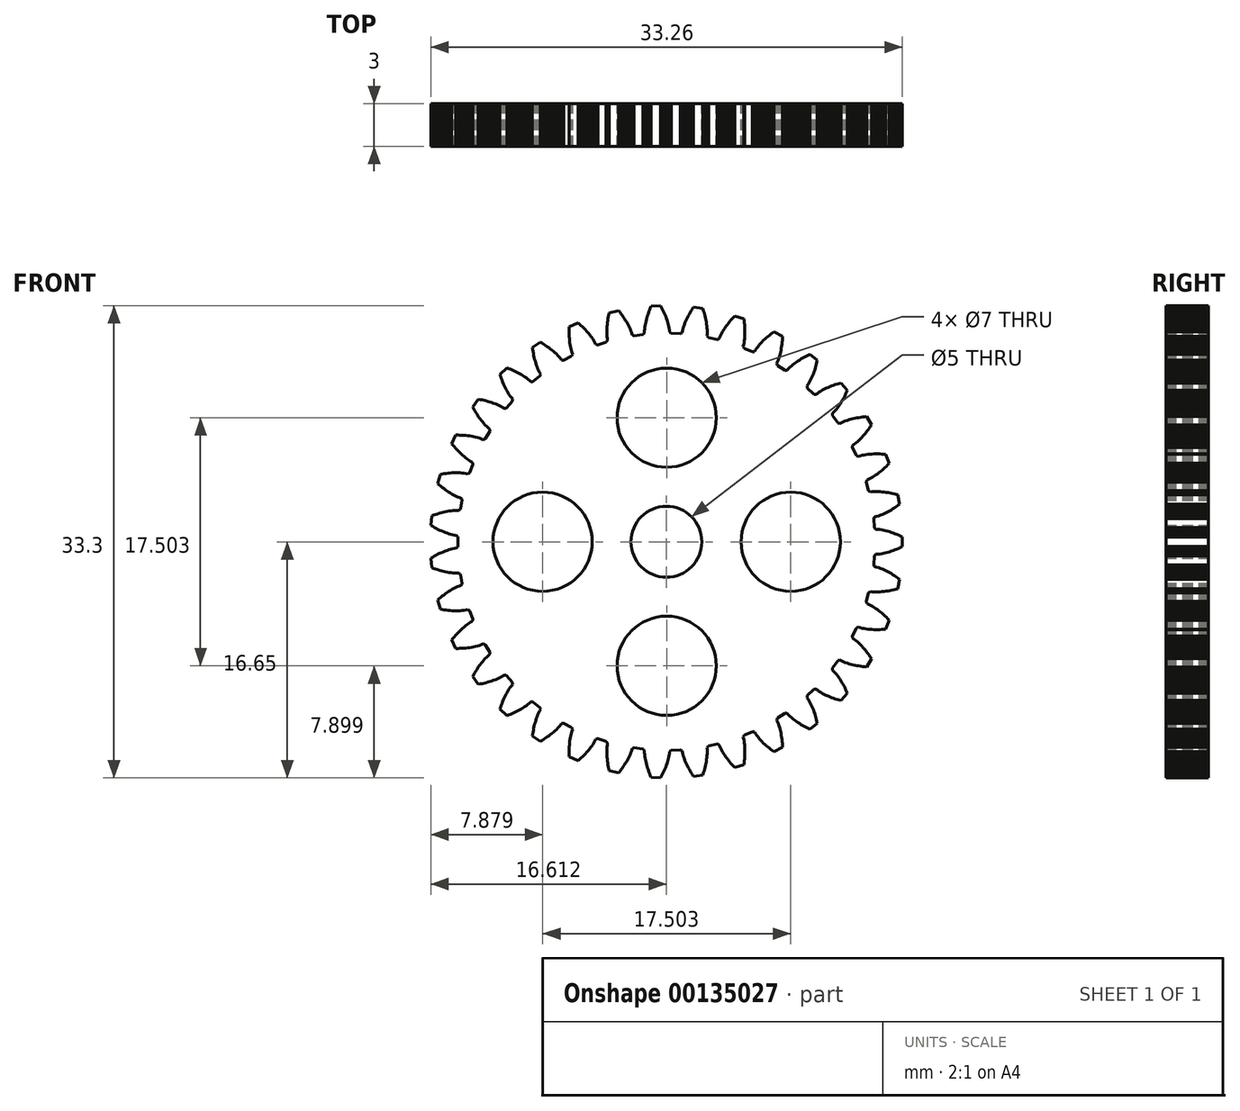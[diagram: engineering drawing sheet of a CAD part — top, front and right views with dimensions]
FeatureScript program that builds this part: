
annotation { "Feature Type Name" : "Feature", "Feature Type Description" : "" }
export const myFeature = defineFeature(function(context is Context, id is Id, definition is map)
    precondition{}
    {
        {
            var Q0;
            Q0=qCreatedBy(makeId("Front.planeOp"),FACE);
            var sketch = newSketch(context, id + "F0", { "sketchPlane" : qUnion([Q0])});
            skLineSegment(sketch, "E0", {"start": v(14.66, -1.01) * mm, "end": v(14.66, -1) * mm});
            skLineSegment(sketch, "E1", {"start": v(14.66, -1) * mm, "end": v(14.67, -0.97) * mm});
            skLineSegment(sketch, "E2", {"start": v(14.67, -0.97) * mm, "end": v(14.7, -0.95) * mm});
            skLineSegment(sketch, "E3", {"start": v(14.7, -0.95) * mm, "end": v(14.72, -0.93) * mm});
            skLineSegment(sketch, "E4", {"start": v(14.72, -0.93) * mm, "end": v(14.76, -0.88) * mm});
            skLineSegment(sketch, "E5", {"start": v(14.76, -0.88) * mm, "end": v(14.9, -0.88) * mm});
            skLineSegment(sketch, "E6", {"start": v(14.9, -0.88) * mm, "end": v(15.04, -0.86) * mm});
            skLineSegment(sketch, "E7", {"start": v(15.04, -0.86) * mm, "end": v(15.17, -0.84) * mm});
            skLineSegment(sketch, "E8", {"start": v(15.17, -0.84) * mm, "end": v(15.31, -0.81) * mm});
            skLineSegment(sketch, "E9", {"start": v(15.31, -0.81) * mm, "end": v(15.45, -0.78) * mm});
            skLineSegment(sketch, "E10", {"start": v(15.45, -0.78) * mm, "end": v(15.58, -0.75) * mm});
            skLineSegment(sketch, "E11", {"start": v(15.58, -0.75) * mm, "end": v(15.72, -0.7) * mm});
            skLineSegment(sketch, "E12", {"start": v(15.72, -0.7) * mm, "end": v(15.85, -0.66) * mm});
            skLineSegment(sketch, "E13", {"start": v(15.85, -0.66) * mm, "end": v(15.98, -0.61) * mm});
            skLineSegment(sketch, "E14", {"start": v(15.98, -0.61) * mm, "end": v(16.12, -0.56) * mm});
            skLineSegment(sketch, "E15", {"start": v(16.12, -0.56) * mm, "end": v(16.25, -0.51) * mm});
            skLineSegment(sketch, "E16", {"start": v(16.25, -0.51) * mm, "end": v(16.38, -0.46) * mm});
            skLineSegment(sketch, "E17", {"start": v(16.38, -0.46) * mm, "end": v(16.5, -0.4) * mm});
            skLineSegment(sketch, "E18", {"start": v(16.5, -0.4) * mm, "end": v(16.63, -0.34) * mm});
            skLineSegment(sketch, "E19", {"start": v(16.63, -0.34) * mm, "end": v(16.63, 0.34) * mm});
            skLineSegment(sketch, "E20", {"start": v(16.63, 0.34) * mm, "end": v(16.5, 0.4) * mm});
            skLineSegment(sketch, "E21", {"start": v(16.5, 0.4) * mm, "end": v(16.38, 0.46) * mm});
            skLineSegment(sketch, "E22", {"start": v(16.38, 0.46) * mm, "end": v(16.25, 0.51) * mm});
            skLineSegment(sketch, "E23", {"start": v(16.25, 0.51) * mm, "end": v(16.12, 0.56) * mm});
            skLineSegment(sketch, "E24", {"start": v(16.12, 0.56) * mm, "end": v(15.98, 0.61) * mm});
            skLineSegment(sketch, "E25", {"start": v(15.98, 0.61) * mm, "end": v(15.85, 0.66) * mm});
            skLineSegment(sketch, "E26", {"start": v(15.85, 0.66) * mm, "end": v(15.72, 0.7) * mm});
            skLineSegment(sketch, "E27", {"start": v(15.72, 0.7) * mm, "end": v(15.58, 0.75) * mm});
            skLineSegment(sketch, "E28", {"start": v(15.58, 0.75) * mm, "end": v(15.45, 0.78) * mm});
            skLineSegment(sketch, "E29", {"start": v(15.45, 0.78) * mm, "end": v(15.31, 0.81) * mm});
            skLineSegment(sketch, "E30", {"start": v(15.31, 0.81) * mm, "end": v(15.17, 0.84) * mm});
            skLineSegment(sketch, "E31", {"start": v(15.17, 0.84) * mm, "end": v(15.04, 0.86) * mm});
            skLineSegment(sketch, "E32", {"start": v(15.04, 0.86) * mm, "end": v(14.9, 0.88) * mm});
            skLineSegment(sketch, "E33", {"start": v(14.9, 0.88) * mm, "end": v(14.76, 0.88) * mm});
            skLineSegment(sketch, "E34", {"start": v(14.76, 0.88) * mm, "end": v(14.72, 0.93) * mm});
            skLineSegment(sketch, "E35", {"start": v(14.72, 0.93) * mm, "end": v(14.7, 0.95) * mm});
            skLineSegment(sketch, "E36", {"start": v(14.7, 0.95) * mm, "end": v(14.67, 0.97) * mm});
            skLineSegment(sketch, "E37", {"start": v(14.67, 0.97) * mm, "end": v(14.66, 1) * mm});
            skLineSegment(sketch, "E38", {"start": v(14.66, 1) * mm, "end": v(14.66, 1.01) * mm});
            skLineSegment(sketch, "E39", {"start": v(14.66, 1.01) * mm, "end": v(14.6, 1.62) * mm});
            skLineSegment(sketch, "E40", {"start": v(14.6, 1.62) * mm, "end": v(14.6, 1.65) * mm});
            skLineSegment(sketch, "E41", {"start": v(14.6, 1.65) * mm, "end": v(14.61, 1.67) * mm});
            skLineSegment(sketch, "E42", {"start": v(14.61, 1.67) * mm, "end": v(14.63, 1.7) * mm});
            skLineSegment(sketch, "E43", {"start": v(14.63, 1.7) * mm, "end": v(14.65, 1.71) * mm});
            skLineSegment(sketch, "E44", {"start": v(14.65, 1.71) * mm, "end": v(14.68, 1.77) * mm});
            skLineSegment(sketch, "E45", {"start": v(14.68, 1.77) * mm, "end": v(14.81, 1.8) * mm});
            skLineSegment(sketch, "E46", {"start": v(14.81, 1.8) * mm, "end": v(14.95, 1.84) * mm});
            skLineSegment(sketch, "E47", {"start": v(14.95, 1.84) * mm, "end": v(15.08, 1.88) * mm});
            skLineSegment(sketch, "E48", {"start": v(15.08, 1.88) * mm, "end": v(15.21, 1.94) * mm});
            skLineSegment(sketch, "E49", {"start": v(15.21, 1.94) * mm, "end": v(15.34, 2) * mm});
            skLineSegment(sketch, "E50", {"start": v(15.34, 2) * mm, "end": v(15.47, 2.05) * mm});
            skLineSegment(sketch, "E51", {"start": v(15.47, 2.05) * mm, "end": v(15.6, 2.12) * mm});
            skLineSegment(sketch, "E52", {"start": v(15.6, 2.12) * mm, "end": v(15.72, 2.18) * mm});
            skLineSegment(sketch, "E53", {"start": v(15.72, 2.18) * mm, "end": v(15.84, 2.25) * mm});
            skLineSegment(sketch, "E54", {"start": v(15.84, 2.25) * mm, "end": v(15.96, 2.33) * mm});
            skLineSegment(sketch, "E55", {"start": v(15.96, 2.33) * mm, "end": v(16.08, 2.4) * mm});
            skLineSegment(sketch, "E56", {"start": v(16.08, 2.4) * mm, "end": v(16.2, 2.48) * mm});
            skLineSegment(sketch, "E57", {"start": v(16.2, 2.48) * mm, "end": v(16.3, 2.56) * mm});
            skLineSegment(sketch, "E58", {"start": v(16.3, 2.56) * mm, "end": v(16.42, 2.64) * mm});
            skLineSegment(sketch, "E59", {"start": v(16.42, 2.64) * mm, "end": v(16.3, 3.3) * mm});
            skLineSegment(sketch, "E60", {"start": v(16.3, 3.3) * mm, "end": v(16.17, 3.34) * mm});
            skLineSegment(sketch, "E61", {"start": v(16.17, 3.34) * mm, "end": v(16.03, 3.38) * mm});
            skLineSegment(sketch, "E62", {"start": v(16.03, 3.38) * mm, "end": v(15.9, 3.4) * mm});
            skLineSegment(sketch, "E63", {"start": v(15.9, 3.4) * mm, "end": v(15.76, 3.44) * mm});
            skLineSegment(sketch, "E64", {"start": v(15.76, 3.44) * mm, "end": v(15.62, 3.46) * mm});
            skLineSegment(sketch, "E65", {"start": v(15.62, 3.46) * mm, "end": v(15.48, 3.48) * mm});
            skLineSegment(sketch, "E66", {"start": v(15.48, 3.48) * mm, "end": v(15.34, 3.5) * mm});
            skLineSegment(sketch, "E67", {"start": v(15.34, 3.5) * mm, "end": v(15.2, 3.52) * mm});
            skLineSegment(sketch, "E68", {"start": v(15.2, 3.52) * mm, "end": v(15.06, 3.53) * mm});
            skLineSegment(sketch, "E69", {"start": v(15.06, 3.53) * mm, "end": v(14.92, 3.54) * mm});
            skLineSegment(sketch, "E70", {"start": v(14.92, 3.54) * mm, "end": v(14.78, 3.54) * mm});
            skLineSegment(sketch, "E71", {"start": v(14.78, 3.54) * mm, "end": v(14.64, 3.54) * mm});
            skLineSegment(sketch, "E72", {"start": v(14.64, 3.54) * mm, "end": v(14.5, 3.53) * mm});
            skLineSegment(sketch, "E73", {"start": v(14.5, 3.53) * mm, "end": v(14.36, 3.5) * mm});
            skLineSegment(sketch, "E74", {"start": v(14.36, 3.5) * mm, "end": v(14.32, 3.55) * mm});
            skLineSegment(sketch, "E75", {"start": v(14.32, 3.55) * mm, "end": v(14.29, 3.56) * mm});
            skLineSegment(sketch, "E76", {"start": v(14.29, 3.56) * mm, "end": v(14.26, 3.58) * mm});
            skLineSegment(sketch, "E77", {"start": v(14.26, 3.58) * mm, "end": v(14.25, 3.6) * mm});
            skLineSegment(sketch, "E78", {"start": v(14.25, 3.6) * mm, "end": v(14.24, 3.62) * mm});
            skLineSegment(sketch, "E79", {"start": v(14.24, 3.62) * mm, "end": v(14.08, 4.2) * mm});
            skLineSegment(sketch, "E80", {"start": v(14.08, 4.2) * mm, "end": v(14.07, 4.23) * mm});
            skLineSegment(sketch, "E81", {"start": v(14.07, 4.23) * mm, "end": v(14.08, 4.25) * mm});
            skLineSegment(sketch, "E82", {"start": v(14.08, 4.25) * mm, "end": v(14.09, 4.28) * mm});
            skLineSegment(sketch, "E83", {"start": v(14.09, 4.28) * mm, "end": v(14.1, 4.3) * mm});
            skLineSegment(sketch, "E84", {"start": v(14.1, 4.3) * mm, "end": v(14.12, 4.36) * mm});
            skLineSegment(sketch, "E85", {"start": v(14.12, 4.36) * mm, "end": v(14.25, 4.42) * mm});
            skLineSegment(sketch, "E86", {"start": v(14.25, 4.42) * mm, "end": v(14.38, 4.48) * mm});
            skLineSegment(sketch, "E87", {"start": v(14.38, 4.48) * mm, "end": v(14.5, 4.55) * mm});
            skLineSegment(sketch, "E88", {"start": v(14.5, 4.55) * mm, "end": v(14.62, 4.62) * mm});
            skLineSegment(sketch, "E89", {"start": v(14.62, 4.62) * mm, "end": v(14.74, 4.7) * mm});
            skLineSegment(sketch, "E90", {"start": v(14.74, 4.7) * mm, "end": v(14.85, 4.78) * mm});
            skLineSegment(sketch, "E91", {"start": v(14.85, 4.78) * mm, "end": v(14.96, 4.87) * mm});
            skLineSegment(sketch, "E92", {"start": v(14.96, 4.87) * mm, "end": v(15.07, 4.96) * mm});
            skLineSegment(sketch, "E93", {"start": v(15.07, 4.96) * mm, "end": v(15.18, 5.05) * mm});
            skLineSegment(sketch, "E94", {"start": v(15.18, 5.05) * mm, "end": v(15.29, 5.14) * mm});
            skLineSegment(sketch, "E95", {"start": v(15.29, 5.14) * mm, "end": v(15.39, 5.24) * mm});
            skLineSegment(sketch, "E96", {"start": v(15.39, 5.24) * mm, "end": v(15.49, 5.33) * mm});
            skLineSegment(sketch, "E97", {"start": v(15.49, 5.33) * mm, "end": v(15.59, 5.43) * mm});
            skLineSegment(sketch, "E98", {"start": v(15.59, 5.43) * mm, "end": v(15.69, 5.53) * mm});
            skLineSegment(sketch, "E99", {"start": v(15.69, 5.53) * mm, "end": v(15.45, 6.17) * mm});
            skLineSegment(sketch, "E100", {"start": v(15.45, 6.17) * mm, "end": v(15.3, 6.18) * mm});
            skLineSegment(sketch, "E101", {"start": v(15.3, 6.18) * mm, "end": v(15.17, 6.19) * mm});
            skLineSegment(sketch, "E102", {"start": v(15.17, 6.19) * mm, "end": v(15.03, 6.2) * mm});
            skLineSegment(sketch, "E103", {"start": v(15.03, 6.2) * mm, "end": v(14.89, 6.2) * mm});
            skLineSegment(sketch, "E104", {"start": v(14.89, 6.2) * mm, "end": v(14.75, 6.2) * mm});
            skLineSegment(sketch, "E105", {"start": v(14.75, 6.2) * mm, "end": v(14.6, 6.2) * mm});
            skLineSegment(sketch, "E106", {"start": v(14.6, 6.2) * mm, "end": v(14.47, 6.2) * mm});
            skLineSegment(sketch, "E107", {"start": v(14.47, 6.2) * mm, "end": v(14.33, 6.18) * mm});
            skLineSegment(sketch, "E108", {"start": v(14.33, 6.18) * mm, "end": v(14.19, 6.17) * mm});
            skLineSegment(sketch, "E109", {"start": v(14.19, 6.17) * mm, "end": v(14.05, 6.15) * mm});
            skLineSegment(sketch, "E110", {"start": v(14.05, 6.15) * mm, "end": v(13.9, 6.13) * mm});
            skLineSegment(sketch, "E111", {"start": v(13.9, 6.13) * mm, "end": v(13.77, 6.1) * mm});
            skLineSegment(sketch, "E112", {"start": v(13.77, 6.1) * mm, "end": v(13.64, 6.06) * mm});
            skLineSegment(sketch, "E113", {"start": v(13.64, 6.06) * mm, "end": v(13.5, 6.02) * mm});
            skLineSegment(sketch, "E114", {"start": v(13.5, 6.02) * mm, "end": v(13.45, 6.05) * mm});
            skLineSegment(sketch, "E115", {"start": v(13.45, 6.05) * mm, "end": v(13.42, 6.06) * mm});
            skLineSegment(sketch, "E116", {"start": v(13.42, 6.06) * mm, "end": v(13.4, 6.07) * mm});
            skLineSegment(sketch, "E117", {"start": v(13.4, 6.07) * mm, "end": v(13.38, 6.09) * mm});
            skLineSegment(sketch, "E118", {"start": v(13.38, 6.09) * mm, "end": v(13.36, 6.1) * mm});
            skLineSegment(sketch, "E119", {"start": v(13.36, 6.1) * mm, "end": v(13.1, 6.66) * mm});
            skLineSegment(sketch, "E120", {"start": v(13.1, 6.66) * mm, "end": v(13.1, 6.68) * mm});
            skLineSegment(sketch, "E121", {"start": v(13.1, 6.68) * mm, "end": v(13.1, 6.7) * mm});
            skLineSegment(sketch, "E122", {"start": v(13.1, 6.7) * mm, "end": v(13.1, 6.73) * mm});
            skLineSegment(sketch, "E123", {"start": v(13.1, 6.73) * mm, "end": v(13.11, 6.76) * mm});
            skLineSegment(sketch, "E124", {"start": v(13.11, 6.76) * mm, "end": v(13.12, 6.82) * mm});
            skLineSegment(sketch, "E125", {"start": v(13.12, 6.82) * mm, "end": v(13.24, 6.9) * mm});
            skLineSegment(sketch, "E126", {"start": v(13.24, 6.9) * mm, "end": v(13.35, 6.98) * mm});
            skLineSegment(sketch, "E127", {"start": v(13.35, 6.98) * mm, "end": v(13.46, 7.07) * mm});
            skLineSegment(sketch, "E128", {"start": v(13.46, 7.07) * mm, "end": v(13.56, 7.16) * mm});
            skLineSegment(sketch, "E129", {"start": v(13.56, 7.16) * mm, "end": v(13.66, 7.26) * mm});
            skLineSegment(sketch, "E130", {"start": v(13.66, 7.26) * mm, "end": v(13.76, 7.36) * mm});
            skLineSegment(sketch, "E131", {"start": v(13.76, 7.36) * mm, "end": v(13.85, 7.47) * mm});
            skLineSegment(sketch, "E132", {"start": v(13.85, 7.47) * mm, "end": v(13.95, 7.57) * mm});
            skLineSegment(sketch, "E133", {"start": v(13.95, 7.57) * mm, "end": v(14.03, 7.68) * mm});
            skLineSegment(sketch, "E134", {"start": v(14.03, 7.68) * mm, "end": v(14.12, 7.8) * mm});
            skLineSegment(sketch, "E135", {"start": v(14.12, 7.8) * mm, "end": v(14.2, 7.9) * mm});
            skLineSegment(sketch, "E136", {"start": v(14.2, 7.9) * mm, "end": v(14.29, 8.02) * mm});
            skLineSegment(sketch, "E137", {"start": v(14.29, 8.02) * mm, "end": v(14.37, 8.13) * mm});
            skLineSegment(sketch, "E138", {"start": v(14.37, 8.13) * mm, "end": v(14.45, 8.25) * mm});
            skLineSegment(sketch, "E139", {"start": v(14.45, 8.25) * mm, "end": v(14.1, 8.83) * mm});
            skLineSegment(sketch, "E140", {"start": v(14.1, 8.83) * mm, "end": v(13.96, 8.82) * mm});
            skLineSegment(sketch, "E141", {"start": v(13.96, 8.82) * mm, "end": v(13.82, 8.8) * mm});
            skLineSegment(sketch, "E142", {"start": v(13.82, 8.8) * mm, "end": v(13.68, 8.78) * mm});
            skLineSegment(sketch, "E143", {"start": v(13.68, 8.78) * mm, "end": v(13.54, 8.76) * mm});
            skLineSegment(sketch, "E144", {"start": v(13.54, 8.76) * mm, "end": v(13.4, 8.74) * mm});
            skLineSegment(sketch, "E145", {"start": v(13.4, 8.74) * mm, "end": v(13.27, 8.7) * mm});
            skLineSegment(sketch, "E146", {"start": v(13.27, 8.7) * mm, "end": v(13.13, 8.68) * mm});
            skLineSegment(sketch, "E147", {"start": v(13.13, 8.68) * mm, "end": v(13, 8.64) * mm});
            skLineSegment(sketch, "E148", {"start": v(13, 8.64) * mm, "end": v(12.86, 8.6) * mm});
            skLineSegment(sketch, "E149", {"start": v(12.86, 8.6) * mm, "end": v(12.72, 8.56) * mm});
            skLineSegment(sketch, "E150", {"start": v(12.72, 8.56) * mm, "end": v(12.6, 8.52) * mm});
            skLineSegment(sketch, "E151", {"start": v(12.6, 8.52) * mm, "end": v(12.46, 8.46) * mm});
            skLineSegment(sketch, "E152", {"start": v(12.46, 8.46) * mm, "end": v(12.33, 8.4) * mm});
            skLineSegment(sketch, "E153", {"start": v(12.33, 8.4) * mm, "end": v(12.21, 8.34) * mm});
            skLineSegment(sketch, "E154", {"start": v(12.21, 8.34) * mm, "end": v(12.15, 8.36) * mm});
            skLineSegment(sketch, "E155", {"start": v(12.15, 8.36) * mm, "end": v(12.12, 8.36) * mm});
            skLineSegment(sketch, "E156", {"start": v(12.12, 8.36) * mm, "end": v(12.1, 8.37) * mm});
            skLineSegment(sketch, "E157", {"start": v(12.1, 8.37) * mm, "end": v(12.07, 8.38) * mm});
            skLineSegment(sketch, "E158", {"start": v(12.07, 8.38) * mm, "end": v(12.06, 8.4) * mm});
            skLineSegment(sketch, "E159", {"start": v(12.06, 8.4) * mm, "end": v(11.7, 8.9) * mm});
            skLineSegment(sketch, "E160", {"start": v(11.7, 8.9) * mm, "end": v(11.69, 8.91) * mm});
            skLineSegment(sketch, "E161", {"start": v(11.69, 8.91) * mm, "end": v(11.68, 8.94) * mm});
            skLineSegment(sketch, "E162", {"start": v(11.68, 8.94) * mm, "end": v(11.69, 8.96) * mm});
            skLineSegment(sketch, "E163", {"start": v(11.69, 8.96) * mm, "end": v(11.7, 9) * mm});
            skLineSegment(sketch, "E164", {"start": v(11.7, 9) * mm, "end": v(11.69, 9.05) * mm});
            skLineSegment(sketch, "E165", {"start": v(11.69, 9.05) * mm, "end": v(11.8, 9.15) * mm});
            skLineSegment(sketch, "E166", {"start": v(11.8, 9.15) * mm, "end": v(11.89, 9.25) * mm});
            skLineSegment(sketch, "E167", {"start": v(11.89, 9.25) * mm, "end": v(11.98, 9.36) * mm});
            skLineSegment(sketch, "E168", {"start": v(11.98, 9.36) * mm, "end": v(12.06, 9.47) * mm});
            skLineSegment(sketch, "E169", {"start": v(12.06, 9.47) * mm, "end": v(12.14, 9.59) * mm});
            skLineSegment(sketch, "E170", {"start": v(12.14, 9.59) * mm, "end": v(12.22, 9.7) * mm});
            skLineSegment(sketch, "E171", {"start": v(12.22, 9.7) * mm, "end": v(12.3, 9.82) * mm});
            skLineSegment(sketch, "E172", {"start": v(12.3, 9.82) * mm, "end": v(12.37, 9.94) * mm});
            skLineSegment(sketch, "E173", {"start": v(12.37, 9.94) * mm, "end": v(12.44, 10.07) * mm});
            skLineSegment(sketch, "E174", {"start": v(12.44, 10.07) * mm, "end": v(12.5, 10.2) * mm});
            skLineSegment(sketch, "E175", {"start": v(12.5, 10.2) * mm, "end": v(12.57, 10.32) * mm});
            skLineSegment(sketch, "E176", {"start": v(12.57, 10.32) * mm, "end": v(12.63, 10.44) * mm});
            skLineSegment(sketch, "E177", {"start": v(12.63, 10.44) * mm, "end": v(12.68, 10.57) * mm});
            skLineSegment(sketch, "E178", {"start": v(12.68, 10.57) * mm, "end": v(12.74, 10.7) * mm});
            skLineSegment(sketch, "E179", {"start": v(12.74, 10.7) * mm, "end": v(12.3, 11.2) * mm});
            skLineSegment(sketch, "E180", {"start": v(12.3, 11.2) * mm, "end": v(12.16, 11.17) * mm});
            skLineSegment(sketch, "E181", {"start": v(12.16, 11.17) * mm, "end": v(12.03, 11.13) * mm});
            skLineSegment(sketch, "E182", {"start": v(12.03, 11.13) * mm, "end": v(11.9, 11.09) * mm});
            skLineSegment(sketch, "E183", {"start": v(11.9, 11.09) * mm, "end": v(11.76, 11.04) * mm});
            skLineSegment(sketch, "E184", {"start": v(11.76, 11.04) * mm, "end": v(11.63, 11) * mm});
            skLineSegment(sketch, "E185", {"start": v(11.63, 11) * mm, "end": v(11.5, 10.94) * mm});
            skLineSegment(sketch, "E186", {"start": v(11.5, 10.94) * mm, "end": v(11.37, 10.89) * mm});
            skLineSegment(sketch, "E187", {"start": v(11.37, 10.89) * mm, "end": v(11.24, 10.83) * mm});
            skLineSegment(sketch, "E188", {"start": v(11.24, 10.83) * mm, "end": v(11.11, 10.77) * mm});
            skLineSegment(sketch, "E189", {"start": v(11.11, 10.77) * mm, "end": v(11, 10.7) * mm});
            skLineSegment(sketch, "E190", {"start": v(11, 10.7) * mm, "end": v(10.87, 10.63) * mm});
            skLineSegment(sketch, "E191", {"start": v(10.87, 10.63) * mm, "end": v(10.75, 10.56) * mm});
            skLineSegment(sketch, "E192", {"start": v(10.75, 10.56) * mm, "end": v(10.63, 10.48) * mm});
            skLineSegment(sketch, "E193", {"start": v(10.63, 10.48) * mm, "end": v(10.53, 10.39) * mm});
            skLineSegment(sketch, "E194", {"start": v(10.53, 10.39) * mm, "end": v(10.47, 10.4) * mm});
            skLineSegment(sketch, "E195", {"start": v(10.47, 10.4) * mm, "end": v(10.43, 10.4) * mm});
            skLineSegment(sketch, "E196", {"start": v(10.43, 10.4) * mm, "end": v(10.4, 10.4) * mm});
            skLineSegment(sketch, "E197", {"start": v(10.4, 10.4) * mm, "end": v(10.38, 10.4) * mm});
            skLineSegment(sketch, "E198", {"start": v(10.38, 10.4) * mm, "end": v(10.37, 10.42) * mm});
            skLineSegment(sketch, "E199", {"start": v(10.37, 10.42) * mm, "end": v(9.92, 10.84) * mm});
            skLineSegment(sketch, "E200", {"start": v(9.92, 10.84) * mm, "end": v(9.9, 10.86) * mm});
            skLineSegment(sketch, "E201", {"start": v(9.9, 10.86) * mm, "end": v(9.9, 10.88) * mm});
            skLineSegment(sketch, "E202", {"start": v(9.9, 10.88) * mm, "end": v(9.9, 10.9) * mm});
            skLineSegment(sketch, "E203", {"start": v(9.9, 10.9) * mm, "end": v(9.9, 10.94) * mm});
            skLineSegment(sketch, "E204", {"start": v(9.9, 10.94) * mm, "end": v(9.88, 11) * mm});
            skLineSegment(sketch, "E205", {"start": v(9.88, 11) * mm, "end": v(9.97, 11.11) * mm});
            skLineSegment(sketch, "E206", {"start": v(9.97, 11.11) * mm, "end": v(10.04, 11.23) * mm});
            skLineSegment(sketch, "E207", {"start": v(10.04, 11.23) * mm, "end": v(10.11, 11.35) * mm});
            skLineSegment(sketch, "E208", {"start": v(10.11, 11.35) * mm, "end": v(10.18, 11.48) * mm});
            skLineSegment(sketch, "E209", {"start": v(10.18, 11.48) * mm, "end": v(10.24, 11.6) * mm});
            skLineSegment(sketch, "E210", {"start": v(10.24, 11.6) * mm, "end": v(10.3, 11.73) * mm});
            skLineSegment(sketch, "E211", {"start": v(10.3, 11.73) * mm, "end": v(10.35, 11.86) * mm});
            skLineSegment(sketch, "E212", {"start": v(10.35, 11.86) * mm, "end": v(10.4, 12) * mm});
            skLineSegment(sketch, "E213", {"start": v(10.4, 12) * mm, "end": v(10.44, 12.13) * mm});
            skLineSegment(sketch, "E214", {"start": v(10.44, 12.13) * mm, "end": v(10.48, 12.26) * mm});
            skLineSegment(sketch, "E215", {"start": v(10.48, 12.26) * mm, "end": v(10.52, 12.4) * mm});
            skLineSegment(sketch, "E216", {"start": v(10.52, 12.4) * mm, "end": v(10.56, 12.53) * mm});
            skLineSegment(sketch, "E217", {"start": v(10.56, 12.53) * mm, "end": v(10.6, 12.67) * mm});
            skLineSegment(sketch, "E218", {"start": v(10.6, 12.67) * mm, "end": v(10.62, 12.8) * mm});
            skLineSegment(sketch, "E219", {"start": v(10.62, 12.8) * mm, "end": v(10.1, 13.23) * mm});
            skLineSegment(sketch, "E220", {"start": v(10.1, 13.23) * mm, "end": v(9.97, 13.16) * mm});
            skLineSegment(sketch, "E221", {"start": v(9.97, 13.16) * mm, "end": v(9.85, 13.1) * mm});
            skLineSegment(sketch, "E222", {"start": v(9.85, 13.1) * mm, "end": v(9.72, 13.03) * mm});
            skLineSegment(sketch, "E223", {"start": v(9.72, 13.03) * mm, "end": v(9.6, 12.97) * mm});
            skLineSegment(sketch, "E224", {"start": v(9.6, 12.97) * mm, "end": v(9.48, 12.9) * mm});
            skLineSegment(sketch, "E225", {"start": v(9.48, 12.9) * mm, "end": v(9.36, 12.82) * mm});
            skLineSegment(sketch, "E226", {"start": v(9.36, 12.82) * mm, "end": v(9.24, 12.74) * mm});
            skLineSegment(sketch, "E227", {"start": v(9.24, 12.74) * mm, "end": v(9.13, 12.66) * mm});
            skLineSegment(sketch, "E228", {"start": v(9.13, 12.66) * mm, "end": v(9.01, 12.58) * mm});
            skLineSegment(sketch, "E229", {"start": v(9.01, 12.58) * mm, "end": v(8.9, 12.5) * mm});
            skLineSegment(sketch, "E230", {"start": v(8.9, 12.5) * mm, "end": v(8.8, 12.4) * mm});
            skLineSegment(sketch, "E231", {"start": v(8.8, 12.4) * mm, "end": v(8.7, 12.3) * mm});
            skLineSegment(sketch, "E232", {"start": v(8.7, 12.3) * mm, "end": v(8.6, 12.2) * mm});
            skLineSegment(sketch, "E233", {"start": v(8.6, 12.2) * mm, "end": v(8.5, 12.1) * mm});
            skLineSegment(sketch, "E234", {"start": v(8.5, 12.1) * mm, "end": v(8.44, 12.1) * mm});
            skLineSegment(sketch, "E235", {"start": v(8.44, 12.1) * mm, "end": v(8.41, 12.1) * mm});
            skLineSegment(sketch, "E236", {"start": v(8.41, 12.1) * mm, "end": v(8.38, 12.1) * mm});
            skLineSegment(sketch, "E237", {"start": v(8.38, 12.1) * mm, "end": v(8.36, 12.1) * mm});
            skLineSegment(sketch, "E238", {"start": v(8.36, 12.1) * mm, "end": v(8.34, 12.1) * mm});
            skLineSegment(sketch, "E239", {"start": v(8.34, 12.1) * mm, "end": v(7.83, 12.44) * mm});
            skLineSegment(sketch, "E240", {"start": v(7.83, 12.44) * mm, "end": v(7.81, 12.46) * mm});
            skLineSegment(sketch, "E241", {"start": v(7.81, 12.46) * mm, "end": v(7.8, 12.48) * mm});
            skLineSegment(sketch, "E242", {"start": v(7.8, 12.48) * mm, "end": v(7.8, 12.5) * mm});
            skLineSegment(sketch, "E243", {"start": v(7.8, 12.5) * mm, "end": v(7.79, 12.54) * mm});
            skLineSegment(sketch, "E244", {"start": v(7.79, 12.54) * mm, "end": v(7.76, 12.6) * mm});
            skLineSegment(sketch, "E245", {"start": v(7.76, 12.6) * mm, "end": v(7.82, 12.72) * mm});
            skLineSegment(sketch, "E246", {"start": v(7.82, 12.72) * mm, "end": v(7.88, 12.85) * mm});
            skLineSegment(sketch, "E247", {"start": v(7.88, 12.85) * mm, "end": v(7.92, 12.98) * mm});
            skLineSegment(sketch, "E248", {"start": v(7.92, 12.98) * mm, "end": v(7.96, 13.11) * mm});
            skLineSegment(sketch, "E249", {"start": v(7.96, 13.11) * mm, "end": v(8, 13.25) * mm});
            skLineSegment(sketch, "E250", {"start": v(8, 13.25) * mm, "end": v(8.03, 13.39) * mm});
            skLineSegment(sketch, "E251", {"start": v(8.03, 13.39) * mm, "end": v(8.06, 13.52) * mm});
            skLineSegment(sketch, "E252", {"start": v(8.06, 13.52) * mm, "end": v(8.08, 13.66) * mm});
            skLineSegment(sketch, "E253", {"start": v(8.08, 13.66) * mm, "end": v(8.1, 13.8) * mm});
            skLineSegment(sketch, "E254", {"start": v(8.1, 13.8) * mm, "end": v(8.12, 13.94) * mm});
            skLineSegment(sketch, "E255", {"start": v(8.12, 13.94) * mm, "end": v(8.14, 14.08) * mm});
            skLineSegment(sketch, "E256", {"start": v(8.14, 14.08) * mm, "end": v(8.15, 14.22) * mm});
            skLineSegment(sketch, "E257", {"start": v(8.15, 14.22) * mm, "end": v(8.16, 14.36) * mm});
            skLineSegment(sketch, "E258", {"start": v(8.16, 14.36) * mm, "end": v(8.17, 14.5) * mm});
            skLineSegment(sketch, "E259", {"start": v(8.17, 14.5) * mm, "end": v(7.57, 14.82) * mm});
            skLineSegment(sketch, "E260", {"start": v(7.57, 14.82) * mm, "end": v(7.46, 14.74) * mm});
            skLineSegment(sketch, "E261", {"start": v(7.46, 14.74) * mm, "end": v(7.35, 14.65) * mm});
            skLineSegment(sketch, "E262", {"start": v(7.35, 14.65) * mm, "end": v(7.24, 14.56) * mm});
            skLineSegment(sketch, "E263", {"start": v(7.24, 14.56) * mm, "end": v(7.13, 14.48) * mm});
            skLineSegment(sketch, "E264", {"start": v(7.13, 14.48) * mm, "end": v(7.02, 14.38) * mm});
            skLineSegment(sketch, "E265", {"start": v(7.02, 14.38) * mm, "end": v(6.92, 14.29) * mm});
            skLineSegment(sketch, "E266", {"start": v(6.92, 14.29) * mm, "end": v(6.82, 14.2) * mm});
            skLineSegment(sketch, "E267", {"start": v(6.82, 14.2) * mm, "end": v(6.72, 14.1) * mm});
            skLineSegment(sketch, "E268", {"start": v(6.72, 14.1) * mm, "end": v(6.62, 14) * mm});
            skLineSegment(sketch, "E269", {"start": v(6.62, 14) * mm, "end": v(6.53, 13.89) * mm});
            skLineSegment(sketch, "E270", {"start": v(6.53, 13.89) * mm, "end": v(6.44, 13.78) * mm});
            skLineSegment(sketch, "E271", {"start": v(6.44, 13.78) * mm, "end": v(6.35, 13.67) * mm});
            skLineSegment(sketch, "E272", {"start": v(6.35, 13.67) * mm, "end": v(6.27, 13.55) * mm});
            skLineSegment(sketch, "E273", {"start": v(6.27, 13.55) * mm, "end": v(6.2, 13.43) * mm});
            skLineSegment(sketch, "E274", {"start": v(6.2, 13.43) * mm, "end": v(6.14, 13.42) * mm});
            skLineSegment(sketch, "E275", {"start": v(6.14, 13.42) * mm, "end": v(6.12, 13.4) * mm});
            skLineSegment(sketch, "E276", {"start": v(6.12, 13.4) * mm, "end": v(6.09, 13.4) * mm});
            skLineSegment(sketch, "E277", {"start": v(6.09, 13.4) * mm, "end": v(6.06, 13.4) * mm});
            skLineSegment(sketch, "E278", {"start": v(6.06, 13.4) * mm, "end": v(6.04, 13.4) * mm});
            skLineSegment(sketch, "E279", {"start": v(6.04, 13.4) * mm, "end": v(5.48, 13.64) * mm});
            skLineSegment(sketch, "E280", {"start": v(5.48, 13.64) * mm, "end": v(5.46, 13.65) * mm});
            skLineSegment(sketch, "E281", {"start": v(5.46, 13.65) * mm, "end": v(5.44, 13.67) * mm});
            skLineSegment(sketch, "E282", {"start": v(5.44, 13.67) * mm, "end": v(5.43, 13.7) * mm});
            skLineSegment(sketch, "E283", {"start": v(5.43, 13.7) * mm, "end": v(5.42, 13.73) * mm});
            skLineSegment(sketch, "E284", {"start": v(5.42, 13.73) * mm, "end": v(5.39, 13.78) * mm});
            skLineSegment(sketch, "E285", {"start": v(5.39, 13.78) * mm, "end": v(5.43, 13.91) * mm});
            skLineSegment(sketch, "E286", {"start": v(5.43, 13.91) * mm, "end": v(5.46, 14.05) * mm});
            skLineSegment(sketch, "E287", {"start": v(5.46, 14.05) * mm, "end": v(5.48, 14.19) * mm});
            skLineSegment(sketch, "E288", {"start": v(5.48, 14.19) * mm, "end": v(5.5, 14.33) * mm});
            skLineSegment(sketch, "E289", {"start": v(5.5, 14.33) * mm, "end": v(5.5, 14.47) * mm});
            skLineSegment(sketch, "E290", {"start": v(5.5, 14.47) * mm, "end": v(5.51, 14.6) * mm});
            skLineSegment(sketch, "E291", {"start": v(5.51, 14.6) * mm, "end": v(5.52, 14.75) * mm});
            skLineSegment(sketch, "E292", {"start": v(5.52, 14.75) * mm, "end": v(5.52, 14.89) * mm});
            skLineSegment(sketch, "E293", {"start": v(5.52, 14.89) * mm, "end": v(5.51, 15.03) * mm});
            skLineSegment(sketch, "E294", {"start": v(5.51, 15.03) * mm, "end": v(5.5, 15.17) * mm});
            skLineSegment(sketch, "E295", {"start": v(5.5, 15.17) * mm, "end": v(5.5, 15.31) * mm});
            skLineSegment(sketch, "E296", {"start": v(5.5, 15.31) * mm, "end": v(5.48, 15.45) * mm});
            skLineSegment(sketch, "E297", {"start": v(5.48, 15.45) * mm, "end": v(5.47, 15.59) * mm});
            skLineSegment(sketch, "E298", {"start": v(5.47, 15.59) * mm, "end": v(5.45, 15.73) * mm});
            skLineSegment(sketch, "E299", {"start": v(5.45, 15.73) * mm, "end": v(4.8, 15.94) * mm});
            skLineSegment(sketch, "E300", {"start": v(4.8, 15.94) * mm, "end": v(4.7, 15.84) * mm});
            skLineSegment(sketch, "E301", {"start": v(4.7, 15.84) * mm, "end": v(4.61, 15.73) * mm});
            skLineSegment(sketch, "E302", {"start": v(4.61, 15.73) * mm, "end": v(4.52, 15.63) * mm});
            skLineSegment(sketch, "E303", {"start": v(4.52, 15.63) * mm, "end": v(4.43, 15.52) * mm});
            skLineSegment(sketch, "E304", {"start": v(4.43, 15.52) * mm, "end": v(4.34, 15.4) * mm});
            skLineSegment(sketch, "E305", {"start": v(4.34, 15.4) * mm, "end": v(4.26, 15.3) * mm});
            skLineSegment(sketch, "E306", {"start": v(4.26, 15.3) * mm, "end": v(4.17, 15.19) * mm});
            skLineSegment(sketch, "E307", {"start": v(4.17, 15.19) * mm, "end": v(4.1, 15.07) * mm});
            skLineSegment(sketch, "E308", {"start": v(4.1, 15.07) * mm, "end": v(4.02, 14.95) * mm});
            skLineSegment(sketch, "E309", {"start": v(4.02, 14.95) * mm, "end": v(3.94, 14.83) * mm});
            skLineSegment(sketch, "E310", {"start": v(3.94, 14.83) * mm, "end": v(3.88, 14.7) * mm});
            skLineSegment(sketch, "E311", {"start": v(3.88, 14.7) * mm, "end": v(3.81, 14.58) * mm});
            skLineSegment(sketch, "E312", {"start": v(3.81, 14.58) * mm, "end": v(3.75, 14.46) * mm});
            skLineSegment(sketch, "E313", {"start": v(3.75, 14.46) * mm, "end": v(3.7, 14.32) * mm});
            skLineSegment(sketch, "E314", {"start": v(3.7, 14.32) * mm, "end": v(3.65, 14.3) * mm});
            skLineSegment(sketch, "E315", {"start": v(3.65, 14.3) * mm, "end": v(3.62, 14.29) * mm});
            skLineSegment(sketch, "E316", {"start": v(3.62, 14.29) * mm, "end": v(3.6, 14.27) * mm});
            skLineSegment(sketch, "E317", {"start": v(3.6, 14.27) * mm, "end": v(3.57, 14.27) * mm});
            skLineSegment(sketch, "E318", {"start": v(3.57, 14.27) * mm, "end": v(3.55, 14.27) * mm});
            skLineSegment(sketch, "E319", {"start": v(3.55, 14.27) * mm, "end": v(2.95, 14.4) * mm});
            skLineSegment(sketch, "E320", {"start": v(2.95, 14.4) * mm, "end": v(2.93, 14.41) * mm});
            skLineSegment(sketch, "E321", {"start": v(2.93, 14.41) * mm, "end": v(2.92, 14.43) * mm});
            skLineSegment(sketch, "E322", {"start": v(2.92, 14.43) * mm, "end": v(2.9, 14.45) * mm});
            skLineSegment(sketch, "E323", {"start": v(2.9, 14.45) * mm, "end": v(2.88, 14.48) * mm});
            skLineSegment(sketch, "E324", {"start": v(2.88, 14.48) * mm, "end": v(2.84, 14.52) * mm});
            skLineSegment(sketch, "E325", {"start": v(2.84, 14.52) * mm, "end": v(2.86, 14.66) * mm});
            skLineSegment(sketch, "E326", {"start": v(2.86, 14.66) * mm, "end": v(2.86, 14.8) * mm});
            skLineSegment(sketch, "E327", {"start": v(2.86, 14.8) * mm, "end": v(2.86, 14.94) * mm});
            skLineSegment(sketch, "E328", {"start": v(2.86, 14.94) * mm, "end": v(2.85, 15.08) * mm});
            skLineSegment(sketch, "E329", {"start": v(2.85, 15.08) * mm, "end": v(2.83, 15.22) * mm});
            skLineSegment(sketch, "E330", {"start": v(2.83, 15.22) * mm, "end": v(2.82, 15.36) * mm});
            skLineSegment(sketch, "E331", {"start": v(2.82, 15.36) * mm, "end": v(2.8, 15.5) * mm});
            skLineSegment(sketch, "E332", {"start": v(2.8, 15.5) * mm, "end": v(2.77, 15.64) * mm});
            skLineSegment(sketch, "E333", {"start": v(2.77, 15.64) * mm, "end": v(2.74, 15.78) * mm});
            skLineSegment(sketch, "E334", {"start": v(2.74, 15.78) * mm, "end": v(2.7, 15.91) * mm});
            skLineSegment(sketch, "E335", {"start": v(2.7, 15.91) * mm, "end": v(2.67, 16.05) * mm});
            skLineSegment(sketch, "E336", {"start": v(2.67, 16.05) * mm, "end": v(2.63, 16.18) * mm});
            skLineSegment(sketch, "E337", {"start": v(2.63, 16.18) * mm, "end": v(2.6, 16.32) * mm});
            skLineSegment(sketch, "E338", {"start": v(2.6, 16.32) * mm, "end": v(2.55, 16.45) * mm});
            skLineSegment(sketch, "E339", {"start": v(2.55, 16.45) * mm, "end": v(1.88, 16.54) * mm});
            skLineSegment(sketch, "E340", {"start": v(1.88, 16.54) * mm, "end": v(1.8, 16.43) * mm});
            skLineSegment(sketch, "E341", {"start": v(1.8, 16.43) * mm, "end": v(1.73, 16.3) * mm});
            skLineSegment(sketch, "E342", {"start": v(1.73, 16.3) * mm, "end": v(1.66, 16.19) * mm});
            skLineSegment(sketch, "E343", {"start": v(1.66, 16.19) * mm, "end": v(1.59, 16.06) * mm});
            skLineSegment(sketch, "E344", {"start": v(1.59, 16.06) * mm, "end": v(1.52, 15.94) * mm});
            skLineSegment(sketch, "E345", {"start": v(1.52, 15.94) * mm, "end": v(1.46, 15.82) * mm});
            skLineSegment(sketch, "E346", {"start": v(1.46, 15.82) * mm, "end": v(1.4, 15.69) * mm});
            skLineSegment(sketch, "E347", {"start": v(1.4, 15.69) * mm, "end": v(1.34, 15.56) * mm});
            skLineSegment(sketch, "E348", {"start": v(1.34, 15.56) * mm, "end": v(1.28, 15.43) * mm});
            skLineSegment(sketch, "E349", {"start": v(1.28, 15.43) * mm, "end": v(1.23, 15.3) * mm});
            skLineSegment(sketch, "E350", {"start": v(1.23, 15.3) * mm, "end": v(1.19, 15.17) * mm});
            skLineSegment(sketch, "E351", {"start": v(1.19, 15.17) * mm, "end": v(1.15, 15.03) * mm});
            skLineSegment(sketch, "E352", {"start": v(1.15, 15.03) * mm, "end": v(1.11, 14.9) * mm});
            skLineSegment(sketch, "E353", {"start": v(1.11, 14.9) * mm, "end": v(1.09, 14.76) * mm});
            skLineSegment(sketch, "E354", {"start": v(1.09, 14.76) * mm, "end": v(1.03, 14.73) * mm});
            skLineSegment(sketch, "E355", {"start": v(1.03, 14.73) * mm, "end": v(1.01, 14.7) * mm});
            skLineSegment(sketch, "E356", {"start": v(1.01, 14.7) * mm, "end": v(1, 14.69) * mm});
            skLineSegment(sketch, "E357", {"start": v(1, 14.69) * mm, "end": v(0.97, 14.68) * mm});
            skLineSegment(sketch, "E358", {"start": v(0.97, 14.68) * mm, "end": v(0.95, 14.68) * mm});
            skLineSegment(sketch, "E359", {"start": v(0.95, 14.68) * mm, "end": v(0.33, 14.7) * mm});
            skLineSegment(sketch, "E360", {"start": v(0.33, 14.7) * mm, "end": v(0.31, 14.7) * mm});
            skLineSegment(sketch, "E361", {"start": v(0.31, 14.7) * mm, "end": v(0.3, 14.72) * mm});
            skLineSegment(sketch, "E362", {"start": v(0.3, 14.72) * mm, "end": v(0.27, 14.74) * mm});
            skLineSegment(sketch, "E363", {"start": v(0.27, 14.74) * mm, "end": v(0.25, 14.77) * mm});
            skLineSegment(sketch, "E364", {"start": v(0.25, 14.77) * mm, "end": v(0.2, 14.8) * mm});
            skLineSegment(sketch, "E365", {"start": v(0.2, 14.8) * mm, "end": v(0.2, 14.94) * mm});
            skLineSegment(sketch, "E366", {"start": v(0.2, 14.94) * mm, "end": v(0.17, 15.08) * mm});
            skLineSegment(sketch, "E367", {"start": v(0.17, 15.08) * mm, "end": v(0.14, 15.21) * mm});
            skLineSegment(sketch, "E368", {"start": v(0.14, 15.21) * mm, "end": v(0.1, 15.35) * mm});
            skLineSegment(sketch, "E369", {"start": v(0.1, 15.35) * mm, "end": v(0.07, 15.49) * mm});
            skLineSegment(sketch, "E370", {"start": v(0.07, 15.49) * mm, "end": v(0.03, 15.62) * mm});
            skLineSegment(sketch, "E371", {"start": v(0.03, 15.62) * mm, "end": v(-0.02, 15.75) * mm});
            skLineSegment(sketch, "E372", {"start": v(-0.02, 15.75) * mm, "end": v(-0.07, 15.88) * mm});
            skLineSegment(sketch, "E373", {"start": v(-0.07, 15.88) * mm, "end": v(-0.12, 16.01) * mm});
            skLineSegment(sketch, "E374", {"start": v(-0.12, 16.01) * mm, "end": v(-0.18, 16.14) * mm});
            skLineSegment(sketch, "E375", {"start": v(-0.18, 16.14) * mm, "end": v(-0.24, 16.27) * mm});
            skLineSegment(sketch, "E376", {"start": v(-0.24, 16.27) * mm, "end": v(-0.3, 16.4) * mm});
            skLineSegment(sketch, "E377", {"start": v(-0.3, 16.4) * mm, "end": v(-0.36, 16.52) * mm});
            skLineSegment(sketch, "E378", {"start": v(-0.36, 16.52) * mm, "end": v(-0.43, 16.65) * mm});
            skLineSegment(sketch, "E379", {"start": v(-0.43, 16.65) * mm, "end": v(-1.1, 16.62) * mm});
            skLineSegment(sketch, "E380", {"start": v(-1.1, 16.62) * mm, "end": v(-1.16, 16.49) * mm});
            skLineSegment(sketch, "E381", {"start": v(-1.16, 16.49) * mm, "end": v(-1.2, 16.36) * mm});
            skLineSegment(sketch, "E382", {"start": v(-1.2, 16.36) * mm, "end": v(-1.26, 16.23) * mm});
            skLineSegment(sketch, "E383", {"start": v(-1.26, 16.23) * mm, "end": v(-1.3, 16.1) * mm});
            skLineSegment(sketch, "E384", {"start": v(-1.3, 16.1) * mm, "end": v(-1.35, 15.96) * mm});
            skLineSegment(sketch, "E385", {"start": v(-1.35, 15.96) * mm, "end": v(-1.4, 15.82) * mm});
            skLineSegment(sketch, "E386", {"start": v(-1.4, 15.82) * mm, "end": v(-1.43, 15.69) * mm});
            skLineSegment(sketch, "E387", {"start": v(-1.43, 15.69) * mm, "end": v(-1.46, 15.55) * mm});
            skLineSegment(sketch, "E388", {"start": v(-1.46, 15.55) * mm, "end": v(-1.5, 15.42) * mm});
            skLineSegment(sketch, "E389", {"start": v(-1.5, 15.42) * mm, "end": v(-1.52, 15.28) * mm});
            skLineSegment(sketch, "E390", {"start": v(-1.52, 15.28) * mm, "end": v(-1.54, 15.14) * mm});
            skLineSegment(sketch, "E391", {"start": v(-1.54, 15.14) * mm, "end": v(-1.56, 15) * mm});
            skLineSegment(sketch, "E392", {"start": v(-1.56, 15) * mm, "end": v(-1.57, 14.86) * mm});
            skLineSegment(sketch, "E393", {"start": v(-1.57, 14.86) * mm, "end": v(-1.56, 14.72) * mm});
            skLineSegment(sketch, "E394", {"start": v(-1.56, 14.72) * mm, "end": v(-1.61, 14.68) * mm});
            skLineSegment(sketch, "E395", {"start": v(-1.61, 14.68) * mm, "end": v(-1.63, 14.65) * mm});
            skLineSegment(sketch, "E396", {"start": v(-1.63, 14.65) * mm, "end": v(-1.65, 14.63) * mm});
            skLineSegment(sketch, "E397", {"start": v(-1.65, 14.63) * mm, "end": v(-1.67, 14.62) * mm});
            skLineSegment(sketch, "E398", {"start": v(-1.67, 14.62) * mm, "end": v(-1.69, 14.61) * mm});
            skLineSegment(sketch, "E399", {"start": v(-1.69, 14.61) * mm, "end": v(-2.3, 14.53) * mm});
            skLineSegment(sketch, "E400", {"start": v(-2.3, 14.53) * mm, "end": v(-2.32, 14.53) * mm});
            skLineSegment(sketch, "E401", {"start": v(-2.32, 14.53) * mm, "end": v(-2.34, 14.54) * mm});
            skLineSegment(sketch, "E402", {"start": v(-2.34, 14.54) * mm, "end": v(-2.36, 14.55) * mm});
            skLineSegment(sketch, "E403", {"start": v(-2.36, 14.55) * mm, "end": v(-2.39, 14.58) * mm});
            skLineSegment(sketch, "E404", {"start": v(-2.39, 14.58) * mm, "end": v(-2.44, 14.6) * mm});
            skLineSegment(sketch, "E405", {"start": v(-2.44, 14.6) * mm, "end": v(-2.48, 14.74) * mm});
            skLineSegment(sketch, "E406", {"start": v(-2.48, 14.74) * mm, "end": v(-2.53, 14.87) * mm});
            skLineSegment(sketch, "E407", {"start": v(-2.53, 14.87) * mm, "end": v(-2.58, 15) * mm});
            skLineSegment(sketch, "E408", {"start": v(-2.58, 15) * mm, "end": v(-2.64, 15.13) * mm});
            skLineSegment(sketch, "E409", {"start": v(-2.64, 15.13) * mm, "end": v(-2.7, 15.25) * mm});
            skLineSegment(sketch, "E410", {"start": v(-2.7, 15.25) * mm, "end": v(-2.76, 15.38) * mm});
            skLineSegment(sketch, "E411", {"start": v(-2.76, 15.38) * mm, "end": v(-2.83, 15.5) * mm});
            skLineSegment(sketch, "E412", {"start": v(-2.83, 15.5) * mm, "end": v(-2.9, 15.62) * mm});
            skLineSegment(sketch, "E413", {"start": v(-2.9, 15.62) * mm, "end": v(-2.98, 15.74) * mm});
            skLineSegment(sketch, "E414", {"start": v(-2.98, 15.74) * mm, "end": v(-3.06, 15.86) * mm});
            skLineSegment(sketch, "E415", {"start": v(-3.06, 15.86) * mm, "end": v(-3.14, 15.97) * mm});
            skLineSegment(sketch, "E416", {"start": v(-3.14, 15.97) * mm, "end": v(-3.22, 16.08) * mm});
            skLineSegment(sketch, "E417", {"start": v(-3.22, 16.08) * mm, "end": v(-3.3, 16.2) * mm});
            skLineSegment(sketch, "E418", {"start": v(-3.3, 16.2) * mm, "end": v(-3.4, 16.3) * mm});
            skLineSegment(sketch, "E419", {"start": v(-3.4, 16.3) * mm, "end": v(-4.05, 16.16) * mm});
            skLineSegment(sketch, "E420", {"start": v(-4.05, 16.16) * mm, "end": v(-4.08, 16.02) * mm});
            skLineSegment(sketch, "E421", {"start": v(-4.08, 16.02) * mm, "end": v(-4.11, 15.88) * mm});
            skLineSegment(sketch, "E422", {"start": v(-4.11, 15.88) * mm, "end": v(-4.14, 15.74) * mm});
            skLineSegment(sketch, "E423", {"start": v(-4.14, 15.74) * mm, "end": v(-4.16, 15.6) * mm});
            skLineSegment(sketch, "E424", {"start": v(-4.16, 15.6) * mm, "end": v(-4.18, 15.47) * mm});
            skLineSegment(sketch, "E425", {"start": v(-4.18, 15.47) * mm, "end": v(-4.2, 15.33) * mm});
            skLineSegment(sketch, "E426", {"start": v(-4.2, 15.33) * mm, "end": v(-4.2, 15.19) * mm});
            skLineSegment(sketch, "E427", {"start": v(-4.2, 15.19) * mm, "end": v(-4.22, 15.05) * mm});
            skLineSegment(sketch, "E428", {"start": v(-4.22, 15.05) * mm, "end": v(-4.22, 14.9) * mm});
            skLineSegment(sketch, "E429", {"start": v(-4.22, 14.9) * mm, "end": v(-4.22, 14.76) * mm});
            skLineSegment(sketch, "E430", {"start": v(-4.22, 14.76) * mm, "end": v(-4.22, 14.62) * mm});
            skLineSegment(sketch, "E431", {"start": v(-4.22, 14.62) * mm, "end": v(-4.21, 14.48) * mm});
            skLineSegment(sketch, "E432", {"start": v(-4.21, 14.48) * mm, "end": v(-4.2, 14.34) * mm});
            skLineSegment(sketch, "E433", {"start": v(-4.2, 14.34) * mm, "end": v(-4.17, 14.2) * mm});
            skLineSegment(sketch, "E434", {"start": v(-4.17, 14.2) * mm, "end": v(-4.2, 14.16) * mm});
            skLineSegment(sketch, "E435", {"start": v(-4.2, 14.16) * mm, "end": v(-4.22, 14.13) * mm});
            skLineSegment(sketch, "E436", {"start": v(-4.22, 14.13) * mm, "end": v(-4.23, 14.1) * mm});
            skLineSegment(sketch, "E437", {"start": v(-4.23, 14.1) * mm, "end": v(-4.25, 14.1) * mm});
            skLineSegment(sketch, "E438", {"start": v(-4.25, 14.1) * mm, "end": v(-4.27, 14.08) * mm});
            skLineSegment(sketch, "E439", {"start": v(-4.27, 14.08) * mm, "end": v(-4.85, 13.9) * mm});
            skLineSegment(sketch, "E440", {"start": v(-4.85, 13.9) * mm, "end": v(-4.88, 13.89) * mm});
            skLineSegment(sketch, "E441", {"start": v(-4.88, 13.89) * mm, "end": v(-4.9, 13.9) * mm});
            skLineSegment(sketch, "E442", {"start": v(-4.9, 13.9) * mm, "end": v(-4.93, 13.9) * mm});
            skLineSegment(sketch, "E443", {"start": v(-4.93, 13.9) * mm, "end": v(-4.95, 13.92) * mm});
            skLineSegment(sketch, "E444", {"start": v(-4.95, 13.92) * mm, "end": v(-5.01, 13.93) * mm});
            skLineSegment(sketch, "E445", {"start": v(-5.01, 13.93) * mm, "end": v(-5.07, 14.06) * mm});
            skLineSegment(sketch, "E446", {"start": v(-5.07, 14.06) * mm, "end": v(-5.14, 14.18) * mm});
            skLineSegment(sketch, "E447", {"start": v(-5.14, 14.18) * mm, "end": v(-5.21, 14.3) * mm});
            skLineSegment(sketch, "E448", {"start": v(-5.21, 14.3) * mm, "end": v(-5.3, 14.42) * mm});
            skLineSegment(sketch, "E449", {"start": v(-5.3, 14.42) * mm, "end": v(-5.38, 14.53) * mm});
            skLineSegment(sketch, "E450", {"start": v(-5.38, 14.53) * mm, "end": v(-5.46, 14.64) * mm});
            skLineSegment(sketch, "E451", {"start": v(-5.46, 14.64) * mm, "end": v(-5.55, 14.75) * mm});
            skLineSegment(sketch, "E452", {"start": v(-5.55, 14.75) * mm, "end": v(-5.65, 14.85) * mm});
            skLineSegment(sketch, "E453", {"start": v(-5.65, 14.85) * mm, "end": v(-5.74, 14.96) * mm});
            skLineSegment(sketch, "E454", {"start": v(-5.74, 14.96) * mm, "end": v(-5.84, 15.06) * mm});
            skLineSegment(sketch, "E455", {"start": v(-5.84, 15.06) * mm, "end": v(-5.94, 15.16) * mm});
            skLineSegment(sketch, "E456", {"start": v(-5.94, 15.16) * mm, "end": v(-6.04, 15.25) * mm});
            skLineSegment(sketch, "E457", {"start": v(-6.04, 15.25) * mm, "end": v(-6.15, 15.35) * mm});
            skLineSegment(sketch, "E458", {"start": v(-6.15, 15.35) * mm, "end": v(-6.25, 15.44) * mm});
            skLineSegment(sketch, "E459", {"start": v(-6.25, 15.44) * mm, "end": v(-6.87, 15.18) * mm});
            skLineSegment(sketch, "E460", {"start": v(-6.87, 15.18) * mm, "end": v(-6.88, 15.04) * mm});
            skLineSegment(sketch, "E461", {"start": v(-6.88, 15.04) * mm, "end": v(-6.88, 14.9) * mm});
            skLineSegment(sketch, "E462", {"start": v(-6.88, 14.9) * mm, "end": v(-6.88, 14.75) * mm});
            skLineSegment(sketch, "E463", {"start": v(-6.88, 14.75) * mm, "end": v(-6.88, 14.61) * mm});
            skLineSegment(sketch, "E464", {"start": v(-6.88, 14.61) * mm, "end": v(-6.87, 14.47) * mm});
            skLineSegment(sketch, "E465", {"start": v(-6.87, 14.47) * mm, "end": v(-6.86, 14.33) * mm});
            skLineSegment(sketch, "E466", {"start": v(-6.86, 14.33) * mm, "end": v(-6.85, 14.2) * mm});
            skLineSegment(sketch, "E467", {"start": v(-6.85, 14.2) * mm, "end": v(-6.84, 14.05) * mm});
            skLineSegment(sketch, "E468", {"start": v(-6.84, 14.05) * mm, "end": v(-6.82, 13.91) * mm});
            skLineSegment(sketch, "E469", {"start": v(-6.82, 13.91) * mm, "end": v(-6.8, 13.78) * mm});
            skLineSegment(sketch, "E470", {"start": v(-6.8, 13.78) * mm, "end": v(-6.76, 13.64) * mm});
            skLineSegment(sketch, "E471", {"start": v(-6.76, 13.64) * mm, "end": v(-6.73, 13.5) * mm});
            skLineSegment(sketch, "E472", {"start": v(-6.73, 13.5) * mm, "end": v(-6.69, 13.37) * mm});
            skLineSegment(sketch, "E473", {"start": v(-6.69, 13.37) * mm, "end": v(-6.64, 13.24) * mm});
            skLineSegment(sketch, "E474", {"start": v(-6.64, 13.24) * mm, "end": v(-6.67, 13.19) * mm});
            skLineSegment(sketch, "E475", {"start": v(-6.67, 13.19) * mm, "end": v(-6.68, 13.15) * mm});
            skLineSegment(sketch, "E476", {"start": v(-6.68, 13.15) * mm, "end": v(-6.69, 13.13) * mm});
            skLineSegment(sketch, "E477", {"start": v(-6.69, 13.13) * mm, "end": v(-6.7, 13.1) * mm});
            skLineSegment(sketch, "E478", {"start": v(-6.7, 13.1) * mm, "end": v(-6.72, 13.1) * mm});
            skLineSegment(sketch, "E479", {"start": v(-6.72, 13.1) * mm, "end": v(-7.26, 12.8) * mm});
            skLineSegment(sketch, "E480", {"start": v(-7.26, 12.8) * mm, "end": v(-7.28, 12.8) * mm});
            skLineSegment(sketch, "E481", {"start": v(-7.28, 12.8) * mm, "end": v(-7.3, 12.8) * mm});
            skLineSegment(sketch, "E482", {"start": v(-7.3, 12.8) * mm, "end": v(-7.33, 12.8) * mm});
            skLineSegment(sketch, "E483", {"start": v(-7.33, 12.8) * mm, "end": v(-7.36, 12.81) * mm});
            skLineSegment(sketch, "E484", {"start": v(-7.36, 12.81) * mm, "end": v(-7.42, 12.82) * mm});
            skLineSegment(sketch, "E485", {"start": v(-7.42, 12.82) * mm, "end": v(-7.5, 12.93) * mm});
            skLineSegment(sketch, "E486", {"start": v(-7.5, 12.93) * mm, "end": v(-7.59, 13.04) * mm});
            skLineSegment(sketch, "E487", {"start": v(-7.59, 13.04) * mm, "end": v(-7.68, 13.14) * mm});
            skLineSegment(sketch, "E488", {"start": v(-7.68, 13.14) * mm, "end": v(-7.78, 13.24) * mm});
            skLineSegment(sketch, "E489", {"start": v(-7.78, 13.24) * mm, "end": v(-7.89, 13.34) * mm});
            skLineSegment(sketch, "E490", {"start": v(-7.89, 13.34) * mm, "end": v(-8, 13.43) * mm});
            skLineSegment(sketch, "E491", {"start": v(-8, 13.43) * mm, "end": v(-8.1, 13.52) * mm});
            skLineSegment(sketch, "E492", {"start": v(-8.1, 13.52) * mm, "end": v(-8.2, 13.6) * mm});
            skLineSegment(sketch, "E493", {"start": v(-8.2, 13.6) * mm, "end": v(-8.32, 13.7) * mm});
            skLineSegment(sketch, "E494", {"start": v(-8.32, 13.7) * mm, "end": v(-8.44, 13.78) * mm});
            skLineSegment(sketch, "E495", {"start": v(-8.44, 13.78) * mm, "end": v(-8.55, 13.86) * mm});
            skLineSegment(sketch, "E496", {"start": v(-8.55, 13.86) * mm, "end": v(-8.67, 13.93) * mm});
            skLineSegment(sketch, "E497", {"start": v(-8.67, 13.93) * mm, "end": v(-8.79, 14) * mm});
            skLineSegment(sketch, "E498", {"start": v(-8.79, 14) * mm, "end": v(-8.9, 14.08) * mm});
            skLineSegment(sketch, "E499", {"start": v(-8.9, 14.08) * mm, "end": v(-9.47, 13.7) * mm});
            skLineSegment(sketch, "E500", {"start": v(-9.47, 13.7) * mm, "end": v(-9.45, 13.57) * mm});
            skLineSegment(sketch, "E501", {"start": v(-9.45, 13.57) * mm, "end": v(-9.43, 13.43) * mm});
            skLineSegment(sketch, "E502", {"start": v(-9.43, 13.43) * mm, "end": v(-9.4, 13.3) * mm});
            skLineSegment(sketch, "E503", {"start": v(-9.4, 13.3) * mm, "end": v(-9.38, 13.15) * mm});
            skLineSegment(sketch, "E504", {"start": v(-9.38, 13.15) * mm, "end": v(-9.35, 13.02) * mm});
            skLineSegment(sketch, "E505", {"start": v(-9.35, 13.02) * mm, "end": v(-9.31, 12.88) * mm});
            skLineSegment(sketch, "E506", {"start": v(-9.31, 12.88) * mm, "end": v(-9.28, 12.75) * mm});
            skLineSegment(sketch, "E507", {"start": v(-9.28, 12.75) * mm, "end": v(-9.24, 12.61) * mm});
            skLineSegment(sketch, "E508", {"start": v(-9.24, 12.61) * mm, "end": v(-9.2, 12.48) * mm});
            skLineSegment(sketch, "E509", {"start": v(-9.2, 12.48) * mm, "end": v(-9.14, 12.35) * mm});
            skLineSegment(sketch, "E510", {"start": v(-9.14, 12.35) * mm, "end": v(-9.1, 12.22) * mm});
            skLineSegment(sketch, "E511", {"start": v(-9.1, 12.22) * mm, "end": v(-9.03, 12.09) * mm});
            skLineSegment(sketch, "E512", {"start": v(-9.03, 12.09) * mm, "end": v(-8.97, 11.96) * mm});
            skLineSegment(sketch, "E513", {"start": v(-8.97, 11.96) * mm, "end": v(-8.9, 11.84) * mm});
            skLineSegment(sketch, "E514", {"start": v(-8.9, 11.84) * mm, "end": v(-8.92, 11.79) * mm});
            skLineSegment(sketch, "E515", {"start": v(-8.92, 11.79) * mm, "end": v(-8.92, 11.75) * mm});
            skLineSegment(sketch, "E516", {"start": v(-8.92, 11.75) * mm, "end": v(-8.92, 11.73) * mm});
            skLineSegment(sketch, "E517", {"start": v(-8.92, 11.73) * mm, "end": v(-8.93, 11.7) * mm});
            skLineSegment(sketch, "E518", {"start": v(-8.93, 11.7) * mm, "end": v(-8.95, 11.69) * mm});
            skLineSegment(sketch, "E519", {"start": v(-8.95, 11.69) * mm, "end": v(-9.43, 11.3) * mm});
            skLineSegment(sketch, "E520", {"start": v(-9.43, 11.3) * mm, "end": v(-9.45, 11.3) * mm});
            skLineSegment(sketch, "E521", {"start": v(-9.45, 11.3) * mm, "end": v(-9.47, 11.29) * mm});
            skLineSegment(sketch, "E522", {"start": v(-9.47, 11.29) * mm, "end": v(-9.5, 11.3) * mm});
            skLineSegment(sketch, "E523", {"start": v(-9.5, 11.3) * mm, "end": v(-9.53, 11.3) * mm});
            skLineSegment(sketch, "E524", {"start": v(-9.53, 11.3) * mm, "end": v(-9.59, 11.29) * mm});
            skLineSegment(sketch, "E525", {"start": v(-9.59, 11.29) * mm, "end": v(-9.69, 11.39) * mm});
            skLineSegment(sketch, "E526", {"start": v(-9.69, 11.39) * mm, "end": v(-9.8, 11.48) * mm});
            skLineSegment(sketch, "E527", {"start": v(-9.8, 11.48) * mm, "end": v(-9.9, 11.56) * mm});
            skLineSegment(sketch, "E528", {"start": v(-9.9, 11.56) * mm, "end": v(-10.02, 11.64) * mm});
            skLineSegment(sketch, "E529", {"start": v(-10.02, 11.64) * mm, "end": v(-10.14, 11.72) * mm});
            skLineSegment(sketch, "E530", {"start": v(-10.14, 11.72) * mm, "end": v(-10.26, 11.8) * mm});
            skLineSegment(sketch, "E531", {"start": v(-10.26, 11.8) * mm, "end": v(-10.38, 11.86) * mm});
            skLineSegment(sketch, "E532", {"start": v(-10.38, 11.86) * mm, "end": v(-10.5, 11.93) * mm});
            skLineSegment(sketch, "E533", {"start": v(-10.5, 11.93) * mm, "end": v(-10.63, 12) * mm});
            skLineSegment(sketch, "E534", {"start": v(-10.63, 12) * mm, "end": v(-10.76, 12.05) * mm});
            skLineSegment(sketch, "E535", {"start": v(-10.76, 12.05) * mm, "end": v(-10.89, 12.1) * mm});
            skLineSegment(sketch, "E536", {"start": v(-10.89, 12.1) * mm, "end": v(-11.02, 12.16) * mm});
            skLineSegment(sketch, "E537", {"start": v(-11.02, 12.16) * mm, "end": v(-11.15, 12.22) * mm});
            skLineSegment(sketch, "E538", {"start": v(-11.15, 12.22) * mm, "end": v(-11.28, 12.27) * mm});
            skLineSegment(sketch, "E539", {"start": v(-11.28, 12.27) * mm, "end": v(-11.77, 11.8) * mm});
            skLineSegment(sketch, "E540", {"start": v(-11.77, 11.8) * mm, "end": v(-11.72, 11.67) * mm});
            skLineSegment(sketch, "E541", {"start": v(-11.72, 11.67) * mm, "end": v(-11.68, 11.53) * mm});
            skLineSegment(sketch, "E542", {"start": v(-11.68, 11.53) * mm, "end": v(-11.63, 11.4) * mm});
            skLineSegment(sketch, "E543", {"start": v(-11.63, 11.4) * mm, "end": v(-11.58, 11.27) * mm});
            skLineSegment(sketch, "E544", {"start": v(-11.58, 11.27) * mm, "end": v(-11.52, 11.14) * mm});
            skLineSegment(sketch, "E545", {"start": v(-11.52, 11.14) * mm, "end": v(-11.46, 11.01) * mm});
            skLineSegment(sketch, "E546", {"start": v(-11.46, 11.01) * mm, "end": v(-11.4, 10.89) * mm});
            skLineSegment(sketch, "E547", {"start": v(-11.4, 10.89) * mm, "end": v(-11.34, 10.76) * mm});
            skLineSegment(sketch, "E548", {"start": v(-11.34, 10.76) * mm, "end": v(-11.27, 10.64) * mm});
            skLineSegment(sketch, "E549", {"start": v(-11.27, 10.64) * mm, "end": v(-11.2, 10.52) * mm});
            skLineSegment(sketch, "E550", {"start": v(-11.2, 10.52) * mm, "end": v(-11.13, 10.4) * mm});
            skLineSegment(sketch, "E551", {"start": v(-11.13, 10.4) * mm, "end": v(-11.05, 10.28) * mm});
            skLineSegment(sketch, "E552", {"start": v(-11.05, 10.28) * mm, "end": v(-10.96, 10.17) * mm});
            skLineSegment(sketch, "E553", {"start": v(-10.96, 10.17) * mm, "end": v(-10.87, 10.07) * mm});
            skLineSegment(sketch, "E554", {"start": v(-10.87, 10.07) * mm, "end": v(-10.88, 10) * mm});
            skLineSegment(sketch, "E555", {"start": v(-10.88, 10) * mm, "end": v(-10.87, 9.98) * mm});
            skLineSegment(sketch, "E556", {"start": v(-10.87, 9.98) * mm, "end": v(-10.87, 9.95) * mm});
            skLineSegment(sketch, "E557", {"start": v(-10.87, 9.95) * mm, "end": v(-10.88, 9.92) * mm});
            skLineSegment(sketch, "E558", {"start": v(-10.88, 9.92) * mm, "end": v(-10.9, 9.9) * mm});
            skLineSegment(sketch, "E559", {"start": v(-10.9, 9.9) * mm, "end": v(-11.3, 9.44) * mm});
            skLineSegment(sketch, "E560", {"start": v(-11.3, 9.44) * mm, "end": v(-11.31, 9.43) * mm});
            skLineSegment(sketch, "E561", {"start": v(-11.31, 9.43) * mm, "end": v(-11.33, 9.42) * mm});
            skLineSegment(sketch, "E562", {"start": v(-11.33, 9.42) * mm, "end": v(-11.36, 9.42) * mm});
            skLineSegment(sketch, "E563", {"start": v(-11.36, 9.42) * mm, "end": v(-11.4, 9.42) * mm});
            skLineSegment(sketch, "E564", {"start": v(-11.4, 9.42) * mm, "end": v(-11.45, 9.4) * mm});
            skLineSegment(sketch, "E565", {"start": v(-11.45, 9.4) * mm, "end": v(-11.57, 9.48) * mm});
            skLineSegment(sketch, "E566", {"start": v(-11.57, 9.48) * mm, "end": v(-11.69, 9.55) * mm});
            skLineSegment(sketch, "E567", {"start": v(-11.69, 9.55) * mm, "end": v(-11.81, 9.61) * mm});
            skLineSegment(sketch, "E568", {"start": v(-11.81, 9.61) * mm, "end": v(-11.94, 9.67) * mm});
            skLineSegment(sketch, "E569", {"start": v(-11.94, 9.67) * mm, "end": v(-12.07, 9.72) * mm});
            skLineSegment(sketch, "E570", {"start": v(-12.07, 9.72) * mm, "end": v(-12.2, 9.77) * mm});
            skLineSegment(sketch, "E571", {"start": v(-12.2, 9.77) * mm, "end": v(-12.34, 9.82) * mm});
            skLineSegment(sketch, "E572", {"start": v(-12.34, 9.82) * mm, "end": v(-12.47, 9.86) * mm});
            skLineSegment(sketch, "E573", {"start": v(-12.47, 9.86) * mm, "end": v(-12.6, 9.9) * mm});
            skLineSegment(sketch, "E574", {"start": v(-12.6, 9.9) * mm, "end": v(-12.74, 9.94) * mm});
            skLineSegment(sketch, "E575", {"start": v(-12.74, 9.94) * mm, "end": v(-12.88, 9.97) * mm});
            skLineSegment(sketch, "E576", {"start": v(-12.88, 9.97) * mm, "end": v(-13.01, 10) * mm});
            skLineSegment(sketch, "E577", {"start": v(-13.01, 10) * mm, "end": v(-13.15, 10.03) * mm});
            skLineSegment(sketch, "E578", {"start": v(-13.15, 10.03) * mm, "end": v(-13.29, 10.06) * mm});
            skLineSegment(sketch, "E579", {"start": v(-13.29, 10.06) * mm, "end": v(-13.69, 9.51) * mm});
            skLineSegment(sketch, "E580", {"start": v(-13.69, 9.51) * mm, "end": v(-13.62, 9.39) * mm});
            skLineSegment(sketch, "E581", {"start": v(-13.62, 9.39) * mm, "end": v(-13.55, 9.27) * mm});
            skLineSegment(sketch, "E582", {"start": v(-13.55, 9.27) * mm, "end": v(-13.48, 9.15) * mm});
            skLineSegment(sketch, "E583", {"start": v(-13.48, 9.15) * mm, "end": v(-13.4, 9.03) * mm});
            skLineSegment(sketch, "E584", {"start": v(-13.4, 9.03) * mm, "end": v(-13.33, 8.9) * mm});
            skLineSegment(sketch, "E585", {"start": v(-13.33, 8.9) * mm, "end": v(-13.25, 8.8) * mm});
            skLineSegment(sketch, "E586", {"start": v(-13.25, 8.8) * mm, "end": v(-13.16, 8.68) * mm});
            skLineSegment(sketch, "E587", {"start": v(-13.16, 8.68) * mm, "end": v(-13.08, 8.57) * mm});
            skLineSegment(sketch, "E588", {"start": v(-13.08, 8.57) * mm, "end": v(-13, 8.46) * mm});
            skLineSegment(sketch, "E589", {"start": v(-13, 8.46) * mm, "end": v(-12.9, 8.35) * mm});
            skLineSegment(sketch, "E590", {"start": v(-12.9, 8.35) * mm, "end": v(-12.8, 8.25) * mm});
            skLineSegment(sketch, "E591", {"start": v(-12.8, 8.25) * mm, "end": v(-12.7, 8.15) * mm});
            skLineSegment(sketch, "E592", {"start": v(-12.7, 8.15) * mm, "end": v(-12.6, 8.05) * mm});
            skLineSegment(sketch, "E593", {"start": v(-12.6, 8.05) * mm, "end": v(-12.5, 7.97) * mm});
            skLineSegment(sketch, "E594", {"start": v(-12.5, 7.97) * mm, "end": v(-12.5, 7.9) * mm});
            skLineSegment(sketch, "E595", {"start": v(-12.5, 7.9) * mm, "end": v(-12.48, 7.88) * mm});
            skLineSegment(sketch, "E596", {"start": v(-12.48, 7.88) * mm, "end": v(-12.47, 7.85) * mm});
            skLineSegment(sketch, "E597", {"start": v(-12.47, 7.85) * mm, "end": v(-12.48, 7.83) * mm});
            skLineSegment(sketch, "E598", {"start": v(-12.48, 7.83) * mm, "end": v(-12.48, 7.8) * mm});
            skLineSegment(sketch, "E599", {"start": v(-12.48, 7.8) * mm, "end": v(-12.8, 7.28) * mm});
            skLineSegment(sketch, "E600", {"start": v(-12.8, 7.28) * mm, "end": v(-12.81, 7.26) * mm});
            skLineSegment(sketch, "E601", {"start": v(-12.81, 7.26) * mm, "end": v(-12.83, 7.25) * mm});
            skLineSegment(sketch, "E602", {"start": v(-12.83, 7.25) * mm, "end": v(-12.86, 7.24) * mm});
            skLineSegment(sketch, "E603", {"start": v(-12.86, 7.24) * mm, "end": v(-12.9, 7.24) * mm});
            skLineSegment(sketch, "E604", {"start": v(-12.9, 7.24) * mm, "end": v(-12.95, 7.2) * mm});
            skLineSegment(sketch, "E605", {"start": v(-12.95, 7.2) * mm, "end": v(-13.07, 7.26) * mm});
            skLineSegment(sketch, "E606", {"start": v(-13.07, 7.26) * mm, "end": v(-13.2, 7.31) * mm});
            skLineSegment(sketch, "E607", {"start": v(-13.2, 7.31) * mm, "end": v(-13.34, 7.35) * mm});
            skLineSegment(sketch, "E608", {"start": v(-13.34, 7.35) * mm, "end": v(-13.48, 7.39) * mm});
            skLineSegment(sketch, "E609", {"start": v(-13.48, 7.39) * mm, "end": v(-13.61, 7.42) * mm});
            skLineSegment(sketch, "E610", {"start": v(-13.61, 7.42) * mm, "end": v(-13.75, 7.44) * mm});
            skLineSegment(sketch, "E611", {"start": v(-13.75, 7.44) * mm, "end": v(-13.9, 7.46) * mm});
            skLineSegment(sketch, "E612", {"start": v(-13.9, 7.46) * mm, "end": v(-14.03, 7.48) * mm});
            skLineSegment(sketch, "E613", {"start": v(-14.03, 7.48) * mm, "end": v(-14.17, 7.5) * mm});
            skLineSegment(sketch, "E614", {"start": v(-14.17, 7.5) * mm, "end": v(-14.3, 7.5) * mm});
            skLineSegment(sketch, "E615", {"start": v(-14.3, 7.5) * mm, "end": v(-14.45, 7.52) * mm});
            skLineSegment(sketch, "E616", {"start": v(-14.45, 7.52) * mm, "end": v(-14.6, 7.52) * mm});
            skLineSegment(sketch, "E617", {"start": v(-14.6, 7.52) * mm, "end": v(-14.73, 7.53) * mm});
            skLineSegment(sketch, "E618", {"start": v(-14.73, 7.53) * mm, "end": v(-14.87, 7.53) * mm});
            skLineSegment(sketch, "E619", {"start": v(-14.87, 7.53) * mm, "end": v(-15.16, 6.92) * mm});
            skLineSegment(sketch, "E620", {"start": v(-15.16, 6.92) * mm, "end": v(-15.08, 6.81) * mm});
            skLineSegment(sketch, "E621", {"start": v(-15.08, 6.81) * mm, "end": v(-14.99, 6.7) * mm});
            skLineSegment(sketch, "E622", {"start": v(-14.99, 6.7) * mm, "end": v(-14.9, 6.6) * mm});
            skLineSegment(sketch, "E623", {"start": v(-14.9, 6.6) * mm, "end": v(-14.8, 6.5) * mm});
            skLineSegment(sketch, "E624", {"start": v(-14.8, 6.5) * mm, "end": v(-14.7, 6.39) * mm});
            skLineSegment(sketch, "E625", {"start": v(-14.7, 6.39) * mm, "end": v(-14.6, 6.29) * mm});
            skLineSegment(sketch, "E626", {"start": v(-14.6, 6.29) * mm, "end": v(-14.5, 6.2) * mm});
            skLineSegment(sketch, "E627", {"start": v(-14.5, 6.2) * mm, "end": v(-14.4, 6.1) * mm});
            skLineSegment(sketch, "E628", {"start": v(-14.4, 6.1) * mm, "end": v(-14.3, 6) * mm});
            skLineSegment(sketch, "E629", {"start": v(-14.3, 6) * mm, "end": v(-14.18, 5.92) * mm});
            skLineSegment(sketch, "E630", {"start": v(-14.18, 5.92) * mm, "end": v(-14.07, 5.83) * mm});
            skLineSegment(sketch, "E631", {"start": v(-14.07, 5.83) * mm, "end": v(-13.96, 5.75) * mm});
            skLineSegment(sketch, "E632", {"start": v(-13.96, 5.75) * mm, "end": v(-13.84, 5.68) * mm});
            skLineSegment(sketch, "E633", {"start": v(-13.84, 5.68) * mm, "end": v(-13.71, 5.61) * mm});
            skLineSegment(sketch, "E634", {"start": v(-13.71, 5.61) * mm, "end": v(-13.7, 5.55) * mm});
            skLineSegment(sketch, "E635", {"start": v(-13.7, 5.55) * mm, "end": v(-13.69, 5.53) * mm});
            skLineSegment(sketch, "E636", {"start": v(-13.69, 5.53) * mm, "end": v(-13.68, 5.5) * mm});
            skLineSegment(sketch, "E637", {"start": v(-13.68, 5.5) * mm, "end": v(-13.67, 5.48) * mm});
            skLineSegment(sketch, "E638", {"start": v(-13.67, 5.48) * mm, "end": v(-13.68, 5.45) * mm});
            skLineSegment(sketch, "E639", {"start": v(-13.68, 5.45) * mm, "end": v(-13.9, 4.88) * mm});
            skLineSegment(sketch, "E640", {"start": v(-13.9, 4.88) * mm, "end": v(-13.9, 4.86) * mm});
            skLineSegment(sketch, "E641", {"start": v(-13.9, 4.86) * mm, "end": v(-13.92, 4.84) * mm});
            skLineSegment(sketch, "E642", {"start": v(-13.92, 4.84) * mm, "end": v(-13.95, 4.83) * mm});
            skLineSegment(sketch, "E643", {"start": v(-13.95, 4.83) * mm, "end": v(-13.98, 4.82) * mm});
            skLineSegment(sketch, "E644", {"start": v(-13.98, 4.82) * mm, "end": v(-14.02, 4.78) * mm});
            skLineSegment(sketch, "E645", {"start": v(-14.02, 4.78) * mm, "end": v(-14.16, 4.82) * mm});
            skLineSegment(sketch, "E646", {"start": v(-14.16, 4.82) * mm, "end": v(-14.3, 4.84) * mm});
            skLineSegment(sketch, "E647", {"start": v(-14.3, 4.84) * mm, "end": v(-14.44, 4.85) * mm});
            skLineSegment(sketch, "E648", {"start": v(-14.44, 4.85) * mm, "end": v(-14.58, 4.86) * mm});
            skLineSegment(sketch, "E649", {"start": v(-14.58, 4.86) * mm, "end": v(-14.72, 4.87) * mm});
            skLineSegment(sketch, "E650", {"start": v(-14.72, 4.87) * mm, "end": v(-14.86, 4.87) * mm});
            skLineSegment(sketch, "E651", {"start": v(-14.86, 4.87) * mm, "end": v(-15, 4.87) * mm});
            skLineSegment(sketch, "E652", {"start": v(-15, 4.87) * mm, "end": v(-15.14, 4.86) * mm});
            skLineSegment(sketch, "E653", {"start": v(-15.14, 4.86) * mm, "end": v(-15.28, 4.85) * mm});
            skLineSegment(sketch, "E654", {"start": v(-15.28, 4.85) * mm, "end": v(-15.42, 4.84) * mm});
            skLineSegment(sketch, "E655", {"start": v(-15.42, 4.84) * mm, "end": v(-15.56, 4.82) * mm});
            skLineSegment(sketch, "E656", {"start": v(-15.56, 4.82) * mm, "end": v(-15.7, 4.8) * mm});
            skLineSegment(sketch, "E657", {"start": v(-15.7, 4.8) * mm, "end": v(-15.84, 4.78) * mm});
            skLineSegment(sketch, "E658", {"start": v(-15.84, 4.78) * mm, "end": v(-15.98, 4.75) * mm});
            skLineSegment(sketch, "E659", {"start": v(-15.98, 4.75) * mm, "end": v(-16.16, 4.1) * mm});
            skLineSegment(sketch, "E660", {"start": v(-16.16, 4.1) * mm, "end": v(-16.05, 4.01) * mm});
            skLineSegment(sketch, "E661", {"start": v(-16.05, 4.01) * mm, "end": v(-15.94, 3.92) * mm});
            skLineSegment(sketch, "E662", {"start": v(-15.94, 3.92) * mm, "end": v(-15.83, 3.83) * mm});
            skLineSegment(sketch, "E663", {"start": v(-15.83, 3.83) * mm, "end": v(-15.72, 3.75) * mm});
            skLineSegment(sketch, "E664", {"start": v(-15.72, 3.75) * mm, "end": v(-15.6, 3.66) * mm});
            skLineSegment(sketch, "E665", {"start": v(-15.6, 3.66) * mm, "end": v(-15.5, 3.58) * mm});
            skLineSegment(sketch, "E666", {"start": v(-15.5, 3.58) * mm, "end": v(-15.38, 3.5) * mm});
            skLineSegment(sketch, "E667", {"start": v(-15.38, 3.5) * mm, "end": v(-15.26, 3.43) * mm});
            skLineSegment(sketch, "E668", {"start": v(-15.26, 3.43) * mm, "end": v(-15.14, 3.36) * mm});
            skLineSegment(sketch, "E669", {"start": v(-15.14, 3.36) * mm, "end": v(-15.01, 3.3) * mm});
            skLineSegment(sketch, "E670", {"start": v(-15.01, 3.3) * mm, "end": v(-14.89, 3.23) * mm});
            skLineSegment(sketch, "E671", {"start": v(-14.89, 3.23) * mm, "end": v(-14.76, 3.17) * mm});
            skLineSegment(sketch, "E672", {"start": v(-14.76, 3.17) * mm, "end": v(-14.63, 3.12) * mm});
            skLineSegment(sketch, "E673", {"start": v(-14.63, 3.12) * mm, "end": v(-14.5, 3.08) * mm});
            skLineSegment(sketch, "E674", {"start": v(-14.5, 3.08) * mm, "end": v(-14.47, 3.02) * mm});
            skLineSegment(sketch, "E675", {"start": v(-14.47, 3.02) * mm, "end": v(-14.45, 3) * mm});
            skLineSegment(sketch, "E676", {"start": v(-14.45, 3) * mm, "end": v(-14.44, 2.97) * mm});
            skLineSegment(sketch, "E677", {"start": v(-14.44, 2.97) * mm, "end": v(-14.43, 2.95) * mm});
            skLineSegment(sketch, "E678", {"start": v(-14.43, 2.95) * mm, "end": v(-14.43, 2.93) * mm});
            skLineSegment(sketch, "E679", {"start": v(-14.43, 2.93) * mm, "end": v(-14.54, 2.32) * mm});
            skLineSegment(sketch, "E680", {"start": v(-14.54, 2.32) * mm, "end": v(-14.55, 2.3) * mm});
            skLineSegment(sketch, "E681", {"start": v(-14.55, 2.3) * mm, "end": v(-14.56, 2.28) * mm});
            skLineSegment(sketch, "E682", {"start": v(-14.56, 2.28) * mm, "end": v(-14.59, 2.27) * mm});
            skLineSegment(sketch, "E683", {"start": v(-14.59, 2.27) * mm, "end": v(-14.61, 2.25) * mm});
            skLineSegment(sketch, "E684", {"start": v(-14.61, 2.25) * mm, "end": v(-14.65, 2.2) * mm});
            skLineSegment(sketch, "E685", {"start": v(-14.65, 2.2) * mm, "end": v(-14.8, 2.21) * mm});
            skLineSegment(sketch, "E686", {"start": v(-14.8, 2.21) * mm, "end": v(-14.93, 2.21) * mm});
            skLineSegment(sketch, "E687", {"start": v(-14.93, 2.21) * mm, "end": v(-15.07, 2.2) * mm});
            skLineSegment(sketch, "E688", {"start": v(-15.07, 2.2) * mm, "end": v(-15.21, 2.19) * mm});
            skLineSegment(sketch, "E689", {"start": v(-15.21, 2.19) * mm, "end": v(-15.35, 2.17) * mm});
            skLineSegment(sketch, "E690", {"start": v(-15.35, 2.17) * mm, "end": v(-15.5, 2.14) * mm});
            skLineSegment(sketch, "E691", {"start": v(-15.5, 2.14) * mm, "end": v(-15.63, 2.11) * mm});
            skLineSegment(sketch, "E692", {"start": v(-15.63, 2.11) * mm, "end": v(-15.77, 2.08) * mm});
            skLineSegment(sketch, "E693", {"start": v(-15.77, 2.08) * mm, "end": v(-15.9, 2.05) * mm});
            skLineSegment(sketch, "E694", {"start": v(-15.9, 2.05) * mm, "end": v(-16.04, 2) * mm});
            skLineSegment(sketch, "E695", {"start": v(-16.04, 2) * mm, "end": v(-16.17, 1.97) * mm});
            skLineSegment(sketch, "E696", {"start": v(-16.17, 1.97) * mm, "end": v(-16.3, 1.92) * mm});
            skLineSegment(sketch, "E697", {"start": v(-16.3, 1.92) * mm, "end": v(-16.44, 1.88) * mm});
            skLineSegment(sketch, "E698", {"start": v(-16.44, 1.88) * mm, "end": v(-16.57, 1.83) * mm});
            skLineSegment(sketch, "E699", {"start": v(-16.57, 1.83) * mm, "end": v(-16.63, 1.16) * mm});
            skLineSegment(sketch, "E700", {"start": v(-16.63, 1.16) * mm, "end": v(-16.5, 1.08) * mm});
            skLineSegment(sketch, "E701", {"start": v(-16.5, 1.08) * mm, "end": v(-16.39, 1.02) * mm});
            skLineSegment(sketch, "E702", {"start": v(-16.39, 1.02) * mm, "end": v(-16.26, 0.95) * mm});
            skLineSegment(sketch, "E703", {"start": v(-16.26, 0.95) * mm, "end": v(-16.14, 0.88) * mm});
            skLineSegment(sketch, "E704", {"start": v(-16.14, 0.88) * mm, "end": v(-16.01, 0.82) * mm});
            skLineSegment(sketch, "E705", {"start": v(-16.01, 0.82) * mm, "end": v(-15.88, 0.76) * mm});
            skLineSegment(sketch, "E706", {"start": v(-15.88, 0.76) * mm, "end": v(-15.76, 0.7) * mm});
            skLineSegment(sketch, "E707", {"start": v(-15.76, 0.7) * mm, "end": v(-15.63, 0.66) * mm});
            skLineSegment(sketch, "E708", {"start": v(-15.63, 0.66) * mm, "end": v(-15.5, 0.6) * mm});
            skLineSegment(sketch, "E709", {"start": v(-15.5, 0.6) * mm, "end": v(-15.36, 0.56) * mm});
            skLineSegment(sketch, "E710", {"start": v(-15.36, 0.56) * mm, "end": v(-15.23, 0.52) * mm});
            skLineSegment(sketch, "E711", {"start": v(-15.23, 0.52) * mm, "end": v(-15.09, 0.49) * mm});
            skLineSegment(sketch, "E712", {"start": v(-15.09, 0.49) * mm, "end": v(-14.95, 0.46) * mm});
            skLineSegment(sketch, "E713", {"start": v(-14.95, 0.46) * mm, "end": v(-14.81, 0.44) * mm});
            skLineSegment(sketch, "E714", {"start": v(-14.81, 0.44) * mm, "end": v(-14.78, 0.4) * mm});
            skLineSegment(sketch, "E715", {"start": v(-14.78, 0.4) * mm, "end": v(-14.76, 0.37) * mm});
            skLineSegment(sketch, "E716", {"start": v(-14.76, 0.37) * mm, "end": v(-14.74, 0.35) * mm});
            skLineSegment(sketch, "E717", {"start": v(-14.74, 0.35) * mm, "end": v(-14.73, 0.33) * mm});
            skLineSegment(sketch, "E718", {"start": v(-14.73, 0.33) * mm, "end": v(-14.72, 0.3) * mm});
            skLineSegment(sketch, "E719", {"start": v(-14.72, 0.3) * mm, "end": v(-14.72, -0.3) * mm});
            skLineSegment(sketch, "E720", {"start": v(-14.72, -0.3) * mm, "end": v(-14.73, -0.33) * mm});
            skLineSegment(sketch, "E721", {"start": v(-14.73, -0.33) * mm, "end": v(-14.74, -0.35) * mm});
            skLineSegment(sketch, "E722", {"start": v(-14.74, -0.35) * mm, "end": v(-14.76, -0.37) * mm});
            skLineSegment(sketch, "E723", {"start": v(-14.76, -0.37) * mm, "end": v(-14.78, -0.4) * mm});
            skLineSegment(sketch, "E724", {"start": v(-14.78, -0.4) * mm, "end": v(-14.81, -0.44) * mm});
            skLineSegment(sketch, "E725", {"start": v(-14.81, -0.44) * mm, "end": v(-14.95, -0.46) * mm});
            skLineSegment(sketch, "E726", {"start": v(-14.95, -0.46) * mm, "end": v(-15.09, -0.49) * mm});
            skLineSegment(sketch, "E727", {"start": v(-15.09, -0.49) * mm, "end": v(-15.23, -0.52) * mm});
            skLineSegment(sketch, "E728", {"start": v(-15.23, -0.52) * mm, "end": v(-15.36, -0.56) * mm});
            skLineSegment(sketch, "E729", {"start": v(-15.36, -0.56) * mm, "end": v(-15.5, -0.6) * mm});
            skLineSegment(sketch, "E730", {"start": v(-15.5, -0.6) * mm, "end": v(-15.63, -0.66) * mm});
            skLineSegment(sketch, "E731", {"start": v(-15.63, -0.66) * mm, "end": v(-15.76, -0.7) * mm});
            skLineSegment(sketch, "E732", {"start": v(-15.76, -0.7) * mm, "end": v(-15.88, -0.76) * mm});
            skLineSegment(sketch, "E733", {"start": v(-15.88, -0.76) * mm, "end": v(-16.01, -0.82) * mm});
            skLineSegment(sketch, "E734", {"start": v(-16.01, -0.82) * mm, "end": v(-16.14, -0.88) * mm});
            skLineSegment(sketch, "E735", {"start": v(-16.14, -0.88) * mm, "end": v(-16.26, -0.95) * mm});
            skLineSegment(sketch, "E736", {"start": v(-16.26, -0.95) * mm, "end": v(-16.39, -1.02) * mm});
            skLineSegment(sketch, "E737", {"start": v(-16.39, -1.02) * mm, "end": v(-16.5, -1.08) * mm});
            skLineSegment(sketch, "E738", {"start": v(-16.5, -1.08) * mm, "end": v(-16.63, -1.16) * mm});
            skLineSegment(sketch, "E739", {"start": v(-16.63, -1.16) * mm, "end": v(-16.57, -1.83) * mm});
            skLineSegment(sketch, "E740", {"start": v(-16.57, -1.83) * mm, "end": v(-16.44, -1.88) * mm});
            skLineSegment(sketch, "E741", {"start": v(-16.44, -1.88) * mm, "end": v(-16.3, -1.92) * mm});
            skLineSegment(sketch, "E742", {"start": v(-16.3, -1.92) * mm, "end": v(-16.17, -1.97) * mm});
            skLineSegment(sketch, "E743", {"start": v(-16.17, -1.97) * mm, "end": v(-16.04, -2) * mm});
            skLineSegment(sketch, "E744", {"start": v(-16.04, -2) * mm, "end": v(-15.9, -2.05) * mm});
            skLineSegment(sketch, "E745", {"start": v(-15.9, -2.05) * mm, "end": v(-15.77, -2.08) * mm});
            skLineSegment(sketch, "E746", {"start": v(-15.77, -2.08) * mm, "end": v(-15.63, -2.11) * mm});
            skLineSegment(sketch, "E747", {"start": v(-15.63, -2.11) * mm, "end": v(-15.5, -2.14) * mm});
            skLineSegment(sketch, "E748", {"start": v(-15.5, -2.14) * mm, "end": v(-15.35, -2.17) * mm});
            skLineSegment(sketch, "E749", {"start": v(-15.35, -2.17) * mm, "end": v(-15.21, -2.19) * mm});
            skLineSegment(sketch, "E750", {"start": v(-15.21, -2.19) * mm, "end": v(-15.07, -2.2) * mm});
            skLineSegment(sketch, "E751", {"start": v(-15.07, -2.2) * mm, "end": v(-14.93, -2.21) * mm});
            skLineSegment(sketch, "E752", {"start": v(-14.93, -2.21) * mm, "end": v(-14.8, -2.21) * mm});
            skLineSegment(sketch, "E753", {"start": v(-14.8, -2.21) * mm, "end": v(-14.65, -2.2) * mm});
            skLineSegment(sketch, "E754", {"start": v(-14.65, -2.2) * mm, "end": v(-14.61, -2.25) * mm});
            skLineSegment(sketch, "E755", {"start": v(-14.61, -2.25) * mm, "end": v(-14.59, -2.27) * mm});
            skLineSegment(sketch, "E756", {"start": v(-14.59, -2.27) * mm, "end": v(-14.56, -2.28) * mm});
            skLineSegment(sketch, "E757", {"start": v(-14.56, -2.28) * mm, "end": v(-14.55, -2.3) * mm});
            skLineSegment(sketch, "E758", {"start": v(-14.55, -2.3) * mm, "end": v(-14.54, -2.32) * mm});
            skLineSegment(sketch, "E759", {"start": v(-14.54, -2.32) * mm, "end": v(-14.43, -2.93) * mm});
            skLineSegment(sketch, "E760", {"start": v(-14.43, -2.93) * mm, "end": v(-14.43, -2.95) * mm});
            skLineSegment(sketch, "E761", {"start": v(-14.43, -2.95) * mm, "end": v(-14.44, -2.97) * mm});
            skLineSegment(sketch, "E762", {"start": v(-14.44, -2.97) * mm, "end": v(-14.45, -3) * mm});
            skLineSegment(sketch, "E763", {"start": v(-14.45, -3) * mm, "end": v(-14.47, -3.02) * mm});
            skLineSegment(sketch, "E764", {"start": v(-14.47, -3.02) * mm, "end": v(-14.5, -3.08) * mm});
            skLineSegment(sketch, "E765", {"start": v(-14.5, -3.08) * mm, "end": v(-14.63, -3.12) * mm});
            skLineSegment(sketch, "E766", {"start": v(-14.63, -3.12) * mm, "end": v(-14.76, -3.17) * mm});
            skLineSegment(sketch, "E767", {"start": v(-14.76, -3.17) * mm, "end": v(-14.89, -3.23) * mm});
            skLineSegment(sketch, "E768", {"start": v(-14.89, -3.23) * mm, "end": v(-15.01, -3.3) * mm});
            skLineSegment(sketch, "E769", {"start": v(-15.01, -3.3) * mm, "end": v(-15.14, -3.36) * mm});
            skLineSegment(sketch, "E770", {"start": v(-15.14, -3.36) * mm, "end": v(-15.26, -3.43) * mm});
            skLineSegment(sketch, "E771", {"start": v(-15.26, -3.43) * mm, "end": v(-15.38, -3.5) * mm});
            skLineSegment(sketch, "E772", {"start": v(-15.38, -3.5) * mm, "end": v(-15.5, -3.58) * mm});
            skLineSegment(sketch, "E773", {"start": v(-15.5, -3.58) * mm, "end": v(-15.6, -3.66) * mm});
            skLineSegment(sketch, "E774", {"start": v(-15.6, -3.66) * mm, "end": v(-15.72, -3.75) * mm});
            skLineSegment(sketch, "E775", {"start": v(-15.72, -3.75) * mm, "end": v(-15.83, -3.83) * mm});
            skLineSegment(sketch, "E776", {"start": v(-15.83, -3.83) * mm, "end": v(-15.94, -3.92) * mm});
            skLineSegment(sketch, "E777", {"start": v(-15.94, -3.92) * mm, "end": v(-16.05, -4.01) * mm});
            skLineSegment(sketch, "E778", {"start": v(-16.05, -4.01) * mm, "end": v(-16.16, -4.1) * mm});
            skLineSegment(sketch, "E779", {"start": v(-16.16, -4.1) * mm, "end": v(-15.98, -4.75) * mm});
            skLineSegment(sketch, "E780", {"start": v(-15.98, -4.75) * mm, "end": v(-15.84, -4.78) * mm});
            skLineSegment(sketch, "E781", {"start": v(-15.84, -4.78) * mm, "end": v(-15.7, -4.8) * mm});
            skLineSegment(sketch, "E782", {"start": v(-15.7, -4.8) * mm, "end": v(-15.56, -4.82) * mm});
            skLineSegment(sketch, "E783", {"start": v(-15.56, -4.82) * mm, "end": v(-15.42, -4.84) * mm});
            skLineSegment(sketch, "E784", {"start": v(-15.42, -4.84) * mm, "end": v(-15.28, -4.85) * mm});
            skLineSegment(sketch, "E785", {"start": v(-15.28, -4.85) * mm, "end": v(-15.14, -4.86) * mm});
            skLineSegment(sketch, "E786", {"start": v(-15.14, -4.86) * mm, "end": v(-15, -4.87) * mm});
            skLineSegment(sketch, "E787", {"start": v(-15, -4.87) * mm, "end": v(-14.86, -4.87) * mm});
            skLineSegment(sketch, "E788", {"start": v(-14.86, -4.87) * mm, "end": v(-14.72, -4.87) * mm});
            skLineSegment(sketch, "E789", {"start": v(-14.72, -4.87) * mm, "end": v(-14.58, -4.86) * mm});
            skLineSegment(sketch, "E790", {"start": v(-14.58, -4.86) * mm, "end": v(-14.44, -4.85) * mm});
            skLineSegment(sketch, "E791", {"start": v(-14.44, -4.85) * mm, "end": v(-14.3, -4.84) * mm});
            skLineSegment(sketch, "E792", {"start": v(-14.3, -4.84) * mm, "end": v(-14.16, -4.82) * mm});
            skLineSegment(sketch, "E793", {"start": v(-14.16, -4.82) * mm, "end": v(-14.02, -4.78) * mm});
            skLineSegment(sketch, "E794", {"start": v(-14.02, -4.78) * mm, "end": v(-13.98, -4.82) * mm});
            skLineSegment(sketch, "E795", {"start": v(-13.98, -4.82) * mm, "end": v(-13.95, -4.83) * mm});
            skLineSegment(sketch, "E796", {"start": v(-13.95, -4.83) * mm, "end": v(-13.92, -4.84) * mm});
            skLineSegment(sketch, "E797", {"start": v(-13.92, -4.84) * mm, "end": v(-13.9, -4.86) * mm});
            skLineSegment(sketch, "E798", {"start": v(-13.9, -4.86) * mm, "end": v(-13.9, -4.88) * mm});
            skLineSegment(sketch, "E799", {"start": v(-13.9, -4.88) * mm, "end": v(-13.68, -5.45) * mm});
            skLineSegment(sketch, "E800", {"start": v(-13.68, -5.45) * mm, "end": v(-13.67, -5.48) * mm});
            skLineSegment(sketch, "E801", {"start": v(-13.67, -5.48) * mm, "end": v(-13.68, -5.5) * mm});
            skLineSegment(sketch, "E802", {"start": v(-13.68, -5.5) * mm, "end": v(-13.69, -5.53) * mm});
            skLineSegment(sketch, "E803", {"start": v(-13.69, -5.53) * mm, "end": v(-13.7, -5.55) * mm});
            skLineSegment(sketch, "E804", {"start": v(-13.7, -5.55) * mm, "end": v(-13.71, -5.61) * mm});
            skLineSegment(sketch, "E805", {"start": v(-13.71, -5.61) * mm, "end": v(-13.84, -5.68) * mm});
            skLineSegment(sketch, "E806", {"start": v(-13.84, -5.68) * mm, "end": v(-13.96, -5.75) * mm});
            skLineSegment(sketch, "E807", {"start": v(-13.96, -5.75) * mm, "end": v(-14.07, -5.83) * mm});
            skLineSegment(sketch, "E808", {"start": v(-14.07, -5.83) * mm, "end": v(-14.18, -5.92) * mm});
            skLineSegment(sketch, "E809", {"start": v(-14.18, -5.92) * mm, "end": v(-14.3, -6) * mm});
            skLineSegment(sketch, "E810", {"start": v(-14.3, -6) * mm, "end": v(-14.4, -6.1) * mm});
            skLineSegment(sketch, "E811", {"start": v(-14.4, -6.1) * mm, "end": v(-14.5, -6.2) * mm});
            skLineSegment(sketch, "E812", {"start": v(-14.5, -6.2) * mm, "end": v(-14.6, -6.29) * mm});
            skLineSegment(sketch, "E813", {"start": v(-14.6, -6.29) * mm, "end": v(-14.7, -6.39) * mm});
            skLineSegment(sketch, "E814", {"start": v(-14.7, -6.39) * mm, "end": v(-14.8, -6.5) * mm});
            skLineSegment(sketch, "E815", {"start": v(-14.8, -6.5) * mm, "end": v(-14.9, -6.6) * mm});
            skLineSegment(sketch, "E816", {"start": v(-14.9, -6.6) * mm, "end": v(-14.99, -6.7) * mm});
            skLineSegment(sketch, "E817", {"start": v(-14.99, -6.7) * mm, "end": v(-15.08, -6.81) * mm});
            skLineSegment(sketch, "E818", {"start": v(-15.08, -6.81) * mm, "end": v(-15.16, -6.92) * mm});
            skLineSegment(sketch, "E819", {"start": v(-15.16, -6.92) * mm, "end": v(-14.87, -7.53) * mm});
            skLineSegment(sketch, "E820", {"start": v(-14.87, -7.53) * mm, "end": v(-14.73, -7.53) * mm});
            skLineSegment(sketch, "E821", {"start": v(-14.73, -7.53) * mm, "end": v(-14.6, -7.52) * mm});
            skLineSegment(sketch, "E822", {"start": v(-14.6, -7.52) * mm, "end": v(-14.45, -7.52) * mm});
            skLineSegment(sketch, "E823", {"start": v(-14.45, -7.52) * mm, "end": v(-14.3, -7.5) * mm});
            skLineSegment(sketch, "E824", {"start": v(-14.3, -7.5) * mm, "end": v(-14.17, -7.5) * mm});
            skLineSegment(sketch, "E825", {"start": v(-14.17, -7.5) * mm, "end": v(-14.03, -7.48) * mm});
            skLineSegment(sketch, "E826", {"start": v(-14.03, -7.48) * mm, "end": v(-13.9, -7.46) * mm});
            skLineSegment(sketch, "E827", {"start": v(-13.9, -7.46) * mm, "end": v(-13.75, -7.44) * mm});
            skLineSegment(sketch, "E828", {"start": v(-13.75, -7.44) * mm, "end": v(-13.61, -7.42) * mm});
            skLineSegment(sketch, "E829", {"start": v(-13.61, -7.42) * mm, "end": v(-13.48, -7.39) * mm});
            skLineSegment(sketch, "E830", {"start": v(-13.48, -7.39) * mm, "end": v(-13.34, -7.35) * mm});
            skLineSegment(sketch, "E831", {"start": v(-13.34, -7.35) * mm, "end": v(-13.2, -7.31) * mm});
            skLineSegment(sketch, "E832", {"start": v(-13.2, -7.31) * mm, "end": v(-13.07, -7.26) * mm});
            skLineSegment(sketch, "E833", {"start": v(-13.07, -7.26) * mm, "end": v(-12.95, -7.2) * mm});
            skLineSegment(sketch, "E834", {"start": v(-12.95, -7.2) * mm, "end": v(-12.9, -7.24) * mm});
            skLineSegment(sketch, "E835", {"start": v(-12.9, -7.24) * mm, "end": v(-12.86, -7.24) * mm});
            skLineSegment(sketch, "E836", {"start": v(-12.86, -7.24) * mm, "end": v(-12.83, -7.25) * mm});
            skLineSegment(sketch, "E837", {"start": v(-12.83, -7.25) * mm, "end": v(-12.81, -7.26) * mm});
            skLineSegment(sketch, "E838", {"start": v(-12.81, -7.26) * mm, "end": v(-12.8, -7.28) * mm});
            skLineSegment(sketch, "E839", {"start": v(-12.8, -7.28) * mm, "end": v(-12.48, -7.8) * mm});
            skLineSegment(sketch, "E840", {"start": v(-12.48, -7.8) * mm, "end": v(-12.48, -7.83) * mm});
            skLineSegment(sketch, "E841", {"start": v(-12.48, -7.83) * mm, "end": v(-12.47, -7.85) * mm});
            skLineSegment(sketch, "E842", {"start": v(-12.47, -7.85) * mm, "end": v(-12.48, -7.88) * mm});
            skLineSegment(sketch, "E843", {"start": v(-12.48, -7.88) * mm, "end": v(-12.5, -7.9) * mm});
            skLineSegment(sketch, "E844", {"start": v(-12.5, -7.9) * mm, "end": v(-12.5, -7.97) * mm});
            skLineSegment(sketch, "E845", {"start": v(-12.5, -7.97) * mm, "end": v(-12.6, -8.05) * mm});
            skLineSegment(sketch, "E846", {"start": v(-12.6, -8.05) * mm, "end": v(-12.7, -8.15) * mm});
            skLineSegment(sketch, "E847", {"start": v(-12.7, -8.15) * mm, "end": v(-12.8, -8.25) * mm});
            skLineSegment(sketch, "E848", {"start": v(-12.8, -8.25) * mm, "end": v(-12.9, -8.35) * mm});
            skLineSegment(sketch, "E849", {"start": v(-12.9, -8.35) * mm, "end": v(-13, -8.46) * mm});
            skLineSegment(sketch, "E850", {"start": v(-13, -8.46) * mm, "end": v(-13.08, -8.57) * mm});
            skLineSegment(sketch, "E851", {"start": v(-13.08, -8.57) * mm, "end": v(-13.16, -8.68) * mm});
            skLineSegment(sketch, "E852", {"start": v(-13.16, -8.68) * mm, "end": v(-13.25, -8.8) * mm});
            skLineSegment(sketch, "E853", {"start": v(-13.25, -8.8) * mm, "end": v(-13.33, -8.9) * mm});
            skLineSegment(sketch, "E854", {"start": v(-13.33, -8.9) * mm, "end": v(-13.4, -9.03) * mm});
            skLineSegment(sketch, "E855", {"start": v(-13.4, -9.03) * mm, "end": v(-13.48, -9.15) * mm});
            skLineSegment(sketch, "E856", {"start": v(-13.48, -9.15) * mm, "end": v(-13.55, -9.27) * mm});
            skLineSegment(sketch, "E857", {"start": v(-13.55, -9.27) * mm, "end": v(-13.62, -9.39) * mm});
            skLineSegment(sketch, "E858", {"start": v(-13.62, -9.39) * mm, "end": v(-13.69, -9.51) * mm});
            skLineSegment(sketch, "E859", {"start": v(-13.69, -9.51) * mm, "end": v(-13.29, -10.06) * mm});
            skLineSegment(sketch, "E860", {"start": v(-13.29, -10.06) * mm, "end": v(-13.15, -10.03) * mm});
            skLineSegment(sketch, "E861", {"start": v(-13.15, -10.03) * mm, "end": v(-13.01, -10) * mm});
            skLineSegment(sketch, "E862", {"start": v(-13.01, -10) * mm, "end": v(-12.88, -9.97) * mm});
            skLineSegment(sketch, "E863", {"start": v(-12.88, -9.97) * mm, "end": v(-12.74, -9.94) * mm});
            skLineSegment(sketch, "E864", {"start": v(-12.74, -9.94) * mm, "end": v(-12.6, -9.9) * mm});
            skLineSegment(sketch, "E865", {"start": v(-12.6, -9.9) * mm, "end": v(-12.47, -9.86) * mm});
            skLineSegment(sketch, "E866", {"start": v(-12.47, -9.86) * mm, "end": v(-12.34, -9.82) * mm});
            skLineSegment(sketch, "E867", {"start": v(-12.34, -9.82) * mm, "end": v(-12.2, -9.77) * mm});
            skLineSegment(sketch, "E868", {"start": v(-12.2, -9.77) * mm, "end": v(-12.07, -9.72) * mm});
            skLineSegment(sketch, "E869", {"start": v(-12.07, -9.72) * mm, "end": v(-11.94, -9.67) * mm});
            skLineSegment(sketch, "E870", {"start": v(-11.94, -9.67) * mm, "end": v(-11.81, -9.61) * mm});
            skLineSegment(sketch, "E871", {"start": v(-11.81, -9.61) * mm, "end": v(-11.69, -9.55) * mm});
            skLineSegment(sketch, "E872", {"start": v(-11.69, -9.55) * mm, "end": v(-11.57, -9.48) * mm});
            skLineSegment(sketch, "E873", {"start": v(-11.57, -9.48) * mm, "end": v(-11.45, -9.4) * mm});
            skLineSegment(sketch, "E874", {"start": v(-11.45, -9.4) * mm, "end": v(-11.4, -9.42) * mm});
            skLineSegment(sketch, "E875", {"start": v(-11.4, -9.42) * mm, "end": v(-11.36, -9.42) * mm});
            skLineSegment(sketch, "E876", {"start": v(-11.36, -9.42) * mm, "end": v(-11.33, -9.42) * mm});
            skLineSegment(sketch, "E877", {"start": v(-11.33, -9.42) * mm, "end": v(-11.31, -9.43) * mm});
            skLineSegment(sketch, "E878", {"start": v(-11.31, -9.43) * mm, "end": v(-11.3, -9.44) * mm});
            skLineSegment(sketch, "E879", {"start": v(-11.3, -9.44) * mm, "end": v(-10.9, -9.9) * mm});
            skLineSegment(sketch, "E880", {"start": v(-10.9, -9.9) * mm, "end": v(-10.88, -9.92) * mm});
            skLineSegment(sketch, "E881", {"start": v(-10.88, -9.92) * mm, "end": v(-10.87, -9.95) * mm});
            skLineSegment(sketch, "E882", {"start": v(-10.87, -9.95) * mm, "end": v(-10.87, -9.98) * mm});
            skLineSegment(sketch, "E883", {"start": v(-10.87, -9.98) * mm, "end": v(-10.88, -10) * mm});
            skLineSegment(sketch, "E884", {"start": v(-10.88, -10) * mm, "end": v(-10.87, -10.07) * mm});
            skLineSegment(sketch, "E885", {"start": v(-10.87, -10.07) * mm, "end": v(-10.96, -10.17) * mm});
            skLineSegment(sketch, "E886", {"start": v(-10.96, -10.17) * mm, "end": v(-11.05, -10.28) * mm});
            skLineSegment(sketch, "E887", {"start": v(-11.05, -10.28) * mm, "end": v(-11.13, -10.4) * mm});
            skLineSegment(sketch, "E888", {"start": v(-11.13, -10.4) * mm, "end": v(-11.2, -10.52) * mm});
            skLineSegment(sketch, "E889", {"start": v(-11.2, -10.52) * mm, "end": v(-11.27, -10.64) * mm});
            skLineSegment(sketch, "E890", {"start": v(-11.27, -10.64) * mm, "end": v(-11.34, -10.76) * mm});
            skLineSegment(sketch, "E891", {"start": v(-11.34, -10.76) * mm, "end": v(-11.4, -10.89) * mm});
            skLineSegment(sketch, "E892", {"start": v(-11.4, -10.89) * mm, "end": v(-11.46, -11.01) * mm});
            skLineSegment(sketch, "E893", {"start": v(-11.46, -11.01) * mm, "end": v(-11.52, -11.14) * mm});
            skLineSegment(sketch, "E894", {"start": v(-11.52, -11.14) * mm, "end": v(-11.58, -11.27) * mm});
            skLineSegment(sketch, "E895", {"start": v(-11.58, -11.27) * mm, "end": v(-11.63, -11.4) * mm});
            skLineSegment(sketch, "E896", {"start": v(-11.63, -11.4) * mm, "end": v(-11.68, -11.53) * mm});
            skLineSegment(sketch, "E897", {"start": v(-11.68, -11.53) * mm, "end": v(-11.72, -11.67) * mm});
            skLineSegment(sketch, "E898", {"start": v(-11.72, -11.67) * mm, "end": v(-11.77, -11.8) * mm});
            skLineSegment(sketch, "E899", {"start": v(-11.77, -11.8) * mm, "end": v(-11.28, -12.27) * mm});
            skLineSegment(sketch, "E900", {"start": v(-11.28, -12.27) * mm, "end": v(-11.15, -12.22) * mm});
            skLineSegment(sketch, "E901", {"start": v(-11.15, -12.22) * mm, "end": v(-11.02, -12.16) * mm});
            skLineSegment(sketch, "E902", {"start": v(-11.02, -12.16) * mm, "end": v(-10.89, -12.1) * mm});
            skLineSegment(sketch, "E903", {"start": v(-10.89, -12.1) * mm, "end": v(-10.76, -12.05) * mm});
            skLineSegment(sketch, "E904", {"start": v(-10.76, -12.05) * mm, "end": v(-10.63, -12) * mm});
            skLineSegment(sketch, "E905", {"start": v(-10.63, -12) * mm, "end": v(-10.5, -11.93) * mm});
            skLineSegment(sketch, "E906", {"start": v(-10.5, -11.93) * mm, "end": v(-10.38, -11.86) * mm});
            skLineSegment(sketch, "E907", {"start": v(-10.38, -11.86) * mm, "end": v(-10.26, -11.8) * mm});
            skLineSegment(sketch, "E908", {"start": v(-10.26, -11.8) * mm, "end": v(-10.14, -11.72) * mm});
            skLineSegment(sketch, "E909", {"start": v(-10.14, -11.72) * mm, "end": v(-10.02, -11.64) * mm});
            skLineSegment(sketch, "E910", {"start": v(-10.02, -11.64) * mm, "end": v(-9.9, -11.56) * mm});
            skLineSegment(sketch, "E911", {"start": v(-9.9, -11.56) * mm, "end": v(-9.8, -11.48) * mm});
            skLineSegment(sketch, "E912", {"start": v(-9.8, -11.48) * mm, "end": v(-9.69, -11.39) * mm});
            skLineSegment(sketch, "E913", {"start": v(-9.69, -11.39) * mm, "end": v(-9.59, -11.29) * mm});
            skLineSegment(sketch, "E914", {"start": v(-9.59, -11.29) * mm, "end": v(-9.53, -11.3) * mm});
            skLineSegment(sketch, "E915", {"start": v(-9.53, -11.3) * mm, "end": v(-9.5, -11.3) * mm});
            skLineSegment(sketch, "E916", {"start": v(-9.5, -11.3) * mm, "end": v(-9.47, -11.29) * mm});
            skLineSegment(sketch, "E917", {"start": v(-9.47, -11.29) * mm, "end": v(-9.45, -11.3) * mm});
            skLineSegment(sketch, "E918", {"start": v(-9.45, -11.3) * mm, "end": v(-9.43, -11.3) * mm});
            skLineSegment(sketch, "E919", {"start": v(-9.43, -11.3) * mm, "end": v(-8.95, -11.69) * mm});
            skLineSegment(sketch, "E920", {"start": v(-8.95, -11.69) * mm, "end": v(-8.93, -11.7) * mm});
            skLineSegment(sketch, "E921", {"start": v(-8.93, -11.7) * mm, "end": v(-8.92, -11.73) * mm});
            skLineSegment(sketch, "E922", {"start": v(-8.92, -11.73) * mm, "end": v(-8.92, -11.75) * mm});
            skLineSegment(sketch, "E923", {"start": v(-8.92, -11.75) * mm, "end": v(-8.92, -11.79) * mm});
            skLineSegment(sketch, "E924", {"start": v(-8.92, -11.79) * mm, "end": v(-8.9, -11.84) * mm});
            skLineSegment(sketch, "E925", {"start": v(-8.9, -11.84) * mm, "end": v(-8.97, -11.96) * mm});
            skLineSegment(sketch, "E926", {"start": v(-8.97, -11.96) * mm, "end": v(-9.03, -12.09) * mm});
            skLineSegment(sketch, "E927", {"start": v(-9.03, -12.09) * mm, "end": v(-9.1, -12.22) * mm});
            skLineSegment(sketch, "E928", {"start": v(-9.1, -12.22) * mm, "end": v(-9.14, -12.35) * mm});
            skLineSegment(sketch, "E929", {"start": v(-9.14, -12.35) * mm, "end": v(-9.2, -12.48) * mm});
            skLineSegment(sketch, "E930", {"start": v(-9.2, -12.48) * mm, "end": v(-9.24, -12.61) * mm});
            skLineSegment(sketch, "E931", {"start": v(-9.24, -12.61) * mm, "end": v(-9.28, -12.75) * mm});
            skLineSegment(sketch, "E932", {"start": v(-9.28, -12.75) * mm, "end": v(-9.31, -12.88) * mm});
            skLineSegment(sketch, "E933", {"start": v(-9.31, -12.88) * mm, "end": v(-9.35, -13.02) * mm});
            skLineSegment(sketch, "E934", {"start": v(-9.35, -13.02) * mm, "end": v(-9.38, -13.15) * mm});
            skLineSegment(sketch, "E935", {"start": v(-9.38, -13.15) * mm, "end": v(-9.4, -13.3) * mm});
            skLineSegment(sketch, "E936", {"start": v(-9.4, -13.3) * mm, "end": v(-9.43, -13.43) * mm});
            skLineSegment(sketch, "E937", {"start": v(-9.43, -13.43) * mm, "end": v(-9.45, -13.57) * mm});
            skLineSegment(sketch, "E938", {"start": v(-9.45, -13.57) * mm, "end": v(-9.47, -13.7) * mm});
            skLineSegment(sketch, "E939", {"start": v(-9.47, -13.7) * mm, "end": v(-8.9, -14.08) * mm});
            skLineSegment(sketch, "E940", {"start": v(-8.9, -14.08) * mm, "end": v(-8.79, -14) * mm});
            skLineSegment(sketch, "E941", {"start": v(-8.79, -14) * mm, "end": v(-8.67, -13.93) * mm});
            skLineSegment(sketch, "E942", {"start": v(-8.67, -13.93) * mm, "end": v(-8.55, -13.86) * mm});
            skLineSegment(sketch, "E943", {"start": v(-8.55, -13.86) * mm, "end": v(-8.44, -13.78) * mm});
            skLineSegment(sketch, "E944", {"start": v(-8.44, -13.78) * mm, "end": v(-8.32, -13.7) * mm});
            skLineSegment(sketch, "E945", {"start": v(-8.32, -13.7) * mm, "end": v(-8.2, -13.6) * mm});
            skLineSegment(sketch, "E946", {"start": v(-8.2, -13.6) * mm, "end": v(-8.1, -13.52) * mm});
            skLineSegment(sketch, "E947", {"start": v(-8.1, -13.52) * mm, "end": v(-8, -13.43) * mm});
            skLineSegment(sketch, "E948", {"start": v(-8, -13.43) * mm, "end": v(-7.89, -13.34) * mm});
            skLineSegment(sketch, "E949", {"start": v(-7.89, -13.34) * mm, "end": v(-7.78, -13.24) * mm});
            skLineSegment(sketch, "E950", {"start": v(-7.78, -13.24) * mm, "end": v(-7.68, -13.14) * mm});
            skLineSegment(sketch, "E951", {"start": v(-7.68, -13.14) * mm, "end": v(-7.59, -13.04) * mm});
            skLineSegment(sketch, "E952", {"start": v(-7.59, -13.04) * mm, "end": v(-7.5, -12.93) * mm});
            skLineSegment(sketch, "E953", {"start": v(-7.5, -12.93) * mm, "end": v(-7.42, -12.82) * mm});
            skLineSegment(sketch, "E954", {"start": v(-7.42, -12.82) * mm, "end": v(-7.36, -12.81) * mm});
            skLineSegment(sketch, "E955", {"start": v(-7.36, -12.81) * mm, "end": v(-7.33, -12.8) * mm});
            skLineSegment(sketch, "E956", {"start": v(-7.33, -12.8) * mm, "end": v(-7.3, -12.8) * mm});
            skLineSegment(sketch, "E957", {"start": v(-7.3, -12.8) * mm, "end": v(-7.28, -12.8) * mm});
            skLineSegment(sketch, "E958", {"start": v(-7.28, -12.8) * mm, "end": v(-7.26, -12.8) * mm});
            skLineSegment(sketch, "E959", {"start": v(-7.26, -12.8) * mm, "end": v(-6.72, -13.1) * mm});
            skLineSegment(sketch, "E960", {"start": v(-6.72, -13.1) * mm, "end": v(-6.7, -13.1) * mm});
            skLineSegment(sketch, "E961", {"start": v(-6.7, -13.1) * mm, "end": v(-6.69, -13.13) * mm});
            skLineSegment(sketch, "E962", {"start": v(-6.69, -13.13) * mm, "end": v(-6.68, -13.15) * mm});
            skLineSegment(sketch, "E963", {"start": v(-6.68, -13.15) * mm, "end": v(-6.67, -13.19) * mm});
            skLineSegment(sketch, "E964", {"start": v(-6.67, -13.19) * mm, "end": v(-6.64, -13.24) * mm});
            skLineSegment(sketch, "E965", {"start": v(-6.64, -13.24) * mm, "end": v(-6.69, -13.37) * mm});
            skLineSegment(sketch, "E966", {"start": v(-6.69, -13.37) * mm, "end": v(-6.73, -13.5) * mm});
            skLineSegment(sketch, "E967", {"start": v(-6.73, -13.5) * mm, "end": v(-6.76, -13.64) * mm});
            skLineSegment(sketch, "E968", {"start": v(-6.76, -13.64) * mm, "end": v(-6.8, -13.78) * mm});
            skLineSegment(sketch, "E969", {"start": v(-6.8, -13.78) * mm, "end": v(-6.82, -13.91) * mm});
            skLineSegment(sketch, "E970", {"start": v(-6.82, -13.91) * mm, "end": v(-6.84, -14.05) * mm});
            skLineSegment(sketch, "E971", {"start": v(-6.84, -14.05) * mm, "end": v(-6.85, -14.2) * mm});
            skLineSegment(sketch, "E972", {"start": v(-6.85, -14.2) * mm, "end": v(-6.86, -14.33) * mm});
            skLineSegment(sketch, "E973", {"start": v(-6.86, -14.33) * mm, "end": v(-6.87, -14.47) * mm});
            skLineSegment(sketch, "E974", {"start": v(-6.87, -14.47) * mm, "end": v(-6.88, -14.61) * mm});
            skLineSegment(sketch, "E975", {"start": v(-6.88, -14.61) * mm, "end": v(-6.88, -14.75) * mm});
            skLineSegment(sketch, "E976", {"start": v(-6.88, -14.75) * mm, "end": v(-6.88, -14.9) * mm});
            skLineSegment(sketch, "E977", {"start": v(-6.88, -14.9) * mm, "end": v(-6.88, -15.04) * mm});
            skLineSegment(sketch, "E978", {"start": v(-6.88, -15.04) * mm, "end": v(-6.87, -15.18) * mm});
            skLineSegment(sketch, "E979", {"start": v(-6.87, -15.18) * mm, "end": v(-6.25, -15.44) * mm});
            skLineSegment(sketch, "E980", {"start": v(-6.25, -15.44) * mm, "end": v(-6.15, -15.35) * mm});
            skLineSegment(sketch, "E981", {"start": v(-6.15, -15.35) * mm, "end": v(-6.04, -15.25) * mm});
            skLineSegment(sketch, "E982", {"start": v(-6.04, -15.25) * mm, "end": v(-5.94, -15.16) * mm});
            skLineSegment(sketch, "E983", {"start": v(-5.94, -15.16) * mm, "end": v(-5.84, -15.06) * mm});
            skLineSegment(sketch, "E984", {"start": v(-5.84, -15.06) * mm, "end": v(-5.74, -14.96) * mm});
            skLineSegment(sketch, "E985", {"start": v(-5.74, -14.96) * mm, "end": v(-5.65, -14.85) * mm});
            skLineSegment(sketch, "E986", {"start": v(-5.65, -14.85) * mm, "end": v(-5.55, -14.75) * mm});
            skLineSegment(sketch, "E987", {"start": v(-5.55, -14.75) * mm, "end": v(-5.46, -14.64) * mm});
            skLineSegment(sketch, "E988", {"start": v(-5.46, -14.64) * mm, "end": v(-5.38, -14.53) * mm});
            skLineSegment(sketch, "E989", {"start": v(-5.38, -14.53) * mm, "end": v(-5.3, -14.42) * mm});
            skLineSegment(sketch, "E990", {"start": v(-5.3, -14.42) * mm, "end": v(-5.21, -14.3) * mm});
            skLineSegment(sketch, "E991", {"start": v(-5.21, -14.3) * mm, "end": v(-5.14, -14.18) * mm});
            skLineSegment(sketch, "E992", {"start": v(-5.14, -14.18) * mm, "end": v(-5.07, -14.06) * mm});
            skLineSegment(sketch, "E993", {"start": v(-5.07, -14.06) * mm, "end": v(-5.01, -13.93) * mm});
            skLineSegment(sketch, "E994", {"start": v(-5.01, -13.93) * mm, "end": v(-4.95, -13.92) * mm});
            skLineSegment(sketch, "E995", {"start": v(-4.95, -13.92) * mm, "end": v(-4.93, -13.9) * mm});
            skLineSegment(sketch, "E996", {"start": v(-4.93, -13.9) * mm, "end": v(-4.9, -13.9) * mm});
            skLineSegment(sketch, "E997", {"start": v(-4.9, -13.9) * mm, "end": v(-4.88, -13.89) * mm});
            skLineSegment(sketch, "E998", {"start": v(-4.88, -13.89) * mm, "end": v(-4.85, -13.9) * mm});
            skLineSegment(sketch, "E999", {"start": v(-4.85, -13.9) * mm, "end": v(-4.27, -14.08) * mm});
            skLineSegment(sketch, "E1000", {"start": v(-4.27, -14.08) * mm, "end": v(-4.25, -14.1) * mm});
            skLineSegment(sketch, "E1001", {"start": v(-4.25, -14.1) * mm, "end": v(-4.23, -14.1) * mm});
            skLineSegment(sketch, "E1002", {"start": v(-4.23, -14.1) * mm, "end": v(-4.22, -14.13) * mm});
            skLineSegment(sketch, "E1003", {"start": v(-4.22, -14.13) * mm, "end": v(-4.2, -14.16) * mm});
            skLineSegment(sketch, "E1004", {"start": v(-4.2, -14.16) * mm, "end": v(-4.17, -14.2) * mm});
            skLineSegment(sketch, "E1005", {"start": v(-4.17, -14.2) * mm, "end": v(-4.2, -14.34) * mm});
            skLineSegment(sketch, "E1006", {"start": v(-4.2, -14.34) * mm, "end": v(-4.21, -14.48) * mm});
            skLineSegment(sketch, "E1007", {"start": v(-4.21, -14.48) * mm, "end": v(-4.22, -14.62) * mm});
            skLineSegment(sketch, "E1008", {"start": v(-4.22, -14.62) * mm, "end": v(-4.22, -14.76) * mm});
            skLineSegment(sketch, "E1009", {"start": v(-4.22, -14.76) * mm, "end": v(-4.22, -14.9) * mm});
            skLineSegment(sketch, "E1010", {"start": v(-4.22, -14.9) * mm, "end": v(-4.22, -15.05) * mm});
            skLineSegment(sketch, "E1011", {"start": v(-4.22, -15.05) * mm, "end": v(-4.2, -15.19) * mm});
            skLineSegment(sketch, "E1012", {"start": v(-4.2, -15.19) * mm, "end": v(-4.2, -15.33) * mm});
            skLineSegment(sketch, "E1013", {"start": v(-4.2, -15.33) * mm, "end": v(-4.18, -15.47) * mm});
            skLineSegment(sketch, "E1014", {"start": v(-4.18, -15.47) * mm, "end": v(-4.16, -15.6) * mm});
            skLineSegment(sketch, "E1015", {"start": v(-4.16, -15.6) * mm, "end": v(-4.14, -15.74) * mm});
            skLineSegment(sketch, "E1016", {"start": v(-4.14, -15.74) * mm, "end": v(-4.11, -15.88) * mm});
            skLineSegment(sketch, "E1017", {"start": v(-4.11, -15.88) * mm, "end": v(-4.08, -16.02) * mm});
            skLineSegment(sketch, "E1018", {"start": v(-4.08, -16.02) * mm, "end": v(-4.05, -16.16) * mm});
            skLineSegment(sketch, "E1019", {"start": v(-4.05, -16.16) * mm, "end": v(-3.4, -16.3) * mm});
            skLineSegment(sketch, "E1020", {"start": v(-3.4, -16.3) * mm, "end": v(-3.3, -16.2) * mm});
            skLineSegment(sketch, "E1021", {"start": v(-3.3, -16.2) * mm, "end": v(-3.22, -16.08) * mm});
            skLineSegment(sketch, "E1022", {"start": v(-3.22, -16.08) * mm, "end": v(-3.14, -15.97) * mm});
            skLineSegment(sketch, "E1023", {"start": v(-3.14, -15.97) * mm, "end": v(-3.06, -15.86) * mm});
            skLineSegment(sketch, "E1024", {"start": v(-3.06, -15.86) * mm, "end": v(-2.98, -15.74) * mm});
            skLineSegment(sketch, "E1025", {"start": v(-2.98, -15.74) * mm, "end": v(-2.9, -15.62) * mm});
            skLineSegment(sketch, "E1026", {"start": v(-2.9, -15.62) * mm, "end": v(-2.83, -15.5) * mm});
            skLineSegment(sketch, "E1027", {"start": v(-2.83, -15.5) * mm, "end": v(-2.76, -15.38) * mm});
            skLineSegment(sketch, "E1028", {"start": v(-2.76, -15.38) * mm, "end": v(-2.7, -15.25) * mm});
            skLineSegment(sketch, "E1029", {"start": v(-2.7, -15.25) * mm, "end": v(-2.64, -15.13) * mm});
            skLineSegment(sketch, "E1030", {"start": v(-2.64, -15.13) * mm, "end": v(-2.58, -15) * mm});
            skLineSegment(sketch, "E1031", {"start": v(-2.58, -15) * mm, "end": v(-2.53, -14.87) * mm});
            skLineSegment(sketch, "E1032", {"start": v(-2.53, -14.87) * mm, "end": v(-2.48, -14.74) * mm});
            skLineSegment(sketch, "E1033", {"start": v(-2.48, -14.74) * mm, "end": v(-2.44, -14.6) * mm});
            skLineSegment(sketch, "E1034", {"start": v(-2.44, -14.6) * mm, "end": v(-2.39, -14.58) * mm});
            skLineSegment(sketch, "E1035", {"start": v(-2.39, -14.58) * mm, "end": v(-2.36, -14.55) * mm});
            skLineSegment(sketch, "E1036", {"start": v(-2.36, -14.55) * mm, "end": v(-2.34, -14.54) * mm});
            skLineSegment(sketch, "E1037", {"start": v(-2.34, -14.54) * mm, "end": v(-2.32, -14.53) * mm});
            skLineSegment(sketch, "E1038", {"start": v(-2.32, -14.53) * mm, "end": v(-2.3, -14.53) * mm});
            skLineSegment(sketch, "E1039", {"start": v(-2.3, -14.53) * mm, "end": v(-1.69, -14.61) * mm});
            skLineSegment(sketch, "E1040", {"start": v(-1.69, -14.61) * mm, "end": v(-1.67, -14.62) * mm});
            skLineSegment(sketch, "E1041", {"start": v(-1.67, -14.62) * mm, "end": v(-1.65, -14.63) * mm});
            skLineSegment(sketch, "E1042", {"start": v(-1.65, -14.63) * mm, "end": v(-1.63, -14.65) * mm});
            skLineSegment(sketch, "E1043", {"start": v(-1.63, -14.65) * mm, "end": v(-1.61, -14.68) * mm});
            skLineSegment(sketch, "E1044", {"start": v(-1.61, -14.68) * mm, "end": v(-1.56, -14.72) * mm});
            skLineSegment(sketch, "E1045", {"start": v(-1.56, -14.72) * mm, "end": v(-1.57, -14.86) * mm});
            skLineSegment(sketch, "E1046", {"start": v(-1.57, -14.86) * mm, "end": v(-1.56, -15) * mm});
            skLineSegment(sketch, "E1047", {"start": v(-1.56, -15) * mm, "end": v(-1.54, -15.14) * mm});
            skLineSegment(sketch, "E1048", {"start": v(-1.54, -15.14) * mm, "end": v(-1.52, -15.28) * mm});
            skLineSegment(sketch, "E1049", {"start": v(-1.52, -15.28) * mm, "end": v(-1.5, -15.42) * mm});
            skLineSegment(sketch, "E1050", {"start": v(-1.5, -15.42) * mm, "end": v(-1.46, -15.55) * mm});
            skLineSegment(sketch, "E1051", {"start": v(-1.46, -15.55) * mm, "end": v(-1.43, -15.69) * mm});
            skLineSegment(sketch, "E1052", {"start": v(-1.43, -15.69) * mm, "end": v(-1.4, -15.82) * mm});
            skLineSegment(sketch, "E1053", {"start": v(-1.4, -15.82) * mm, "end": v(-1.35, -15.96) * mm});
            skLineSegment(sketch, "E1054", {"start": v(-1.35, -15.96) * mm, "end": v(-1.3, -16.1) * mm});
            skLineSegment(sketch, "E1055", {"start": v(-1.3, -16.1) * mm, "end": v(-1.26, -16.23) * mm});
            skLineSegment(sketch, "E1056", {"start": v(-1.26, -16.23) * mm, "end": v(-1.2, -16.36) * mm});
            skLineSegment(sketch, "E1057", {"start": v(-1.2, -16.36) * mm, "end": v(-1.16, -16.49) * mm});
            skLineSegment(sketch, "E1058", {"start": v(-1.16, -16.49) * mm, "end": v(-1.1, -16.62) * mm});
            skLineSegment(sketch, "E1059", {"start": v(-1.1, -16.62) * mm, "end": v(-0.43, -16.65) * mm});
            skLineSegment(sketch, "E1060", {"start": v(-0.43, -16.65) * mm, "end": v(-0.36, -16.52) * mm});
            skLineSegment(sketch, "E1061", {"start": v(-0.36, -16.52) * mm, "end": v(-0.3, -16.4) * mm});
            skLineSegment(sketch, "E1062", {"start": v(-0.3, -16.4) * mm, "end": v(-0.24, -16.27) * mm});
            skLineSegment(sketch, "E1063", {"start": v(-0.24, -16.27) * mm, "end": v(-0.18, -16.14) * mm});
            skLineSegment(sketch, "E1064", {"start": v(-0.18, -16.14) * mm, "end": v(-0.12, -16.01) * mm});
            skLineSegment(sketch, "E1065", {"start": v(-0.12, -16.01) * mm, "end": v(-0.07, -15.88) * mm});
            skLineSegment(sketch, "E1066", {"start": v(-0.07, -15.88) * mm, "end": v(-0.02, -15.75) * mm});
            skLineSegment(sketch, "E1067", {"start": v(-0.02, -15.75) * mm, "end": v(0.03, -15.62) * mm});
            skLineSegment(sketch, "E1068", {"start": v(0.03, -15.62) * mm, "end": v(0.07, -15.49) * mm});
            skLineSegment(sketch, "E1069", {"start": v(0.07, -15.49) * mm, "end": v(0.1, -15.35) * mm});
            skLineSegment(sketch, "E1070", {"start": v(0.1, -15.35) * mm, "end": v(0.14, -15.21) * mm});
            skLineSegment(sketch, "E1071", {"start": v(0.14, -15.21) * mm, "end": v(0.17, -15.08) * mm});
            skLineSegment(sketch, "E1072", {"start": v(0.17, -15.08) * mm, "end": v(0.2, -14.94) * mm});
            skLineSegment(sketch, "E1073", {"start": v(0.2, -14.94) * mm, "end": v(0.2, -14.8) * mm});
            skLineSegment(sketch, "E1074", {"start": v(0.2, -14.8) * mm, "end": v(0.25, -14.77) * mm});
            skLineSegment(sketch, "E1075", {"start": v(0.25, -14.77) * mm, "end": v(0.27, -14.74) * mm});
            skLineSegment(sketch, "E1076", {"start": v(0.27, -14.74) * mm, "end": v(0.3, -14.72) * mm});
            skLineSegment(sketch, "E1077", {"start": v(0.3, -14.72) * mm, "end": v(0.31, -14.7) * mm});
            skLineSegment(sketch, "E1078", {"start": v(0.31, -14.7) * mm, "end": v(0.33, -14.7) * mm});
            skLineSegment(sketch, "E1079", {"start": v(0.33, -14.7) * mm, "end": v(0.95, -14.68) * mm});
            skLineSegment(sketch, "E1080", {"start": v(0.95, -14.68) * mm, "end": v(0.97, -14.68) * mm});
            skLineSegment(sketch, "E1081", {"start": v(0.97, -14.68) * mm, "end": v(1, -14.69) * mm});
            skLineSegment(sketch, "E1082", {"start": v(1, -14.69) * mm, "end": v(1.01, -14.7) * mm});
            skLineSegment(sketch, "E1083", {"start": v(1.01, -14.7) * mm, "end": v(1.03, -14.73) * mm});
            skLineSegment(sketch, "E1084", {"start": v(1.03, -14.73) * mm, "end": v(1.09, -14.76) * mm});
            skLineSegment(sketch, "E1085", {"start": v(1.09, -14.76) * mm, "end": v(1.11, -14.9) * mm});
            skLineSegment(sketch, "E1086", {"start": v(1.11, -14.9) * mm, "end": v(1.15, -15.03) * mm});
            skLineSegment(sketch, "E1087", {"start": v(1.15, -15.03) * mm, "end": v(1.19, -15.17) * mm});
            skLineSegment(sketch, "E1088", {"start": v(1.19, -15.17) * mm, "end": v(1.23, -15.3) * mm});
            skLineSegment(sketch, "E1089", {"start": v(1.23, -15.3) * mm, "end": v(1.28, -15.43) * mm});
            skLineSegment(sketch, "E1090", {"start": v(1.28, -15.43) * mm, "end": v(1.34, -15.56) * mm});
            skLineSegment(sketch, "E1091", {"start": v(1.34, -15.56) * mm, "end": v(1.4, -15.69) * mm});
            skLineSegment(sketch, "E1092", {"start": v(1.4, -15.69) * mm, "end": v(1.46, -15.82) * mm});
            skLineSegment(sketch, "E1093", {"start": v(1.46, -15.82) * mm, "end": v(1.52, -15.94) * mm});
            skLineSegment(sketch, "E1094", {"start": v(1.52, -15.94) * mm, "end": v(1.59, -16.06) * mm});
            skLineSegment(sketch, "E1095", {"start": v(1.59, -16.06) * mm, "end": v(1.66, -16.19) * mm});
            skLineSegment(sketch, "E1096", {"start": v(1.66, -16.19) * mm, "end": v(1.73, -16.3) * mm});
            skLineSegment(sketch, "E1097", {"start": v(1.73, -16.3) * mm, "end": v(1.8, -16.43) * mm});
            skLineSegment(sketch, "E1098", {"start": v(1.8, -16.43) * mm, "end": v(1.88, -16.54) * mm});
            skLineSegment(sketch, "E1099", {"start": v(1.88, -16.54) * mm, "end": v(2.55, -16.45) * mm});
            skLineSegment(sketch, "E1100", {"start": v(2.55, -16.45) * mm, "end": v(2.6, -16.32) * mm});
            skLineSegment(sketch, "E1101", {"start": v(2.6, -16.32) * mm, "end": v(2.63, -16.18) * mm});
            skLineSegment(sketch, "E1102", {"start": v(2.63, -16.18) * mm, "end": v(2.67, -16.05) * mm});
            skLineSegment(sketch, "E1103", {"start": v(2.67, -16.05) * mm, "end": v(2.7, -15.91) * mm});
            skLineSegment(sketch, "E1104", {"start": v(2.7, -15.91) * mm, "end": v(2.74, -15.78) * mm});
            skLineSegment(sketch, "E1105", {"start": v(2.74, -15.78) * mm, "end": v(2.77, -15.64) * mm});
            skLineSegment(sketch, "E1106", {"start": v(2.77, -15.64) * mm, "end": v(2.8, -15.5) * mm});
            skLineSegment(sketch, "E1107", {"start": v(2.8, -15.5) * mm, "end": v(2.82, -15.36) * mm});
            skLineSegment(sketch, "E1108", {"start": v(2.82, -15.36) * mm, "end": v(2.83, -15.22) * mm});
            skLineSegment(sketch, "E1109", {"start": v(2.83, -15.22) * mm, "end": v(2.85, -15.08) * mm});
            skLineSegment(sketch, "E1110", {"start": v(2.85, -15.08) * mm, "end": v(2.86, -14.94) * mm});
            skLineSegment(sketch, "E1111", {"start": v(2.86, -14.94) * mm, "end": v(2.86, -14.8) * mm});
            skLineSegment(sketch, "E1112", {"start": v(2.86, -14.8) * mm, "end": v(2.86, -14.66) * mm});
            skLineSegment(sketch, "E1113", {"start": v(2.86, -14.66) * mm, "end": v(2.84, -14.52) * mm});
            skLineSegment(sketch, "E1114", {"start": v(2.84, -14.52) * mm, "end": v(2.88, -14.48) * mm});
            skLineSegment(sketch, "E1115", {"start": v(2.88, -14.48) * mm, "end": v(2.9, -14.45) * mm});
            skLineSegment(sketch, "E1116", {"start": v(2.9, -14.45) * mm, "end": v(2.92, -14.43) * mm});
            skLineSegment(sketch, "E1117", {"start": v(2.92, -14.43) * mm, "end": v(2.93, -14.41) * mm});
            skLineSegment(sketch, "E1118", {"start": v(2.93, -14.41) * mm, "end": v(2.95, -14.4) * mm});
            skLineSegment(sketch, "E1119", {"start": v(2.95, -14.4) * mm, "end": v(3.55, -14.27) * mm});
            skLineSegment(sketch, "E1120", {"start": v(3.55, -14.27) * mm, "end": v(3.57, -14.27) * mm});
            skLineSegment(sketch, "E1121", {"start": v(3.57, -14.27) * mm, "end": v(3.6, -14.27) * mm});
            skLineSegment(sketch, "E1122", {"start": v(3.6, -14.27) * mm, "end": v(3.62, -14.29) * mm});
            skLineSegment(sketch, "E1123", {"start": v(3.62, -14.29) * mm, "end": v(3.65, -14.3) * mm});
            skLineSegment(sketch, "E1124", {"start": v(3.65, -14.3) * mm, "end": v(3.7, -14.32) * mm});
            skLineSegment(sketch, "E1125", {"start": v(3.7, -14.32) * mm, "end": v(3.75, -14.46) * mm});
            skLineSegment(sketch, "E1126", {"start": v(3.75, -14.46) * mm, "end": v(3.81, -14.58) * mm});
            skLineSegment(sketch, "E1127", {"start": v(3.81, -14.58) * mm, "end": v(3.88, -14.7) * mm});
            skLineSegment(sketch, "E1128", {"start": v(3.88, -14.7) * mm, "end": v(3.94, -14.83) * mm});
            skLineSegment(sketch, "E1129", {"start": v(3.94, -14.83) * mm, "end": v(4.02, -14.95) * mm});
            skLineSegment(sketch, "E1130", {"start": v(4.02, -14.95) * mm, "end": v(4.1, -15.07) * mm});
            skLineSegment(sketch, "E1131", {"start": v(4.1, -15.07) * mm, "end": v(4.17, -15.19) * mm});
            skLineSegment(sketch, "E1132", {"start": v(4.17, -15.19) * mm, "end": v(4.26, -15.3) * mm});
            skLineSegment(sketch, "E1133", {"start": v(4.26, -15.3) * mm, "end": v(4.34, -15.4) * mm});
            skLineSegment(sketch, "E1134", {"start": v(4.34, -15.4) * mm, "end": v(4.43, -15.52) * mm});
            skLineSegment(sketch, "E1135", {"start": v(4.43, -15.52) * mm, "end": v(4.52, -15.63) * mm});
            skLineSegment(sketch, "E1136", {"start": v(4.52, -15.63) * mm, "end": v(4.61, -15.73) * mm});
            skLineSegment(sketch, "E1137", {"start": v(4.61, -15.73) * mm, "end": v(4.7, -15.84) * mm});
            skLineSegment(sketch, "E1138", {"start": v(4.7, -15.84) * mm, "end": v(4.8, -15.94) * mm});
            skLineSegment(sketch, "E1139", {"start": v(4.8, -15.94) * mm, "end": v(5.45, -15.73) * mm});
            skLineSegment(sketch, "E1140", {"start": v(5.45, -15.73) * mm, "end": v(5.47, -15.59) * mm});
            skLineSegment(sketch, "E1141", {"start": v(5.47, -15.59) * mm, "end": v(5.48, -15.45) * mm});
            skLineSegment(sketch, "E1142", {"start": v(5.48, -15.45) * mm, "end": v(5.5, -15.31) * mm});
            skLineSegment(sketch, "E1143", {"start": v(5.5, -15.31) * mm, "end": v(5.5, -15.17) * mm});
            skLineSegment(sketch, "E1144", {"start": v(5.5, -15.17) * mm, "end": v(5.51, -15.03) * mm});
            skLineSegment(sketch, "E1145", {"start": v(5.51, -15.03) * mm, "end": v(5.52, -14.89) * mm});
            skLineSegment(sketch, "E1146", {"start": v(5.52, -14.89) * mm, "end": v(5.52, -14.75) * mm});
            skLineSegment(sketch, "E1147", {"start": v(5.52, -14.75) * mm, "end": v(5.51, -14.6) * mm});
            skLineSegment(sketch, "E1148", {"start": v(5.51, -14.6) * mm, "end": v(5.5, -14.47) * mm});
            skLineSegment(sketch, "E1149", {"start": v(5.5, -14.47) * mm, "end": v(5.5, -14.33) * mm});
            skLineSegment(sketch, "E1150", {"start": v(5.5, -14.33) * mm, "end": v(5.48, -14.19) * mm});
            skLineSegment(sketch, "E1151", {"start": v(5.48, -14.19) * mm, "end": v(5.46, -14.05) * mm});
            skLineSegment(sketch, "E1152", {"start": v(5.46, -14.05) * mm, "end": v(5.43, -13.91) * mm});
            skLineSegment(sketch, "E1153", {"start": v(5.43, -13.91) * mm, "end": v(5.39, -13.78) * mm});
            skLineSegment(sketch, "E1154", {"start": v(5.39, -13.78) * mm, "end": v(5.42, -13.73) * mm});
            skLineSegment(sketch, "E1155", {"start": v(5.42, -13.73) * mm, "end": v(5.43, -13.7) * mm});
            skLineSegment(sketch, "E1156", {"start": v(5.43, -13.7) * mm, "end": v(5.44, -13.67) * mm});
            skLineSegment(sketch, "E1157", {"start": v(5.44, -13.67) * mm, "end": v(5.46, -13.65) * mm});
            skLineSegment(sketch, "E1158", {"start": v(5.46, -13.65) * mm, "end": v(5.48, -13.64) * mm});
            skLineSegment(sketch, "E1159", {"start": v(5.48, -13.64) * mm, "end": v(6.04, -13.4) * mm});
            skLineSegment(sketch, "E1160", {"start": v(6.04, -13.4) * mm, "end": v(6.06, -13.4) * mm});
            skLineSegment(sketch, "E1161", {"start": v(6.06, -13.4) * mm, "end": v(6.09, -13.4) * mm});
            skLineSegment(sketch, "E1162", {"start": v(6.09, -13.4) * mm, "end": v(6.12, -13.4) * mm});
            skLineSegment(sketch, "E1163", {"start": v(6.12, -13.4) * mm, "end": v(6.14, -13.42) * mm});
            skLineSegment(sketch, "E1164", {"start": v(6.14, -13.42) * mm, "end": v(6.2, -13.43) * mm});
            skLineSegment(sketch, "E1165", {"start": v(6.2, -13.43) * mm, "end": v(6.27, -13.55) * mm});
            skLineSegment(sketch, "E1166", {"start": v(6.27, -13.55) * mm, "end": v(6.35, -13.67) * mm});
            skLineSegment(sketch, "E1167", {"start": v(6.35, -13.67) * mm, "end": v(6.44, -13.78) * mm});
            skLineSegment(sketch, "E1168", {"start": v(6.44, -13.78) * mm, "end": v(6.53, -13.89) * mm});
            skLineSegment(sketch, "E1169", {"start": v(6.53, -13.89) * mm, "end": v(6.62, -14) * mm});
            skLineSegment(sketch, "E1170", {"start": v(6.62, -14) * mm, "end": v(6.72, -14.1) * mm});
            skLineSegment(sketch, "E1171", {"start": v(6.72, -14.1) * mm, "end": v(6.82, -14.2) * mm});
            skLineSegment(sketch, "E1172", {"start": v(6.82, -14.2) * mm, "end": v(6.92, -14.29) * mm});
            skLineSegment(sketch, "E1173", {"start": v(6.92, -14.29) * mm, "end": v(7.02, -14.38) * mm});
            skLineSegment(sketch, "E1174", {"start": v(7.02, -14.38) * mm, "end": v(7.13, -14.48) * mm});
            skLineSegment(sketch, "E1175", {"start": v(7.13, -14.48) * mm, "end": v(7.24, -14.56) * mm});
            skLineSegment(sketch, "E1176", {"start": v(7.24, -14.56) * mm, "end": v(7.35, -14.65) * mm});
            skLineSegment(sketch, "E1177", {"start": v(7.35, -14.65) * mm, "end": v(7.46, -14.74) * mm});
            skLineSegment(sketch, "E1178", {"start": v(7.46, -14.74) * mm, "end": v(7.57, -14.82) * mm});
            skLineSegment(sketch, "E1179", {"start": v(7.57, -14.82) * mm, "end": v(8.17, -14.5) * mm});
            skLineSegment(sketch, "E1180", {"start": v(8.17, -14.5) * mm, "end": v(8.16, -14.36) * mm});
            skLineSegment(sketch, "E1181", {"start": v(8.16, -14.36) * mm, "end": v(8.15, -14.22) * mm});
            skLineSegment(sketch, "E1182", {"start": v(8.15, -14.22) * mm, "end": v(8.14, -14.08) * mm});
            skLineSegment(sketch, "E1183", {"start": v(8.14, -14.08) * mm, "end": v(8.12, -13.94) * mm});
            skLineSegment(sketch, "E1184", {"start": v(8.12, -13.94) * mm, "end": v(8.1, -13.8) * mm});
            skLineSegment(sketch, "E1185", {"start": v(8.1, -13.8) * mm, "end": v(8.08, -13.66) * mm});
            skLineSegment(sketch, "E1186", {"start": v(8.08, -13.66) * mm, "end": v(8.06, -13.52) * mm});
            skLineSegment(sketch, "E1187", {"start": v(8.06, -13.52) * mm, "end": v(8.03, -13.39) * mm});
            skLineSegment(sketch, "E1188", {"start": v(8.03, -13.39) * mm, "end": v(8, -13.25) * mm});
            skLineSegment(sketch, "E1189", {"start": v(8, -13.25) * mm, "end": v(7.96, -13.11) * mm});
            skLineSegment(sketch, "E1190", {"start": v(7.96, -13.11) * mm, "end": v(7.92, -12.98) * mm});
            skLineSegment(sketch, "E1191", {"start": v(7.92, -12.98) * mm, "end": v(7.88, -12.85) * mm});
            skLineSegment(sketch, "E1192", {"start": v(7.88, -12.85) * mm, "end": v(7.82, -12.72) * mm});
            skLineSegment(sketch, "E1193", {"start": v(7.82, -12.72) * mm, "end": v(7.76, -12.6) * mm});
            skLineSegment(sketch, "E1194", {"start": v(7.76, -12.6) * mm, "end": v(7.79, -12.54) * mm});
            skLineSegment(sketch, "E1195", {"start": v(7.79, -12.54) * mm, "end": v(7.8, -12.5) * mm});
            skLineSegment(sketch, "E1196", {"start": v(7.8, -12.5) * mm, "end": v(7.8, -12.48) * mm});
            skLineSegment(sketch, "E1197", {"start": v(7.8, -12.48) * mm, "end": v(7.81, -12.46) * mm});
            skLineSegment(sketch, "E1198", {"start": v(7.81, -12.46) * mm, "end": v(7.83, -12.44) * mm});
            skLineSegment(sketch, "E1199", {"start": v(7.83, -12.44) * mm, "end": v(8.34, -12.1) * mm});
            skLineSegment(sketch, "E1200", {"start": v(8.34, -12.1) * mm, "end": v(8.36, -12.1) * mm});
            skLineSegment(sketch, "E1201", {"start": v(8.36, -12.1) * mm, "end": v(8.38, -12.1) * mm});
            skLineSegment(sketch, "E1202", {"start": v(8.38, -12.1) * mm, "end": v(8.41, -12.1) * mm});
            skLineSegment(sketch, "E1203", {"start": v(8.41, -12.1) * mm, "end": v(8.44, -12.1) * mm});
            skLineSegment(sketch, "E1204", {"start": v(8.44, -12.1) * mm, "end": v(8.5, -12.1) * mm});
            skLineSegment(sketch, "E1205", {"start": v(8.5, -12.1) * mm, "end": v(8.6, -12.2) * mm});
            skLineSegment(sketch, "E1206", {"start": v(8.6, -12.2) * mm, "end": v(8.7, -12.3) * mm});
            skLineSegment(sketch, "E1207", {"start": v(8.7, -12.3) * mm, "end": v(8.8, -12.4) * mm});
            skLineSegment(sketch, "E1208", {"start": v(8.8, -12.4) * mm, "end": v(8.9, -12.5) * mm});
            skLineSegment(sketch, "E1209", {"start": v(8.9, -12.5) * mm, "end": v(9.01, -12.58) * mm});
            skLineSegment(sketch, "E1210", {"start": v(9.01, -12.58) * mm, "end": v(9.13, -12.66) * mm});
            skLineSegment(sketch, "E1211", {"start": v(9.13, -12.66) * mm, "end": v(9.24, -12.74) * mm});
            skLineSegment(sketch, "E1212", {"start": v(9.24, -12.74) * mm, "end": v(9.36, -12.82) * mm});
            skLineSegment(sketch, "E1213", {"start": v(9.36, -12.82) * mm, "end": v(9.48, -12.9) * mm});
            skLineSegment(sketch, "E1214", {"start": v(9.48, -12.9) * mm, "end": v(9.6, -12.97) * mm});
            skLineSegment(sketch, "E1215", {"start": v(9.6, -12.97) * mm, "end": v(9.72, -13.03) * mm});
            skLineSegment(sketch, "E1216", {"start": v(9.72, -13.03) * mm, "end": v(9.85, -13.1) * mm});
            skLineSegment(sketch, "E1217", {"start": v(9.85, -13.1) * mm, "end": v(9.97, -13.16) * mm});
            skLineSegment(sketch, "E1218", {"start": v(9.97, -13.16) * mm, "end": v(10.1, -13.23) * mm});
            skLineSegment(sketch, "E1219", {"start": v(10.1, -13.23) * mm, "end": v(10.62, -12.8) * mm});
            skLineSegment(sketch, "E1220", {"start": v(10.62, -12.8) * mm, "end": v(10.6, -12.67) * mm});
            skLineSegment(sketch, "E1221", {"start": v(10.6, -12.67) * mm, "end": v(10.56, -12.53) * mm});
            skLineSegment(sketch, "E1222", {"start": v(10.56, -12.53) * mm, "end": v(10.52, -12.4) * mm});
            skLineSegment(sketch, "E1223", {"start": v(10.52, -12.4) * mm, "end": v(10.48, -12.26) * mm});
            skLineSegment(sketch, "E1224", {"start": v(10.48, -12.26) * mm, "end": v(10.44, -12.13) * mm});
            skLineSegment(sketch, "E1225", {"start": v(10.44, -12.13) * mm, "end": v(10.4, -12) * mm});
            skLineSegment(sketch, "E1226", {"start": v(10.4, -12) * mm, "end": v(10.35, -11.86) * mm});
            skLineSegment(sketch, "E1227", {"start": v(10.35, -11.86) * mm, "end": v(10.3, -11.73) * mm});
            skLineSegment(sketch, "E1228", {"start": v(10.3, -11.73) * mm, "end": v(10.24, -11.6) * mm});
            skLineSegment(sketch, "E1229", {"start": v(10.24, -11.6) * mm, "end": v(10.18, -11.48) * mm});
            skLineSegment(sketch, "E1230", {"start": v(10.18, -11.48) * mm, "end": v(10.11, -11.35) * mm});
            skLineSegment(sketch, "E1231", {"start": v(10.11, -11.35) * mm, "end": v(10.04, -11.23) * mm});
            skLineSegment(sketch, "E1232", {"start": v(10.04, -11.23) * mm, "end": v(9.97, -11.11) * mm});
            skLineSegment(sketch, "E1233", {"start": v(9.97, -11.11) * mm, "end": v(9.88, -11) * mm});
            skLineSegment(sketch, "E1234", {"start": v(9.88, -11) * mm, "end": v(9.9, -10.94) * mm});
            skLineSegment(sketch, "E1235", {"start": v(9.9, -10.94) * mm, "end": v(9.9, -10.9) * mm});
            skLineSegment(sketch, "E1236", {"start": v(9.9, -10.9) * mm, "end": v(9.9, -10.88) * mm});
            skLineSegment(sketch, "E1237", {"start": v(9.9, -10.88) * mm, "end": v(9.9, -10.86) * mm});
            skLineSegment(sketch, "E1238", {"start": v(9.9, -10.86) * mm, "end": v(9.92, -10.84) * mm});
            skLineSegment(sketch, "E1239", {"start": v(9.92, -10.84) * mm, "end": v(10.37, -10.42) * mm});
            skLineSegment(sketch, "E1240", {"start": v(10.37, -10.42) * mm, "end": v(10.38, -10.4) * mm});
            skLineSegment(sketch, "E1241", {"start": v(10.38, -10.4) * mm, "end": v(10.4, -10.4) * mm});
            skLineSegment(sketch, "E1242", {"start": v(10.4, -10.4) * mm, "end": v(10.43, -10.4) * mm});
            skLineSegment(sketch, "E1243", {"start": v(10.43, -10.4) * mm, "end": v(10.47, -10.4) * mm});
            skLineSegment(sketch, "E1244", {"start": v(10.47, -10.4) * mm, "end": v(10.53, -10.39) * mm});
            skLineSegment(sketch, "E1245", {"start": v(10.53, -10.39) * mm, "end": v(10.63, -10.48) * mm});
            skLineSegment(sketch, "E1246", {"start": v(10.63, -10.48) * mm, "end": v(10.75, -10.56) * mm});
            skLineSegment(sketch, "E1247", {"start": v(10.75, -10.56) * mm, "end": v(10.87, -10.63) * mm});
            skLineSegment(sketch, "E1248", {"start": v(10.87, -10.63) * mm, "end": v(11, -10.7) * mm});
            skLineSegment(sketch, "E1249", {"start": v(11, -10.7) * mm, "end": v(11.11, -10.77) * mm});
            skLineSegment(sketch, "E1250", {"start": v(11.11, -10.77) * mm, "end": v(11.24, -10.83) * mm});
            skLineSegment(sketch, "E1251", {"start": v(11.24, -10.83) * mm, "end": v(11.37, -10.89) * mm});
            skLineSegment(sketch, "E1252", {"start": v(11.37, -10.89) * mm, "end": v(11.5, -10.94) * mm});
            skLineSegment(sketch, "E1253", {"start": v(11.5, -10.94) * mm, "end": v(11.63, -11) * mm});
            skLineSegment(sketch, "E1254", {"start": v(11.63, -11) * mm, "end": v(11.76, -11.04) * mm});
            skLineSegment(sketch, "E1255", {"start": v(11.76, -11.04) * mm, "end": v(11.9, -11.09) * mm});
            skLineSegment(sketch, "E1256", {"start": v(11.9, -11.09) * mm, "end": v(12.03, -11.13) * mm});
            skLineSegment(sketch, "E1257", {"start": v(12.03, -11.13) * mm, "end": v(12.16, -11.17) * mm});
            skLineSegment(sketch, "E1258", {"start": v(12.16, -11.17) * mm, "end": v(12.3, -11.2) * mm});
            skLineSegment(sketch, "E1259", {"start": v(12.3, -11.2) * mm, "end": v(12.74, -10.7) * mm});
            skLineSegment(sketch, "E1260", {"start": v(12.74, -10.7) * mm, "end": v(12.68, -10.57) * mm});
            skLineSegment(sketch, "E1261", {"start": v(12.68, -10.57) * mm, "end": v(12.63, -10.44) * mm});
            skLineSegment(sketch, "E1262", {"start": v(12.63, -10.44) * mm, "end": v(12.57, -10.32) * mm});
            skLineSegment(sketch, "E1263", {"start": v(12.57, -10.32) * mm, "end": v(12.5, -10.2) * mm});
            skLineSegment(sketch, "E1264", {"start": v(12.5, -10.2) * mm, "end": v(12.44, -10.07) * mm});
            skLineSegment(sketch, "E1265", {"start": v(12.44, -10.07) * mm, "end": v(12.37, -9.94) * mm});
            skLineSegment(sketch, "E1266", {"start": v(12.37, -9.94) * mm, "end": v(12.3, -9.82) * mm});
            skLineSegment(sketch, "E1267", {"start": v(12.3, -9.82) * mm, "end": v(12.22, -9.7) * mm});
            skLineSegment(sketch, "E1268", {"start": v(12.22, -9.7) * mm, "end": v(12.14, -9.59) * mm});
            skLineSegment(sketch, "E1269", {"start": v(12.14, -9.59) * mm, "end": v(12.06, -9.47) * mm});
            skLineSegment(sketch, "E1270", {"start": v(12.06, -9.47) * mm, "end": v(11.98, -9.36) * mm});
            skLineSegment(sketch, "E1271", {"start": v(11.98, -9.36) * mm, "end": v(11.89, -9.25) * mm});
            skLineSegment(sketch, "E1272", {"start": v(11.89, -9.25) * mm, "end": v(11.8, -9.15) * mm});
            skLineSegment(sketch, "E1273", {"start": v(11.8, -9.15) * mm, "end": v(11.69, -9.05) * mm});
            skLineSegment(sketch, "E1274", {"start": v(11.69, -9.05) * mm, "end": v(11.7, -9) * mm});
            skLineSegment(sketch, "E1275", {"start": v(11.7, -9) * mm, "end": v(11.69, -8.96) * mm});
            skLineSegment(sketch, "E1276", {"start": v(11.69, -8.96) * mm, "end": v(11.68, -8.94) * mm});
            skLineSegment(sketch, "E1277", {"start": v(11.68, -8.94) * mm, "end": v(11.69, -8.91) * mm});
            skLineSegment(sketch, "E1278", {"start": v(11.69, -8.91) * mm, "end": v(11.7, -8.9) * mm});
            skLineSegment(sketch, "E1279", {"start": v(11.7, -8.9) * mm, "end": v(12.06, -8.4) * mm});
            skLineSegment(sketch, "E1280", {"start": v(12.06, -8.4) * mm, "end": v(12.07, -8.38) * mm});
            skLineSegment(sketch, "E1281", {"start": v(12.07, -8.38) * mm, "end": v(12.1, -8.37) * mm});
            skLineSegment(sketch, "E1282", {"start": v(12.1, -8.37) * mm, "end": v(12.12, -8.36) * mm});
            skLineSegment(sketch, "E1283", {"start": v(12.12, -8.36) * mm, "end": v(12.15, -8.36) * mm});
            skLineSegment(sketch, "E1284", {"start": v(12.15, -8.36) * mm, "end": v(12.21, -8.34) * mm});
            skLineSegment(sketch, "E1285", {"start": v(12.21, -8.34) * mm, "end": v(12.33, -8.4) * mm});
            skLineSegment(sketch, "E1286", {"start": v(12.33, -8.4) * mm, "end": v(12.46, -8.46) * mm});
            skLineSegment(sketch, "E1287", {"start": v(12.46, -8.46) * mm, "end": v(12.6, -8.52) * mm});
            skLineSegment(sketch, "E1288", {"start": v(12.6, -8.52) * mm, "end": v(12.72, -8.56) * mm});
            skLineSegment(sketch, "E1289", {"start": v(12.72, -8.56) * mm, "end": v(12.86, -8.6) * mm});
            skLineSegment(sketch, "E1290", {"start": v(12.86, -8.6) * mm, "end": v(13, -8.64) * mm});
            skLineSegment(sketch, "E1291", {"start": v(13, -8.64) * mm, "end": v(13.13, -8.68) * mm});
            skLineSegment(sketch, "E1292", {"start": v(13.13, -8.68) * mm, "end": v(13.27, -8.7) * mm});
            skLineSegment(sketch, "E1293", {"start": v(13.27, -8.7) * mm, "end": v(13.4, -8.74) * mm});
            skLineSegment(sketch, "E1294", {"start": v(13.4, -8.74) * mm, "end": v(13.54, -8.76) * mm});
            skLineSegment(sketch, "E1295", {"start": v(13.54, -8.76) * mm, "end": v(13.68, -8.78) * mm});
            skLineSegment(sketch, "E1296", {"start": v(13.68, -8.78) * mm, "end": v(13.82, -8.8) * mm});
            skLineSegment(sketch, "E1297", {"start": v(13.82, -8.8) * mm, "end": v(13.96, -8.82) * mm});
            skLineSegment(sketch, "E1298", {"start": v(13.96, -8.82) * mm, "end": v(14.1, -8.83) * mm});
            skLineSegment(sketch, "E1299", {"start": v(14.1, -8.83) * mm, "end": v(14.45, -8.25) * mm});
            skLineSegment(sketch, "E1300", {"start": v(14.45, -8.25) * mm, "end": v(14.37, -8.13) * mm});
            skLineSegment(sketch, "E1301", {"start": v(14.37, -8.13) * mm, "end": v(14.29, -8.02) * mm});
            skLineSegment(sketch, "E1302", {"start": v(14.29, -8.02) * mm, "end": v(14.2, -7.9) * mm});
            skLineSegment(sketch, "E1303", {"start": v(14.2, -7.9) * mm, "end": v(14.12, -7.8) * mm});
            skLineSegment(sketch, "E1304", {"start": v(14.12, -7.8) * mm, "end": v(14.03, -7.68) * mm});
            skLineSegment(sketch, "E1305", {"start": v(14.03, -7.68) * mm, "end": v(13.95, -7.57) * mm});
            skLineSegment(sketch, "E1306", {"start": v(13.95, -7.57) * mm, "end": v(13.85, -7.47) * mm});
            skLineSegment(sketch, "E1307", {"start": v(13.85, -7.47) * mm, "end": v(13.76, -7.36) * mm});
            skLineSegment(sketch, "E1308", {"start": v(13.76, -7.36) * mm, "end": v(13.66, -7.26) * mm});
            skLineSegment(sketch, "E1309", {"start": v(13.66, -7.26) * mm, "end": v(13.56, -7.16) * mm});
            skLineSegment(sketch, "E1310", {"start": v(13.56, -7.16) * mm, "end": v(13.46, -7.07) * mm});
            skLineSegment(sketch, "E1311", {"start": v(13.46, -7.07) * mm, "end": v(13.35, -6.98) * mm});
            skLineSegment(sketch, "E1312", {"start": v(13.35, -6.98) * mm, "end": v(13.24, -6.9) * mm});
            skLineSegment(sketch, "E1313", {"start": v(13.24, -6.9) * mm, "end": v(13.12, -6.82) * mm});
            skLineSegment(sketch, "E1314", {"start": v(13.12, -6.82) * mm, "end": v(13.11, -6.76) * mm});
            skLineSegment(sketch, "E1315", {"start": v(13.11, -6.76) * mm, "end": v(13.1, -6.73) * mm});
            skLineSegment(sketch, "E1316", {"start": v(13.1, -6.73) * mm, "end": v(13.1, -6.7) * mm});
            skLineSegment(sketch, "E1317", {"start": v(13.1, -6.7) * mm, "end": v(13.1, -6.68) * mm});
            skLineSegment(sketch, "E1318", {"start": v(13.1, -6.68) * mm, "end": v(13.1, -6.66) * mm});
            skLineSegment(sketch, "E1319", {"start": v(13.1, -6.66) * mm, "end": v(13.36, -6.1) * mm});
            skLineSegment(sketch, "E1320", {"start": v(13.36, -6.1) * mm, "end": v(13.38, -6.09) * mm});
            skLineSegment(sketch, "E1321", {"start": v(13.38, -6.09) * mm, "end": v(13.4, -6.07) * mm});
            skLineSegment(sketch, "E1322", {"start": v(13.4, -6.07) * mm, "end": v(13.42, -6.06) * mm});
            skLineSegment(sketch, "E1323", {"start": v(13.42, -6.06) * mm, "end": v(13.45, -6.05) * mm});
            skLineSegment(sketch, "E1324", {"start": v(13.45, -6.05) * mm, "end": v(13.5, -6.02) * mm});
            skLineSegment(sketch, "E1325", {"start": v(13.5, -6.02) * mm, "end": v(13.64, -6.06) * mm});
            skLineSegment(sketch, "E1326", {"start": v(13.64, -6.06) * mm, "end": v(13.77, -6.1) * mm});
            skLineSegment(sketch, "E1327", {"start": v(13.77, -6.1) * mm, "end": v(13.9, -6.13) * mm});
            skLineSegment(sketch, "E1328", {"start": v(13.9, -6.13) * mm, "end": v(14.05, -6.15) * mm});
            skLineSegment(sketch, "E1329", {"start": v(14.05, -6.15) * mm, "end": v(14.19, -6.17) * mm});
            skLineSegment(sketch, "E1330", {"start": v(14.19, -6.17) * mm, "end": v(14.33, -6.18) * mm});
            skLineSegment(sketch, "E1331", {"start": v(14.33, -6.18) * mm, "end": v(14.47, -6.2) * mm});
            skLineSegment(sketch, "E1332", {"start": v(14.47, -6.2) * mm, "end": v(14.6, -6.2) * mm});
            skLineSegment(sketch, "E1333", {"start": v(14.6, -6.2) * mm, "end": v(14.75, -6.2) * mm});
            skLineSegment(sketch, "E1334", {"start": v(14.75, -6.2) * mm, "end": v(14.89, -6.2) * mm});
            skLineSegment(sketch, "E1335", {"start": v(14.89, -6.2) * mm, "end": v(15.03, -6.2) * mm});
            skLineSegment(sketch, "E1336", {"start": v(15.03, -6.2) * mm, "end": v(15.17, -6.19) * mm});
            skLineSegment(sketch, "E1337", {"start": v(15.17, -6.19) * mm, "end": v(15.3, -6.18) * mm});
            skLineSegment(sketch, "E1338", {"start": v(15.3, -6.18) * mm, "end": v(15.45, -6.17) * mm});
            skLineSegment(sketch, "E1339", {"start": v(15.45, -6.17) * mm, "end": v(15.69, -5.53) * mm});
            skLineSegment(sketch, "E1340", {"start": v(15.69, -5.53) * mm, "end": v(15.59, -5.43) * mm});
            skLineSegment(sketch, "E1341", {"start": v(15.59, -5.43) * mm, "end": v(15.49, -5.33) * mm});
            skLineSegment(sketch, "E1342", {"start": v(15.49, -5.33) * mm, "end": v(15.39, -5.24) * mm});
            skLineSegment(sketch, "E1343", {"start": v(15.39, -5.24) * mm, "end": v(15.29, -5.14) * mm});
            skLineSegment(sketch, "E1344", {"start": v(15.29, -5.14) * mm, "end": v(15.18, -5.05) * mm});
            skLineSegment(sketch, "E1345", {"start": v(15.18, -5.05) * mm, "end": v(15.07, -4.96) * mm});
            skLineSegment(sketch, "E1346", {"start": v(15.07, -4.96) * mm, "end": v(14.96, -4.87) * mm});
            skLineSegment(sketch, "E1347", {"start": v(14.96, -4.87) * mm, "end": v(14.85, -4.78) * mm});
            skLineSegment(sketch, "E1348", {"start": v(14.85, -4.78) * mm, "end": v(14.74, -4.7) * mm});
            skLineSegment(sketch, "E1349", {"start": v(14.74, -4.7) * mm, "end": v(14.62, -4.62) * mm});
            skLineSegment(sketch, "E1350", {"start": v(14.62, -4.62) * mm, "end": v(14.5, -4.55) * mm});
            skLineSegment(sketch, "E1351", {"start": v(14.5, -4.55) * mm, "end": v(14.38, -4.48) * mm});
            skLineSegment(sketch, "E1352", {"start": v(14.38, -4.48) * mm, "end": v(14.25, -4.42) * mm});
            skLineSegment(sketch, "E1353", {"start": v(14.25, -4.42) * mm, "end": v(14.12, -4.36) * mm});
            skLineSegment(sketch, "E1354", {"start": v(14.12, -4.36) * mm, "end": v(14.1, -4.3) * mm});
            skLineSegment(sketch, "E1355", {"start": v(14.1, -4.3) * mm, "end": v(14.09, -4.28) * mm});
            skLineSegment(sketch, "E1356", {"start": v(14.09, -4.28) * mm, "end": v(14.08, -4.25) * mm});
            skLineSegment(sketch, "E1357", {"start": v(14.08, -4.25) * mm, "end": v(14.07, -4.23) * mm});
            skLineSegment(sketch, "E1358", {"start": v(14.07, -4.23) * mm, "end": v(14.08, -4.2) * mm});
            skLineSegment(sketch, "E1359", {"start": v(14.08, -4.2) * mm, "end": v(14.24, -3.62) * mm});
            skLineSegment(sketch, "E1360", {"start": v(14.24, -3.62) * mm, "end": v(14.25, -3.6) * mm});
            skLineSegment(sketch, "E1361", {"start": v(14.25, -3.6) * mm, "end": v(14.26, -3.58) * mm});
            skLineSegment(sketch, "E1362", {"start": v(14.26, -3.58) * mm, "end": v(14.29, -3.56) * mm});
            skLineSegment(sketch, "E1363", {"start": v(14.29, -3.56) * mm, "end": v(14.32, -3.55) * mm});
            skLineSegment(sketch, "E1364", {"start": v(14.32, -3.55) * mm, "end": v(14.36, -3.5) * mm});
            skLineSegment(sketch, "E1365", {"start": v(14.36, -3.5) * mm, "end": v(14.5, -3.53) * mm});
            skLineSegment(sketch, "E1366", {"start": v(14.5, -3.53) * mm, "end": v(14.64, -3.54) * mm});
            skLineSegment(sketch, "E1367", {"start": v(14.64, -3.54) * mm, "end": v(14.78, -3.54) * mm});
            skLineSegment(sketch, "E1368", {"start": v(14.78, -3.54) * mm, "end": v(14.92, -3.54) * mm});
            skLineSegment(sketch, "E1369", {"start": v(14.92, -3.54) * mm, "end": v(15.06, -3.53) * mm});
            skLineSegment(sketch, "E1370", {"start": v(15.06, -3.53) * mm, "end": v(15.2, -3.52) * mm});
            skLineSegment(sketch, "E1371", {"start": v(15.2, -3.52) * mm, "end": v(15.34, -3.5) * mm});
            skLineSegment(sketch, "E1372", {"start": v(15.34, -3.5) * mm, "end": v(15.48, -3.48) * mm});
            skLineSegment(sketch, "E1373", {"start": v(15.48, -3.48) * mm, "end": v(15.62, -3.46) * mm});
            skLineSegment(sketch, "E1374", {"start": v(15.62, -3.46) * mm, "end": v(15.76, -3.44) * mm});
            skLineSegment(sketch, "E1375", {"start": v(15.76, -3.44) * mm, "end": v(15.9, -3.4) * mm});
            skLineSegment(sketch, "E1376", {"start": v(15.9, -3.4) * mm, "end": v(16.03, -3.38) * mm});
            skLineSegment(sketch, "E1377", {"start": v(16.03, -3.38) * mm, "end": v(16.17, -3.34) * mm});
            skLineSegment(sketch, "E1378", {"start": v(16.17, -3.34) * mm, "end": v(16.3, -3.3) * mm});
            skLineSegment(sketch, "E1379", {"start": v(16.3, -3.3) * mm, "end": v(16.42, -2.64) * mm});
            skLineSegment(sketch, "E1380", {"start": v(16.42, -2.64) * mm, "end": v(16.3, -2.56) * mm});
            skLineSegment(sketch, "E1381", {"start": v(16.3, -2.56) * mm, "end": v(16.2, -2.48) * mm});
            skLineSegment(sketch, "E1382", {"start": v(16.2, -2.48) * mm, "end": v(16.08, -2.4) * mm});
            skLineSegment(sketch, "E1383", {"start": v(16.08, -2.4) * mm, "end": v(15.96, -2.33) * mm});
            skLineSegment(sketch, "E1384", {"start": v(15.96, -2.33) * mm, "end": v(15.84, -2.25) * mm});
            skLineSegment(sketch, "E1385", {"start": v(15.84, -2.25) * mm, "end": v(15.72, -2.18) * mm});
            skLineSegment(sketch, "E1386", {"start": v(15.72, -2.18) * mm, "end": v(15.6, -2.12) * mm});
            skLineSegment(sketch, "E1387", {"start": v(15.6, -2.12) * mm, "end": v(15.47, -2.05) * mm});
            skLineSegment(sketch, "E1388", {"start": v(15.47, -2.05) * mm, "end": v(15.34, -2) * mm});
            skLineSegment(sketch, "E1389", {"start": v(15.34, -2) * mm, "end": v(15.21, -1.94) * mm});
            skLineSegment(sketch, "E1390", {"start": v(15.21, -1.94) * mm, "end": v(15.08, -1.88) * mm});
            skLineSegment(sketch, "E1391", {"start": v(15.08, -1.88) * mm, "end": v(14.95, -1.84) * mm});
            skLineSegment(sketch, "E1392", {"start": v(14.95, -1.84) * mm, "end": v(14.81, -1.8) * mm});
            skLineSegment(sketch, "E1393", {"start": v(14.81, -1.8) * mm, "end": v(14.68, -1.77) * mm});
            skLineSegment(sketch, "E1394", {"start": v(14.68, -1.77) * mm, "end": v(14.65, -1.71) * mm});
            skLineSegment(sketch, "E1395", {"start": v(14.65, -1.71) * mm, "end": v(14.63, -1.7) * mm});
            skLineSegment(sketch, "E1396", {"start": v(14.63, -1.7) * mm, "end": v(14.61, -1.67) * mm});
            skLineSegment(sketch, "E1397", {"start": v(14.61, -1.67) * mm, "end": v(14.6, -1.65) * mm});
            skLineSegment(sketch, "E1398", {"start": v(14.6, -1.65) * mm, "end": v(14.6, -1.62) * mm});
            skLineSegment(sketch, "E1399", {"start": v(14.6, -1.62) * mm, "end": v(14.66, -1.01) * mm});
            skArc(sketch, "E1400", {"start": v(2.48, 0) * mm, "mid": v(-0.02, 2.5) * mm, "end": v(-2.52, 0) * mm});
            skArc(sketch, "E1401", {"start": v(-2.52, 0) * mm, "mid": v(-0.02, -2.5) * mm, "end": v(2.48, 0) * mm});
            skSolve(sketch);
        }
        {
            var Q0;
            Q0=makeQuery(id+"F0.imprint","IMPRINT",FACE,{"disambiguationData":[TD([[makeQuery(id+"F0.imprint","IMPRINT",EDGE,{"derivedFrom":sQuery(id+"F0.wireOp",EDGE,"E0")}),1.0]])]});
            var Q1;
            Q1=sQuery(id+"F0.wireOp",EDGE,"7309f3f8-ef88-46e9-8fb4-8255285162c7");
            var Q2;
            Q2=sQuery(id+"F0.wireOp",EDGE,"b2a63112-4bf1-41c3-b461-56f98d5fa946");
            var Q3;
            Q3=sQuery(id+"F0.wireOp",EDGE,"be3bdae5-7221-43e0-9c34-a2ee1238bb43");
            var Q4;
            Q4=sQuery(id+"F0.wireOp",EDGE,"ec9eebeb-1b99-46b7-b2f4-5d2084d343b1");
            var Q5;
            Q5=sQuery(id+"F0.wireOp",EDGE,"35b14249-e9a0-47c8-aca2-4ab9fe527380");
            var Q6;
            Q6=sQuery(id+"F0.wireOp",EDGE,"c3351f80-c2ff-4df1-bd8f-ec6a557da3f3");
            var Q7;
            Q7=sQuery(id+"F0.wireOp",EDGE,"46acb43d-d820-40f7-9638-2ccedc33000a");
            var Q8;
            Q8=sQuery(id+"F0.wireOp",EDGE,"29ea69ef-cd05-4e00-a0a6-9cc8001efeb1");
            var Q9;
            Q9=sQuery(id+"F0.wireOp",EDGE,"7ab8850d-2ea3-45dd-a1c8-00848d1db5b8");
            var Q10;
            Q10=sQuery(id+"F0.wireOp",EDGE,"623bd98d-c0dc-479d-a8a5-890fe37865cb");
            var Q11;
            Q11=sQuery(id+"F0.wireOp",EDGE,"1efc9fc0-7036-4e0d-9986-c9b1302a552e");
            var Q12;
            Q12=sQuery(id+"F0.wireOp",EDGE,"7662399b-19ac-4a72-a0ac-402ceeb9b6a6");
            var Q13;
            Q13=sQuery(id+"F0.wireOp",EDGE,"c4cbaa82-8d02-46a8-b059-21a10c35e4ce");
            var Q14;
            Q14=sQuery(id+"F0.wireOp",EDGE,"472b75b9-c591-4bb4-a231-992f9da12eed");
            var Q15;
            Q15=sQuery(id+"F0.wireOp",EDGE,"68f39e92-25ab-443d-8542-4550f2e761c6");
            var Q16;
            Q16=sQuery(id+"F0.wireOp",EDGE,"70addfda-b363-4c8d-8f28-65f55d6bf3f9");
            var Q17;
            Q17=sQuery(id+"F0.wireOp",EDGE,"a4603310-b405-43ed-bc6b-6584038cd5b5");
            var Q18;
            Q18=sQuery(id+"F0.wireOp",EDGE,"b4a0b278-f3b5-4f1c-8bbb-7459f56fdb34");
            var Q19;
            Q19=sQuery(id+"F0.wireOp",EDGE,"9fa16e21-8a48-424b-b30d-da61aeee6c9d");
            var Q20;
            Q20=sQuery(id+"F0.wireOp",EDGE,"584f3759-045f-43ac-9341-90ba05595e02");
            var Q21;
            Q21=sQuery(id+"F0.wireOp",EDGE,"f7aa21af-c542-484b-a152-bd626eb03955");
            var Q22;
            Q22=sQuery(id+"F0.wireOp",EDGE,"b9bdda09-afda-4f35-a687-465d606eb36e");
            var Q23;
            Q23=sQuery(id+"F0.wireOp",EDGE,"70f01949-47ce-4438-9cf4-a8b3ca3bf5ae");
            var Q24;
            Q24=sQuery(id+"F0.wireOp",EDGE,"5f222920-fe5b-46d2-a61c-a114375e88aa");
            var Q25;
            Q25=sQuery(id+"F0.wireOp",EDGE,"2dcfc702-2bb2-4b9c-8461-9676e20c291e");
            var Q26;
            Q26=sQuery(id+"F0.wireOp",EDGE,"dca9aac0-f9d2-4242-9c32-5ff30d33bf8e");
            var Q27;
            Q27=sQuery(id+"F0.wireOp",EDGE,"63e166f6-15d9-451e-a3b9-4110036b3ae1");
            var Q28;
            Q28=sQuery(id+"F0.wireOp",EDGE,"5f72f41a-55b7-4b46-9740-f25719e33462");
            var Q29;
            Q29=sQuery(id+"F0.wireOp",EDGE,"b5905b0b-7c74-4187-93f6-fc8d35eca649");
            var Q30;
            Q30=sQuery(id+"F0.wireOp",EDGE,"b83b1cda-3bfb-4581-a92d-e4b788d51102");
            var Q31;
            Q31=sQuery(id+"F0.wireOp",EDGE,"94ee5c99-f184-4824-8962-8d9f357783cc");
            var Q32;
            Q32=sQuery(id+"F0.wireOp",EDGE,"7583a498-f963-428a-bc34-090ce8c12176");
            var Q33;
            Q33=sQuery(id+"F0.wireOp",EDGE,"884c4fd3-9bf9-48ba-b8a0-4d00b815c230");
            var Q34;
            Q34=sQuery(id+"F0.wireOp",EDGE,"3cd332c9-439f-41f9-91b2-bc31bcbfee76");
            var Q35;
            Q35=sQuery(id+"F0.wireOp",EDGE,"75fa14c4-213c-4a00-81b2-006ac13c50d2");
            var Q36;
            Q36=sQuery(id+"F0.wireOp",EDGE,"e1ffbcfd-7490-495b-972d-e4921fb3579a");
            var Q37;
            Q37=sQuery(id+"F0.wireOp",EDGE,"d97ffa5b-f102-4bbe-8476-3722f31591da");
            var Q38;
            Q38=sQuery(id+"F0.wireOp",EDGE,"89154713-6e23-46b1-9483-7df1bc6b3ac0");
            var Q39;
            Q39=sQuery(id+"F0.wireOp",EDGE,"272f92f5-2497-4508-9ecb-38b1b7578350");
            var Q40;
            Q40=sQuery(id+"F0.wireOp",EDGE,"2982ca84-2c20-4561-9a20-d30b503f607c");
            var Q41;
            Q41=sQuery(id+"F0.wireOp",EDGE,"90fdf26b-707c-4b41-b30c-847906291f5d");
            var Q42;
            Q42=sQuery(id+"F0.wireOp",EDGE,"5d666d61-8589-4f1a-9bde-30663510b4b0");
            var Q43;
            Q43=sQuery(id+"F0.wireOp",EDGE,"1e68ec19-922b-4806-a83d-953545ad0019");
            var Q44;
            Q44=sQuery(id+"F0.wireOp",EDGE,"94ec0cc2-5c05-4931-813a-f418e61d2aaf");
            var Q45;
            Q45=sQuery(id+"F0.wireOp",EDGE,"75de6577-5c6c-4f7f-a147-082f3f837f3c");
            var Q46;
            Q46=sQuery(id+"F0.wireOp",EDGE,"df9d9f96-f722-4f4b-875a-86c96eb74f8f");
            var Q47;
            Q47=sQuery(id+"F0.wireOp",EDGE,"2e4af2a4-728c-4945-977a-6554cb0fff51");
            var Q48;
            Q48=sQuery(id+"F0.wireOp",EDGE,"377f6529-6584-43c6-bdc2-9ba0d4e11724");
            var Q49;
            Q49=sQuery(id+"F0.wireOp",EDGE,"10cbb697-5226-4b2c-b5cc-e81d69268c96");
            var Q50;
            Q50=sQuery(id+"F0.wireOp",EDGE,"3ece06c8-c336-4122-8b35-987510dac89b");
            var Q51;
            Q51=sQuery(id+"F0.wireOp",EDGE,"c8d66315-8cdc-41fe-937c-2e1a63ec9f10");
            var Q52;
            Q52=sQuery(id+"F0.wireOp",EDGE,"6e86d26c-efab-47bd-8872-f2e23db73f00");
            var Q53;
            Q53=sQuery(id+"F0.wireOp",EDGE,"d7949ea1-ab0b-4d88-86b4-6daa9cd0f181");
            var Q54;
            Q54=sQuery(id+"F0.wireOp",EDGE,"297bec19-d9ae-4386-bfe1-c0c7466fd250");
            var Q55;
            Q55=sQuery(id+"F0.wireOp",EDGE,"a32aa804-80e1-4a05-9618-4dac30ced6c3");
            var Q56;
            Q56=sQuery(id+"F0.wireOp",EDGE,"aa6f45c6-7afb-4d27-86fd-c1ebd8e2f7e7");
            var Q57;
            Q57=sQuery(id+"F0.wireOp",EDGE,"11d1b8f2-847e-4bb8-81cc-d043421a6ae8");
            var Q58;
            Q58=sQuery(id+"F0.wireOp",EDGE,"1beb1f84-8ce1-4d84-b8f6-0d24b79d50e5");
            var Q59;
            Q59=sQuery(id+"F0.wireOp",EDGE,"8c902ec3-e1fd-4ca9-8dca-893e540a809d");
            var Q60;
            Q60=sQuery(id+"F0.wireOp",EDGE,"179cdf32-9807-46cd-92c2-30124c439a6c");
            var Q61;
            Q61=sQuery(id+"F0.wireOp",EDGE,"45d6227b-93d9-4a31-b933-e4694813863e");
            var Q62;
            Q62=sQuery(id+"F0.wireOp",EDGE,"543a261d-eb1f-445e-b2b0-01ffdb662b0b");
            var Q63;
            Q63=sQuery(id+"F0.wireOp",EDGE,"d33cb51b-e03d-41f1-9ccf-90c5b7f3cd52");
            var Q64;
            Q64=sQuery(id+"F0.wireOp",EDGE,"f227d708-1f6a-4b32-b816-381fda1d1450");
            var Q65;
            Q65=sQuery(id+"F0.wireOp",EDGE,"1f5e820d-3c99-42dd-b4a6-99b199b266df");
            var Q66;
            Q66=sQuery(id+"F0.wireOp",EDGE,"41422e6e-5894-4db3-8e77-810edf1b7272");
            var Q67;
            Q67=sQuery(id+"F0.wireOp",EDGE,"4f1a2a27-c633-4465-bfdb-88c6b73c62c4");
            var Q68;
            Q68=sQuery(id+"F0.wireOp",EDGE,"a57f4070-c4f1-4e95-a628-a9a6a349497a");
            var Q69;
            Q69=sQuery(id+"F0.wireOp",EDGE,"4a1a83b5-9a06-41ae-98a3-3a04336b08ad");
            var Q70;
            Q70=sQuery(id+"F0.wireOp",EDGE,"4c693bb5-86f2-4158-aa6a-af2805e25b9a");
            var Q71;
            Q71=sQuery(id+"F0.wireOp",EDGE,"1bc0a22e-0169-4fb9-bda7-0924990e0b3e");
            var Q72;
            Q72=sQuery(id+"F0.wireOp",EDGE,"ce196c30-22b6-4dc5-92ee-945213ffb0d8");
            var Q73;
            Q73=sQuery(id+"F0.wireOp",EDGE,"24870c9e-006d-4ee9-ba51-613bbbbc10c5");
            var Q74;
            Q74=sQuery(id+"F0.wireOp",EDGE,"ffa842f2-254b-4916-be1a-a88e763aafd7");
            var Q75;
            Q75=sQuery(id+"F0.wireOp",EDGE,"f3189daf-d85d-4ec7-8f8e-e40009f41664");
            var Q76;
            Q76=sQuery(id+"F0.wireOp",EDGE,"473cd8b3-bedd-430f-9a11-c85ad8cb5a5b");
            var Q77;
            Q77=sQuery(id+"F0.wireOp",EDGE,"d8e6115d-03ee-46f3-9b21-48b840269ebd");
            var Q78;
            Q78=sQuery(id+"F0.wireOp",EDGE,"83b13cdd-6dd5-45c4-a538-1c0e935c1ff3");
            var Q79;
            Q79=sQuery(id+"F0.wireOp",EDGE,"bf3fc835-79b4-4e35-997e-51877b2170ec");
            var Q80;
            Q80=sQuery(id+"F0.wireOp",EDGE,"63c5684c-b12f-40c4-ab44-e39470141120");
            var Q81;
            Q81=sQuery(id+"F0.wireOp",EDGE,"e62aeb14-e6b0-4c36-957b-3fd3b729a46b");
            var Q82;
            Q82=sQuery(id+"F0.wireOp",EDGE,"d69a79c5-910d-44d1-9ccf-ca80c0d4f05b");
            var Q83;
            Q83=sQuery(id+"F0.wireOp",EDGE,"7060d10d-b95f-4674-9f7b-125dd6c6a589");
            var Q84;
            Q84=sQuery(id+"F0.wireOp",EDGE,"caf1fbc0-cc95-47c7-8f56-e6e81de24bc1");
            var Q85;
            Q85=sQuery(id+"F0.wireOp",EDGE,"ee6d87e2-fe0a-4d93-9b03-6aa2e71190e2");
            var Q86;
            Q86=sQuery(id+"F0.wireOp",EDGE,"a40b6dff-ca63-4f98-a8e5-30971598be1d");
            var Q87;
            Q87=sQuery(id+"F0.wireOp",EDGE,"0aa880ba-8163-48e3-9076-0f427dd79036");
            var Q88;
            Q88=sQuery(id+"F0.wireOp",EDGE,"6d229088-adae-4870-bc57-6753069c361f");
            var Q89;
            Q89=sQuery(id+"F0.wireOp",EDGE,"2d5dced9-c715-465e-b06d-5545aa175d12");
            var Q90;
            Q90=sQuery(id+"F0.wireOp",EDGE,"982fef42-0279-4e8a-9ded-45d6a86b66ef");
            var Q91;
            Q91=sQuery(id+"F0.wireOp",EDGE,"12e6ae0f-94f9-4d72-9700-96a8fb56f190");
            var Q92;
            Q92=sQuery(id+"F0.wireOp",EDGE,"e90157f7-3c56-4887-a605-af283ad49b8c");
            var Q93;
            Q93=sQuery(id+"F0.wireOp",EDGE,"6a08b5a6-83a3-4bd7-868d-afd1c004ff4a");
            var Q94;
            Q94=sQuery(id+"F0.wireOp",EDGE,"d1dd882c-9276-455e-b7be-540880040f96");
            var Q95;
            Q95=sQuery(id+"F0.wireOp",EDGE,"3c61c565-db3a-4148-80e8-2aa197252efa");
            var Q96;
            Q96=sQuery(id+"F0.wireOp",EDGE,"c8a1e2b0-c85e-4794-b773-fe6a1eb9bc29");
            var Q97;
            Q97=sQuery(id+"F0.wireOp",EDGE,"16cf732e-9e83-4722-b09a-37f381a24923");
            var Q98;
            Q98=sQuery(id+"F0.wireOp",EDGE,"2d3ca5d5-cb33-4073-b288-f4ffb2e724f4");
            var Q99;
            Q99=sQuery(id+"F0.wireOp",EDGE,"e1b9e37d-5601-4aba-a24e-ffc9865441a0");
            var Q100;
            Q100=sQuery(id+"F0.wireOp",EDGE,"a2e1f6b5-1609-487f-9fc8-309514535e02");
            var Q101;
            Q101=sQuery(id+"F0.wireOp",EDGE,"a246b688-e5c0-4195-95f9-01e393df7fc7");
            var Q102;
            Q102=sQuery(id+"F0.wireOp",EDGE,"2a09587e-3111-4844-a2a4-914ddc9de77b");
            var Q103;
            Q103=sQuery(id+"F0.wireOp",EDGE,"a83dcc95-8ddd-4b3b-b502-9717e4ad198d");
            var Q104;
            Q104=sQuery(id+"F0.wireOp",EDGE,"451ce23c-99c0-495c-8995-c9efb44d27b2");
            var Q105;
            Q105=sQuery(id+"F0.wireOp",EDGE,"ac203fcb-dea0-4f3c-b5df-89be0ae61488");
            var Q106;
            Q106=sQuery(id+"F0.wireOp",EDGE,"94cbe807-6985-427d-8940-1e3995c33bfa");
            var Q107;
            Q107=sQuery(id+"F0.wireOp",EDGE,"5b9d69c3-3463-4541-89b0-b52d6965ceff");
            var Q108;
            Q108=sQuery(id+"F0.wireOp",EDGE,"dabac9ec-1792-4a30-b093-80af6aa0bccf");
            var Q109;
            Q109=sQuery(id+"F0.wireOp",EDGE,"15142d5c-1134-49b7-986d-5e2227ba75ff");
            var Q110;
            Q110=sQuery(id+"F0.wireOp",EDGE,"fb1468d6-59de-4c38-ab33-eec1b36e0082");
            var Q111;
            Q111=sQuery(id+"F0.wireOp",EDGE,"19518190-0445-4dd2-ae83-2969e903840d");
            var Q112;
            Q112=sQuery(id+"F0.wireOp",EDGE,"080e2fe6-8b7a-4a04-a2b4-c3eb09c71583");
            var Q113;
            Q113=sQuery(id+"F0.wireOp",EDGE,"3140dba7-ed21-4f8b-80cd-ba3ad2efd9d8");
            var Q114;
            Q114=sQuery(id+"F0.wireOp",EDGE,"936f2a14-84fb-48ce-a5ca-7d99b52b8b4e");
            var Q115;
            Q115=sQuery(id+"F0.wireOp",EDGE,"8829ee09-6a9c-4b36-8b0a-4123fef7bddf");
            var Q116;
            Q116=sQuery(id+"F0.wireOp",EDGE,"e85b8b67-7d90-4a3b-b9f4-d78ab6c2e61b");
            var Q117;
            Q117=sQuery(id+"F0.wireOp",EDGE,"721b4826-6925-4f18-a067-c63206d4ffef");
            var Q118;
            Q118=sQuery(id+"F0.wireOp",EDGE,"e9fcef97-ffad-48c3-9ca7-9243d7d3905c");
            var Q119;
            Q119=sQuery(id+"F0.wireOp",EDGE,"04c4160b-9d8a-4f5b-969d-151e94076818");
            var Q120;
            Q120=sQuery(id+"F0.wireOp",EDGE,"e259befe-e3de-4130-8e60-1ef21500c7dc");
            var Q121;
            Q121=sQuery(id+"F0.wireOp",EDGE,"cbe1f823-a23d-4649-b334-8a83b90e0afb");
            var Q122;
            Q122=sQuery(id+"F0.wireOp",EDGE,"e755d527-187a-4fb2-a514-6f331dcb4af2");
            var Q123;
            Q123=sQuery(id+"F0.wireOp",EDGE,"dd40b44f-920d-4825-9930-24d3af47eb61");
            var Q124;
            Q124=sQuery(id+"F0.wireOp",EDGE,"b71a7093-5359-458b-9a43-08d928570128");
            var Q125;
            Q125=sQuery(id+"F0.wireOp",EDGE,"a9c834f3-c3d3-4e0f-be17-42c47d945f13");
            var Q126;
            Q126=sQuery(id+"F0.wireOp",EDGE,"626141c7-5b74-4f9e-a389-ea8407d48580");
            var Q127;
            Q127=sQuery(id+"F0.wireOp",EDGE,"3b04b0c8-5fa6-49c2-beab-d217cb9a7bc7");
            var Q128;
            Q128=sQuery(id+"F0.wireOp",EDGE,"31f2ed08-c90a-440f-9717-b7a33d14793d");
            var Q129;
            Q129=sQuery(id+"F0.wireOp",EDGE,"3219733c-0ee5-4d1c-8a07-5d837d99ed80");
            var Q130;
            Q130=sQuery(id+"F0.wireOp",EDGE,"713d4b77-bc17-4308-9478-5f305760a654");
            var Q131;
            Q131=sQuery(id+"F0.wireOp",EDGE,"958e88b5-6cd3-434a-97f8-1f951c34d63c");
            var Q132;
            Q132=sQuery(id+"F0.wireOp",EDGE,"db81bf98-7869-4716-81aa-c17cbc16732b");
            var Q133;
            Q133=sQuery(id+"F0.wireOp",EDGE,"142d55f4-5e14-427c-b54c-505b3e9850d0");
            var Q134;
            Q134=sQuery(id+"F0.wireOp",EDGE,"c8029bf8-70bf-42df-978d-c493726b82b1");
            var Q135;
            Q135=sQuery(id+"F0.wireOp",EDGE,"6d8d724f-a34f-4100-a088-6555e23b4351");
            var Q136;
            Q136=sQuery(id+"F0.wireOp",EDGE,"6b707735-0332-41d8-bd5b-af7eca52f773");
            var Q137;
            Q137=sQuery(id+"F0.wireOp",EDGE,"222ef1bd-0af5-4e6c-8c40-45813659ed35");
            var Q138;
            Q138=sQuery(id+"F0.wireOp",EDGE,"86cbfd17-bda3-4848-8ff1-39776571088a");
            var Q139;
            Q139=sQuery(id+"F0.wireOp",EDGE,"ae4a1f36-c1fd-4a5c-977d-8b5948d07b7c");
            var Q140;
            Q140=sQuery(id+"F0.wireOp",EDGE,"81187b77-b5e9-42a9-9da8-f71af45faaab");
            var Q141;
            Q141=sQuery(id+"F0.wireOp",EDGE,"81705a66-663c-4763-9e46-e90485d2d841");
            var Q142;
            Q142=sQuery(id+"F0.wireOp",EDGE,"13d4ba02-48ba-4fe0-87a3-201b4659e093");
            var Q143;
            Q143=sQuery(id+"F0.wireOp",EDGE,"2dcac969-a105-4f2a-84dd-37f60b0af43f");
            var Q144;
            Q144=sQuery(id+"F0.wireOp",EDGE,"e127b53b-c21f-4421-ba8b-edafc972fcc5");
            var Q145;
            Q145=sQuery(id+"F0.wireOp",EDGE,"564ed9b6-8979-4104-933a-879b9b5fea65");
            var Q146;
            Q146=sQuery(id+"F0.wireOp",EDGE,"b7f965e3-c419-4939-8ba7-a599f938fd7c");
            var Q147;
            Q147=sQuery(id+"F0.wireOp",EDGE,"3941c595-af71-4494-b1a2-f7365ae4605c");
            var Q148;
            Q148=sQuery(id+"F0.wireOp",EDGE,"e018ae15-d7c6-4ac6-981a-ca11a95724f3");
            var Q149;
            Q149=sQuery(id+"F0.wireOp",EDGE,"241bee0d-6fba-4687-97c8-aa09339cce1c");
            var Q150;
            Q150=sQuery(id+"F0.wireOp",EDGE,"c15aa438-26a4-4c6c-9de6-bc099cd37cc8");
            var Q151;
            Q151=sQuery(id+"F0.wireOp",EDGE,"ae38a82f-dbfa-43eb-b3ea-1d789d9b38d3");
            var Q152;
            Q152=sQuery(id+"F0.wireOp",EDGE,"7e36df09-c549-4606-9aa8-faadb265c30d");
            var Q153;
            Q153=sQuery(id+"F0.wireOp",EDGE,"aec71f34-a5c3-40de-b49f-1658ae85eb65");
            var Q154;
            Q154=sQuery(id+"F0.wireOp",EDGE,"7c34add8-7a8a-46da-8bd0-fe90622e2fec");
            var Q155;
            Q155=sQuery(id+"F0.wireOp",EDGE,"1d0651bc-b14e-4d84-a0c9-eed0cc06cc2b");
            var Q156;
            Q156=sQuery(id+"F0.wireOp",EDGE,"1b21b260-6793-412d-ac7e-231a665e2f67");
            var Q157;
            Q157=sQuery(id+"F0.wireOp",EDGE,"f9132a57-b075-4694-aa8f-0b4a2c4c75f2");
            var Q158;
            Q158=sQuery(id+"F0.wireOp",EDGE,"fdd3a3c4-54f0-4cb7-bac3-53dec90283bb");
            var Q159;
            Q159=sQuery(id+"F0.wireOp",EDGE,"822784f9-6941-42e1-9ee6-3f4a40940b2d");
            var Q160;
            Q160=sQuery(id+"F0.wireOp",EDGE,"1f087669-54f8-4c8d-ba14-7e05eb3e8409");
            var Q161;
            Q161=sQuery(id+"F0.wireOp",EDGE,"9d7e5707-cdfa-4dc8-8492-a19cc241628f");
            var Q162;
            Q162=sQuery(id+"F0.wireOp",EDGE,"bcb3dfad-fb4a-4411-91e6-c9b5cda8fd14");
            var Q163;
            Q163=sQuery(id+"F0.wireOp",EDGE,"95962ee9-9084-43ab-b1e4-76a9ee61eb30");
            var Q164;
            Q164=sQuery(id+"F0.wireOp",EDGE,"200a7033-b7af-4dda-b57b-5a45707219a9");
            var Q165;
            Q165=sQuery(id+"F0.wireOp",EDGE,"eadf095e-bc43-46e3-af85-0683d06a32ed");
            var Q166;
            Q166=sQuery(id+"F0.wireOp",EDGE,"208db721-fa1d-4159-abfe-ce43f533a226");
            var Q167;
            Q167=sQuery(id+"F0.wireOp",EDGE,"708b5412-edc0-474e-b74f-b2f5291f1d6f");
            var Q168;
            Q168=sQuery(id+"F0.wireOp",EDGE,"ba50007b-7739-47eb-8a5d-eea6c23cae1a");
            var Q169;
            Q169=sQuery(id+"F0.wireOp",EDGE,"7c4f7003-3786-44e3-89d3-9cdcb530bd96");
            var Q170;
            Q170=sQuery(id+"F0.wireOp",EDGE,"42377a32-1649-41bf-ad98-0860f8939325");
            var Q171;
            Q171=sQuery(id+"F0.wireOp",EDGE,"023966f7-04b6-486f-9307-04207d55d774");
            var Q172;
            Q172=sQuery(id+"F0.wireOp",EDGE,"ae52cdd3-6b80-45fe-8671-c5fc49032b15");
            var Q173;
            Q173=sQuery(id+"F0.wireOp",EDGE,"670054d2-47ad-4900-9e36-eaadf7dea361");
            var Q174;
            Q174=sQuery(id+"F0.wireOp",EDGE,"dea378e4-c466-4f25-9545-ab8e48fafcb7");
            var Q175;
            Q175=sQuery(id+"F0.wireOp",EDGE,"52713da7-b4e2-4871-8ba9-29c5d4c8c32a");
            var Q176;
            Q176=sQuery(id+"F0.wireOp",EDGE,"bf6f0fb8-0b10-4d7c-8c5c-aa39c35ed806");
            var Q177;
            Q177=sQuery(id+"F0.wireOp",EDGE,"1df2c45d-eda5-4bad-887c-eb3fb30eeb61");
            var Q178;
            Q178=sQuery(id+"F0.wireOp",EDGE,"4005f240-1be1-4c36-88ff-ff847a5577da");
            var Q179;
            Q179=sQuery(id+"F0.wireOp",EDGE,"18ba767c-ae24-4547-957b-bf58be90d5d6");
            var Q180;
            Q180=sQuery(id+"F0.wireOp",EDGE,"b033678a-8024-4a22-b997-12e0b82a0a8d");
            var Q181;
            Q181=sQuery(id+"F0.wireOp",EDGE,"54b98135-d1f7-4d00-a813-44ba808d54f4");
            var Q182;
            Q182=sQuery(id+"F0.wireOp",EDGE,"a4c9d2cb-2fb7-41b1-ab09-1aaa2a95a4b7");
            var Q183;
            Q183=sQuery(id+"F0.wireOp",EDGE,"ad9d789c-c57e-4533-97e0-66265e645b33");
            var Q184;
            Q184=sQuery(id+"F0.wireOp",EDGE,"4e1e4b9c-98ad-420f-9e13-52cfad6aa471");
            var Q185;
            Q185=sQuery(id+"F0.wireOp",EDGE,"59011ceb-ceb6-4741-b705-4558e9035875");
            var Q186;
            Q186=sQuery(id+"F0.wireOp",EDGE,"a8783edb-7103-4604-84aa-ae5f50ce6f35");
            var Q187;
            Q187=sQuery(id+"F0.wireOp",EDGE,"e974b45b-1f0d-4675-b4a6-1dd9354d2159");
            var Q188;
            Q188=sQuery(id+"F0.wireOp",EDGE,"85e41199-6c72-49e9-8ffe-c5e1a65a4ed2");
            var Q189;
            Q189=sQuery(id+"F0.wireOp",EDGE,"3b3d6dbe-d43f-432b-919e-87e1f59aee55");
            var Q190;
            Q190=sQuery(id+"F0.wireOp",EDGE,"943e2d72-a598-468b-934a-2d8cbad0fe81");
            var Q191;
            Q191=sQuery(id+"F0.wireOp",EDGE,"5c5a8aa5-77c8-49b3-beb8-c44a8f908f93");
            var Q192;
            Q192=sQuery(id+"F0.wireOp",EDGE,"97bb7080-2790-4ec3-8e60-17cb88b3837b");
            var Q193;
            Q193=sQuery(id+"F0.wireOp",EDGE,"d783070b-3db1-4405-be62-31af5ee851bc");
            var Q194;
            Q194=sQuery(id+"F0.wireOp",EDGE,"a87ee406-1397-4a46-9f4f-c9ee503f5c00");
            var Q195;
            Q195=sQuery(id+"F0.wireOp",EDGE,"9adb11b5-17e4-4570-bbe1-ead1ae22a224");
            var Q196;
            Q196=sQuery(id+"F0.wireOp",EDGE,"e6914099-8d46-40bc-a70e-07f640dd2b5c");
            var Q197;
            Q197=sQuery(id+"F0.wireOp",EDGE,"182f6ebc-877d-49de-b1d2-a744eea1bb5a");
            var Q198;
            Q198=sQuery(id+"F0.wireOp",EDGE,"f2ffceea-56d6-429a-a395-f6fdaeb9c5b9");
            var Q199;
            Q199=sQuery(id+"F0.wireOp",EDGE,"fed4ff70-ab02-4cfd-84cf-1f5617b51fd1");
            var Q200;
            Q200=sQuery(id+"F0.wireOp",EDGE,"01e2eafe-d6b7-446a-80c0-45b023e238b8");
            var Q201;
            Q201=sQuery(id+"F0.wireOp",EDGE,"092b59f1-313f-4d4b-b3ba-6b46ae178804");
            var Q202;
            Q202=sQuery(id+"F0.wireOp",EDGE,"fc68b6b9-3937-4a61-874b-320c0e13cc4f");
            var Q203;
            Q203=sQuery(id+"F0.wireOp",EDGE,"80decb2d-1536-4a18-b939-e4ec6bbea812");
            var Q204;
            Q204=sQuery(id+"F0.wireOp",EDGE,"c6f9345b-86db-43a4-b515-eb158d5ef369");
            var Q205;
            Q205=sQuery(id+"F0.wireOp",EDGE,"cc889fad-9551-4a9e-8107-c060dd4a1ee0");
            var Q206;
            Q206=sQuery(id+"F0.wireOp",EDGE,"02dc6fdb-d17f-425c-a813-7633b344225f");
            var Q207;
            Q207=sQuery(id+"F0.wireOp",EDGE,"19d41cb9-7b14-4336-bd7f-c4ae697d61ed");
            var Q208;
            Q208=sQuery(id+"F0.wireOp",EDGE,"fabc90ab-b7f0-4706-a816-833440d7a082");
            var Q209;
            Q209=sQuery(id+"F0.wireOp",EDGE,"7e78b61c-5fa9-42bd-b385-4a6641259dec");
            var Q210;
            Q210=sQuery(id+"F0.wireOp",EDGE,"43a79a8b-2c50-4f9a-938f-a57d68172c91");
            var Q211;
            Q211=sQuery(id+"F0.wireOp",EDGE,"55a49ccb-3225-413b-8d60-325cd313969d");
            var Q212;
            Q212=sQuery(id+"F0.wireOp",EDGE,"4f20ef62-eb61-4e80-b320-a570306b013a");
            var Q213;
            Q213=sQuery(id+"F0.wireOp",EDGE,"e6f5a2ea-c659-47ba-9fdd-0e1490e48047");
            var Q214;
            Q214=sQuery(id+"F0.wireOp",EDGE,"6ef797e6-6fca-4c67-b96a-fc605fc0a61f");
            var Q215;
            Q215=sQuery(id+"F0.wireOp",EDGE,"59a3c244-7eeb-456e-9f29-d2dac5ea8019");
            var Q216;
            Q216=sQuery(id+"F0.wireOp",EDGE,"a53c1f67-00b4-4250-ab22-6aca685f083e");
            var Q217;
            Q217=sQuery(id+"F0.wireOp",EDGE,"752dab1e-6506-4335-bfaa-9acdd9f376d5");
            var Q218;
            Q218=sQuery(id+"F0.wireOp",EDGE,"281fa2eb-c7e4-4a90-92ea-9394f7d4b19b");
            var Q219;
            Q219=sQuery(id+"F0.wireOp",EDGE,"8471d841-cf85-4302-b5e1-b49ac7d04758");
            var Q220;
            Q220=sQuery(id+"F0.wireOp",EDGE,"9e33050f-6ade-4444-9139-12cbbadb0058");
            var Q221;
            Q221=sQuery(id+"F0.wireOp",EDGE,"c7b8b96a-5954-49e2-8192-05ff292aaa25");
            var Q222;
            Q222=sQuery(id+"F0.wireOp",EDGE,"61ff8242-49d8-41b6-a586-2637f50f01de");
            var Q223;
            Q223=sQuery(id+"F0.wireOp",EDGE,"f7442712-9243-4227-b455-863977752177");
            var Q224;
            Q224=sQuery(id+"F0.wireOp",EDGE,"170d62ae-a9ef-4a8d-8a53-f45e045b5146");
            var Q225;
            Q225=sQuery(id+"F0.wireOp",EDGE,"e970df4d-c520-4d14-ad11-dcbceccf15fe");
            var Q226;
            Q226=sQuery(id+"F0.wireOp",EDGE,"abf4d311-9ccd-4e27-a19c-5a20a183c842");
            var Q227;
            Q227=sQuery(id+"F0.wireOp",EDGE,"a254cd3b-21af-4385-bf3b-a1575fe07dd9");
            var Q228;
            Q228=sQuery(id+"F0.wireOp",EDGE,"594ff17d-4ee6-4973-916a-d543e49c5ec3");
            var Q229;
            Q229=sQuery(id+"F0.wireOp",EDGE,"e86682ef-b041-4e95-be7b-285cd4d4df88");
            var Q230;
            Q230=sQuery(id+"F0.wireOp",EDGE,"94ef4e09-fbda-4fd5-be9a-c66b7cae82e1");
            var Q231;
            Q231=sQuery(id+"F0.wireOp",EDGE,"15a11fe2-bed9-4f20-925a-9bed442a08f0");
            var Q232;
            Q232=sQuery(id+"F0.wireOp",EDGE,"6a624c9f-ced0-4431-8a1b-88256ff62a77");
            var Q233;
            Q233=sQuery(id+"F0.wireOp",EDGE,"d940df8c-b160-4e01-bc03-0c05d840abf5");
            var Q234;
            Q234=sQuery(id+"F0.wireOp",EDGE,"f422e6ee-78a3-4f44-909d-3801a1389615");
            var Q235;
            Q235=sQuery(id+"F0.wireOp",EDGE,"06022005-639e-4dfe-8703-a0e07118bd50");
            var Q236;
            Q236=sQuery(id+"F0.wireOp",EDGE,"147bd0ea-68a1-41b9-bce9-6ea09494e95c");
            var Q237;
            Q237=sQuery(id+"F0.wireOp",EDGE,"dde150f4-1b7e-4070-85c5-2365280059ba");
            var Q238;
            Q238=sQuery(id+"F0.wireOp",EDGE,"09214e61-70c1-439f-aba1-d64ae4936d6d");
            var Q239;
            Q239=sQuery(id+"F0.wireOp",EDGE,"6b62aad5-6267-4a3a-b143-9c0585b6040f");
            var Q240;
            Q240=sQuery(id+"F0.wireOp",EDGE,"ab5c2a37-a635-476b-a7b1-996719423ef7");
            var Q241;
            Q241=sQuery(id+"F0.wireOp",EDGE,"c773e41e-f025-4dea-8424-73d06e777144");
            var Q242;
            Q242=sQuery(id+"F0.wireOp",EDGE,"43c604ef-1fe6-4677-9a51-841cea193f8d");
            var Q243;
            Q243=sQuery(id+"F0.wireOp",EDGE,"4079cc02-c2ab-48f1-96ad-5e445c7c5daa");
            var Q244;
            Q244=sQuery(id+"F0.wireOp",EDGE,"bca58e95-6a4f-49be-87d3-423e0dfd1e13");
            var Q245;
            Q245=sQuery(id+"F0.wireOp",EDGE,"6f00a1f0-c17a-4e2b-a4dd-3b0ecfeefd3f");
            var Q246;
            Q246=sQuery(id+"F0.wireOp",EDGE,"93af3d28-65ea-42bd-9944-4a01794fa17f");
            var Q247;
            Q247=sQuery(id+"F0.wireOp",EDGE,"8ae477cd-fba8-4ed4-94a7-acbff7aa2caf");
            var Q248;
            Q248=sQuery(id+"F0.wireOp",EDGE,"92b1ff2e-21b9-4bb5-96dc-db7ffe1b1239");
            var Q249;
            Q249=sQuery(id+"F0.wireOp",EDGE,"8eb805be-5375-40c9-ae28-df5c0b9e8e28");
            var Q250;
            Q250=sQuery(id+"F0.wireOp",EDGE,"2bda0f72-8f58-4999-b8dd-a2727c5fdb4b");
            var Q251;
            Q251=sQuery(id+"F0.wireOp",EDGE,"1f0bb823-3707-49dc-b33d-4b8095ea962f");
            var Q252;
            Q252=sQuery(id+"F0.wireOp",EDGE,"436738d1-ee62-4cee-b007-bd71c44ca3ee");
            var Q253;
            Q253=sQuery(id+"F0.wireOp",EDGE,"6871e66e-f4f4-4649-8570-dbceaf7154b2");
            var Q254;
            Q254=sQuery(id+"F0.wireOp",EDGE,"9fadec71-6945-4a52-a4c9-66d324f01180");
            var Q255;
            Q255=sQuery(id+"F0.wireOp",EDGE,"f7e041bd-23ad-4145-8b58-2206bcc89525");
            var Q256;
            Q256=sQuery(id+"F0.wireOp",EDGE,"d1b3a265-2744-436a-a39d-1eaafc116a85");
            var Q257;
            Q257=sQuery(id+"F0.wireOp",EDGE,"7a28e73a-4d55-4a16-8a35-57849b49e6cf");
            var Q258;
            Q258=sQuery(id+"F0.wireOp",EDGE,"6a40ec59-6cc4-48c2-baf1-4f2f2aade053");
            var Q259;
            Q259=sQuery(id+"F0.wireOp",EDGE,"b908e2bf-91f5-4c64-8960-beae9ae2a4d6");
            var Q260;
            Q260=sQuery(id+"F0.wireOp",EDGE,"570633e6-7517-49a3-bff5-82ab9de813d6");
            var Q261;
            Q261=sQuery(id+"F0.wireOp",EDGE,"0945c1b5-d4f9-47c5-b57b-e332ddd4e855");
            var Q262;
            Q262=sQuery(id+"F0.wireOp",EDGE,"fe48725f-090e-4992-abe2-aa71fe558e4d");
            var Q263;
            Q263=sQuery(id+"F0.wireOp",EDGE,"4b5a159b-e256-4dd7-9c17-f72d86f10fcf");
            var Q264;
            Q264=sQuery(id+"F0.wireOp",EDGE,"3c705657-ebd5-4a2e-ba43-6bdac0ab4b9e");
            var Q265;
            Q265=sQuery(id+"F0.wireOp",EDGE,"712e4b28-ff2c-40e8-ba32-9f0605835486");
            var Q266;
            Q266=sQuery(id+"F0.wireOp",EDGE,"24fa234a-2b35-466f-a3cd-e4be737aed86");
            var Q267;
            Q267=sQuery(id+"F0.wireOp",EDGE,"9bad5c4b-02fc-44ea-aa41-48f12b23e18b");
            var Q268;
            Q268=sQuery(id+"F0.wireOp",EDGE,"bc6a7240-a078-410c-acf2-d54f8b2a807b");
            var Q269;
            Q269=sQuery(id+"F0.wireOp",EDGE,"6dd0d1b0-6502-48c5-83cd-8955309dc104");
            var Q270;
            Q270=sQuery(id+"F0.wireOp",EDGE,"32268b4e-ad34-43ab-9daa-f2fcc4560a6d");
            var Q271;
            Q271=sQuery(id+"F0.wireOp",EDGE,"9847225f-f29a-4fec-ab8a-6664b9ebae80");
            var Q272;
            Q272=sQuery(id+"F0.wireOp",EDGE,"f76aca36-b9f6-4e91-a925-d249fead31a3");
            var Q273;
            Q273=sQuery(id+"F0.wireOp",EDGE,"3661c53d-308a-4556-a41e-3306c72a4d35");
            var Q274;
            Q274=sQuery(id+"F0.wireOp",EDGE,"9894e9d3-2c4f-4f0a-b5ea-31c54520a84a");
            var Q275;
            Q275=sQuery(id+"F0.wireOp",EDGE,"2b5b1eb8-1455-416a-8faa-2760d59dd5ea");
            var Q276;
            Q276=sQuery(id+"F0.wireOp",EDGE,"a216fc57-d47b-455a-917e-bdcfa69b1c1a");
            var Q277;
            Q277=sQuery(id+"F0.wireOp",EDGE,"a6661684-0a55-47be-a2fe-69eda20bf1b1");
            var Q278;
            Q278=sQuery(id+"F0.wireOp",EDGE,"24051782-1490-45f2-823c-226c75081577");
            var Q279;
            Q279=sQuery(id+"F0.wireOp",EDGE,"b756afba-3e58-446e-87b1-46c49cb034f2");
            var Q280;
            Q280=sQuery(id+"F0.wireOp",EDGE,"4dce0a22-4cfc-4c9c-890f-304bb43b0c1e");
            var Q281;
            Q281=sQuery(id+"F0.wireOp",EDGE,"15e630bf-ac27-40d4-af00-d534fbea9def");
            var Q282;
            Q282=sQuery(id+"F0.wireOp",EDGE,"ae1db1c7-7ead-4213-8aac-417530f5d9f6");
            var Q283;
            Q283=sQuery(id+"F0.wireOp",EDGE,"e3e8741b-b50c-4bd5-a322-09d9c1e72bdf");
            var Q284;
            Q284=sQuery(id+"F0.wireOp",EDGE,"63ad6c29-aed3-48f2-859c-b3306693e82f");
            var Q285;
            Q285=sQuery(id+"F0.wireOp",EDGE,"718e3965-66f3-4ef3-b966-255703aba622");
            var Q286;
            Q286=sQuery(id+"F0.wireOp",EDGE,"158921ad-1888-4e3c-86d5-c4fb477243ec");
            var Q287;
            Q287=sQuery(id+"F0.wireOp",EDGE,"5c78efcd-c602-4dba-8da5-86049ce937a7");
            var Q288;
            Q288=sQuery(id+"F0.wireOp",EDGE,"30347bf8-ae05-430f-86bc-c305ba899688");
            var Q289;
            Q289=sQuery(id+"F0.wireOp",EDGE,"b231a039-7285-4fb4-ab8a-67ed776e6413");
            var Q290;
            Q290=sQuery(id+"F0.wireOp",EDGE,"dcdc839c-c5f8-4ca7-9aa4-8e69b3a2aa64");
            var Q291;
            Q291=sQuery(id+"F0.wireOp",EDGE,"5f33efc1-c690-47fb-bb11-fc5faa1838b0");
            var Q292;
            Q292=sQuery(id+"F0.wireOp",EDGE,"89cf8f2d-7ce4-4ee7-9fbf-0a5f152fb2c4");
            var Q293;
            Q293=sQuery(id+"F0.wireOp",EDGE,"b1cd398c-b9b1-4cb5-9352-8ca609c9acb4");
            var Q294;
            Q294=sQuery(id+"F0.wireOp",EDGE,"9f1a7cae-6987-429c-a2f6-dcd8041146ed");
            var Q295;
            Q295=sQuery(id+"F0.wireOp",EDGE,"b653d48f-6c5b-402d-aa65-1c5abe97d5c9");
            var Q296;
            Q296=sQuery(id+"F0.wireOp",EDGE,"a163c911-ff0f-4431-9af2-fc6f56f3d0dc");
            var Q297;
            Q297=sQuery(id+"F0.wireOp",EDGE,"e06f4376-9365-41b8-a401-cc906146f956");
            var Q298;
            Q298=sQuery(id+"F0.wireOp",EDGE,"9a7b0da6-876a-49f1-9cb2-73f81be332ee");
            var Q299;
            Q299=sQuery(id+"F0.wireOp",EDGE,"7edf417f-18d5-4661-83cb-a760c2b0dca4");
            var Q300;
            Q300=sQuery(id+"F0.wireOp",EDGE,"5f316655-5179-4d32-a9e7-c273bf19bb4e");
            var Q301;
            Q301=sQuery(id+"F0.wireOp",EDGE,"cba3f01e-f043-4097-a14d-a99c3b3aae8a");
            var Q302;
            Q302=sQuery(id+"F0.wireOp",EDGE,"61b2ee59-7706-448c-a32c-54a21cbc5363");
            var Q303;
            Q303=sQuery(id+"F0.wireOp",EDGE,"e3d86722-bb18-4c24-9244-e51d365b08cf");
            var Q304;
            Q304=sQuery(id+"F0.wireOp",EDGE,"c9cc44c4-6bf0-4fc4-ae87-0e0ed4605d10");
            var Q305;
            Q305=sQuery(id+"F0.wireOp",EDGE,"6dce4068-cadd-49d6-b465-361764826a9d");
            var Q306;
            Q306=sQuery(id+"F0.wireOp",EDGE,"710e49e5-a932-4e02-8173-a4077f0c4e7c");
            var Q307;
            Q307=sQuery(id+"F0.wireOp",EDGE,"2515c18a-6b91-43e9-84db-b8fe3071d6e9");
            var Q308;
            Q308=sQuery(id+"F0.wireOp",EDGE,"33261848-5bcf-4520-ac7e-eabeaf1f0f2b");
            var Q309;
            Q309=sQuery(id+"F0.wireOp",EDGE,"fc8f182c-f0e5-45a0-baa0-0dd0e6b989ff");
            var Q310;
            Q310=sQuery(id+"F0.wireOp",EDGE,"4466e7be-3994-43b8-85b2-0444a8f8d1dd");
            var Q311;
            Q311=sQuery(id+"F0.wireOp",EDGE,"ed43152d-2de0-461a-8572-3cf223b4821f");
            var Q312;
            Q312=sQuery(id+"F0.wireOp",EDGE,"95dfa57d-a339-48d0-a5b1-c31657420968");
            var Q313;
            Q313=sQuery(id+"F0.wireOp",EDGE,"14d6ec74-049e-4f47-bec1-5514d1929b08");
            var Q314;
            Q314=sQuery(id+"F0.wireOp",EDGE,"b6adeab5-bfd9-4105-a79c-e5d7a65deb4e");
            var Q315;
            Q315=sQuery(id+"F0.wireOp",EDGE,"f1fcc84b-c5f8-405b-a788-91acd4fe5d6f");
            var Q316;
            Q316=sQuery(id+"F0.wireOp",EDGE,"204a93df-3e8b-48a8-b4a6-3b1f7df701de");
            var Q317;
            Q317=sQuery(id+"F0.wireOp",EDGE,"68c010cf-21da-4a99-a306-f48544d44a24");
            var Q318;
            Q318=sQuery(id+"F0.wireOp",EDGE,"7d58a832-b1c8-4c1d-b19e-77332a7e850e");
            var Q319;
            Q319=sQuery(id+"F0.wireOp",EDGE,"3ab9c832-2f3e-48ac-b5fe-1d85a0d27515");
            var Q320;
            Q320=sQuery(id+"F0.wireOp",EDGE,"7f598219-c50b-466c-9963-7aa06059f3c3");
            var Q321;
            Q321=sQuery(id+"F0.wireOp",EDGE,"78957a42-6091-469b-8187-228bdeaae0dd");
            var Q322;
            Q322=sQuery(id+"F0.wireOp",EDGE,"3e4c8541-5611-4ef6-bfc6-c9658453a165");
            var Q323;
            Q323=sQuery(id+"F0.wireOp",EDGE,"0309f8bf-6441-49fe-a3e8-633837b1e06e");
            var Q324;
            Q324=sQuery(id+"F0.wireOp",EDGE,"3b007f29-a46e-44af-887e-5e05572845be");
            var Q325;
            Q325=sQuery(id+"F0.wireOp",EDGE,"874044c1-1454-4e66-8967-ed63f41701dd");
            var Q326;
            Q326=sQuery(id+"F0.wireOp",EDGE,"aeade805-d481-4216-bf99-5a48db9cf426");
            var Q327;
            Q327=sQuery(id+"F0.wireOp",EDGE,"00e86a39-94b3-4023-a53f-b4aa44a775ec");
            var Q328;
            Q328=sQuery(id+"F0.wireOp",EDGE,"8c73edf1-6ac8-44ac-b93d-44f0affe2040");
            var Q329;
            Q329=sQuery(id+"F0.wireOp",EDGE,"84fc82e1-304f-471d-92c1-044a46d2f091");
            var Q330;
            Q330=sQuery(id+"F0.wireOp",EDGE,"028781c7-9bd6-4d23-bd54-411b028262f7");
            var Q331;
            Q331=sQuery(id+"F0.wireOp",EDGE,"8932bf57-ea72-4dae-9dd1-05ff1af233dd");
            var Q332;
            Q332=sQuery(id+"F0.wireOp",EDGE,"126f7224-531d-4f22-86f2-2a96b7705991");
            var Q333;
            Q333=sQuery(id+"F0.wireOp",EDGE,"7f7ab259-b4e4-47be-804d-ea5579f4b57c");
            var Q334;
            Q334=sQuery(id+"F0.wireOp",EDGE,"2c314007-30a4-4fe1-a3af-32cab76b0449");
            var Q335;
            Q335=sQuery(id+"F0.wireOp",EDGE,"ca62d923-0b38-4bbd-b99c-2ec846512bf9");
            var Q336;
            Q336=sQuery(id+"F0.wireOp",EDGE,"f6e73acd-588f-42ab-b10e-40382b729b80");
            var Q337;
            Q337=sQuery(id+"F0.wireOp",EDGE,"12e105e2-e15f-4bd6-bff1-c7870034a4d2");
            var Q338;
            Q338=sQuery(id+"F0.wireOp",EDGE,"b31b1fb0-4294-49a1-b997-0bda446484da");
            var Q339;
            Q339=sQuery(id+"F0.wireOp",EDGE,"1dbfca44-5845-4966-bb70-8b692067a66c");
            var Q340;
            Q340=sQuery(id+"F0.wireOp",EDGE,"a0eba54a-3365-4b96-8c49-ce29b1587b5a");
            var Q341;
            Q341=sQuery(id+"F0.wireOp",EDGE,"ed432ea7-389f-475c-bbe5-4f4fec1bebad");
            var Q342;
            Q342=sQuery(id+"F0.wireOp",EDGE,"5ce8c59f-7dfb-414a-a6e0-4ff488a28fb2");
            var Q343;
            Q343=sQuery(id+"F0.wireOp",EDGE,"4f9e31a4-b999-4bc7-95b2-4f159697828c");
            var Q344;
            Q344=sQuery(id+"F0.wireOp",EDGE,"a08e625b-a8c1-4735-a52b-b38f04e63ae5");
            var Q345;
            Q345=sQuery(id+"F0.wireOp",EDGE,"30b75b4c-8e51-4562-910d-645cf956ca61");
            var Q346;
            Q346=sQuery(id+"F0.wireOp",EDGE,"3f55a9e4-e58d-470e-aae4-e4322d856376");
            var Q347;
            Q347=sQuery(id+"F0.wireOp",EDGE,"58556f95-a468-44b5-84d1-0270322461c3");
            var Q348;
            Q348=sQuery(id+"F0.wireOp",EDGE,"84669540-2781-4340-8707-565b3c4a4420");
            var Q349;
            Q349=sQuery(id+"F0.wireOp",EDGE,"e5d889a3-2e26-4ec3-bb59-9820bdcc1709");
            var Q350;
            Q350=sQuery(id+"F0.wireOp",EDGE,"61b373e4-8d44-44e1-8fac-2cf8fd06ca1a");
            var Q351;
            Q351=sQuery(id+"F0.wireOp",EDGE,"486cbbcf-239a-4153-a642-1b963908063b");
            var Q352;
            Q352=sQuery(id+"F0.wireOp",EDGE,"7e7f1c9d-90b9-450c-b268-ec1d7233d4af");
            var Q353;
            Q353=sQuery(id+"F0.wireOp",EDGE,"2008e0ba-7109-4a40-818e-c6843e5ca367");
            var Q354;
            Q354=sQuery(id+"F0.wireOp",EDGE,"f9f3e073-a369-4469-84ee-548d29d14263");
            var Q355;
            Q355=sQuery(id+"F0.wireOp",EDGE,"1666dc2f-26e5-4a43-b4ed-0523ac478243");
            var Q356;
            Q356=sQuery(id+"F0.wireOp",EDGE,"b6161f04-496f-4b7d-8689-fbafaa3d2ab2");
            var Q357;
            Q357=sQuery(id+"F0.wireOp",EDGE,"6097b697-fa79-40b2-89d8-30548b2fe342");
            var Q358;
            Q358=sQuery(id+"F0.wireOp",EDGE,"71a6252e-44d2-4488-a0b3-68043f90e243");
            var Q359;
            Q359=sQuery(id+"F0.wireOp",EDGE,"16519efe-fa94-4315-b088-329e2beecb7e");
            var Q360;
            Q360=sQuery(id+"F0.wireOp",EDGE,"e0bae670-4179-4a6f-b4ed-d68ac16fd916");
            var Q361;
            Q361=sQuery(id+"F0.wireOp",EDGE,"2ceac2f5-cf09-4104-893f-586b7758b944");
            var Q362;
            Q362=sQuery(id+"F0.wireOp",EDGE,"b6577b79-44b1-41c8-8aa2-ad92633e5bf7");
            var Q363;
            Q363=sQuery(id+"F0.wireOp",EDGE,"e6207f82-95ad-43e8-a44c-29849019fe82");
            var Q364;
            Q364=sQuery(id+"F0.wireOp",EDGE,"fe21c3b0-8545-4827-94e6-f4d4723f8b9c");
            var Q365;
            Q365=sQuery(id+"F0.wireOp",EDGE,"acd5adb5-cc08-4699-bc29-15ed15393373");
            var Q366;
            Q366=sQuery(id+"F0.wireOp",EDGE,"4d3f9095-d82f-4b71-84a6-b11eb229af17");
            var Q367;
            Q367=sQuery(id+"F0.wireOp",EDGE,"1972ee2f-3439-49cc-b51c-4b5e933f349d");
            var Q368;
            Q368=sQuery(id+"F0.wireOp",EDGE,"bf17d7c0-23f0-4eeb-a4ec-84e067684ff1");
            var Q369;
            Q369=sQuery(id+"F0.wireOp",EDGE,"2a13326e-54df-4fac-8248-a44836dfc266");
            var Q370;
            Q370=sQuery(id+"F0.wireOp",EDGE,"accbb5f2-97bb-451e-a978-c27f09aaae09");
            var Q371;
            Q371=sQuery(id+"F0.wireOp",EDGE,"aae82bf7-3277-48e7-94ae-f7d85818d0e2");
            var Q372;
            Q372=sQuery(id+"F0.wireOp",EDGE,"12a956a1-5e84-4a9d-8c79-3d2b94aaba04");
            var Q373;
            Q373=sQuery(id+"F0.wireOp",EDGE,"95f9f989-237c-46a1-9153-d42f698fdf2a");
            var Q374;
            Q374=sQuery(id+"F0.wireOp",EDGE,"1c9b03f7-0e23-4665-8c6a-032aca37a267");
            var Q375;
            Q375=sQuery(id+"F0.wireOp",EDGE,"abc2e760-6330-4f7a-bede-db7f0641340b");
            var Q376;
            Q376=sQuery(id+"F0.wireOp",EDGE,"1cf2b08a-386c-4cf3-b4d9-abdf79250f19");
            var Q377;
            Q377=sQuery(id+"F0.wireOp",EDGE,"9e8f7868-09eb-424c-aa2d-208e1253c597");
            var Q378;
            Q378=sQuery(id+"F0.wireOp",EDGE,"1018596e-5666-486b-8f55-d02f80e1e46c");
            var Q379;
            Q379=sQuery(id+"F0.wireOp",EDGE,"62565ba4-7b55-4c83-b18e-ef0d66ed250d");
            var Q380;
            Q380=sQuery(id+"F0.wireOp",EDGE,"a7e0e514-cc88-488c-b14a-00e50b20241a");
            var Q381;
            Q381=sQuery(id+"F0.wireOp",EDGE,"baa9fcec-114a-489a-82e9-f76e113aa5f2");
            var Q382;
            Q382=sQuery(id+"F0.wireOp",EDGE,"a929d149-ba50-4562-b0ef-b6911a79f464");
            var Q383;
            Q383=sQuery(id+"F0.wireOp",EDGE,"8aa420fb-4b32-4e2c-b58d-10d903bb11e4");
            var Q384;
            Q384=sQuery(id+"F0.wireOp",EDGE,"74b43074-f05a-4bc0-acbb-eb525222dad0");
            var Q385;
            Q385=sQuery(id+"F0.wireOp",EDGE,"04be3a19-02d0-47d0-b6bd-d415b195b495");
            var Q386;
            Q386=sQuery(id+"F0.wireOp",EDGE,"3ae136b8-2aae-476a-ad48-e5afa5c5f200");
            var Q387;
            Q387=sQuery(id+"F0.wireOp",EDGE,"818f9023-beba-47a1-9734-fb5f77750908");
            var Q388;
            Q388=sQuery(id+"F0.wireOp",EDGE,"9e5ee8aa-84b6-479b-b720-dbc823c9c2cb");
            var Q389;
            Q389=sQuery(id+"F0.wireOp",EDGE,"61030a76-3b4f-4e34-8c8b-f7bd082feaea");
            var Q390;
            Q390=sQuery(id+"F0.wireOp",EDGE,"852a069f-acdd-4d55-aaa5-9c34f418adec");
            var Q391;
            Q391=sQuery(id+"F0.wireOp",EDGE,"d1679a48-5781-49d6-a762-1f57a16e231c");
            var Q392;
            Q392=sQuery(id+"F0.wireOp",EDGE,"e2f5ea15-fb45-4fc7-8ee5-0d4284da82dd");
            var Q393;
            Q393=sQuery(id+"F0.wireOp",EDGE,"81a5d950-5bc6-491e-b953-c2e267885748");
            var Q394;
            Q394=sQuery(id+"F0.wireOp",EDGE,"408287aa-aef2-4bfa-b4c5-b859ffcee08f");
            var Q395;
            Q395=sQuery(id+"F0.wireOp",EDGE,"1521a068-ac87-4687-8ede-4291755ae4a3");
            var Q396;
            Q396=sQuery(id+"F0.wireOp",EDGE,"1ea76fe4-f069-4d4f-8b46-6f8bb3f885f9");
            var Q397;
            Q397=sQuery(id+"F0.wireOp",EDGE,"9f2170eb-64e5-4ee3-b0cf-414594a6a298");
            var Q398;
            Q398=sQuery(id+"F0.wireOp",EDGE,"f01332b9-ab39-465c-beb6-8984c2184f39");
            var Q399;
            Q399=sQuery(id+"F0.wireOp",EDGE,"b081edc4-6d4d-4b62-9029-b534f9249413");
            var Q400;
            Q400=sQuery(id+"F0.wireOp",EDGE,"4df64e8d-aef7-4c8b-bde6-19b901d8831d");
            var Q401;
            Q401=sQuery(id+"F0.wireOp",EDGE,"4d52244b-6e15-4f8a-b321-d6f5fb858f8a");
            var Q402;
            Q402=sQuery(id+"F0.wireOp",EDGE,"062ede01-6ca6-4aa1-8e3f-5ac7e1b67dcc");
            var Q403;
            Q403=sQuery(id+"F0.wireOp",EDGE,"cee0d511-8e9a-48ae-8dfb-9c4f7ec137aa");
            var Q404;
            Q404=sQuery(id+"F0.wireOp",EDGE,"5913414d-3f83-4224-a811-9e9a5f31ba27");
            var Q405;
            Q405=sQuery(id+"F0.wireOp",EDGE,"a287ea01-349a-4ce3-8832-7d30eb52a30f");
            var Q406;
            Q406=sQuery(id+"F0.wireOp",EDGE,"23476558-9d87-437c-8afa-28353b48b8f6");
            var Q407;
            Q407=sQuery(id+"F0.wireOp",EDGE,"9af30d04-f352-4f79-bdea-c6fd37cae325");
            var Q408;
            Q408=sQuery(id+"F0.wireOp",EDGE,"4044b538-b1f4-4cca-ae7c-bdd926e353ac");
            var Q409;
            Q409=sQuery(id+"F0.wireOp",EDGE,"1d74f1c9-2727-44b3-a0dc-bc47d79da832");
            var Q410;
            Q410=sQuery(id+"F0.wireOp",EDGE,"ec8cd1df-7649-4fb1-8402-4e48e1375cbd");
            var Q411;
            Q411=sQuery(id+"F0.wireOp",EDGE,"4c027a63-fc91-4c6d-9b49-0cc7ded3b89a");
            var Q412;
            Q412=sQuery(id+"F0.wireOp",EDGE,"d8fbec70-6f02-4622-94d1-5e3c853f8e18");
            var Q413;
            Q413=sQuery(id+"F0.wireOp",EDGE,"5e1b5da2-95c4-4f3f-a161-6bc589a541d9");
            var Q414;
            Q414=sQuery(id+"F0.wireOp",EDGE,"beb08d6c-fe16-48a7-b09f-963761e0119b");
            var Q415;
            Q415=sQuery(id+"F0.wireOp",EDGE,"0053698b-7f0f-441e-ac2d-3afd16a290b8");
            var Q416;
            Q416=sQuery(id+"F0.wireOp",EDGE,"e3b8132d-c381-49d8-b3fc-c95c308392c9");
            var Q417;
            Q417=sQuery(id+"F0.wireOp",EDGE,"3f96cf5d-c423-4839-acd3-571db6f1c4a4");
            var Q418;
            Q418=sQuery(id+"F0.wireOp",EDGE,"459af069-a669-41a0-abbb-127ae50cb09f");
            var Q419;
            Q419=sQuery(id+"F0.wireOp",EDGE,"746e4252-9699-4a68-a801-b91c1123648a");
            var Q420;
            Q420=sQuery(id+"F0.wireOp",EDGE,"fe50feef-dcf1-4a6b-8c35-9320cb5e4cbe");
            var Q421;
            Q421=sQuery(id+"F0.wireOp",EDGE,"03c148b0-f31c-49b1-b988-bcbea5c027bd");
            var Q422;
            Q422=sQuery(id+"F0.wireOp",EDGE,"61c519ee-dcf0-4992-82d3-75fec948e721");
            var Q423;
            Q423=sQuery(id+"F0.wireOp",EDGE,"8b661c0d-055b-43d6-b076-b460f0201bf4");
            var Q424;
            Q424=sQuery(id+"F0.wireOp",EDGE,"86b7d3ae-2512-4204-81d7-55256437d0ea");
            var Q425;
            Q425=sQuery(id+"F0.wireOp",EDGE,"6b403c07-df29-4907-900e-dc9875300bd1");
            var Q426;
            Q426=sQuery(id+"F0.wireOp",EDGE,"db41e016-4d70-4cfa-8285-2ca86cf24b85");
            var Q427;
            Q427=sQuery(id+"F0.wireOp",EDGE,"e7d0385e-b609-426d-9841-6c2ff86bdeb3");
            var Q428;
            Q428=sQuery(id+"F0.wireOp",EDGE,"1d7cf3b9-ce58-4f5e-b7e9-dd43746a9bd5");
            var Q429;
            Q429=sQuery(id+"F0.wireOp",EDGE,"74717471-de17-4922-90e5-2b3a44363210");
            var Q430;
            Q430=sQuery(id+"F0.wireOp",EDGE,"20a14537-9657-4727-8691-3caaf883bfd2");
            var Q431;
            Q431=sQuery(id+"F0.wireOp",EDGE,"856912ba-9ee0-4017-bd98-9aa288beb6ab");
            var Q432;
            Q432=sQuery(id+"F0.wireOp",EDGE,"eb656ce3-473f-4dd7-a18d-591eca08611e");
            var Q433;
            Q433=sQuery(id+"F0.wireOp",EDGE,"37818a3f-6017-4e4f-94e6-b467d3b7c78a");
            var Q434;
            Q434=sQuery(id+"F0.wireOp",EDGE,"1c855a8b-861d-49b3-a26b-1d8de9eede60");
            var Q435;
            Q435=sQuery(id+"F0.wireOp",EDGE,"ad004b65-5a30-411a-8582-2a43038239b1");
            var Q436;
            Q436=sQuery(id+"F0.wireOp",EDGE,"fead4a3f-fffd-4bac-a116-a2bed4ae2169");
            var Q437;
            Q437=sQuery(id+"F0.wireOp",EDGE,"50de83bb-6e24-4fae-9847-076ee6852f0a");
            var Q438;
            Q438=sQuery(id+"F0.wireOp",EDGE,"d09f2845-53bc-48ac-af47-265ab2f3e3e4");
            var Q439;
            Q439=sQuery(id+"F0.wireOp",EDGE,"bca4a6a0-f7b9-4618-aa7d-5371c57d0069");
            var Q440;
            Q440=sQuery(id+"F0.wireOp",EDGE,"ad4288c3-60d3-4e8a-85c4-79febd1164e9");
            var Q441;
            Q441=sQuery(id+"F0.wireOp",EDGE,"04bd206b-1085-4bce-9c2a-501427a26078");
            var Q442;
            Q442=sQuery(id+"F0.wireOp",EDGE,"94efd2e8-0d98-4ded-b020-3afcd68a3189");
            var Q443;
            Q443=sQuery(id+"F0.wireOp",EDGE,"94e78dc4-5c38-466c-8268-dc58d093b5e9");
            var Q444;
            Q444=sQuery(id+"F0.wireOp",EDGE,"2b8c4a85-bdba-4d41-9cf2-5207d5fd6afb");
            var Q445;
            Q445=sQuery(id+"F0.wireOp",EDGE,"ad31e87b-84e1-4a4f-8fc6-74022bd5d25d");
            var Q446;
            Q446=sQuery(id+"F0.wireOp",EDGE,"0a351fb9-3afd-42db-9c8d-c5b8ad01d728");
            var Q447;
            Q447=sQuery(id+"F0.wireOp",EDGE,"14f5f2c0-b85c-4341-b750-154b67dc4070");
            var Q448;
            Q448=sQuery(id+"F0.wireOp",EDGE,"63f59df1-76b3-4343-966d-a60838649a05");
            var Q449;
            Q449=sQuery(id+"F0.wireOp",EDGE,"25189332-8524-44fe-a2fc-aac3fa488e39");
            var Q450;
            Q450=sQuery(id+"F0.wireOp",EDGE,"f874bbcb-a2bc-46bd-b6d7-44ba1279ee91");
            var Q451;
            Q451=sQuery(id+"F0.wireOp",EDGE,"d0a7814a-1222-4f8c-8e7a-80471a822548");
            var Q452;
            Q452=sQuery(id+"F0.wireOp",EDGE,"122a558a-46c0-43a0-b15c-9dfba89fbb0f");
            var Q453;
            Q453=sQuery(id+"F0.wireOp",EDGE,"a7cd5c29-5fd4-400a-9add-82191ceda874");
            var Q454;
            Q454=sQuery(id+"F0.wireOp",EDGE,"61fe6b3d-6e93-497c-8f0d-b6404c1d344b");
            var Q455;
            Q455=sQuery(id+"F0.wireOp",EDGE,"5bd33001-578a-4f51-a1e8-2a873ceb4bee");
            var Q456;
            Q456=sQuery(id+"F0.wireOp",EDGE,"8fa2012b-84e6-4fbf-af20-03d72d2b540c");
            var Q457;
            Q457=sQuery(id+"F0.wireOp",EDGE,"7c340835-bed0-4727-9ef2-b1d094dccd83");
            var Q458;
            Q458=sQuery(id+"F0.wireOp",EDGE,"047ad523-9107-4e7c-be35-fc26db93e666");
            var Q459;
            Q459=sQuery(id+"F0.wireOp",EDGE,"3b7d9e52-e2fd-4dde-a7ae-a3087f1199db");
            var Q460;
            Q460=sQuery(id+"F0.wireOp",EDGE,"d47b0123-c20f-40ee-8a46-1addfb46e102");
            var Q461;
            Q461=sQuery(id+"F0.wireOp",EDGE,"985666c0-7fd1-4443-affd-4eb1e8e5d53d");
            var Q462;
            Q462=sQuery(id+"F0.wireOp",EDGE,"90582e85-4e1a-441e-a53f-043b378d98f3");
            var Q463;
            Q463=sQuery(id+"F0.wireOp",EDGE,"aa626575-5564-470a-84cd-c627e7de4aed");
            var Q464;
            Q464=sQuery(id+"F0.wireOp",EDGE,"a3b6b441-427d-440b-8c2c-80785c929e40");
            var Q465;
            Q465=sQuery(id+"F0.wireOp",EDGE,"e57f89cf-6cb2-42af-9578-f0ef4107fd33");
            var Q466;
            Q466=sQuery(id+"F0.wireOp",EDGE,"5a2435ae-17a7-4fbb-ba20-4a0f65af2d1d");
            var Q467;
            Q467=sQuery(id+"F0.wireOp",EDGE,"138eb31f-5006-46d0-8ca8-2c67495791fd");
            var Q468;
            Q468=sQuery(id+"F0.wireOp",EDGE,"6579bb54-9fdc-4110-88a4-7906c3ef3556");
            var Q469;
            Q469=sQuery(id+"F0.wireOp",EDGE,"0cf7208c-1a71-47df-97c8-53c6d421c9fb");
            var Q470;
            Q470=sQuery(id+"F0.wireOp",EDGE,"60fff4b6-1947-4d59-b7c1-1105943900dd");
            var Q471;
            Q471=sQuery(id+"F0.wireOp",EDGE,"fcb45c1f-8973-439f-8532-e83cd1331289");
            var Q472;
            Q472=sQuery(id+"F0.wireOp",EDGE,"78226ede-3183-4892-a582-1516693a27e7");
            var Q473;
            Q473=sQuery(id+"F0.wireOp",EDGE,"e9164195-c5de-4080-8e3c-23046a038e85");
            var Q474;
            Q474=sQuery(id+"F0.wireOp",EDGE,"363e33d5-ca43-466f-b69f-5dc54007e29f");
            var Q475;
            Q475=sQuery(id+"F0.wireOp",EDGE,"8814b402-bf88-4c52-954c-bdbb337b8d1a");
            var Q476;
            Q476=sQuery(id+"F0.wireOp",EDGE,"103e89e5-d0ac-4b7d-bfa2-d84d0dff8951");
            var Q477;
            Q477=sQuery(id+"F0.wireOp",EDGE,"0b43ab89-c2a8-4938-9f7a-d08a511a6cbd");
            var Q478;
            Q478=sQuery(id+"F0.wireOp",EDGE,"5d77cda3-eaab-46da-83d2-ffa8dcd8220a");
            var Q479;
            Q479=sQuery(id+"F0.wireOp",EDGE,"66983001-3dcd-4b9e-9670-77a27fbc2c54");
            var Q480;
            Q480=sQuery(id+"F0.wireOp",EDGE,"bd8d5075-2a82-4e18-83e0-74c8aefd0e32");
            var Q481;
            Q481=sQuery(id+"F0.wireOp",EDGE,"a89e7e69-11db-41a8-8a74-ba4250ee6a85");
            var Q482;
            Q482=sQuery(id+"F0.wireOp",EDGE,"1c7fb0ba-077d-483b-ae1c-1dde5a594371");
            var Q483;
            Q483=sQuery(id+"F0.wireOp",EDGE,"855afb09-258e-4880-b1a1-0f2b59b4fe2f");
            var Q484;
            Q484=sQuery(id+"F0.wireOp",EDGE,"b259bfec-d253-4a2c-a24f-7d8631b7afd7");
            var Q485;
            Q485=sQuery(id+"F0.wireOp",EDGE,"84603e5c-3b30-417f-a56a-e882bd6a0b5d");
            var Q486;
            Q486=sQuery(id+"F0.wireOp",EDGE,"1521c41d-b5c9-45ff-9edc-56230a2ed4a4");
            var Q487;
            Q487=sQuery(id+"F0.wireOp",EDGE,"dcaeb994-f153-4958-87bc-431588b68df6");
            var Q488;
            Q488=sQuery(id+"F0.wireOp",EDGE,"52bfafaf-e2e3-4d72-9107-243d2d8a8012");
            var Q489;
            Q489=sQuery(id+"F0.wireOp",EDGE,"9a957709-b59b-49a7-8d84-3ec4f9c2ec1c");
            var Q490;
            Q490=sQuery(id+"F0.wireOp",EDGE,"1d7add12-6228-4d84-adc0-d71fdaa25509");
            var Q491;
            Q491=sQuery(id+"F0.wireOp",EDGE,"767627d2-8812-495f-a08f-95b5ddd45e37");
            var Q492;
            Q492=sQuery(id+"F0.wireOp",EDGE,"2e620b6b-c55f-47db-a814-7f7551ff26b4");
            var Q493;
            Q493=sQuery(id+"F0.wireOp",EDGE,"6ec58471-5e6a-44d2-9282-e2fa170a3529");
            var Q494;
            Q494=sQuery(id+"F0.wireOp",EDGE,"f2db79c3-2ec8-4911-b557-ad6997a9c13a");
            var Q495;
            Q495=sQuery(id+"F0.wireOp",EDGE,"f909c35a-6754-47e2-9080-053ec47216d0");
            var Q496;
            Q496=sQuery(id+"F0.wireOp",EDGE,"2ffa262c-3d37-44a7-b3ec-6c19a3cba8fb");
            var Q497;
            Q497=sQuery(id+"F0.wireOp",EDGE,"f294d6b1-f3cc-4531-a978-8ce670211157");
            var Q498;
            Q498=sQuery(id+"F0.wireOp",EDGE,"cd4d4eb2-46ab-4ec9-853f-bd4721f7408c");
            var Q499;
            Q499=sQuery(id+"F0.wireOp",EDGE,"f322850d-93d2-4033-a75d-11cdfe81a91c");
            var Q500;
            Q500=sQuery(id+"F0.wireOp",EDGE,"95bcaee2-c604-4096-9b52-2f57d6947b0d");
            var Q501;
            Q501=sQuery(id+"F0.wireOp",EDGE,"e25eeb5b-34e6-4129-a03c-dcfd41d91f73");
            var Q502;
            Q502=sQuery(id+"F0.wireOp",EDGE,"629f2785-6231-4ca9-b1ae-5ccadb133575");
            var Q503;
            Q503=sQuery(id+"F0.wireOp",EDGE,"73bea145-0604-4790-bd75-3ad1a1fd2b06");
            var Q504;
            Q504=sQuery(id+"F0.wireOp",EDGE,"6d864eac-8b9e-4b4e-b713-f6acc84c62a5");
            var Q505;
            Q505=sQuery(id+"F0.wireOp",EDGE,"ddd51366-a982-45c5-ace5-e961c7d109e9");
            var Q506;
            Q506=sQuery(id+"F0.wireOp",EDGE,"4d4cfdc5-eb0c-424f-82f5-38dc03d1feb1");
            var Q507;
            Q507=sQuery(id+"F0.wireOp",EDGE,"20cf5957-0f8b-48ea-a3bf-d9edb72e515b");
            var Q508;
            Q508=sQuery(id+"F0.wireOp",EDGE,"ce6b0072-47a3-426d-b32f-67d89b43b61f");
            var Q509;
            Q509=sQuery(id+"F0.wireOp",EDGE,"d268efd0-19cb-44ab-a888-f4f92552d823");
            var Q510;
            Q510=sQuery(id+"F0.wireOp",EDGE,"bc6ca0f5-1c83-4e7c-ab08-0d68b6054148");
            var Q511;
            Q511=sQuery(id+"F0.wireOp",EDGE,"f9f941f6-80c6-4b83-95b8-22a7d0e9cafc");
            var Q512;
            Q512=sQuery(id+"F0.wireOp",EDGE,"c8ee8d35-d1ad-4dd7-bd1e-fd29dfbc38be");
            var Q513;
            Q513=sQuery(id+"F0.wireOp",EDGE,"ebe46ed6-a27a-4f61-8de2-f27ac0004ce6");
            var Q514;
            Q514=sQuery(id+"F0.wireOp",EDGE,"4f7adc8d-dbf4-4aff-82d3-fae2ad54f90e");
            var Q515;
            Q515=sQuery(id+"F0.wireOp",EDGE,"b892e461-1800-4299-a272-a8766a2c0126");
            var Q516;
            Q516=sQuery(id+"F0.wireOp",EDGE,"d4718cb8-9a10-49d8-9282-53fb380303af");
            var Q517;
            Q517=sQuery(id+"F0.wireOp",EDGE,"3059d69b-787c-487b-8717-4fae857d1f42");
            var Q518;
            Q518=sQuery(id+"F0.wireOp",EDGE,"a3b952db-0257-40e8-ae82-e3719db8004d");
            var Q519;
            Q519=sQuery(id+"F0.wireOp",EDGE,"2ae867bc-aa63-4b58-ae0f-ce66b7cd19fb");
            var Q520;
            Q520=sQuery(id+"F0.wireOp",EDGE,"3534428a-10a2-4703-8563-a62eec53282b");
            var Q521;
            Q521=sQuery(id+"F0.wireOp",EDGE,"c6fa1ef4-1829-44e2-ba8c-4f02416815c2");
            var Q522;
            Q522=sQuery(id+"F0.wireOp",EDGE,"678b29cd-7408-411b-b8d6-83b0cb157339");
            var Q523;
            Q523=sQuery(id+"F0.wireOp",EDGE,"b4290da5-aa83-4878-b36c-5c5d78594994");
            var Q524;
            Q524=sQuery(id+"F0.wireOp",EDGE,"7fd1c1f9-1e59-476b-bc0f-8a9a7843098e");
            var Q525;
            Q525=sQuery(id+"F0.wireOp",EDGE,"181fb608-04f6-4f8d-acc7-bbf37972e770");
            var Q526;
            Q526=sQuery(id+"F0.wireOp",EDGE,"3236ed16-407d-4a48-a6ec-0911b0473962");
            var Q527;
            Q527=sQuery(id+"F0.wireOp",EDGE,"efc84da6-379c-46fe-949c-e08be640cc81");
            var Q528;
            Q528=sQuery(id+"F0.wireOp",EDGE,"b547bb45-8b37-4fea-b03f-8b909485fec0");
            var Q529;
            Q529=sQuery(id+"F0.wireOp",EDGE,"6141d76a-66b2-4cfa-8000-5c3b377c6a02");
            var Q530;
            Q530=sQuery(id+"F0.wireOp",EDGE,"71c3bac6-e149-4125-bbc5-d9cc39433aa6");
            var Q531;
            Q531=sQuery(id+"F0.wireOp",EDGE,"68f54daa-9af1-4f3c-ba8d-6079211c1d63");
            var Q532;
            Q532=sQuery(id+"F0.wireOp",EDGE,"f3010785-e4a9-4ec1-93bf-d890c295b738");
            var Q533;
            Q533=sQuery(id+"F0.wireOp",EDGE,"126d7365-51e2-426c-8cb6-536c46931f65");
            var Q534;
            Q534=sQuery(id+"F0.wireOp",EDGE,"334171b9-4515-4770-aa89-8a8e3261534c");
            var Q535;
            Q535=sQuery(id+"F0.wireOp",EDGE,"2250db4e-00d1-4e57-9ab2-bd91be94555a");
            var Q536;
            Q536=sQuery(id+"F0.wireOp",EDGE,"545b69c8-dc73-497a-a742-3a0c497953a6");
            var Q537;
            Q537=sQuery(id+"F0.wireOp",EDGE,"b33c4c3b-a7a0-43cc-9078-d9c7c5fd1229");
            var Q538;
            Q538=sQuery(id+"F0.wireOp",EDGE,"80d477bc-515c-4f64-b593-cfb2aa7a9c4f");
            var Q539;
            Q539=sQuery(id+"F0.wireOp",EDGE,"876ef25c-f7ce-4574-aee9-d59c1eef4dcb");
            var Q540;
            Q540=sQuery(id+"F0.wireOp",EDGE,"2f0a1aab-41c3-472d-ace1-a9096a0dafa2");
            var Q541;
            Q541=sQuery(id+"F0.wireOp",EDGE,"1d22b484-5126-495f-aee6-751e27c0418c");
            var Q542;
            Q542=sQuery(id+"F0.wireOp",EDGE,"7af0be32-e452-42b8-86a6-29ad33cbadd3");
            var Q543;
            Q543=sQuery(id+"F0.wireOp",EDGE,"4c129c47-0274-40e5-98b1-a33b40a2b2fc");
            var Q544;
            Q544=sQuery(id+"F0.wireOp",EDGE,"2435d7a4-2d50-46ef-baa9-c1734e7df4fe");
            var Q545;
            Q545=sQuery(id+"F0.wireOp",EDGE,"15886489-f7c5-4ab4-9d1b-a21e5d648e21");
            var Q546;
            Q546=sQuery(id+"F0.wireOp",EDGE,"e48f69d3-f6f8-4ae4-aa1d-f9d0081d6522");
            var Q547;
            Q547=sQuery(id+"F0.wireOp",EDGE,"65b74898-40b1-44fa-8f85-aeca3648dd59");
            var Q548;
            Q548=sQuery(id+"F0.wireOp",EDGE,"4859540f-82e8-4cb2-bb7c-dfc8782d8730");
            var Q549;
            Q549=sQuery(id+"F0.wireOp",EDGE,"f534458d-67de-405e-b991-805b723b8329");
            var Q550;
            Q550=sQuery(id+"F0.wireOp",EDGE,"a40f3c3d-bb30-436c-9dec-d2ab363f0958");
            var Q551;
            Q551=sQuery(id+"F0.wireOp",EDGE,"53351925-de40-4414-89a6-2044e8fd5543");
            var Q552;
            Q552=sQuery(id+"F0.wireOp",EDGE,"d76a8e36-dc11-4a94-b226-187974253dc5");
            var Q553;
            Q553=sQuery(id+"F0.wireOp",EDGE,"39f3253a-00e6-44e3-bec9-cd7d99c9d8f4");
            var Q554;
            Q554=sQuery(id+"F0.wireOp",EDGE,"304c153c-0716-49de-bf70-49e62218028a");
            var Q555;
            Q555=sQuery(id+"F0.wireOp",EDGE,"b3420633-8995-4156-9ac5-687f4ffe3503");
            var Q556;
            Q556=sQuery(id+"F0.wireOp",EDGE,"b8fbef81-bc51-4624-ad45-7c49b05c5eb9");
            var Q557;
            Q557=sQuery(id+"F0.wireOp",EDGE,"a406faed-58cd-488f-8b9f-885bab66d5ac");
            var Q558;
            Q558=sQuery(id+"F0.wireOp",EDGE,"3640537b-b84e-4b88-8daa-1380de25c44a");
            var Q559;
            Q559=sQuery(id+"F0.wireOp",EDGE,"42e48f3b-33a9-4518-904e-2412c949bbdb");
            var Q560;
            Q560=sQuery(id+"F0.wireOp",EDGE,"0335961c-c5e0-47e5-81b6-1a9b5a213c74");
            var Q561;
            Q561=sQuery(id+"F0.wireOp",EDGE,"662e1da9-27fa-4af8-8210-4b79d9af7e42");
            var Q562;
            Q562=sQuery(id+"F0.wireOp",EDGE,"6dc66cb9-4606-4c16-b73f-9c32e0d650f2");
            var Q563;
            Q563=sQuery(id+"F0.wireOp",EDGE,"8c7b1507-d709-4f38-a0db-4572cdcd4fb5");
            var Q564;
            Q564=sQuery(id+"F0.wireOp",EDGE,"1d598116-0a88-46cf-9af7-efce2bf9acaf");
            var Q565;
            Q565=sQuery(id+"F0.wireOp",EDGE,"eb35c1ed-7a78-4a26-93f9-9f972ea6e778");
            var Q566;
            Q566=sQuery(id+"F0.wireOp",EDGE,"991f671b-3fc3-4cf1-977e-17d6a43d86e3");
            var Q567;
            Q567=sQuery(id+"F0.wireOp",EDGE,"8113fb5b-df3c-48b9-a42a-0252b4344fd1");
            var Q568;
            Q568=sQuery(id+"F0.wireOp",EDGE,"00c08814-0dae-4830-b04e-e777c80183d1");
            var Q569;
            Q569=sQuery(id+"F0.wireOp",EDGE,"a83ebc36-fa0f-4deb-ac05-1dcbd97d0ebc");
            var Q570;
            Q570=sQuery(id+"F0.wireOp",EDGE,"0f9137b7-eb45-420e-b4fe-33be502bb732");
            var Q571;
            Q571=sQuery(id+"F0.wireOp",EDGE,"c5eeed70-3087-4086-8b51-9a2197a59f51");
            var Q572;
            Q572=sQuery(id+"F0.wireOp",EDGE,"5c179d0c-7561-4c51-98e1-cdacce0068da");
            var Q573;
            Q573=sQuery(id+"F0.wireOp",EDGE,"270b7cf6-df7e-4ad7-846b-66cf83c905c5");
            var Q574;
            Q574=sQuery(id+"F0.wireOp",EDGE,"9a0ad8ed-b740-422e-a79d-8846f2c223b1");
            var Q575;
            Q575=sQuery(id+"F0.wireOp",EDGE,"7fc0f6ad-9c5e-42ce-a64d-e90a39e26311");
            var Q576;
            Q576=sQuery(id+"F0.wireOp",EDGE,"94aaf6db-da50-4de8-aff1-3cd9b643884a");
            var Q577;
            Q577=sQuery(id+"F0.wireOp",EDGE,"ac737ff0-e154-4660-8b70-dee6eeafc03c");
            var Q578;
            Q578=sQuery(id+"F0.wireOp",EDGE,"d38faf90-d12e-4353-93af-609026f644d9");
            var Q579;
            Q579=sQuery(id+"F0.wireOp",EDGE,"33fd6c38-110c-40f3-8bdd-ebd8e5271663");
            var Q580;
            Q580=sQuery(id+"F0.wireOp",EDGE,"e9183c95-dab9-4603-b802-1c0d8e577071");
            var Q581;
            Q581=sQuery(id+"F0.wireOp",EDGE,"e2a7d1cc-622f-4fef-8903-18175652cb58");
            var Q582;
            Q582=sQuery(id+"F0.wireOp",EDGE,"b301fa47-36ff-41bb-b319-0c76f3083598");
            var Q583;
            Q583=sQuery(id+"F0.wireOp",EDGE,"45303744-8f52-411d-ac07-4fc6d226e0ae");
            var Q584;
            Q584=sQuery(id+"F0.wireOp",EDGE,"b43fcb64-529b-49a0-9773-2f20c657565c");
            var Q585;
            Q585=sQuery(id+"F0.wireOp",EDGE,"2e18731b-3c5a-4707-a521-355c8674fe0e");
            var Q586;
            Q586=sQuery(id+"F0.wireOp",EDGE,"6cab2b07-7205-43b9-8677-4e380babddfa");
            var Q587;
            Q587=sQuery(id+"F0.wireOp",EDGE,"6457d740-0cfb-4044-900d-e9596b45bfd0");
            var Q588;
            Q588=sQuery(id+"F0.wireOp",EDGE,"4e459bb9-8ef5-444f-b456-edb38bfbeabf");
            var Q589;
            Q589=sQuery(id+"F0.wireOp",EDGE,"19701cad-3e9d-428e-8ec7-2a4abf53ce56");
            var Q590;
            Q590=sQuery(id+"F0.wireOp",EDGE,"a242cedd-8ce7-46c7-ae1a-0be622896d55");
            var Q591;
            Q591=sQuery(id+"F0.wireOp",EDGE,"7efe9093-d4bd-423a-a445-f889e4992ef7");
            var Q592;
            Q592=sQuery(id+"F0.wireOp",EDGE,"7991c37b-6eb9-4ae1-a9c3-eff94d62ca07");
            var Q593;
            Q593=sQuery(id+"F0.wireOp",EDGE,"c0d66a6c-0395-40b6-bf6d-4c6a18810018");
            var Q594;
            Q594=sQuery(id+"F0.wireOp",EDGE,"6f9969c4-def1-49c8-aa67-97094f565530");
            var Q595;
            Q595=sQuery(id+"F0.wireOp",EDGE,"8cff4383-1351-42ae-aad1-24c93fd16937");
            var Q596;
            Q596=sQuery(id+"F0.wireOp",EDGE,"b2538979-2fb2-4adb-9d3d-97deef6632db");
            var Q597;
            Q597=sQuery(id+"F0.wireOp",EDGE,"948aea44-44d9-46fb-8056-d7e348bdcf2b");
            var Q598;
            Q598=sQuery(id+"F0.wireOp",EDGE,"099d4304-3dc5-4396-a74d-00eca0c31b43");
            var Q599;
            Q599=sQuery(id+"F0.wireOp",EDGE,"aecd66bf-2c05-468a-b9de-942bc829af6f");
            var Q600;
            Q600=sQuery(id+"F0.wireOp",EDGE,"987c5c36-b9b9-41f9-9459-8b387259daf4");
            var Q601;
            Q601=sQuery(id+"F0.wireOp",EDGE,"a8880e3a-2da7-42e0-aa09-8fc4072df998");
            var Q602;
            Q602=sQuery(id+"F0.wireOp",EDGE,"69075c17-7add-4dc3-90b8-8420b4227d44");
            var Q603;
            Q603=sQuery(id+"F0.wireOp",EDGE,"a20a391b-d6b4-480c-8e4c-ea38b6fb079c");
            var Q604;
            Q604=sQuery(id+"F0.wireOp",EDGE,"c447e8ad-e551-43e8-a884-fb509faff453");
            var Q605;
            Q605=sQuery(id+"F0.wireOp",EDGE,"56eface6-be90-4fbe-9e41-77e5f2525ff9");
            var Q606;
            Q606=sQuery(id+"F0.wireOp",EDGE,"953304b0-fea2-4dcc-b61e-3adaf178347f");
            var Q607;
            Q607=sQuery(id+"F0.wireOp",EDGE,"02ab138e-a8e5-4097-929b-9b4e8bfc950e");
            var Q608;
            Q608=sQuery(id+"F0.wireOp",EDGE,"1ccc4ecd-4d2f-46fa-843b-94b6a04a40e8");
            var Q609;
            Q609=sQuery(id+"F0.wireOp",EDGE,"55ca0f4a-92f6-4912-963c-41051052d43d");
            var Q610;
            Q610=sQuery(id+"F0.wireOp",EDGE,"3089c7ce-1d6d-41ab-b5b5-c02007b3f125");
            var Q611;
            Q611=sQuery(id+"F0.wireOp",EDGE,"22e27a29-c939-4432-ae82-c66144d3f8a8");
            var Q612;
            Q612=sQuery(id+"F0.wireOp",EDGE,"ebce9ea1-7e3b-435b-940c-9bdb7ebe10d3");
            var Q613;
            Q613=sQuery(id+"F0.wireOp",EDGE,"9368a4a1-f6ca-4676-b286-f0b772f65f9a");
            var Q614;
            Q614=sQuery(id+"F0.wireOp",EDGE,"5b753b46-ac8d-4a28-b5e6-ac26fa3aba35");
            var Q615;
            Q615=sQuery(id+"F0.wireOp",EDGE,"46b7b235-c6d7-4a5e-83b4-7382c38b1a18");
            var Q616;
            Q616=sQuery(id+"F0.wireOp",EDGE,"d5195f34-a264-4dc9-aafc-7404a82c1feb");
            var Q617;
            Q617=sQuery(id+"F0.wireOp",EDGE,"c04d38db-e472-4780-b497-96328ae812d2");
            var Q618;
            Q618=sQuery(id+"F0.wireOp",EDGE,"7f870fd5-554b-4571-bd31-e5869345d474");
            var Q619;
            Q619=sQuery(id+"F0.wireOp",EDGE,"b671f6f3-9a51-46a8-aaaa-25116b8914c8");
            var Q620;
            Q620=sQuery(id+"F0.wireOp",EDGE,"4fd65f93-ba25-46b8-9e08-2a940c798a7b");
            var Q621;
            Q621=sQuery(id+"F0.wireOp",EDGE,"a65fadf5-8a31-4e71-9bf1-9adca0af22ea");
            var Q622;
            Q622=sQuery(id+"F0.wireOp",EDGE,"a18aa294-8ccb-46b8-8135-a6581ec408d9");
            var Q623;
            Q623=sQuery(id+"F0.wireOp",EDGE,"b92d5a49-a1f8-4d22-aea0-572ef872cd39");
            var Q624;
            Q624=sQuery(id+"F0.wireOp",EDGE,"d610c442-713c-4641-9add-4836c36d2f9f");
            var Q625;
            Q625=sQuery(id+"F0.wireOp",EDGE,"8a1bc0ea-885b-4b11-ba9e-97b58299f71a");
            var Q626;
            Q626=sQuery(id+"F0.wireOp",EDGE,"4a6db11d-b61b-4708-a483-3eb312625c01");
            var Q627;
            Q627=sQuery(id+"F0.wireOp",EDGE,"70f66ffb-2d23-429a-8063-bf022e6057d7");
            var Q628;
            Q628=sQuery(id+"F0.wireOp",EDGE,"743380f7-2b8d-41ec-9f85-d48e925f2bd1");
            var Q629;
            Q629=sQuery(id+"F0.wireOp",EDGE,"d87e8a83-96c2-4b1e-8cb5-b707d2837be9");
            var Q630;
            Q630=sQuery(id+"F0.wireOp",EDGE,"e5d3cdfa-3711-47e8-bf9f-094b4e82d1ff");
            var Q631;
            Q631=sQuery(id+"F0.wireOp",EDGE,"ad9ce5de-9991-47ae-85a1-6dcfda4b9fc4");
            var Q632;
            Q632=sQuery(id+"F0.wireOp",EDGE,"abe799c4-63ec-4827-a1b8-e1bb9576732a");
            var Q633;
            Q633=sQuery(id+"F0.wireOp",EDGE,"54e15c2e-8928-4066-9047-b1e4b816bc72");
            var Q634;
            Q634=sQuery(id+"F0.wireOp",EDGE,"020fd7f6-e0a4-4712-85a6-0d94a65bc6d7");
            var Q635;
            Q635=sQuery(id+"F0.wireOp",EDGE,"76ed57cb-2b10-4bb2-8cec-b3f523b176d2");
            var Q636;
            Q636=sQuery(id+"F0.wireOp",EDGE,"dc0ed29d-52bd-464f-8991-b9bc578032a4");
            var Q637;
            Q637=sQuery(id+"F0.wireOp",EDGE,"9e2b3d73-4488-4a3b-9733-8ecd06b07509");
            var Q638;
            Q638=sQuery(id+"F0.wireOp",EDGE,"a29dc876-9db7-4a89-a450-7af35f3cb388");
            var Q639;
            Q639=sQuery(id+"F0.wireOp",EDGE,"4364685c-3655-49fd-800c-490fc8903b5b");
            var Q640;
            Q640=sQuery(id+"F0.wireOp",EDGE,"018c0786-f949-4b1c-abf8-d1667153acaf");
            var Q641;
            Q641=sQuery(id+"F0.wireOp",EDGE,"6d4cbf3b-d2bf-4092-b6fd-58351ac4f9bd");
            var Q642;
            Q642=sQuery(id+"F0.wireOp",EDGE,"061016bb-9cf1-4489-afa5-f1603262daca");
            var Q643;
            Q643=sQuery(id+"F0.wireOp",EDGE,"83e09370-cfd8-4c83-a232-c6fda9a2d27e");
            var Q644;
            Q644=sQuery(id+"F0.wireOp",EDGE,"fa4b581a-ed49-42b6-93a1-7cfb0767069c");
            var Q645;
            Q645=sQuery(id+"F0.wireOp",EDGE,"b92a198d-c671-4bd5-b6b3-bef59f8d9a6d");
            var Q646;
            Q646=sQuery(id+"F0.wireOp",EDGE,"bf8243a6-dccb-46d1-98c1-534a4fe33bcb");
            var Q647;
            Q647=sQuery(id+"F0.wireOp",EDGE,"c044a52e-9505-406e-b41a-7be4f5355ce6");
            var Q648;
            Q648=sQuery(id+"F0.wireOp",EDGE,"6fac1e2b-f734-4df1-b866-19195771f8a1");
            var Q649;
            Q649=sQuery(id+"F0.wireOp",EDGE,"b20ce43b-34bf-4841-a319-3e148cdc7794");
            var Q650;
            Q650=sQuery(id+"F0.wireOp",EDGE,"02ce821f-2bb9-4bfe-b08c-b08bea45f7bd");
            var Q651;
            Q651=sQuery(id+"F0.wireOp",EDGE,"1ef8e333-4829-4ddf-970f-f7e3895e13a7");
            var Q652;
            Q652=sQuery(id+"F0.wireOp",EDGE,"ab700dc7-1bc6-4c5d-a51c-849c878ad7cb");
            var Q653;
            Q653=sQuery(id+"F0.wireOp",EDGE,"d4280c2b-752b-489d-bebd-418eb61c9082");
            var Q654;
            Q654=sQuery(id+"F0.wireOp",EDGE,"df424ed9-d181-495f-a0c5-fb957548713b");
            var Q655;
            Q655=sQuery(id+"F0.wireOp",EDGE,"9e68c307-734d-4a2b-a868-2336a36cb550");
            var Q656;
            Q656=sQuery(id+"F0.wireOp",EDGE,"549f8dbe-e9b3-42c2-960e-1c57ae7ea28f");
            var Q657;
            Q657=sQuery(id+"F0.wireOp",EDGE,"b07ebf06-a3d7-4b9c-9f7b-4e265d567a61");
            var Q658;
            Q658=sQuery(id+"F0.wireOp",EDGE,"06857f45-8830-4d91-b144-bc580efe798d");
            var Q659;
            Q659=sQuery(id+"F0.wireOp",EDGE,"ea567a39-acc3-49b9-85aa-239862508a53");
            var Q660;
            Q660=sQuery(id+"F0.wireOp",EDGE,"995e7647-eab6-4a35-8b1e-6fde6900bb77");
            var Q661;
            Q661=sQuery(id+"F0.wireOp",EDGE,"9ab9f135-e806-45ae-b913-60e4fb588830");
            var Q662;
            Q662=sQuery(id+"F0.wireOp",EDGE,"5d78e72e-dda5-449d-b283-c41b32ca25cd");
            var Q663;
            Q663=sQuery(id+"F0.wireOp",EDGE,"318dbd9d-6c31-49d0-943e-419c939a4628");
            var Q664;
            Q664=sQuery(id+"F0.wireOp",EDGE,"1b0f0d51-5396-4324-9b6d-0ea6724a4315");
            var Q665;
            Q665=sQuery(id+"F0.wireOp",EDGE,"b8199065-0982-4be0-9a66-622dd85793d0");
            var Q666;
            Q666=sQuery(id+"F0.wireOp",EDGE,"5c529e34-28a0-4e24-bf9e-03afb7a7ec65");
            var Q667;
            Q667=sQuery(id+"F0.wireOp",EDGE,"0ba5c6f0-e917-44ab-bd94-5e583370fa58");
            var Q668;
            Q668=sQuery(id+"F0.wireOp",EDGE,"efa148f8-8aca-42a6-8d3d-da637cc82507");
            var Q669;
            Q669=sQuery(id+"F0.wireOp",EDGE,"f7238a60-9bde-49b1-ade9-4180079dd791");
            var Q670;
            Q670=sQuery(id+"F0.wireOp",EDGE,"311e5408-cea7-4fca-a049-98008501fad2");
            var Q671;
            Q671=sQuery(id+"F0.wireOp",EDGE,"c1b13eca-332d-416b-be97-51aeb1a362e7");
            var Q672;
            Q672=sQuery(id+"F0.wireOp",EDGE,"e8d8463e-5f04-4ca8-8d4c-c159ca3f31a6");
            var Q673;
            Q673=sQuery(id+"F0.wireOp",EDGE,"5292e5b5-bb77-4913-a41d-ea10ee014a1b");
            var Q674;
            Q674=sQuery(id+"F0.wireOp",EDGE,"0bb4ca49-d77f-44b6-9c36-6f47d451a1be");
            var Q675;
            Q675=sQuery(id+"F0.wireOp",EDGE,"06d8f846-92dd-4563-96d6-7eafd8a5937c");
            var Q676;
            Q676=sQuery(id+"F0.wireOp",EDGE,"cd0f66f0-4e41-4b21-966b-f565684014fa");
            var Q677;
            Q677=sQuery(id+"F0.wireOp",EDGE,"1b611731-55dd-4043-ad9d-452ab17e9a20");
            var Q678;
            Q678=sQuery(id+"F0.wireOp",EDGE,"57c24580-c717-4581-acb2-30b4585170ab");
            var Q679;
            Q679=sQuery(id+"F0.wireOp",EDGE,"9bf0b0a8-5262-4bbf-b80b-50c4ca2ea9f0");
            var Q680;
            Q680=sQuery(id+"F0.wireOp",EDGE,"226cf30a-d0a4-4ec3-8636-f6162329ddcd");
            var Q681;
            Q681=sQuery(id+"F0.wireOp",EDGE,"b85b1105-5acd-4632-895f-2712e3fb322e");
            var Q682;
            Q682=sQuery(id+"F0.wireOp",EDGE,"fc0db943-9038-40d9-89f2-1afcfac8191e");
            var Q683;
            Q683=sQuery(id+"F0.wireOp",EDGE,"9b373def-923f-4348-85cc-fb43396c4524");
            var Q684;
            Q684=sQuery(id+"F0.wireOp",EDGE,"9ee26cc4-fe8e-4f4e-8cf7-0e79c606c3a5");
            var Q685;
            Q685=sQuery(id+"F0.wireOp",EDGE,"df624a78-3d71-4c81-a83b-da52893e6b0d");
            var Q686;
            Q686=sQuery(id+"F0.wireOp",EDGE,"b8bd13b7-d83e-475a-9ff7-bba6e4acbb8f");
            var Q687;
            Q687=sQuery(id+"F0.wireOp",EDGE,"b89d7bb5-f3cb-4933-8963-d5e8f3aa5431");
            var Q688;
            Q688=sQuery(id+"F0.wireOp",EDGE,"e06c8f76-5625-4037-95cc-8e0e65b340a1");
            var Q689;
            Q689=sQuery(id+"F0.wireOp",EDGE,"cd3095be-be4c-46c0-a84a-79adabe1d73f");
            var Q690;
            Q690=sQuery(id+"F0.wireOp",EDGE,"2ca78408-307a-4863-84bc-f9818ede4e70");
            var Q691;
            Q691=sQuery(id+"F0.wireOp",EDGE,"5567731b-642d-42ef-a54e-4861b8a4a20d");
            var Q692;
            Q692=sQuery(id+"F0.wireOp",EDGE,"729c0272-55ac-422c-929b-7b3af7abc181");
            var Q693;
            Q693=sQuery(id+"F0.wireOp",EDGE,"e2463ec5-fa7c-4206-a09e-7a3936556a3a");
            var Q694;
            Q694=sQuery(id+"F0.wireOp",EDGE,"e14994cb-e903-4d3b-b954-48760b318a61");
            var Q695;
            Q695=sQuery(id+"F0.wireOp",EDGE,"e4ce63aa-ac44-4f16-abac-07405d582644");
            var Q696;
            Q696=sQuery(id+"F0.wireOp",EDGE,"aae2f22f-a07b-4ea0-99fd-679a5c293e7a");
            var Q697;
            Q697=sQuery(id+"F0.wireOp",EDGE,"f4c61589-1cb5-4436-aa51-28191e1ffffa");
            var Q698;
            Q698=sQuery(id+"F0.wireOp",EDGE,"a0eb9cf2-1607-44af-87a7-f27bf55caf81");
            var Q699;
            Q699=sQuery(id+"F0.wireOp",EDGE,"e4c2bfc7-b407-45df-abba-b9e042676afa");
            var Q700;
            Q700=sQuery(id+"F0.wireOp",EDGE,"bbe158af-7f57-4207-9782-d01310131e80");
            var Q701;
            Q701=sQuery(id+"F0.wireOp",EDGE,"340c1193-b1c2-48c4-865b-fc9d4b76d97f");
            var Q702;
            Q702=sQuery(id+"F0.wireOp",EDGE,"abd8d8d2-8b21-4b26-b005-21dc4b81d400");
            var Q703;
            Q703=sQuery(id+"F0.wireOp",EDGE,"35129d01-d080-4bf4-b886-85a2631e98de");
            var Q704;
            Q704=sQuery(id+"F0.wireOp",EDGE,"42febb35-8373-42ca-bc17-7c85a0564869");
            var Q705;
            Q705=sQuery(id+"F0.wireOp",EDGE,"e08b37a7-31fd-4895-9d8c-2ce173918687");
            var Q706;
            Q706=sQuery(id+"F0.wireOp",EDGE,"aeda04ce-0bdd-4c4c-92f0-9acc6ccff554");
            var Q707;
            Q707=sQuery(id+"F0.wireOp",EDGE,"d6638ce8-91d2-46bd-9fc3-9dcf9c837180");
            var Q708;
            Q708=sQuery(id+"F0.wireOp",EDGE,"251d6a62-db51-4eee-8992-fa460e00b8a3");
            var Q709;
            Q709=sQuery(id+"F0.wireOp",EDGE,"222550cb-db48-41a6-b466-c9af710a6f54");
            var Q710;
            Q710=sQuery(id+"F0.wireOp",EDGE,"735fce0c-e352-430b-8758-3db0c075c388");
            var Q711;
            Q711=sQuery(id+"F0.wireOp",EDGE,"99234a4f-b74b-460f-bd5c-0514b8367f6f");
            var Q712;
            Q712=sQuery(id+"F0.wireOp",EDGE,"5a44ae7a-0084-4e65-bff7-b1215f231a92");
            var Q713;
            Q713=sQuery(id+"F0.wireOp",EDGE,"8759d1c1-9ac5-4211-a62f-1db118e82b32");
            var Q714;
            Q714=sQuery(id+"F0.wireOp",EDGE,"02a916d0-98d8-4b0a-8be8-4a67c01843ae");
            var Q715;
            Q715=sQuery(id+"F0.wireOp",EDGE,"e9edff3e-9b80-45ea-8aaf-1a4a32fe47b6");
            var Q716;
            Q716=sQuery(id+"F0.wireOp",EDGE,"50322658-9eeb-4056-982e-394fb90bf338");
            var Q717;
            Q717=sQuery(id+"F0.wireOp",EDGE,"34aa46f2-652d-4168-80c6-0e9b2dfb3b22");
            var Q718;
            Q718=sQuery(id+"F0.wireOp",EDGE,"a5d728eb-a79d-44d9-9ac9-4ccf26485cf8");
            var Q719;
            Q719=sQuery(id+"F0.wireOp",EDGE,"9ddbccd6-80d5-4876-a3c0-dbff6beb1f53");
            var Q720;
            Q720=sQuery(id+"F0.wireOp",EDGE,"0eb5ab9f-1cf2-4dfc-97d4-fc72e92d64a3");
            var Q721;
            Q721=sQuery(id+"F0.wireOp",EDGE,"debe28b8-ca08-48cd-9b4a-3cfc9c97b736");
            var Q722;
            Q722=sQuery(id+"F0.wireOp",EDGE,"d267cb5e-d153-4ffc-9058-7eecde02ccb8");
            var Q723;
            Q723=sQuery(id+"F0.wireOp",EDGE,"96d27abd-8152-4345-8229-2c7a6eaff5af");
            var Q724;
            Q724=sQuery(id+"F0.wireOp",EDGE,"67a6a5a0-26ba-440e-a442-c24cfcc8722f");
            var Q725;
            Q725=sQuery(id+"F0.wireOp",EDGE,"897c5cca-b143-4e84-9cd2-e5dcc48e48b5");
            var Q726;
            Q726=sQuery(id+"F0.wireOp",EDGE,"b8bf9860-d705-460e-92f0-94c86af85ba8");
            var Q727;
            Q727=sQuery(id+"F0.wireOp",EDGE,"a69441dc-1f05-4068-bee5-564ce2922a6d");
            var Q728;
            Q728=sQuery(id+"F0.wireOp",EDGE,"5b99408f-31a4-4173-8585-3a513215cec4");
            var Q729;
            Q729=sQuery(id+"F0.wireOp",EDGE,"69da18e0-97b6-490b-a1a1-77733fd36deb");
            var Q730;
            Q730=sQuery(id+"F0.wireOp",EDGE,"e8d526e7-d7c3-4f10-8312-83fb277069bc");
            var Q731;
            Q731=sQuery(id+"F0.wireOp",EDGE,"3b53011b-3b67-43c3-970f-a2fb59fb3ca5");
            var Q732;
            Q732=sQuery(id+"F0.wireOp",EDGE,"e21fd06e-f471-4738-a0c6-865f961e2279");
            var Q733;
            Q733=sQuery(id+"F0.wireOp",EDGE,"880b4647-3b07-4951-9f75-78c131395aad");
            var Q734;
            Q734=sQuery(id+"F0.wireOp",EDGE,"41b0f430-635b-4569-84e7-47ec56fff732");
            var Q735;
            Q735=sQuery(id+"F0.wireOp",EDGE,"74f253cc-d814-4dd1-88ea-f652fa7e791f");
            var Q736;
            Q736=sQuery(id+"F0.wireOp",EDGE,"2b9f1373-ab85-467a-b472-878114948614");
            var Q737;
            Q737=sQuery(id+"F0.wireOp",EDGE,"7436747e-654c-4e90-83bd-b577ded190b0");
            var Q738;
            Q738=sQuery(id+"F0.wireOp",EDGE,"baa580ad-85ef-4920-9f18-924d39b909cc");
            var Q739;
            Q739=sQuery(id+"F0.wireOp",EDGE,"ce3a7348-776f-430f-b8f4-779d794a24ab");
            var Q740;
            Q740=sQuery(id+"F0.wireOp",EDGE,"06811bbc-6825-4580-8389-b50546dc544a");
            var Q741;
            Q741=sQuery(id+"F0.wireOp",EDGE,"90ee5fc9-1e35-4faa-afec-ff267c70eb66");
            var Q742;
            Q742=sQuery(id+"F0.wireOp",EDGE,"02d1a0cd-6c60-482f-8f17-5dd19e3e96a3");
            var Q743;
            Q743=sQuery(id+"F0.wireOp",EDGE,"5747ed7d-5786-4e18-ae47-b194d449f038");
            var Q744;
            Q744=sQuery(id+"F0.wireOp",EDGE,"c4801ceb-49a4-421c-9437-dfebd272cfa7");
            var Q745;
            Q745=sQuery(id+"F0.wireOp",EDGE,"7348a5be-0336-4eea-bc10-347736d79777");
            var Q746;
            Q746=sQuery(id+"F0.wireOp",EDGE,"d658e318-1e85-4595-b481-46d43ca667ec");
            var Q747;
            Q747=sQuery(id+"F0.wireOp",EDGE,"a7e62d7b-5aec-4093-9c3b-d031f728ac86");
            var Q748;
            Q748=sQuery(id+"F0.wireOp",EDGE,"b4b13375-3f8d-47b6-83fc-1c0937fdb1d4");
            var Q749;
            Q749=sQuery(id+"F0.wireOp",EDGE,"202c07ad-b2e6-44b8-bddb-6ea2652ce024");
            var Q750;
            Q750=sQuery(id+"F0.wireOp",EDGE,"53855dd5-440c-471c-9344-0973f3dc2bb3");
            var Q751;
            Q751=sQuery(id+"F0.wireOp",EDGE,"257ab787-cddb-4bcf-a75b-043875771d41");
            var Q752;
            Q752=sQuery(id+"F0.wireOp",EDGE,"d8d1f9b7-e7ad-4a7f-8bc1-7e334b32de9c");
            var Q753;
            Q753=sQuery(id+"F0.wireOp",EDGE,"21e7995e-3f52-4b82-93c9-e17c0f4c5fdc");
            var Q754;
            Q754=sQuery(id+"F0.wireOp",EDGE,"bff4f46c-3409-4f01-848b-024baf62d644");
            var Q755;
            Q755=sQuery(id+"F0.wireOp",EDGE,"2952bb6b-bfd4-453b-bbb3-c7203a38b1d7");
            var Q756;
            Q756=sQuery(id+"F0.wireOp",EDGE,"634a8e3e-ab4b-4ea1-bb9e-67166c89d6f9");
            var Q757;
            Q757=sQuery(id+"F0.wireOp",EDGE,"9d672fb0-5c25-4942-9c3f-16023faf327e");
            var Q758;
            Q758=sQuery(id+"F0.wireOp",EDGE,"7d17ef5f-c962-43ed-a0ba-dfb16b3c8dd4");
            var Q759;
            Q759=sQuery(id+"F0.wireOp",EDGE,"b24c74f7-8d65-4f66-bb17-dd68f6322bc2");
            var Q760;
            Q760=sQuery(id+"F0.wireOp",EDGE,"8ce39a8e-5b7b-46fc-b332-44d3ea07d37c");
            var Q761;
            Q761=sQuery(id+"F0.wireOp",EDGE,"d565f671-80ff-4b39-bf5b-72ab2749ae4d");
            var Q762;
            Q762=sQuery(id+"F0.wireOp",EDGE,"d805ff01-bbd8-42d7-b613-f9d7df3e8b85");
            var Q763;
            Q763=sQuery(id+"F0.wireOp",EDGE,"e75a1734-f028-4b34-9f56-fb74f97d7ab2");
            var Q764;
            Q764=sQuery(id+"F0.wireOp",EDGE,"3476e810-4ac1-4af2-9f57-002eaeea9d06");
            var Q765;
            Q765=sQuery(id+"F0.wireOp",EDGE,"ad49505c-9e3a-4a1f-a342-68fff1199af9");
            var Q766;
            Q766=sQuery(id+"F0.wireOp",EDGE,"e080b694-193a-470b-b925-42e13d719b36");
            var Q767;
            Q767=sQuery(id+"F0.wireOp",EDGE,"d89b075e-9e9d-4556-9c37-28c9466dbd76");
            var Q768;
            Q768=sQuery(id+"F0.wireOp",EDGE,"e1a3e1f9-1928-4f4b-9536-204b1bd74e0a");
            var Q769;
            Q769=sQuery(id+"F0.wireOp",EDGE,"cd24a8db-39fa-4839-bf11-ccff41dc2465");
            var Q770;
            Q770=sQuery(id+"F0.wireOp",EDGE,"772a54c5-8d7d-45ba-b680-42332558546f");
            var Q771;
            Q771=sQuery(id+"F0.wireOp",EDGE,"4c82d0d3-d915-4ac8-a273-9e3578faac7c");
            var Q772;
            Q772=sQuery(id+"F0.wireOp",EDGE,"9142770e-0295-4ed7-94a0-ac8b076bd50c");
            var Q773;
            Q773=sQuery(id+"F0.wireOp",EDGE,"8f3f7d3e-235f-4c9e-aa88-1f4628c58b1e");
            var Q774;
            Q774=sQuery(id+"F0.wireOp",EDGE,"3da8a89b-ec1f-4762-9ea0-a2d1640b6e92");
            var Q775;
            Q775=sQuery(id+"F0.wireOp",EDGE,"1e451767-9be8-4678-8ed7-d32693b0bdde");
            var Q776;
            Q776=sQuery(id+"F0.wireOp",EDGE,"6b3e79aa-1946-4b4c-aa5f-24c94313cb37");
            var Q777;
            Q777=sQuery(id+"F0.wireOp",EDGE,"9dd96c5e-2ef4-44f0-a52e-8b0be1f35b6a");
            var Q778;
            Q778=sQuery(id+"F0.wireOp",EDGE,"2f3aaa11-2c6d-4c46-aae2-ffa2eafbc8c1");
            var Q779;
            Q779=sQuery(id+"F0.wireOp",EDGE,"49ea14ce-09e5-4c5d-99b9-31a918571c5e");
            var Q780;
            Q780=sQuery(id+"F0.wireOp",EDGE,"61d0c1f4-0913-4959-82a2-654e3dff0660");
            var Q781;
            Q781=sQuery(id+"F0.wireOp",EDGE,"057c3b44-407f-403f-a825-a579b6651f36");
            var Q782;
            Q782=sQuery(id+"F0.wireOp",EDGE,"9534ffc5-e28c-4467-8a69-6a67467a701b");
            var Q783;
            Q783=sQuery(id+"F0.wireOp",EDGE,"93ae1f92-21f2-4cf5-abcf-5db9da00690d");
            var Q784;
            Q784=sQuery(id+"F0.wireOp",EDGE,"417154ca-3473-44b2-a0e4-7ec8a0ac1bf4");
            var Q785;
            Q785=sQuery(id+"F0.wireOp",EDGE,"9fdcd7ee-9d91-4a37-92e6-69cec5b8d672");
            var Q786;
            Q786=sQuery(id+"F0.wireOp",EDGE,"aa6c851d-948c-4890-9a14-6390a23b98d2");
            var Q787;
            Q787=sQuery(id+"F0.wireOp",EDGE,"4786a75a-282b-46a9-bea1-a7ef4d6e0756");
            var Q788;
            Q788=sQuery(id+"F0.wireOp",EDGE,"eb1264ef-7877-4e85-b601-97ff90499d1f");
            var Q789;
            Q789=sQuery(id+"F0.wireOp",EDGE,"6822c7b1-5af5-46c6-a6c5-06955a0357c3");
            var Q790;
            Q790=sQuery(id+"F0.wireOp",EDGE,"3a1fd319-b879-4662-9d37-db8915be39cb");
            var Q791;
            Q791=sQuery(id+"F0.wireOp",EDGE,"c03e5701-030c-475d-88bf-5ead03cc0fa1");
            var Q792;
            Q792=sQuery(id+"F0.wireOp",EDGE,"c70e4dab-423d-4330-b75a-4a766c04f351");
            var Q793;
            Q793=sQuery(id+"F0.wireOp",EDGE,"f4a7e75a-cc89-4bc0-8328-b2c46d1ff2da");
            var Q794;
            Q794=sQuery(id+"F0.wireOp",EDGE,"2f77f550-79e5-4f26-87fb-62d1b65a8e48");
            var Q795;
            Q795=sQuery(id+"F0.wireOp",EDGE,"437087ae-fb99-4fb3-aef7-8eaaf5367870");
            var Q796;
            Q796=sQuery(id+"F0.wireOp",EDGE,"193564c7-9e5a-41ca-b7d7-bf653a617aa3");
            var Q797;
            Q797=sQuery(id+"F0.wireOp",EDGE,"91ed608d-ec40-45a4-908b-0f1183838e25");
            var Q798;
            Q798=sQuery(id+"F0.wireOp",EDGE,"7da0fa1c-8432-4272-9ebe-5d6aa7ec74e0");
            var Q799;
            Q799=sQuery(id+"F0.wireOp",EDGE,"07d8525b-7626-4dbe-b82b-321c1944b6ac");
            var Q800;
            Q800=sQuery(id+"F0.wireOp",EDGE,"c2122313-4500-44fd-8279-5494d393b25e");
            var Q801;
            Q801=sQuery(id+"F0.wireOp",EDGE,"4f358088-c30e-44a0-b999-82cf4317c004");
            var Q802;
            Q802=sQuery(id+"F0.wireOp",EDGE,"13670792-c99b-4a03-9481-5fcd7dc7d4fc");
            var Q803;
            Q803=sQuery(id+"F0.wireOp",EDGE,"7406ddc7-9e25-42c4-a74a-d1166690fd50");
            var Q804;
            Q804=sQuery(id+"F0.wireOp",EDGE,"cb4211a0-f684-4573-b8a4-35ecf09375f8");
            var Q805;
            Q805=sQuery(id+"F0.wireOp",EDGE,"77174881-e2e4-4bef-aa9d-2b9dcfa8b299");
            var Q806;
            Q806=sQuery(id+"F0.wireOp",EDGE,"a0e3bd67-c979-481b-bcfd-08f6c13fcb7c");
            var Q807;
            Q807=sQuery(id+"F0.wireOp",EDGE,"b0c4f9bb-386a-488a-b771-fbe7527e506e");
            var Q808;
            Q808=sQuery(id+"F0.wireOp",EDGE,"df14c01c-2968-4a4a-ac2a-0a508eb7327c");
            var Q809;
            Q809=sQuery(id+"F0.wireOp",EDGE,"8102b00d-96b4-4ff0-a262-3b35a71b73a7");
            var Q810;
            Q810=sQuery(id+"F0.wireOp",EDGE,"14e8810b-2680-44d6-9de5-40ba95295c95");
            var Q811;
            Q811=sQuery(id+"F0.wireOp",EDGE,"4c22e5a8-95f4-44dc-b3e8-ba4919168179");
            var Q812;
            Q812=sQuery(id+"F0.wireOp",EDGE,"086f73a6-401f-46f1-8d39-a1fed06c1433");
            var Q813;
            Q813=sQuery(id+"F0.wireOp",EDGE,"eb62652e-8a61-4aeb-b817-81e56e48e244");
            var Q814;
            Q814=sQuery(id+"F0.wireOp",EDGE,"05282f7e-daf2-403b-a30e-dbe0cbb22f51");
            var Q815;
            Q815=sQuery(id+"F0.wireOp",EDGE,"d635ea92-4c76-4a8e-b72a-8a1c7608a63a");
            var Q816;
            Q816=sQuery(id+"F0.wireOp",EDGE,"c0d9b3bb-eb6f-4b00-9346-f2e181403b94");
            var Q817;
            Q817=sQuery(id+"F0.wireOp",EDGE,"3061c564-c0e3-4ce3-acae-5d47ba0cdf73");
            var Q818;
            Q818=sQuery(id+"F0.wireOp",EDGE,"b87304c6-d165-41e3-9f88-c8a25900eac9");
            var Q819;
            Q819=sQuery(id+"F0.wireOp",EDGE,"f56e819d-0814-42fa-954b-c6bd523b28e1");
            var Q820;
            Q820=sQuery(id+"F0.wireOp",EDGE,"fd8779c1-49fc-498d-a816-382fd1b28c5a");
            var Q821;
            Q821=sQuery(id+"F0.wireOp",EDGE,"6e124a58-80b7-4ed3-8f30-eadf2c8dff87");
            var Q822;
            Q822=sQuery(id+"F0.wireOp",EDGE,"369e6bfc-8ecb-45e5-8b06-137c3c1a0c7f");
            var Q823;
            Q823=sQuery(id+"F0.wireOp",EDGE,"2dcda2a0-6263-401b-bbca-813dd3399492");
            var Q824;
            Q824=sQuery(id+"F0.wireOp",EDGE,"0183eb4c-f5b2-44e5-8e0d-18ebc51096dc");
            var Q825;
            Q825=sQuery(id+"F0.wireOp",EDGE,"e992fa22-950c-430e-ba71-5dcfa8f7b3b0");
            var Q826;
            Q826=sQuery(id+"F0.wireOp",EDGE,"fa4c3aca-4691-42e6-8572-12edd329cedd");
            var Q827;
            Q827=sQuery(id+"F0.wireOp",EDGE,"0fdf2d11-86fa-49b8-b206-466234cd4c35");
            var Q828;
            Q828=sQuery(id+"F0.wireOp",EDGE,"802ab94d-8bcc-4a0e-a5bc-ec864cb48968");
            var Q829;
            Q829=sQuery(id+"F0.wireOp",EDGE,"3e360326-ef52-4997-bfde-309fb277042d");
            var Q830;
            Q830=sQuery(id+"F0.wireOp",EDGE,"eadcaa6b-de26-4625-b697-b36df8bd00ea");
            var Q831;
            Q831=sQuery(id+"F0.wireOp",EDGE,"c4a22567-dace-4290-a05b-6ac26ac5b565");
            var Q832;
            Q832=sQuery(id+"F0.wireOp",EDGE,"09c71ff1-5739-41f6-b56d-8427e50dd049");
            var Q833;
            Q833=sQuery(id+"F0.wireOp",EDGE,"07db4bd0-faaa-488b-8ac0-87e10012eb18");
            var Q834;
            Q834=sQuery(id+"F0.wireOp",EDGE,"11c8cb92-442d-4312-a44d-2929e2528cbc");
            var Q835;
            Q835=sQuery(id+"F0.wireOp",EDGE,"7c6ea435-cdc7-410d-bcd3-342a445d8b51");
            var Q836;
            Q836=sQuery(id+"F0.wireOp",EDGE,"76bcbc71-20f2-4ba1-b04a-0ad05bc70df2");
            var Q837;
            Q837=sQuery(id+"F0.wireOp",EDGE,"6d918b5c-f8b3-49c7-b019-1643fb23b1ec");
            var Q838;
            Q838=sQuery(id+"F0.wireOp",EDGE,"d7190486-2c6f-4968-a495-584e16aa84cd");
            var Q839;
            Q839=sQuery(id+"F0.wireOp",EDGE,"b222357e-4283-4408-b75d-9cf7ed0ce8b4");
            var Q840;
            Q840=sQuery(id+"F0.wireOp",EDGE,"3fc31a60-5e89-4bc2-85ce-8eeb57782117");
            var Q841;
            Q841=sQuery(id+"F0.wireOp",EDGE,"cdac3c3f-b36c-4aa0-9199-89ba1f75d2c4");
            var Q842;
            Q842=sQuery(id+"F0.wireOp",EDGE,"d778532b-bbda-4fcc-a3fd-0c4ef590cf41");
            var Q843;
            Q843=sQuery(id+"F0.wireOp",EDGE,"9f1d1a60-85e0-4438-82f9-5a0d614e20d6");
            var Q844;
            Q844=sQuery(id+"F0.wireOp",EDGE,"d3c200a1-4914-40bd-a2a8-71f4f7771fd6");
            var Q845;
            Q845=sQuery(id+"F0.wireOp",EDGE,"bd776398-6bac-42fe-97a2-fb56642ce401");
            var Q846;
            Q846=sQuery(id+"F0.wireOp",EDGE,"fde6ecc8-2b25-43b4-bdf1-66342b015add");
            var Q847;
            Q847=sQuery(id+"F0.wireOp",EDGE,"08008c52-8f49-4895-a748-1d60fc9a25c0");
            var Q848;
            Q848=sQuery(id+"F0.wireOp",EDGE,"ea5b050c-cf05-461b-baa5-9117121ac44a");
            var Q849;
            Q849=sQuery(id+"F0.wireOp",EDGE,"938acc73-85a4-493b-beca-8bb3598a83f3");
            var Q850;
            Q850=sQuery(id+"F0.wireOp",EDGE,"9d52bf1e-d39f-4ac9-8f87-507c219bcf6a");
            var Q851;
            Q851=sQuery(id+"F0.wireOp",EDGE,"bdc0a33a-30ea-465c-8579-f6d1ec919950");
            var Q852;
            Q852=sQuery(id+"F0.wireOp",EDGE,"4ce52613-d7d0-4439-9e0e-eb236dbcc1aa");
            var Q853;
            Q853=sQuery(id+"F0.wireOp",EDGE,"e853f3d7-acd3-4dc3-b0aa-565a380bc805");
            var Q854;
            Q854=sQuery(id+"F0.wireOp",EDGE,"1ae42f27-525a-4e3a-9f3d-ae80482e26ab");
            var Q855;
            Q855=sQuery(id+"F0.wireOp",EDGE,"12c2bfe5-bb8a-430d-a615-62faa06a54ec");
            var Q856;
            Q856=sQuery(id+"F0.wireOp",EDGE,"9596e904-190e-44bb-b799-c993962e8d7e");
            var Q857;
            Q857=sQuery(id+"F0.wireOp",EDGE,"4a0e91df-b252-4c07-903c-c52701e54093");
            var Q858;
            Q858=sQuery(id+"F0.wireOp",EDGE,"a08ac752-1d9e-4f53-8ec7-3a4fee179455");
            var Q859;
            Q859=sQuery(id+"F0.wireOp",EDGE,"dd1a0723-989b-477c-9a02-c6a6404ce35b");
            var Q860;
            Q860=sQuery(id+"F0.wireOp",EDGE,"b77f4a8c-486e-4d72-9358-c7d6692adeb8");
            var Q861;
            Q861=sQuery(id+"F0.wireOp",EDGE,"27d0cbcf-c1e9-4f43-806b-68d39af2e1d5");
            var Q862;
            Q862=sQuery(id+"F0.wireOp",EDGE,"e27bac2c-f9f8-4732-a6e9-2147836dbdb7");
            var Q863;
            Q863=sQuery(id+"F0.wireOp",EDGE,"6aec3e99-1649-4000-9545-56e3970c028e");
            var Q864;
            Q864=sQuery(id+"F0.wireOp",EDGE,"55841520-56ab-44b5-a7b0-ae9c956d045a");
            var Q865;
            Q865=sQuery(id+"F0.wireOp",EDGE,"ddad436e-151d-48b2-9e02-8b69542f3084");
            var Q866;
            Q866=sQuery(id+"F0.wireOp",EDGE,"835f678f-aaea-4de8-846e-5673aea9ca8a");
            var Q867;
            Q867=sQuery(id+"F0.wireOp",EDGE,"a1d5522d-3733-471d-b068-7d4640761422");
            var Q868;
            Q868=sQuery(id+"F0.wireOp",EDGE,"3518fec4-f91d-4d28-92e9-66d1d8fc8c7f");
            var Q869;
            Q869=sQuery(id+"F0.wireOp",EDGE,"83d55ed8-964f-4c39-9ab9-25b0882568bc");
            var Q870;
            Q870=sQuery(id+"F0.wireOp",EDGE,"dc295c26-abfc-4930-986b-3bb05b63116f");
            var Q871;
            Q871=sQuery(id+"F0.wireOp",EDGE,"504bb1a5-ffea-4b46-8aa9-84ffabdf99ab");
            var Q872;
            Q872=sQuery(id+"F0.wireOp",EDGE,"14e8ccef-120e-4c10-934f-59e7b587bb35");
            var Q873;
            Q873=sQuery(id+"F0.wireOp",EDGE,"172775e6-6dd0-4e2c-a9c9-b7bf6390f6e4");
            var Q874;
            Q874=sQuery(id+"F0.wireOp",EDGE,"5d6552a4-a05e-4225-ad6b-dbb830685223");
            var Q875;
            Q875=sQuery(id+"F0.wireOp",EDGE,"1b9ae826-8f00-43d0-8d00-3182dbdb73a9");
            var Q876;
            Q876=sQuery(id+"F0.wireOp",EDGE,"ae4dc029-a93f-4c97-af0a-ccc95eb2dec8");
            var Q877;
            Q877=sQuery(id+"F0.wireOp",EDGE,"b9e0b52d-9e66-4f14-88c5-97e8f8a3f4c8");
            var Q878;
            Q878=sQuery(id+"F0.wireOp",EDGE,"b202c065-313f-438e-b9e5-6bd277acd6b2");
            var Q879;
            Q879=sQuery(id+"F0.wireOp",EDGE,"579cac38-ff4c-4ce8-ad14-41e4584b0c9f");
            var Q880;
            Q880=sQuery(id+"F0.wireOp",EDGE,"abfda4fc-d824-4d2d-8302-1ae38c937602");
            var Q881;
            Q881=sQuery(id+"F0.wireOp",EDGE,"68065df1-955c-4718-95e0-59614744a418");
            var Q882;
            Q882=sQuery(id+"F0.wireOp",EDGE,"7dab18d7-b52e-4072-bfc8-b6f215b17854");
            var Q883;
            Q883=sQuery(id+"F0.wireOp",EDGE,"1b99136e-5706-4396-8129-8e3faff911b6");
            var Q884;
            Q884=sQuery(id+"F0.wireOp",EDGE,"29af4db1-b64d-4847-9138-bc22175c349a");
            var Q885;
            Q885=sQuery(id+"F0.wireOp",EDGE,"5256ffee-bd82-4079-8bb6-d65009bc4236");
            var Q886;
            Q886=sQuery(id+"F0.wireOp",EDGE,"6ea7307d-edf7-420b-aca9-daf7cbab6c11");
            var Q887;
            Q887=sQuery(id+"F0.wireOp",EDGE,"f2fd89f4-f287-42b3-a7b0-ccb50b1178ae");
            var Q888;
            Q888=sQuery(id+"F0.wireOp",EDGE,"e3e27e84-e3fd-4247-b5b7-139f65a22036");
            var Q889;
            Q889=sQuery(id+"F0.wireOp",EDGE,"5097a2a0-34b8-498a-8871-6a7a9d6864c8");
            var Q890;
            Q890=sQuery(id+"F0.wireOp",EDGE,"1b5e061a-3331-4f93-a0da-47ed43d95ed0");
            var Q891;
            Q891=sQuery(id+"F0.wireOp",EDGE,"303e3c5a-a1b0-439b-a3a3-eb7fb9554a0e");
            var Q892;
            Q892=sQuery(id+"F0.wireOp",EDGE,"47dcfebf-5477-4dee-90a7-8ec24fc8fff1");
            var Q893;
            Q893=sQuery(id+"F0.wireOp",EDGE,"4b85f008-2a48-4e63-8c6d-36b3fe535191");
            var Q894;
            Q894=sQuery(id+"F0.wireOp",EDGE,"347afbe2-90a7-4b34-940f-bd1796b66b20");
            var Q895;
            Q895=sQuery(id+"F0.wireOp",EDGE,"eb70c946-9169-4a46-be62-2c6fa3ab6746");
            var Q896;
            Q896=sQuery(id+"F0.wireOp",EDGE,"223dfe85-ff61-4188-a2a4-00d81af6ef96");
            var Q897;
            Q897=sQuery(id+"F0.wireOp",EDGE,"a0d78c51-e080-4515-b9c5-c0b8f8517473");
            var Q898;
            Q898=sQuery(id+"F0.wireOp",EDGE,"b88b04b7-ca21-484f-a6e0-0006e1694c0c");
            var Q899;
            Q899=sQuery(id+"F0.wireOp",EDGE,"05dd9717-47c4-4280-8fed-50df043da697");
            var Q900;
            Q900=sQuery(id+"F0.wireOp",EDGE,"e5e46133-e9e2-4bf6-b89f-c307485c0fbc");
            var Q901;
            Q901=sQuery(id+"F0.wireOp",EDGE,"72d99d60-8d1a-465e-8f83-d400b46145c8");
            var Q902;
            Q902=sQuery(id+"F0.wireOp",EDGE,"b99243ad-eeb6-4975-8856-d586be2478c9");
            var Q903;
            Q903=sQuery(id+"F0.wireOp",EDGE,"9a4c2b49-cb2e-4891-9b3c-910ca107801b");
            var Q904;
            Q904=sQuery(id+"F0.wireOp",EDGE,"155e0260-1c4a-43b8-a4eb-306a9388df5c");
            var Q905;
            Q905=sQuery(id+"F0.wireOp",EDGE,"fd3dd7d6-6ad2-407a-a534-2127aff8d0f0");
            var Q906;
            Q906=sQuery(id+"F0.wireOp",EDGE,"f773f20a-2cac-4881-9a57-7e844c61e1e7");
            var Q907;
            Q907=sQuery(id+"F0.wireOp",EDGE,"48085bd0-833c-4cd7-874c-0338d8ec1657");
            var Q908;
            Q908=sQuery(id+"F0.wireOp",EDGE,"ffbede93-6f27-46d5-b76a-6918362fe5de");
            var Q909;
            Q909=sQuery(id+"F0.wireOp",EDGE,"75ef836c-45b9-4bdf-9362-8caf57bf3941");
            var Q910;
            Q910=sQuery(id+"F0.wireOp",EDGE,"11a2147f-4518-4252-925d-1740d862310d");
            var Q911;
            Q911=sQuery(id+"F0.wireOp",EDGE,"0ee9287c-cc14-4f3d-818b-42b7d5891d6b");
            var Q912;
            Q912=sQuery(id+"F0.wireOp",EDGE,"1bdb204c-100b-425f-9d58-1eff77a8c6d1");
            var Q913;
            Q913=sQuery(id+"F0.wireOp",EDGE,"54524200-bfe5-4cd3-94d2-cafcf8a15520");
            var Q914;
            Q914=sQuery(id+"F0.wireOp",EDGE,"89aa5ab1-b1c6-4154-a436-024078b014a5");
            var Q915;
            Q915=sQuery(id+"F0.wireOp",EDGE,"0ec86a60-4de7-478d-a0bb-b49855dee2e7");
            var Q916;
            Q916=sQuery(id+"F0.wireOp",EDGE,"44939771-1070-449b-9dab-063e74d481f1");
            var Q917;
            Q917=sQuery(id+"F0.wireOp",EDGE,"2bb32760-ef58-4530-be9e-c3ae3d8a2fb9");
            var Q918;
            Q918=sQuery(id+"F0.wireOp",EDGE,"daf5fd84-6378-4e78-a2a2-f4362cd766dc");
            var Q919;
            Q919=sQuery(id+"F0.wireOp",EDGE,"c3ecf6ef-51bf-4c79-b8c4-ff262e87b32c");
            var Q920;
            Q920=sQuery(id+"F0.wireOp",EDGE,"cbe18273-18b0-4a79-8c99-5c7d5c73ccd8");
            var Q921;
            Q921=sQuery(id+"F0.wireOp",EDGE,"132cb862-44b1-446d-8680-7d16ebf8d7be");
            var Q922;
            Q922=sQuery(id+"F0.wireOp",EDGE,"bc848eaa-3d20-4262-897f-a71abad378a7");
            var Q923;
            Q923=sQuery(id+"F0.wireOp",EDGE,"32acb3cf-ccb3-4008-b717-ffec0110e0b8");
            var Q924;
            Q924=sQuery(id+"F0.wireOp",EDGE,"6382525b-575e-4fce-a91d-b540763ded2b");
            var Q925;
            Q925=sQuery(id+"F0.wireOp",EDGE,"55e1cdc3-9d57-4e15-81f2-209cfcdeb2e7");
            var Q926;
            Q926=sQuery(id+"F0.wireOp",EDGE,"d0e8349a-bbe5-499e-bc9b-c1d7a5095728");
            var Q927;
            Q927=sQuery(id+"F0.wireOp",EDGE,"4df841a7-209e-4541-b097-e63c69f4f8ae");
            var Q928;
            Q928=sQuery(id+"F0.wireOp",EDGE,"84bc36b7-4234-4b52-ad52-5b46dfe7480c");
            var Q929;
            Q929=sQuery(id+"F0.wireOp",EDGE,"254d3c67-b4b1-42d9-9f4c-d365681c48c9");
            var Q930;
            Q930=sQuery(id+"F0.wireOp",EDGE,"274c5837-cb55-436d-b293-0bc8b2dabc67");
            var Q931;
            Q931=sQuery(id+"F0.wireOp",EDGE,"f80492ee-7263-43c3-ab9d-23ad5e5f0f31");
            var Q932;
            Q932=sQuery(id+"F0.wireOp",EDGE,"4085d993-f764-493d-9004-16d4de42415f");
            var Q933;
            Q933=sQuery(id+"F0.wireOp",EDGE,"5b5b6edb-1660-4d85-9e11-7394a8ad59ea");
            var Q934;
            Q934=sQuery(id+"F0.wireOp",EDGE,"b17d52bc-23fc-46d6-99e8-b0d60bc78212");
            var Q935;
            Q935=sQuery(id+"F0.wireOp",EDGE,"e66eb439-1120-4629-925f-7ac69db9e14d");
            var Q936;
            Q936=sQuery(id+"F0.wireOp",EDGE,"46fdd694-4c29-4264-a4ad-758b9768018e");
            var Q937;
            Q937=sQuery(id+"F0.wireOp",EDGE,"b47e7e93-160e-494c-9461-b882b5cb33a9");
            var Q938;
            Q938=sQuery(id+"F0.wireOp",EDGE,"1b6de5aa-39d1-4ded-a32a-fcfc6b2b900e");
            var Q939;
            Q939=sQuery(id+"F0.wireOp",EDGE,"e1dcebcb-6d96-48dd-8248-ea35ff958dff");
            var Q940;
            Q940=sQuery(id+"F0.wireOp",EDGE,"4920fe1d-a769-4a8e-a5ac-b75e77f3c4c6");
            var Q941;
            Q941=sQuery(id+"F0.wireOp",EDGE,"ac5c368e-ef49-4f73-b85b-9961d64d7cfe");
            var Q942;
            Q942=sQuery(id+"F0.wireOp",EDGE,"d30e69f4-0b12-4051-803e-aa9f4b125edb");
            var Q943;
            Q943=sQuery(id+"F0.wireOp",EDGE,"7716e2b7-5fd3-4875-9fb4-f02cb2762d3b");
            var Q944;
            Q944=sQuery(id+"F0.wireOp",EDGE,"6af57263-c4df-4bbf-8c67-e6765b095f38");
            var Q945;
            Q945=sQuery(id+"F0.wireOp",EDGE,"028fe349-cd13-459d-97bc-fe93001e460b");
            var Q946;
            Q946=sQuery(id+"F0.wireOp",EDGE,"ba8e49b5-234d-49f5-be7a-992c7fc4fc70");
            var Q947;
            Q947=sQuery(id+"F0.wireOp",EDGE,"2e844f66-ae3a-4530-8ceb-d691ab71dcbc");
            var Q948;
            Q948=sQuery(id+"F0.wireOp",EDGE,"b7b3c0ef-db75-4626-bdee-adbace52fdc0");
            var Q949;
            Q949=sQuery(id+"F0.wireOp",EDGE,"80f4750b-e128-4ac0-ad55-fa18cfcf0dae");
            var Q950;
            Q950=sQuery(id+"F0.wireOp",EDGE,"f1a0291a-b86a-4eae-b7bb-fbff17953a05");
            var Q951;
            Q951=sQuery(id+"F0.wireOp",EDGE,"afa3a927-6f42-4ac4-89f0-fc3d992f5c5e");
            var Q952;
            Q952=sQuery(id+"F0.wireOp",EDGE,"f4d75038-8674-41b3-a694-2560ce1b7b48");
            var Q953;
            Q953=sQuery(id+"F0.wireOp",EDGE,"76edd7aa-6c18-4232-9e21-e7d6e81b0bfd");
            var Q954;
            Q954=sQuery(id+"F0.wireOp",EDGE,"adf5897c-79a2-439e-be62-7361ffd1ec27");
            var Q955;
            Q955=sQuery(id+"F0.wireOp",EDGE,"6d808328-304d-4c4c-b21b-ce7bc57c713b");
            var Q956;
            Q956=sQuery(id+"F0.wireOp",EDGE,"6ab22c0c-482e-4e57-8435-ed1518e28ebf");
            var Q957;
            Q957=sQuery(id+"F0.wireOp",EDGE,"a59571a7-10ce-4f4f-8e2c-4e642970bec4");
            var Q958;
            Q958=sQuery(id+"F0.wireOp",EDGE,"3f33138d-926a-429f-8364-5b8737a1c165");
            var Q959;
            Q959=sQuery(id+"F0.wireOp",EDGE,"d0303319-ce9e-4283-933b-29030d9ba786");
            var Q960;
            Q960=sQuery(id+"F0.wireOp",EDGE,"d340115b-a70b-4063-9c02-e13206ebfae1");
            var Q961;
            Q961=sQuery(id+"F0.wireOp",EDGE,"71954e83-c50d-4f6b-b37d-789bfde0302b");
            var Q962;
            Q962=sQuery(id+"F0.wireOp",EDGE,"79244ad0-a9b8-4f82-aa8e-0a7800e8b5f6");
            var Q963;
            Q963=sQuery(id+"F0.wireOp",EDGE,"35513647-324b-4014-aa36-0b0603c4ac8b");
            var Q964;
            Q964=sQuery(id+"F0.wireOp",EDGE,"e1098d45-774e-44d8-8062-ebcbcf7f9512");
            var Q965;
            Q965=sQuery(id+"F0.wireOp",EDGE,"45be2a86-2ff0-4dac-b364-088f9bd616cb");
            var Q966;
            Q966=sQuery(id+"F0.wireOp",EDGE,"227cd2f9-7dfc-456b-8ac8-6ef0634f8f4a");
            var Q967;
            Q967=sQuery(id+"F0.wireOp",EDGE,"49a2b9a6-c327-4d9e-89ff-06334b33798a");
            var Q968;
            Q968=sQuery(id+"F0.wireOp",EDGE,"5c710c44-cad3-4f03-9227-c88fa3ee5111");
            var Q969;
            Q969=sQuery(id+"F0.wireOp",EDGE,"448a14d3-e18a-413f-8067-619737524f08");
            var Q970;
            Q970=sQuery(id+"F0.wireOp",EDGE,"3a85c37f-dc73-4e98-ad0c-c4e702d21e68");
            var Q971;
            Q971=sQuery(id+"F0.wireOp",EDGE,"2a1178ed-a608-44a8-9d3a-9dd4dde51da0");
            var Q972;
            Q972=sQuery(id+"F0.wireOp",EDGE,"f8d92773-1719-4cd7-a76b-6bf78601dbe5");
            var Q973;
            Q973=sQuery(id+"F0.wireOp",EDGE,"05c21447-3cd3-40af-83f0-5ce70e1185af");
            var Q974;
            Q974=sQuery(id+"F0.wireOp",EDGE,"b293e453-6d17-458f-a4e4-eacb2344a12e");
            var Q975;
            Q975=sQuery(id+"F0.wireOp",EDGE,"548a7f22-1de7-4ad7-95b9-9deb8c58a9ba");
            var Q976;
            Q976=sQuery(id+"F0.wireOp",EDGE,"57e4db6c-e036-4237-8a0b-e94a7544a9ba");
            var Q977;
            Q977=sQuery(id+"F0.wireOp",EDGE,"4c32724e-ff46-4208-b7b6-4d899307a6b6");
            var Q978;
            Q978=sQuery(id+"F0.wireOp",EDGE,"6649ad3c-5b20-4b54-bc9b-68c57c5d46f8");
            var Q979;
            Q979=sQuery(id+"F0.wireOp",EDGE,"c93f9a03-21eb-4e7b-bd13-4a8f5becfa56");
            var Q980;
            Q980=sQuery(id+"F0.wireOp",EDGE,"a9ec1c8f-78c5-40dd-ab1f-38b50984e3ff");
            var Q981;
            Q981=sQuery(id+"F0.wireOp",EDGE,"52b4b6a9-c0cd-42db-8ceb-64e9ea81fdc5");
            var Q982;
            Q982=sQuery(id+"F0.wireOp",EDGE,"5c1ee56c-785a-4bba-bddc-1e1a1a46a3d0");
            var Q983;
            Q983=sQuery(id+"F0.wireOp",EDGE,"243c777d-fad2-4fac-818d-ac560b5e444b");
            var Q984;
            Q984=sQuery(id+"F0.wireOp",EDGE,"74aff87b-4b94-4a75-b9cb-296353e3b94d");
            var Q985;
            Q985=sQuery(id+"F0.wireOp",EDGE,"d7c78873-2920-4892-939b-b99bd05b1374");
            var Q986;
            Q986=sQuery(id+"F0.wireOp",EDGE,"52673f27-dab4-414d-b60d-80e16cb947f4");
            var Q987;
            Q987=sQuery(id+"F0.wireOp",EDGE,"08652a25-580d-4673-9c96-66886550c4dd");
            var Q988;
            Q988=sQuery(id+"F0.wireOp",EDGE,"bd6668c7-6f85-474f-9496-3069bddceb6b");
            var Q989;
            Q989=sQuery(id+"F0.wireOp",EDGE,"6604d794-65d5-4c92-9beb-47e47b74adff");
            var Q990;
            Q990=sQuery(id+"F0.wireOp",EDGE,"ba0aa0ba-33ec-42d0-bd89-3c3e7a0db8ad");
            var Q991;
            Q991=sQuery(id+"F0.wireOp",EDGE,"a7b00356-adfd-48db-b358-2dc4db0ecbd1");
            var Q992;
            Q992=sQuery(id+"F0.wireOp",EDGE,"f9801f88-d7a3-4af3-95a6-24e11f376b93");
            var Q993;
            Q993=sQuery(id+"F0.wireOp",EDGE,"c9d7d1bf-3973-4b92-8076-4859449ee50d");
            var Q994;
            Q994=sQuery(id+"F0.wireOp",EDGE,"99ca1474-f2ed-4bec-9c9c-28ca5d079f96");
            var Q995;
            Q995=sQuery(id+"F0.wireOp",EDGE,"00da09ba-f72d-401e-bfef-7986a569acc8");
            var Q996;
            Q996=sQuery(id+"F0.wireOp",EDGE,"f1bab132-564f-4ad5-a0e8-1573b301a3ea");
            var Q997;
            Q997=sQuery(id+"F0.wireOp",EDGE,"8b22d92d-6395-49c5-b7f2-4e1963e62ef4");
            var Q998;
            Q998=sQuery(id+"F0.wireOp",EDGE,"ec9708bc-bfe3-489a-a2b8-eb4a69003021");
            var Q999;
            Q999=sQuery(id+"F0.wireOp",EDGE,"f4f6d3ec-48f4-4c7c-bfec-d66f2d79dc58");
            var Q1000;
            Q1000=sQuery(id+"F0.wireOp",EDGE,"ebc650b6-b261-43d7-9d0b-6ed3e4edc1a9");
            var Q1001;
            Q1001=sQuery(id+"F0.wireOp",EDGE,"a0c68073-7f39-45a7-b1cd-fc767d138604");
            var Q1002;
            Q1002=sQuery(id+"F0.wireOp",EDGE,"c8d940f1-cecc-45a0-aab4-e3d446f4c080");
            var Q1003;
            Q1003=sQuery(id+"F0.wireOp",EDGE,"0ee0fc05-e63f-45d5-8199-7f095926834f");
            var Q1004;
            Q1004=sQuery(id+"F0.wireOp",EDGE,"bca0b6e2-a9ea-4f6b-a8f6-5d336c7066f8");
            var Q1005;
            Q1005=sQuery(id+"F0.wireOp",EDGE,"009b3d2e-0471-42dd-9808-63f94bebc91f");
            var Q1006;
            Q1006=sQuery(id+"F0.wireOp",EDGE,"59abc83d-9e5f-4c82-b12c-064548dfeb76");
            var Q1007;
            Q1007=sQuery(id+"F0.wireOp",EDGE,"97c59922-9a04-42c0-bfce-5f8a37922ea1");
            var Q1008;
            Q1008=sQuery(id+"F0.wireOp",EDGE,"eff2f1af-df55-4069-96a2-0838fa162f26");
            var Q1009;
            Q1009=sQuery(id+"F0.wireOp",EDGE,"7b7f4c2e-908a-4680-a725-2c74147db3e8");
            var Q1010;
            Q1010=sQuery(id+"F0.wireOp",EDGE,"2f09803a-30ca-4d95-baed-535513cab2e1");
            var Q1011;
            Q1011=sQuery(id+"F0.wireOp",EDGE,"0e05cebd-572c-403f-8d48-e33d7245ecba");
            var Q1012;
            Q1012=sQuery(id+"F0.wireOp",EDGE,"5b3c3f88-b4ff-4f67-9a3e-d46dc4d6417d");
            var Q1013;
            Q1013=sQuery(id+"F0.wireOp",EDGE,"ef5fa1e6-1399-44ec-a936-86ade499e569");
            var Q1014;
            Q1014=sQuery(id+"F0.wireOp",EDGE,"2e29ab11-1d47-442a-9836-5a94e6d2b5e6");
            var Q1015;
            Q1015=sQuery(id+"F0.wireOp",EDGE,"e5fc8c69-0976-4999-9a00-67aebd010f6f");
            var Q1016;
            Q1016=sQuery(id+"F0.wireOp",EDGE,"050b2e82-91c9-47bf-b69a-837559905caa");
            var Q1017;
            Q1017=sQuery(id+"F0.wireOp",EDGE,"49e713a1-553a-4a5d-9ae7-bf33dc9ef8a6");
            var Q1018;
            Q1018=sQuery(id+"F0.wireOp",EDGE,"5e10302b-92a7-48e2-a978-f194f98b059d");
            var Q1019;
            Q1019=sQuery(id+"F0.wireOp",EDGE,"0d07fed5-9492-4eb5-87cc-afc4eaad4458");
            var Q1020;
            Q1020=sQuery(id+"F0.wireOp",EDGE,"e1692512-e64c-4704-827c-ef1aa13bba88");
            var Q1021;
            Q1021=sQuery(id+"F0.wireOp",EDGE,"ba93674f-e329-4712-9e33-68c9c4061ae4");
            var Q1022;
            Q1022=sQuery(id+"F0.wireOp",EDGE,"90eccd4e-0912-4681-9688-6ca44d1a1362");
            var Q1023;
            Q1023=sQuery(id+"F0.wireOp",EDGE,"65153d47-49b7-4cfb-b702-884575c2ef42");
            var Q1024;
            Q1024=sQuery(id+"F0.wireOp",EDGE,"e4f1ca4c-0cdc-43a3-8cae-bf91a390e4f4");
            var Q1025;
            Q1025=sQuery(id+"F0.wireOp",EDGE,"6bd71193-905e-46e6-8e85-a69f6d86f87d");
            var Q1026;
            Q1026=sQuery(id+"F0.wireOp",EDGE,"b9f74751-025f-4bf9-a5de-244f10448bf5");
            var Q1027;
            Q1027=sQuery(id+"F0.wireOp",EDGE,"34735a1b-d042-4be2-9ff9-a70ebb01d15e");
            var Q1028;
            Q1028=sQuery(id+"F0.wireOp",EDGE,"e0da971d-f223-491f-a18f-62cac78e5bbe");
            var Q1029;
            Q1029=sQuery(id+"F0.wireOp",EDGE,"ce46460d-5ef9-4216-8ed3-89b077274dcf");
            var Q1030;
            Q1030=sQuery(id+"F0.wireOp",EDGE,"e51011ac-a1af-4908-913c-a434551e6df3");
            var Q1031;
            Q1031=sQuery(id+"F0.wireOp",EDGE,"197abebf-3209-4599-919b-83a94cba4d3c");
            var Q1032;
            Q1032=sQuery(id+"F0.wireOp",EDGE,"3a122dd1-a515-4518-bccd-2d26f16dffef");
            var Q1033;
            Q1033=sQuery(id+"F0.wireOp",EDGE,"1b2e2ac6-f96f-42da-b875-2047f025e1b3");
            var Q1034;
            Q1034=sQuery(id+"F0.wireOp",EDGE,"38041900-2bd0-4c4b-92f3-146272199bbc");
            var Q1035;
            Q1035=sQuery(id+"F0.wireOp",EDGE,"08448a2f-6322-4266-ab05-10170deb88ff");
            var Q1036;
            Q1036=sQuery(id+"F0.wireOp",EDGE,"74eaab4b-7320-4d53-b183-0a45fbe34574");
            var Q1037;
            Q1037=sQuery(id+"F0.wireOp",EDGE,"219928f5-11a7-4bc7-968f-c78462b39764");
            var Q1038;
            Q1038=sQuery(id+"F0.wireOp",EDGE,"c3a493b8-ee77-4bb8-8edd-f7eea29801a4");
            var Q1039;
            Q1039=sQuery(id+"F0.wireOp",EDGE,"0ab337a5-9061-4566-9876-c73a8bc182d8");
            var Q1040;
            Q1040=sQuery(id+"F0.wireOp",EDGE,"415b98f3-b90b-4989-a49f-ecfb1e72843c");
            var Q1041;
            Q1041=sQuery(id+"F0.wireOp",EDGE,"54a3efee-35fe-4e18-a080-b3f3ec06979e");
            var Q1042;
            Q1042=sQuery(id+"F0.wireOp",EDGE,"694043fa-8aec-4014-a630-4c0441cf2c33");
            var Q1043;
            Q1043=sQuery(id+"F0.wireOp",EDGE,"25026b13-0f55-4bd0-b2b4-7e6d1dcea344");
            var Q1044;
            Q1044=sQuery(id+"F0.wireOp",EDGE,"0bfff023-6aa0-4df6-92ac-ff0a0637417b");
            var Q1045;
            Q1045=sQuery(id+"F0.wireOp",EDGE,"e710705c-52d9-4dcb-9c33-60915f28ec50");
            var Q1046;
            Q1046=sQuery(id+"F0.wireOp",EDGE,"05e86e09-c2e1-48be-a598-95b619a896c8");
            var Q1047;
            Q1047=sQuery(id+"F0.wireOp",EDGE,"d358e790-3062-45e4-894b-c806146fb7eb");
            var Q1048;
            Q1048=sQuery(id+"F0.wireOp",EDGE,"e855f203-9a9c-4f0d-b11b-1b02ad42f581");
            var Q1049;
            Q1049=sQuery(id+"F0.wireOp",EDGE,"d3bc881e-6fa5-4945-8e02-4ac7323c33a9");
            var Q1050;
            Q1050=sQuery(id+"F0.wireOp",EDGE,"bd1d07e4-f2c3-4257-b98a-1fe8c25ce89f");
            var Q1051;
            Q1051=sQuery(id+"F0.wireOp",EDGE,"196ed618-9c79-4127-9b4e-ce37c76f9b5d");
            var Q1052;
            Q1052=sQuery(id+"F0.wireOp",EDGE,"b9b91509-06f2-48c8-a7ed-8e7730225518");
            var Q1053;
            Q1053=sQuery(id+"F0.wireOp",EDGE,"08d34819-d6f5-4f96-aae6-1edd98793c84");
            var Q1054;
            Q1054=sQuery(id+"F0.wireOp",EDGE,"6ab55b0f-9c9a-42c2-a48b-50e1d3fda6f5");
            var Q1055;
            Q1055=sQuery(id+"F0.wireOp",EDGE,"4356c989-a37b-4ffb-9974-797a3a9cb262");
            var Q1056;
            Q1056=sQuery(id+"F0.wireOp",EDGE,"c1bbd3a0-1654-42fb-9faa-4e5eeb844bc6");
            var Q1057;
            Q1057=sQuery(id+"F0.wireOp",EDGE,"259d7614-0b8e-4dca-9ba4-9120f21d6022");
            var Q1058;
            Q1058=sQuery(id+"F0.wireOp",EDGE,"1141a8bf-5516-41a4-bc45-0f2496349041");
            var Q1059;
            Q1059=sQuery(id+"F0.wireOp",EDGE,"04a98c4f-76c0-427d-a665-ef5e75d28741");
            var Q1060;
            Q1060=sQuery(id+"F0.wireOp",EDGE,"682134fd-ac45-434b-93cc-1387d21aaae3");
            var Q1061;
            Q1061=sQuery(id+"F0.wireOp",EDGE,"2fde874d-65d4-4ae6-830e-f4572e7c2c97");
            var Q1062;
            Q1062=sQuery(id+"F0.wireOp",EDGE,"838e71f1-9c44-47e3-899c-2e5daf42cfca");
            var Q1063;
            Q1063=sQuery(id+"F0.wireOp",EDGE,"97056cec-9a6d-4ef4-aeb5-4474882ec37b");
            var Q1064;
            Q1064=sQuery(id+"F0.wireOp",EDGE,"6716076c-a46e-4f66-93b9-242b397b653d");
            var Q1065;
            Q1065=sQuery(id+"F0.wireOp",EDGE,"47609eb1-9b68-429c-b1ea-aab52ab99386");
            var Q1066;
            Q1066=sQuery(id+"F0.wireOp",EDGE,"5fd9940d-378c-4614-aaf8-b874fd7523ec");
            var Q1067;
            Q1067=sQuery(id+"F0.wireOp",EDGE,"bf292283-a1a9-4c80-b517-58602dafaa0f");
            var Q1068;
            Q1068=sQuery(id+"F0.wireOp",EDGE,"5c0b6e27-b23d-414a-865b-733c382fc8e2");
            var Q1069;
            Q1069=sQuery(id+"F0.wireOp",EDGE,"ec6d2cb2-e622-4412-a8cd-638989f1a37c");
            var Q1070;
            Q1070=sQuery(id+"F0.wireOp",EDGE,"35041fea-2462-4ced-beed-129a7502680f");
            var Q1071;
            Q1071=sQuery(id+"F0.wireOp",EDGE,"4e0cc6c1-5ebf-404a-8b60-a9f63f576265");
            var Q1072;
            Q1072=sQuery(id+"F0.wireOp",EDGE,"eadaf89f-5809-4921-9a62-cd5170ea4661");
            var Q1073;
            Q1073=sQuery(id+"F0.wireOp",EDGE,"5698ace3-9b74-4a9a-99cf-65beadf3a12d");
            var Q1074;
            Q1074=sQuery(id+"F0.wireOp",EDGE,"7a4aa2fb-a354-45f4-ae7a-9342f2eceaf7");
            var Q1075;
            Q1075=sQuery(id+"F0.wireOp",EDGE,"e20107cd-498c-403e-a726-bb047d4024d2");
            var Q1076;
            Q1076=sQuery(id+"F0.wireOp",EDGE,"ec4c1733-cbf9-4933-a14d-e8e0d494f3a1");
            var Q1077;
            Q1077=sQuery(id+"F0.wireOp",EDGE,"316ec333-7f05-4d00-a94d-7f25aa60e01a");
            var Q1078;
            Q1078=sQuery(id+"F0.wireOp",EDGE,"1fb4af65-8427-4ac8-a434-d22fce34d010");
            var Q1079;
            Q1079=sQuery(id+"F0.wireOp",EDGE,"f8244a1e-efac-48b0-8088-d6e075f21fdf");
            var Q1080;
            Q1080=sQuery(id+"F0.wireOp",EDGE,"9e2269d3-3da7-415b-9376-2c930d6c0179");
            var Q1081;
            Q1081=sQuery(id+"F0.wireOp",EDGE,"c3981f9e-c2ce-4d7e-ba95-00c60b4c1820");
            var Q1082;
            Q1082=sQuery(id+"F0.wireOp",EDGE,"b8545496-95ca-4d26-b128-c52f5355a3e5");
            var Q1083;
            Q1083=sQuery(id+"F0.wireOp",EDGE,"ad834bc8-ae2b-4a3b-bad0-5f34cf7ff902");
            var Q1084;
            Q1084=sQuery(id+"F0.wireOp",EDGE,"8619d683-48b6-432e-808c-9f69c727dc0f");
            var Q1085;
            Q1085=sQuery(id+"F0.wireOp",EDGE,"ccaa1d33-8eb0-4865-b1d5-b558e4c797b3");
            var Q1086;
            Q1086=sQuery(id+"F0.wireOp",EDGE,"3a05ea55-020e-4ddc-8b57-7ba9f4b38ccb");
            var Q1087;
            Q1087=sQuery(id+"F0.wireOp",EDGE,"8257f5a9-9aa4-42b8-8929-649cc9a6ff8d");
            var Q1088;
            Q1088=sQuery(id+"F0.wireOp",EDGE,"3e865b14-151e-4a54-a6fc-d913306efa25");
            var Q1089;
            Q1089=sQuery(id+"F0.wireOp",EDGE,"598d4b19-9d39-4bd5-a7a3-31b17455c69a");
            var Q1090;
            Q1090=sQuery(id+"F0.wireOp",EDGE,"8621c715-7127-4389-bf10-2227c32cd141");
            var Q1091;
            Q1091=sQuery(id+"F0.wireOp",EDGE,"c6eafcc6-6cbb-4fee-93c2-8bda7b47dca8");
            var Q1092;
            Q1092=sQuery(id+"F0.wireOp",EDGE,"dbffe688-6e2a-46fe-bac6-a82682de5bd4");
            var Q1093;
            Q1093=sQuery(id+"F0.wireOp",EDGE,"411c7282-ca2b-45fb-8c5b-ec3e75a44d57");
            var Q1094;
            Q1094=sQuery(id+"F0.wireOp",EDGE,"b1238417-c4a4-4235-aa77-f5cd219e3a7e");
            var Q1095;
            Q1095=sQuery(id+"F0.wireOp",EDGE,"1e60d794-21c3-40fe-b469-3c0f7658a7a0");
            var Q1096;
            Q1096=sQuery(id+"F0.wireOp",EDGE,"f1faccf2-1f23-49de-bb3e-6d9edb14d30d");
            var Q1097;
            Q1097=sQuery(id+"F0.wireOp",EDGE,"3121b46a-bc88-42a2-8ff9-92256f883f90");
            var Q1098;
            Q1098=sQuery(id+"F0.wireOp",EDGE,"d2b8b635-0829-4918-8dba-be84af4f0740");
            var Q1099;
            Q1099=sQuery(id+"F0.wireOp",EDGE,"2cbb68b1-a72d-4013-a73d-bce717a11d65");
            var Q1100;
            Q1100=sQuery(id+"F0.wireOp",EDGE,"0c484faf-4c65-4e0c-b996-4b34c81f5aae");
            var Q1101;
            Q1101=sQuery(id+"F0.wireOp",EDGE,"52f71b51-46a3-40ce-97c4-cff48ae2d395");
            var Q1102;
            Q1102=sQuery(id+"F0.wireOp",EDGE,"cffac8b0-f98c-4fd0-a6f8-67c6da0e99e7");
            var Q1103;
            Q1103=sQuery(id+"F0.wireOp",EDGE,"9cf4823f-af2d-442d-9603-2b31587c7a17");
            var Q1104;
            Q1104=sQuery(id+"F0.wireOp",EDGE,"716310cb-d7db-4843-aab6-433ebd4d88d6");
            var Q1105;
            Q1105=sQuery(id+"F0.wireOp",EDGE,"05810521-6a2a-4c44-b3bf-e87f2c540d8e");
            var Q1106;
            Q1106=sQuery(id+"F0.wireOp",EDGE,"e3fdf5ed-aaf0-4132-9160-284538a4149e");
            var Q1107;
            Q1107=sQuery(id+"F0.wireOp",EDGE,"92b7194f-b02d-4088-a83f-b98b00611b9e");
            var Q1108;
            Q1108=sQuery(id+"F0.wireOp",EDGE,"c7b4910d-6fb2-47c9-b3a0-96931070c927");
            var Q1109;
            Q1109=sQuery(id+"F0.wireOp",EDGE,"78e2e2dd-2871-44bd-9b89-27f7934f62eb");
            var Q1110;
            Q1110=sQuery(id+"F0.wireOp",EDGE,"2d3c3943-68f8-43aa-8e15-92af06e68089");
            var Q1111;
            Q1111=sQuery(id+"F0.wireOp",EDGE,"b2f7bb5b-8241-4106-b0f9-8053877428fd");
            var Q1112;
            Q1112=sQuery(id+"F0.wireOp",EDGE,"556b535e-ec3f-4e8c-8343-073b022fccd7");
            var Q1113;
            Q1113=sQuery(id+"F0.wireOp",EDGE,"5fe82fa1-175b-45c7-a429-ba98aca0f213");
            var Q1114;
            Q1114=sQuery(id+"F0.wireOp",EDGE,"a20dffe9-d5fd-468f-867b-6c2e894a8005");
            var Q1115;
            Q1115=sQuery(id+"F0.wireOp",EDGE,"d7d8adaa-a443-48ca-87b3-c79a268dd1f7");
            var Q1116;
            Q1116=sQuery(id+"F0.wireOp",EDGE,"23b5e249-ade0-4a62-a164-a366d180aa07");
            var Q1117;
            Q1117=sQuery(id+"F0.wireOp",EDGE,"b94d84d4-53a0-4e0e-9b1b-48c49bdfb704");
            var Q1118;
            Q1118=sQuery(id+"F0.wireOp",EDGE,"99eee4d2-dc67-4f77-9b09-f31150043b33");
            var Q1119;
            Q1119=sQuery(id+"F0.wireOp",EDGE,"7732e2d9-82f3-4394-9b65-b6fe6dc41935");
            var Q1120;
            Q1120=sQuery(id+"F0.wireOp",EDGE,"bb38c429-b087-4c97-9ce1-303c9dead0ba");
            var Q1121;
            Q1121=sQuery(id+"F0.wireOp",EDGE,"928131e9-6543-4add-9e10-23f6291758fe");
            var Q1122;
            Q1122=sQuery(id+"F0.wireOp",EDGE,"765f92d4-b780-4f32-a354-d3bb424c0477");
            var Q1123;
            Q1123=sQuery(id+"F0.wireOp",EDGE,"1c057560-05a0-4357-b9e3-23f323163e9e");
            var Q1124;
            Q1124=sQuery(id+"F0.wireOp",EDGE,"2be8615a-4a15-41cf-90e3-ce0568c77f5b");
            var Q1125;
            Q1125=sQuery(id+"F0.wireOp",EDGE,"a0227d0b-c769-4151-9eb1-6b5cc9e249e7");
            var Q1126;
            Q1126=sQuery(id+"F0.wireOp",EDGE,"51c3883c-3bbd-48f8-a2a8-4bc57761c999");
            var Q1127;
            Q1127=sQuery(id+"F0.wireOp",EDGE,"a59dacfd-fec4-46ed-8bd1-3e963ca4ecf6");
            var Q1128;
            Q1128=sQuery(id+"F0.wireOp",EDGE,"b5d1d2a0-bb75-4340-86d6-208a173fdcde");
            var Q1129;
            Q1129=sQuery(id+"F0.wireOp",EDGE,"124f2ced-dffd-458e-a397-5de7d8b814e6");
            var Q1130;
            Q1130=sQuery(id+"F0.wireOp",EDGE,"c517001c-0b46-4842-8ae1-d6a75cb9d4ea");
            var Q1131;
            Q1131=sQuery(id+"F0.wireOp",EDGE,"9ebe3044-1506-4b3d-be53-d8e519f2658a");
            var Q1132;
            Q1132=sQuery(id+"F0.wireOp",EDGE,"59280f95-60c5-407c-8289-ee9d89d31d6b");
            var Q1133;
            Q1133=sQuery(id+"F0.wireOp",EDGE,"1f12b4d4-c348-445b-8ec9-6f91645136ee");
            var Q1134;
            Q1134=sQuery(id+"F0.wireOp",EDGE,"0c846d6c-08a2-4cc1-aec5-88922fd04a6d");
            var Q1135;
            Q1135=sQuery(id+"F0.wireOp",EDGE,"521974a5-4b1c-47bc-88ac-79b6cf2170db");
            var Q1136;
            Q1136=sQuery(id+"F0.wireOp",EDGE,"0ff16c05-556d-44e1-b880-e459ecfa33eb");
            var Q1137;
            Q1137=sQuery(id+"F0.wireOp",EDGE,"f108ec60-4968-4ad8-8dd3-c2f74511c436");
            var Q1138;
            Q1138=sQuery(id+"F0.wireOp",EDGE,"3774c062-6ca1-4e31-8149-0491274a3a3a");
            var Q1139;
            Q1139=sQuery(id+"F0.wireOp",EDGE,"daac10a3-1925-4f5c-9ac3-5c22cba202c4");
            var Q1140;
            Q1140=sQuery(id+"F0.wireOp",EDGE,"1c98b973-96f5-435f-9491-3192cbf812e4");
            var Q1141;
            Q1141=sQuery(id+"F0.wireOp",EDGE,"d00928be-9b64-481c-a9ee-c68cc400c14e");
            var Q1142;
            Q1142=sQuery(id+"F0.wireOp",EDGE,"feb61220-abdf-4f2e-bd8e-db18306a37ec");
            var Q1143;
            Q1143=sQuery(id+"F0.wireOp",EDGE,"339ba7e6-8849-42e2-a17b-9b37d86c2b32");
            var Q1144;
            Q1144=sQuery(id+"F0.wireOp",EDGE,"afc3be7a-4ee5-457a-a661-d0221db813f6");
            var Q1145;
            Q1145=sQuery(id+"F0.wireOp",EDGE,"9ddf1a81-6e61-493a-8445-79d0dc6dca13");
            var Q1146;
            Q1146=sQuery(id+"F0.wireOp",EDGE,"d752ff8d-b094-486e-a2e1-d0d04a3d4876");
            var Q1147;
            Q1147=sQuery(id+"F0.wireOp",EDGE,"a3ceb55c-4e1d-488d-9717-48e51c048e69");
            var Q1148;
            Q1148=sQuery(id+"F0.wireOp",EDGE,"54fda5f6-063d-4d5e-a28e-cf30f9ac58ee");
            var Q1149;
            Q1149=sQuery(id+"F0.wireOp",EDGE,"10b96512-c83f-44a8-a50d-c67087735c9f");
            var Q1150;
            Q1150=sQuery(id+"F0.wireOp",EDGE,"3549a4c3-8021-4f50-8738-d219cf749902");
            var Q1151;
            Q1151=sQuery(id+"F0.wireOp",EDGE,"59c3d715-60c8-4cb2-af7b-61a9c35e8008");
            var Q1152;
            Q1152=sQuery(id+"F0.wireOp",EDGE,"420d0191-77a8-4846-9af9-eb021fa71ca4");
            var Q1153;
            Q1153=sQuery(id+"F0.wireOp",EDGE,"6c165f4a-eb83-4218-8914-1df302add670");
            var Q1154;
            Q1154=sQuery(id+"F0.wireOp",EDGE,"8c716db9-7f3e-423e-ae7b-79d4767e3e33");
            var Q1155;
            Q1155=sQuery(id+"F0.wireOp",EDGE,"ba537bbd-cad0-436a-acde-6e5695919d87");
            var Q1156;
            Q1156=sQuery(id+"F0.wireOp",EDGE,"cbf23b25-c019-4064-8b08-bfdf0eb0275d");
            var Q1157;
            Q1157=sQuery(id+"F0.wireOp",EDGE,"9f095853-ba20-496e-9656-e23bb46455d7");
            var Q1158;
            Q1158=sQuery(id+"F0.wireOp",EDGE,"ac94fba3-6f13-46b4-8b20-448b8e3462e4");
            var Q1159;
            Q1159=sQuery(id+"F0.wireOp",EDGE,"22ebe7c7-d00c-4df7-b190-db963c23ff84");
            var Q1160;
            Q1160=sQuery(id+"F0.wireOp",EDGE,"3464e4f2-4473-42ea-8d26-2a1bf9ad807b");
            var Q1161;
            Q1161=sQuery(id+"F0.wireOp",EDGE,"453bb8c8-a69c-452c-a5b9-85da4cf1f2fe");
            var Q1162;
            Q1162=sQuery(id+"F0.wireOp",EDGE,"42503707-efc1-4e02-8622-82b466a1a901");
            var Q1163;
            Q1163=sQuery(id+"F0.wireOp",EDGE,"aca3446c-a48b-4ddb-8dcf-45a52939f1aa");
            var Q1164;
            Q1164=sQuery(id+"F0.wireOp",EDGE,"029d299b-73cc-4adb-a7dd-5bf0c18a2f6c");
            var Q1165;
            Q1165=sQuery(id+"F0.wireOp",EDGE,"6f626b80-384b-4cad-9ad6-4c4cb7d07ba2");
            var Q1166;
            Q1166=sQuery(id+"F0.wireOp",EDGE,"0dacc8fe-805a-4985-93cf-803568b133de");
            var Q1167;
            Q1167=sQuery(id+"F0.wireOp",EDGE,"855c098b-118b-4984-9e49-d5c3fc386f93");
            var Q1168;
            Q1168=sQuery(id+"F0.wireOp",EDGE,"9d60d45e-6633-4910-85a8-db10a1abeb68");
            var Q1169;
            Q1169=sQuery(id+"F0.wireOp",EDGE,"a7c134ee-4a82-462c-a689-c30b7cdf3e1c");
            var Q1170;
            Q1170=sQuery(id+"F0.wireOp",EDGE,"f6012f0b-f4fb-4aa6-b9b4-fecfc985ef13");
            var Q1171;
            Q1171=sQuery(id+"F0.wireOp",EDGE,"813674e6-56c6-46bf-ae50-dd63680584e1");
            var Q1172;
            Q1172=sQuery(id+"F0.wireOp",EDGE,"50867e27-907d-46e7-8546-6a4d7aa0ae12");
            var Q1173;
            Q1173=sQuery(id+"F0.wireOp",EDGE,"eb7409a2-58b9-4c6f-858a-ebdd850b69ad");
            var Q1174;
            Q1174=sQuery(id+"F0.wireOp",EDGE,"7ba83392-6b43-42b0-9933-c0ea43256bc3");
            var Q1175;
            Q1175=sQuery(id+"F0.wireOp",EDGE,"86fe4673-5df0-4528-bfaf-30ab9b27e3dd");
            var Q1176;
            Q1176=sQuery(id+"F0.wireOp",EDGE,"8905340d-0776-4caa-9614-3537411ab9cb");
            var Q1177;
            Q1177=sQuery(id+"F0.wireOp",EDGE,"c5ab3c2d-98cd-4cc3-bad3-c80719569fb6");
            var Q1178;
            Q1178=sQuery(id+"F0.wireOp",EDGE,"183c10a1-dc52-46fe-a08d-f45da244174f");
            var Q1179;
            Q1179=sQuery(id+"F0.wireOp",EDGE,"a6c4d6a9-f75f-4806-b924-b25a2732f452");
            var Q1180;
            Q1180=sQuery(id+"F0.wireOp",EDGE,"bff12c84-66ef-4464-b009-736423601901");
            var Q1181;
            Q1181=sQuery(id+"F0.wireOp",EDGE,"f0c3a8d5-f9e6-43db-9993-0f6e2c9ffd25");
            var Q1182;
            Q1182=sQuery(id+"F0.wireOp",EDGE,"c99aa66b-4fe4-4867-883c-e0784af1c06b");
            var Q1183;
            Q1183=sQuery(id+"F0.wireOp",EDGE,"e0bd63f2-9536-4cbb-b6b2-60a9cdce07f1");
            var Q1184;
            Q1184=sQuery(id+"F0.wireOp",EDGE,"7aac01ac-17ef-4f32-af6c-fe2bdad7c437");
            var Q1185;
            Q1185=sQuery(id+"F0.wireOp",EDGE,"0723cd5a-f3a3-406a-b60b-c7d4967394de");
            var Q1186;
            Q1186=sQuery(id+"F0.wireOp",EDGE,"c483ac35-84d3-477d-8f56-a7910402b0fd");
            var Q1187;
            Q1187=sQuery(id+"F0.wireOp",EDGE,"d0cb79d0-2394-4603-8277-b6c36fa26326");
            var Q1188;
            Q1188=sQuery(id+"F0.wireOp",EDGE,"b989aaf2-eff6-46d9-b21d-28e0907ad955");
            var Q1189;
            Q1189=sQuery(id+"F0.wireOp",EDGE,"a79b8e80-5190-4256-8898-0d9b048e6753");
            var Q1190;
            Q1190=sQuery(id+"F0.wireOp",EDGE,"a304bd21-1189-44d1-8f4d-cf30d1f9471e");
            var Q1191;
            Q1191=sQuery(id+"F0.wireOp",EDGE,"110a906b-d9ea-4a08-ac26-33c9e90be99d");
            var Q1192;
            Q1192=sQuery(id+"F0.wireOp",EDGE,"59f20474-fe49-4fc0-95ac-b9a995ebcedf");
            var Q1193;
            Q1193=sQuery(id+"F0.wireOp",EDGE,"e12d07f2-a715-4cce-af43-5ff195a6269f");
            var Q1194;
            Q1194=sQuery(id+"F0.wireOp",EDGE,"3062f8f0-ee88-41c3-b981-ed40f110201a");
            var Q1195;
            Q1195=sQuery(id+"F0.wireOp",EDGE,"84222380-e343-43de-a108-fe13ee216be8");
            var Q1196;
            Q1196=sQuery(id+"F0.wireOp",EDGE,"b8fcadef-81e6-4e31-ac2e-28a0d0e7fc57");
            var Q1197;
            Q1197=sQuery(id+"F0.wireOp",EDGE,"f450fc37-f8f7-4977-9612-3999fd11fa71");
            var Q1198;
            Q1198=sQuery(id+"F0.wireOp",EDGE,"fe363ccb-df82-42a1-bf00-0c4affdece13");
            var Q1199;
            Q1199=sQuery(id+"F0.wireOp",EDGE,"c00ba6ea-c756-468d-be20-9a93ab22eaa3");
            var Q1200;
            Q1200=sQuery(id+"F0.wireOp",EDGE,"8bf7801b-2ef5-47e1-ae34-9830fbe0365b");
            var Q1201;
            Q1201=sQuery(id+"F0.wireOp",EDGE,"3e0faae7-ec92-47c9-9d1e-58831d09b792");
            var Q1202;
            Q1202=sQuery(id+"F0.wireOp",EDGE,"4da6abbe-b8d9-4234-914d-6e448c828b43");
            var Q1203;
            Q1203=sQuery(id+"F0.wireOp",EDGE,"80e74ff1-31d1-4cc5-a67f-249ff43730b9");
            var Q1204;
            Q1204=sQuery(id+"F0.wireOp",EDGE,"5129978e-4d20-4604-acbb-048fe09a930a");
            var Q1205;
            Q1205=sQuery(id+"F0.wireOp",EDGE,"04533f69-956e-4e27-a64a-80f1e2388ea4");
            var Q1206;
            Q1206=sQuery(id+"F0.wireOp",EDGE,"9550e761-4b9e-429c-8274-0d70b3f1497f");
            var Q1207;
            Q1207=sQuery(id+"F0.wireOp",EDGE,"6f84b576-5615-4a44-b602-5b8e12687ab3");
            var Q1208;
            Q1208=sQuery(id+"F0.wireOp",EDGE,"332622cb-7abd-45b5-b02a-597f550706b8");
            var Q1209;
            Q1209=sQuery(id+"F0.wireOp",EDGE,"f77b10ed-182b-485a-9e9c-5799affe1b06");
            var Q1210;
            Q1210=sQuery(id+"F0.wireOp",EDGE,"901e203a-806f-4bab-8007-a4ee834618f9");
            var Q1211;
            Q1211=sQuery(id+"F0.wireOp",EDGE,"9b5f8699-dffb-42f1-956f-457443ac8447");
            var Q1212;
            Q1212=sQuery(id+"F0.wireOp",EDGE,"1f5b3fe8-7c49-40d4-b238-eee804fa50a0");
            var Q1213;
            Q1213=sQuery(id+"F0.wireOp",EDGE,"544a5d24-07d5-4979-811e-279a38922163");
            var Q1214;
            Q1214=sQuery(id+"F0.wireOp",EDGE,"fa063179-f4a6-41a8-959d-d10776167cd3");
            var Q1215;
            Q1215=sQuery(id+"F0.wireOp",EDGE,"06093d75-c62d-4be2-bdb0-3eb055a42e9e");
            var Q1216;
            Q1216=sQuery(id+"F0.wireOp",EDGE,"09458073-2847-4c8f-9e2e-16e823abce5c");
            var Q1217;
            Q1217=sQuery(id+"F0.wireOp",EDGE,"5a75ba8c-6856-42eb-8e03-0ed2454a3e06");
            var Q1218;
            Q1218=sQuery(id+"F0.wireOp",EDGE,"c5f0bf22-2b30-4936-8d0a-bd02d4f08a34");
            var Q1219;
            Q1219=sQuery(id+"F0.wireOp",EDGE,"66dc0efa-3188-4f11-a594-6d325820c26a");
            var Q1220;
            Q1220=sQuery(id+"F0.wireOp",EDGE,"026b4146-ae12-4ec7-bf31-9e4ad6db63f8");
            var Q1221;
            Q1221=sQuery(id+"F0.wireOp",EDGE,"aaa52ea7-56bb-40bb-8052-8ba1d8f1c6e5");
            var Q1222;
            Q1222=sQuery(id+"F0.wireOp",EDGE,"674862a6-29c6-457c-b112-30507f3068c5");
            var Q1223;
            Q1223=sQuery(id+"F0.wireOp",EDGE,"a5c56dd5-6f53-4ee9-9186-cb3a9f345b48");
            var Q1224;
            Q1224=sQuery(id+"F0.wireOp",EDGE,"f8592ba4-85d4-4850-845c-9a19aeeb0234");
            var Q1225;
            Q1225=sQuery(id+"F0.wireOp",EDGE,"fb78cb5d-f617-4463-8ed5-a3e277cf5a1c");
            var Q1226;
            Q1226=sQuery(id+"F0.wireOp",EDGE,"1a20fe12-028e-46e0-bc6d-a1016bbe1a4c");
            var Q1227;
            Q1227=sQuery(id+"F0.wireOp",EDGE,"0d2db3b9-1923-4126-a740-cfea0fea323f");
            var Q1228;
            Q1228=sQuery(id+"F0.wireOp",EDGE,"84456dbb-2811-4a9f-973e-45687f243be5");
            var Q1229;
            Q1229=sQuery(id+"F0.wireOp",EDGE,"55d8a74b-752f-4eb8-a1cc-10eaa5b86778");
            var Q1230;
            Q1230=sQuery(id+"F0.wireOp",EDGE,"797e07f5-6add-4878-91fc-b0fc11005d4f");
            var Q1231;
            Q1231=sQuery(id+"F0.wireOp",EDGE,"2f207ef1-5015-4c0d-b6fe-3b4d000237a4");
            var Q1232;
            Q1232=sQuery(id+"F0.wireOp",EDGE,"08bcbe72-0fe1-405a-9186-7b43a5e18a60");
            var Q1233;
            Q1233=sQuery(id+"F0.wireOp",EDGE,"a91757ab-d63e-41a3-9bd9-9885c4628b95");
            var Q1234;
            Q1234=sQuery(id+"F0.wireOp",EDGE,"a5a23823-105a-41e3-aa97-1ca4cc060672");
            var Q1235;
            Q1235=sQuery(id+"F0.wireOp",EDGE,"5721acc9-99da-4318-85f8-4e8f5e0c5604");
            var Q1236;
            Q1236=sQuery(id+"F0.wireOp",EDGE,"d6b59c8b-c5fb-48f4-80b2-7b7d7c20438d");
            var Q1237;
            Q1237=sQuery(id+"F0.wireOp",EDGE,"17947b76-4190-4341-80b3-32d2f10a46c4");
            var Q1238;
            Q1238=sQuery(id+"F0.wireOp",EDGE,"9ebb6ecf-ace5-4b95-8859-54939e59b9c7");
            var Q1239;
            Q1239=sQuery(id+"F0.wireOp",EDGE,"2759b357-f2be-4634-a86b-7ed53e40126e");
            var Q1240;
            Q1240=sQuery(id+"F0.wireOp",EDGE,"13dec205-eec6-4966-8e37-434043e3bea0");
            var Q1241;
            Q1241=sQuery(id+"F0.wireOp",EDGE,"e1cb6edd-1e6c-48fe-9f27-685bfee70766");
            var Q1242;
            Q1242=sQuery(id+"F0.wireOp",EDGE,"68ff189d-8713-44cc-aa48-ac10bc2864ce");
            var Q1243;
            Q1243=sQuery(id+"F0.wireOp",EDGE,"3a55800d-ffa7-44ea-a043-20e9bdc63de0");
            var Q1244;
            Q1244=sQuery(id+"F0.wireOp",EDGE,"4120baf8-9c83-4847-a2cc-686d46969543");
            var Q1245;
            Q1245=sQuery(id+"F0.wireOp",EDGE,"b380af11-1568-4abd-ae5a-e949bf253836");
            var Q1246;
            Q1246=sQuery(id+"F0.wireOp",EDGE,"c4a63bca-4435-40e7-9dcd-1cd6f53e40e6");
            var Q1247;
            Q1247=sQuery(id+"F0.wireOp",EDGE,"912fed72-529d-496f-ba2f-a8bcd8bf44b5");
            var Q1248;
            Q1248=sQuery(id+"F0.wireOp",EDGE,"b09e278c-f74a-495e-938a-991315706600");
            var Q1249;
            Q1249=sQuery(id+"F0.wireOp",EDGE,"e4251ab2-f1bc-4776-abc5-927bc557a9cf");
            var Q1250;
            Q1250=sQuery(id+"F0.wireOp",EDGE,"6fcecd97-1fad-473a-b538-d2a6704c7040");
            var Q1251;
            Q1251=sQuery(id+"F0.wireOp",EDGE,"ac4b77a3-e393-431d-aae8-1f36693e2015");
            var Q1252;
            Q1252=sQuery(id+"F0.wireOp",EDGE,"584a590f-5cde-4fe0-b9c6-175efc542bb5");
            var Q1253;
            Q1253=sQuery(id+"F0.wireOp",EDGE,"766cbe31-ddab-4eb2-af92-7ebf7f3dfb21");
            var Q1254;
            Q1254=sQuery(id+"F0.wireOp",EDGE,"989bb8ee-e4d0-445e-a88e-9f13e35ae565");
            var Q1255;
            Q1255=sQuery(id+"F0.wireOp",EDGE,"e4fc5e84-4dab-4238-a00e-0b00c12c4121");
            var Q1256;
            Q1256=sQuery(id+"F0.wireOp",EDGE,"d99a3605-28de-4e4a-87c4-f06fe82392bf");
            var Q1257;
            Q1257=sQuery(id+"F0.wireOp",EDGE,"ddd6b76d-75c0-43b8-b257-a7836384e8f0");
            var Q1258;
            Q1258=sQuery(id+"F0.wireOp",EDGE,"060787f0-3f96-4936-8377-06fd555f1251");
            var Q1259;
            Q1259=sQuery(id+"F0.wireOp",EDGE,"9d8af8d7-fc00-4d23-b5c9-7a988ed1700d");
            var Q1260;
            Q1260=sQuery(id+"F0.wireOp",EDGE,"b38656d1-e5b2-46f9-8c99-f5db946fd1fc");
            var Q1261;
            Q1261=sQuery(id+"F0.wireOp",EDGE,"df7374f4-3a7b-4e61-b9a8-90ce8479e9a9");
            var Q1262;
            Q1262=sQuery(id+"F0.wireOp",EDGE,"d774d1e8-8574-4238-8712-36b57315eb95");
            var Q1263;
            Q1263=sQuery(id+"F0.wireOp",EDGE,"ce102e7b-c5b9-4e14-bd26-87ce252c2c16");
            var Q1264;
            Q1264=sQuery(id+"F0.wireOp",EDGE,"03c34f11-ff58-47b2-9d75-c95b9921160f");
            var Q1265;
            Q1265=sQuery(id+"F0.wireOp",EDGE,"dbdeab54-c1bb-4b0c-b69a-e24488286cc9");
            var Q1266;
            Q1266=sQuery(id+"F0.wireOp",EDGE,"e85faae0-1bc9-4c3d-aa13-a96ca68db88b");
            var Q1267;
            Q1267=sQuery(id+"F0.wireOp",EDGE,"f3dc09fe-c92c-42f5-a9f0-b0b2ba60642e");
            var Q1268;
            Q1268=sQuery(id+"F0.wireOp",EDGE,"37948316-fee6-41b5-9c99-7dc231680be6");
            var Q1269;
            Q1269=sQuery(id+"F0.wireOp",EDGE,"4cbac865-8357-4161-ab1e-e64656bbd480");
            var Q1270;
            Q1270=sQuery(id+"F0.wireOp",EDGE,"94dbc04d-2746-47f2-a83c-519bc6f19bb0");
            var Q1271;
            Q1271=sQuery(id+"F0.wireOp",EDGE,"da1fcad3-d07e-4e06-8cff-0fdea0f2da13");
            var Q1272;
            Q1272=sQuery(id+"F0.wireOp",EDGE,"b4380aec-f505-46cd-bb80-910d50d1d195");
            var Q1273;
            Q1273=sQuery(id+"F0.wireOp",EDGE,"454c6f0b-20b5-4a5a-8908-f05304971670");
            var Q1274;
            Q1274=sQuery(id+"F0.wireOp",EDGE,"7eede332-902a-4a38-8ce4-986d70ebe53e");
            var Q1275;
            Q1275=sQuery(id+"F0.wireOp",EDGE,"6923784c-e516-4855-a849-26f9d444fd83");
            var Q1276;
            Q1276=sQuery(id+"F0.wireOp",EDGE,"72eace47-c5db-4d62-b06b-f2ba38ffda4a");
            var Q1277;
            Q1277=sQuery(id+"F0.wireOp",EDGE,"f5cf9b92-93cb-43ae-a0b5-7dd2787fece0");
            var Q1278;
            Q1278=sQuery(id+"F0.wireOp",EDGE,"161773b3-dc72-4ea4-8d7d-2587d17abbc5");
            var Q1279;
            Q1279=sQuery(id+"F0.wireOp",EDGE,"12283117-805b-4687-ad5e-df7a964cbc31");
            var Q1280;
            Q1280=sQuery(id+"F0.wireOp",EDGE,"9d3c9c74-5962-49b5-8442-8b7d2a51da23");
            var Q1281;
            Q1281=sQuery(id+"F0.wireOp",EDGE,"8282cdbf-e702-412e-859d-3aa442c56a14");
            var Q1282;
            Q1282=sQuery(id+"F0.wireOp",EDGE,"4d372f5c-47aa-458e-bdd5-2ba020e6ac50");
            var Q1283;
            Q1283=sQuery(id+"F0.wireOp",EDGE,"29d1f7fd-3452-461b-98e7-9ed9f4e6febf");
            var Q1284;
            Q1284=sQuery(id+"F0.wireOp",EDGE,"732ea894-6130-40fa-9b68-3e64df07e1ee");
            var Q1285;
            Q1285=sQuery(id+"F0.wireOp",EDGE,"f5d522d1-0dd0-4a90-ba6f-0c2fed08fe0e");
            var Q1286;
            Q1286=sQuery(id+"F0.wireOp",EDGE,"4cd86e53-7046-447b-85fb-6f8859658234");
            var Q1287;
            Q1287=sQuery(id+"F0.wireOp",EDGE,"f6c412b2-cfb6-4a2e-972a-44fdd27c8a07");
            var Q1288;
            Q1288=sQuery(id+"F0.wireOp",EDGE,"66ff0429-de3e-470e-b0ae-79ca92020de8");
            var Q1289;
            Q1289=sQuery(id+"F0.wireOp",EDGE,"3e94e381-b3b6-4228-9425-76e8788fded8");
            var Q1290;
            Q1290=sQuery(id+"F0.wireOp",EDGE,"d77e91d3-d1c2-4537-a73f-6770c961cbd6");
            var Q1291;
            Q1291=sQuery(id+"F0.wireOp",EDGE,"15475fac-b36b-4b4c-b371-ba62c9f21c0f");
            var Q1292;
            Q1292=sQuery(id+"F0.wireOp",EDGE,"11f760f5-05a2-43a2-92e2-8b976bb3a84d");
            var Q1293;
            Q1293=sQuery(id+"F0.wireOp",EDGE,"a3ae4e58-d090-4ecb-971f-de5c9b29571c");
            var Q1294;
            Q1294=sQuery(id+"F0.wireOp",EDGE,"e3f88e8a-0c44-45e8-a3fe-fdefa7446ef1");
            var Q1295;
            Q1295=sQuery(id+"F0.wireOp",EDGE,"346c22ec-2347-410f-80a7-9d088e1ccb27");
            var Q1296;
            Q1296=sQuery(id+"F0.wireOp",EDGE,"02034604-fa94-4537-9cec-6484da4c032f");
            var Q1297;
            Q1297=sQuery(id+"F0.wireOp",EDGE,"cb80fc93-00cc-4510-81c2-f5df0545b084");
            var Q1298;
            Q1298=sQuery(id+"F0.wireOp",EDGE,"0b84124e-1017-43cd-b0d4-25f2b32a36fc");
            var Q1299;
            Q1299=sQuery(id+"F0.wireOp",EDGE,"15cc7feb-c360-4e4f-b640-3587d6237279");
            var Q1300;
            Q1300=sQuery(id+"F0.wireOp",EDGE,"d395e5d7-472c-4e8e-95e6-47e2308dd665");
            var Q1301;
            Q1301=sQuery(id+"F0.wireOp",EDGE,"00a2640e-80fc-42a2-912c-ed8295bac3c7");
            var Q1302;
            Q1302=sQuery(id+"F0.wireOp",EDGE,"70fbf84f-63a9-466f-a818-0c481639541a");
            var Q1303;
            Q1303=sQuery(id+"F0.wireOp",EDGE,"e15e0665-1250-4393-88bd-1cc2e2ea0951");
            var Q1304;
            Q1304=sQuery(id+"F0.wireOp",EDGE,"f7bd280b-bf76-4460-b648-f0eb1ad2c04f");
            var Q1305;
            Q1305=sQuery(id+"F0.wireOp",EDGE,"23166e9d-46af-4d06-bc2d-80f726f1de0d");
            var Q1306;
            Q1306=sQuery(id+"F0.wireOp",EDGE,"c49b4d26-e721-4ffe-902b-6150a3769056");
            var Q1307;
            Q1307=sQuery(id+"F0.wireOp",EDGE,"f872ca04-b118-4773-a286-768e202f795c");
            var Q1308;
            Q1308=sQuery(id+"F0.wireOp",EDGE,"bf8ce8aa-6671-425e-ad24-948657b04ed9");
            var Q1309;
            Q1309=sQuery(id+"F0.wireOp",EDGE,"8c85a848-d737-4563-ae34-d9f68e6dcee5");
            var Q1310;
            Q1310=sQuery(id+"F0.wireOp",EDGE,"53ee6f40-50f4-4738-815f-e78ce2163c40");
            var Q1311;
            Q1311=sQuery(id+"F0.wireOp",EDGE,"63156f2e-2b3f-46bc-b489-749998d68bc3");
            var Q1312;
            Q1312=sQuery(id+"F0.wireOp",EDGE,"c362d669-0421-4a7c-ab3e-e5d00c0b357e");
            var Q1313;
            Q1313=sQuery(id+"F0.wireOp",EDGE,"13aeb47e-039f-44e9-8fe4-bf0e472cb30f");
            var Q1314;
            Q1314=sQuery(id+"F0.wireOp",EDGE,"dbf00fb9-39c5-41f6-90ad-af58c9ffcd50");
            var Q1315;
            Q1315=sQuery(id+"F0.wireOp",EDGE,"f185b365-910a-49cc-a448-3018d712aaba");
            var Q1316;
            Q1316=sQuery(id+"F0.wireOp",EDGE,"a2775f3c-7f1c-4b20-b701-265dd603bb61");
            var Q1317;
            Q1317=sQuery(id+"F0.wireOp",EDGE,"17b69779-362a-4932-97a8-5cfe6e3621c9");
            var Q1318;
            Q1318=sQuery(id+"F0.wireOp",EDGE,"48f7ca06-3e2b-4d08-a762-897818f24976");
            var Q1319;
            Q1319=sQuery(id+"F0.wireOp",EDGE,"c07d7a5d-2010-4841-b116-21003ddc74f8");
            var Q1320;
            Q1320=sQuery(id+"F0.wireOp",EDGE,"99193f23-3ab7-4baa-b17a-3aa4eb08a4da");
            var Q1321;
            Q1321=sQuery(id+"F0.wireOp",EDGE,"559ac3c6-4e71-4f80-bf05-6297c280b27f");
            var Q1322;
            Q1322=sQuery(id+"F0.wireOp",EDGE,"881a4252-2395-4de0-8e50-ba53c30422bc");
            var Q1323;
            Q1323=sQuery(id+"F0.wireOp",EDGE,"7d6392d2-93d9-407f-9a97-df338bd3a349");
            var Q1324;
            Q1324=sQuery(id+"F0.wireOp",EDGE,"8eb605dd-ee7e-414f-a32c-e64946fcedac");
            var Q1325;
            Q1325=sQuery(id+"F0.wireOp",EDGE,"ee634cd5-6846-4a33-bb11-acbcd4b6396e");
            var Q1326;
            Q1326=sQuery(id+"F0.wireOp",EDGE,"ce1b7dbb-860a-4f07-96f7-ee2d091e431b");
            var Q1327;
            Q1327=sQuery(id+"F0.wireOp",EDGE,"590e682f-b1bd-411c-9468-0a40e6445a32");
            var Q1328;
            Q1328=sQuery(id+"F0.wireOp",EDGE,"529066f9-1c69-43c4-956f-5c6a6dc09ace");
            var Q1329;
            Q1329=sQuery(id+"F0.wireOp",EDGE,"6eb5396a-19fa-4a36-8998-b97c80b49874");
            var Q1330;
            Q1330=sQuery(id+"F0.wireOp",EDGE,"72557010-a505-44f5-9187-14afc889c239");
            var Q1331;
            Q1331=sQuery(id+"F0.wireOp",EDGE,"e4fd3d82-1791-4f27-9ee8-f0c105daba96");
            var Q1332;
            Q1332=sQuery(id+"F0.wireOp",EDGE,"e7ab4f75-f83d-4b87-8240-23b6dc068c0d");
            var Q1333;
            Q1333=sQuery(id+"F0.wireOp",EDGE,"59d31a56-ec56-4444-92ad-6d81096a2d14");
            var Q1334;
            Q1334=sQuery(id+"F0.wireOp",EDGE,"359d014b-26e0-4bb1-8828-cf3c8d4f07b5");
            var Q1335;
            Q1335=sQuery(id+"F0.wireOp",EDGE,"49ec5d8c-4806-42c6-b705-d1d292f0e686");
            var Q1336;
            Q1336=sQuery(id+"F0.wireOp",EDGE,"fbd8eddb-634f-45df-9bd2-c3ef2ee84175");
            var Q1337;
            Q1337=sQuery(id+"F0.wireOp",EDGE,"c5177b1d-b45c-4a14-ac18-42fb7abada1e");
            var Q1338;
            Q1338=sQuery(id+"F0.wireOp",EDGE,"fbf4bcb2-fa5c-402b-bca1-3efd9bf47a81");
            var Q1339;
            Q1339=sQuery(id+"F0.wireOp",EDGE,"4247ff09-fe42-443e-b2a4-8716e7d6096a");
            var Q1340;
            Q1340=sQuery(id+"F0.wireOp",EDGE,"1f2513cd-2a5b-4487-9272-388755447c48");
            var Q1341;
            Q1341=sQuery(id+"F0.wireOp",EDGE,"49d2674f-ee30-49b1-8c54-8161d1e04aee");
            var Q1342;
            Q1342=sQuery(id+"F0.wireOp",EDGE,"b174c259-ec2e-4bcc-91bd-089f04a7bcd5");
            var Q1343;
            Q1343=sQuery(id+"F0.wireOp",EDGE,"52ffd256-440c-429d-9056-b09b2f04fd33");
            var Q1344;
            Q1344=sQuery(id+"F0.wireOp",EDGE,"54d4c234-23c1-4c51-bce9-7f9743e33a8d");
            var Q1345;
            Q1345=sQuery(id+"F0.wireOp",EDGE,"9dee383b-f1fa-4598-8df1-68879adfd127");
            var Q1346;
            Q1346=sQuery(id+"F0.wireOp",EDGE,"11000d6e-11c2-4405-8a0c-b0fdc02bf230");
            var Q1347;
            Q1347=sQuery(id+"F0.wireOp",EDGE,"640ce6a5-27df-4cc2-82c1-3895135d33db");
            var Q1348;
            Q1348=sQuery(id+"F0.wireOp",EDGE,"f9719c61-1e59-412b-ac3e-fd38e13567e6");
            var Q1349;
            Q1349=sQuery(id+"F0.wireOp",EDGE,"571807ff-65af-487d-af0f-0ab77cd19bb5");
            var Q1350;
            Q1350=sQuery(id+"F0.wireOp",EDGE,"faa62f8e-18c9-473a-8deb-ee40cc44c566");
            var Q1351;
            Q1351=sQuery(id+"F0.wireOp",EDGE,"5b7028ed-1ce1-46bc-926f-e5e2fb5a7630");
            var Q1352;
            Q1352=sQuery(id+"F0.wireOp",EDGE,"eba75926-2dfe-47b2-a172-6cf9ca8fc07d");
            var Q1353;
            Q1353=sQuery(id+"F0.wireOp",EDGE,"ae380623-ecd7-4712-9342-07ab9c93e1c8");
            var Q1354;
            Q1354=sQuery(id+"F0.wireOp",EDGE,"fa208c36-a280-469d-ab5a-5a2d62d456d4");
            var Q1355;
            Q1355=sQuery(id+"F0.wireOp",EDGE,"bd44625d-0dc7-422f-a4f4-726080b88030");
            var Q1356;
            Q1356=sQuery(id+"F0.wireOp",EDGE,"d3a2a52e-44a4-4a86-99ef-13d7f1bbf405");
            var Q1357;
            Q1357=sQuery(id+"F0.wireOp",EDGE,"0d039bc9-8127-42fb-810f-2e4b396d5ef9");
            var Q1358;
            Q1358=sQuery(id+"F0.wireOp",EDGE,"696578c1-0c8c-42e3-b4dd-b07d2fd675da");
            var Q1359;
            Q1359=sQuery(id+"F0.wireOp",EDGE,"a1089da2-28b0-4783-9a28-291cc434f31e");
            var Q1360;
            Q1360=sQuery(id+"F0.wireOp",EDGE,"e56c3784-59dd-41f3-a108-5a2fb828fcd9");
            var Q1361;
            Q1361=sQuery(id+"F0.wireOp",EDGE,"a5b7fbfa-35d4-46e9-80b8-e5ed622bea96");
            var Q1362;
            Q1362=sQuery(id+"F0.wireOp",EDGE,"37e30be5-a4f2-4fdd-a2e5-d734590d65d1");
            var Q1363;
            Q1363=sQuery(id+"F0.wireOp",EDGE,"c5543c86-97ec-429b-86f3-65cd64452b08");
            var Q1364;
            Q1364=sQuery(id+"F0.wireOp",EDGE,"f215a814-bcd0-49c0-9f1e-9bb66a6226e8");
            var Q1365;
            Q1365=sQuery(id+"F0.wireOp",EDGE,"32ba71c9-9490-496d-913d-68b1383bb7ed");
            var Q1366;
            Q1366=sQuery(id+"F0.wireOp",EDGE,"c2b0287d-56ba-42e7-a1f2-0e6de6af062b");
            var Q1367;
            Q1367=sQuery(id+"F0.wireOp",EDGE,"834f25ca-cdd7-43dc-b609-bc32ff1f469e");
            var Q1368;
            Q1368=sQuery(id+"F0.wireOp",EDGE,"312563ce-f695-46ac-bc21-64384a65863d");
            var Q1369;
            Q1369=sQuery(id+"F0.wireOp",EDGE,"3267d0bb-1432-4e9a-bc73-11469d8375d2");
            var Q1370;
            Q1370=sQuery(id+"F0.wireOp",EDGE,"75961fea-2c38-4ea4-bd3c-f87dd9f3092c");
            var Q1371;
            Q1371=sQuery(id+"F0.wireOp",EDGE,"05a7049a-f5b5-47ee-883a-9108e9cdb64c");
            var Q1372;
            Q1372=sQuery(id+"F0.wireOp",EDGE,"13bd3d35-b5d6-4273-bf40-56a0117b2b4b");
            var Q1373;
            Q1373=sQuery(id+"F0.wireOp",EDGE,"1406826a-057a-42cd-beca-a29def5dc4d4");
            var Q1374;
            Q1374=sQuery(id+"F0.wireOp",EDGE,"26dbfe3f-ae89-4ac8-98af-949b286d1ad9");
            var Q1375;
            Q1375=sQuery(id+"F0.wireOp",EDGE,"17721804-51c0-44f5-b324-c037e925600d");
            var Q1376;
            Q1376=sQuery(id+"F0.wireOp",EDGE,"3e2aa420-7b40-4adf-8a27-5fcc1d3ce966");
            var Q1377;
            Q1377=sQuery(id+"F0.wireOp",EDGE,"1486499e-cbb5-47a0-a88d-70d6b3a528ce");
            var Q1378;
            Q1378=sQuery(id+"F0.wireOp",EDGE,"eb327f9f-c993-45fc-ad77-f7179a553bda");
            var Q1379;
            Q1379=sQuery(id+"F0.wireOp",EDGE,"c1cc47a9-5b97-4cbb-bf9a-995889f1cada");
            var Q1380;
            Q1380=sQuery(id+"F0.wireOp",EDGE,"864e614b-3ad8-4650-9229-1a20c3611ab8");
            var Q1381;
            Q1381=sQuery(id+"F0.wireOp",EDGE,"9d2d9ff6-200c-4ff0-a039-3a82e9d78d8c");
            var Q1382;
            Q1382=sQuery(id+"F0.wireOp",EDGE,"2cabda5f-b57c-4f3b-97d5-7ed6f15cf629");
            var Q1383;
            Q1383=sQuery(id+"F0.wireOp",EDGE,"ccde0fb7-6b46-442e-ad72-263d78a239e4");
            var Q1384;
            Q1384=sQuery(id+"F0.wireOp",EDGE,"bd828c82-aac5-4da9-91f8-a36feac8695b");
            var Q1385;
            Q1385=sQuery(id+"F0.wireOp",EDGE,"3d93bdcd-5e6d-4342-ad34-b9d44d5aa404");
            var Q1386;
            Q1386=sQuery(id+"F0.wireOp",EDGE,"3b2d3f53-59e2-4468-a894-b060aeea083f");
            var Q1387;
            Q1387=sQuery(id+"F0.wireOp",EDGE,"a664053d-bfeb-419d-8b75-4bac2216b06f");
            var Q1388;
            Q1388=sQuery(id+"F0.wireOp",EDGE,"db416ea9-f508-47cc-811d-0afecb716931");
            var Q1389;
            Q1389=sQuery(id+"F0.wireOp",EDGE,"c3b289da-63b1-464d-9574-5457f3ea9871");
            var Q1390;
            Q1390=sQuery(id+"F0.wireOp",EDGE,"33fbe0ee-05f0-4682-be39-cb04b87b9ac7");
            var Q1391;
            Q1391=sQuery(id+"F0.wireOp",EDGE,"dbb6d9e4-5da1-4622-ae7d-8c21c045b3e3");
            var Q1392;
            Q1392=sQuery(id+"F0.wireOp",EDGE,"e16bb249-f1db-4a55-9058-b682ca490d22");
            var Q1393;
            Q1393=sQuery(id+"F0.wireOp",EDGE,"9fb3bedd-9338-411f-966a-6a0a9b5fccb0");
            var Q1394;
            Q1394=sQuery(id+"F0.wireOp",EDGE,"e90ca38f-8dab-4b8d-a0c2-d79bcb81ddd9");
            var Q1395;
            Q1395=sQuery(id+"F0.wireOp",EDGE,"8ec7a96a-6984-4633-b93f-17bf555cce94");
            var Q1396;
            Q1396=sQuery(id+"F0.wireOp",EDGE,"5a26aa9e-449f-476e-bc64-d372c8154948");
            var Q1397;
            Q1397=sQuery(id+"F0.wireOp",EDGE,"f0df8461-4c38-4a66-9377-2ffbfb91d054");
            var Q1398;
            Q1398=sQuery(id+"F0.wireOp",EDGE,"b7aa6c94-a8c6-4d33-b23c-789710eaa304");
            var Q1399;
            Q1399=sQuery(id+"F0.wireOp",EDGE,"97ce4053-e7e7-4319-83fa-8006ab3e7f19");
            var Q1400;
            Q1400=sQuery(id+"F0.wireOp",EDGE,"24ea41b5-14ef-4a86-9cf6-8b47cbc0f522");
            var Q1401;
            Q1401=sQuery(id+"F0.wireOp",EDGE,"2dbfffdd-ece1-4271-bd24-afe459a690d0");
            extrude(context, id + "F1", {"entities" : qUnion([Q0]), "surfaceEntities" : qUnion([Q1, Q2, Q3, Q4, Q5, Q6, Q7, Q8, Q9, Q10, Q11, Q12, Q13, Q14, Q15, Q16, Q17, Q18, Q19, Q20, Q21, Q22, Q23, Q24, Q25, Q26, Q27, Q28, Q29, Q30, Q31, Q32, Q33, Q34, Q35, Q36, Q37, Q38, Q39, Q40, Q41, Q42, Q43, Q44, Q45, Q46, Q47, Q48, Q49, Q50, Q51, Q52, Q53, Q54, Q55, Q56, Q57, Q58, Q59, Q60, Q61, Q62, Q63, Q64, Q65, Q66, Q67, Q68, Q69, Q70, Q71, Q72, Q73, Q74, Q75, Q76, Q77, Q78, Q79, Q80, Q81, Q82, Q83, Q84, Q85, Q86, Q87, Q88, Q89, Q90, Q91, Q92, Q93, Q94, Q95, Q96, Q97, Q98, Q99, Q100, Q101, Q102, Q103, Q104, Q105, Q106, Q107, Q108, Q109, Q110, Q111, Q112, Q113, Q114, Q115, Q116, Q117, Q118, Q119, Q120, Q121, Q122, Q123, Q124, Q125, Q126, Q127, Q128, Q129, Q130, Q131, Q132, Q133, Q134, Q135, Q136, Q137, Q138, Q139, Q140, Q141, Q142, Q143, Q144, Q145, Q146, Q147, Q148, Q149, Q150, Q151, Q152, Q153, Q154, Q155, Q156, Q157, Q158, Q159, Q160, Q161, Q162, Q163, Q164, Q165, Q166, Q167, Q168, Q169, Q170, Q171, Q172, Q173, Q174, Q175, Q176, Q177, Q178, Q179, Q180, Q181, Q182, Q183, Q184, Q185, Q186, Q187, Q188, Q189, Q190, Q191, Q192, Q193, Q194, Q195, Q196, Q197, Q198, Q199, Q200, Q201, Q202, Q203, Q204, Q205, Q206, Q207, Q208, Q209, Q210, Q211, Q212, Q213, Q214, Q215, Q216, Q217, Q218, Q219, Q220, Q221, Q222, Q223, Q224, Q225, Q226, Q227, Q228, Q229, Q230, Q231, Q232, Q233, Q234, Q235, Q236, Q237, Q238, Q239, Q240, Q241, Q242, Q243, Q244, Q245, Q246, Q247, Q248, Q249, Q250, Q251, Q252, Q253, Q254, Q255, Q256, Q257, Q258, Q259, Q260, Q261, Q262, Q263, Q264, Q265, Q266, Q267, Q268, Q269, Q270, Q271, Q272, Q273, Q274, Q275, Q276, Q277, Q278, Q279, Q280, Q281, Q282, Q283, Q284, Q285, Q286, Q287, Q288, Q289, Q290, Q291, Q292, Q293, Q294, Q295, Q296, Q297, Q298, Q299, Q300, Q301, Q302, Q303, Q304, Q305, Q306, Q307, Q308, Q309, Q310, Q311, Q312, Q313, Q314, Q315, Q316, Q317, Q318, Q319, Q320, Q321, Q322, Q323, Q324, Q325, Q326, Q327, Q328, Q329, Q330, Q331, Q332, Q333, Q334, Q335, Q336, Q337, Q338, Q339, Q340, Q341, Q342, Q343, Q344, Q345, Q346, Q347, Q348, Q349, Q350, Q351, Q352, Q353, Q354, Q355, Q356, Q357, Q358, Q359, Q360, Q361, Q362, Q363, Q364, Q365, Q366, Q367, Q368, Q369, Q370, Q371, Q372, Q373, Q374, Q375, Q376, Q377, Q378, Q379, Q380, Q381, Q382, Q383, Q384, Q385, Q386, Q387, Q388, Q389, Q390, Q391, Q392, Q393, Q394, Q395, Q396, Q397, Q398, Q399, Q400, Q401, Q402, Q403, Q404, Q405, Q406, Q407, Q408, Q409, Q410, Q411, Q412, Q413, Q414, Q415, Q416, Q417, Q418, Q419, Q420, Q421, Q422, Q423, Q424, Q425, Q426, Q427, Q428, Q429, Q430, Q431, Q432, Q433, Q434, Q435, Q436, Q437, Q438, Q439, Q440, Q441, Q442, Q443, Q444, Q445, Q446, Q447, Q448, Q449, Q450, Q451, Q452, Q453, Q454, Q455, Q456, Q457, Q458, Q459, Q460, Q461, Q462, Q463, Q464, Q465, Q466, Q467, Q468, Q469, Q470, Q471, Q472, Q473, Q474, Q475, Q476, Q477, Q478, Q479, Q480, Q481, Q482, Q483, Q484, Q485, Q486, Q487, Q488, Q489, Q490, Q491, Q492, Q493, Q494, Q495, Q496, Q497, Q498, Q499, Q500, Q501, Q502, Q503, Q504, Q505, Q506, Q507, Q508, Q509, Q510, Q511, Q512, Q513, Q514, Q515, Q516, Q517, Q518, Q519, Q520, Q521, Q522, Q523, Q524, Q525, Q526, Q527, Q528, Q529, Q530, Q531, Q532, Q533, Q534, Q535, Q536, Q537, Q538, Q539, Q540, Q541, Q542, Q543, Q544, Q545, Q546, Q547, Q548, Q549, Q550, Q551, Q552, Q553, Q554, Q555, Q556, Q557, Q558, Q559, Q560, Q561, Q562, Q563, Q564, Q565, Q566, Q567, Q568, Q569, Q570, Q571, Q572, Q573, Q574, Q575, Q576, Q577, Q578, Q579, Q580, Q581, Q582, Q583, Q584, Q585, Q586, Q587, Q588, Q589, Q590, Q591, Q592, Q593, Q594, Q595, Q596, Q597, Q598, Q599, Q600, Q601, Q602, Q603, Q604, Q605, Q606, Q607, Q608, Q609, Q610, Q611, Q612, Q613, Q614, Q615, Q616, Q617, Q618, Q619, Q620, Q621, Q622, Q623, Q624, Q625, Q626, Q627, Q628, Q629, Q630, Q631, Q632, Q633, Q634, Q635, Q636, Q637, Q638, Q639, Q640, Q641, Q642, Q643, Q644, Q645, Q646, Q647, Q648, Q649, Q650, Q651, Q652, Q653, Q654, Q655, Q656, Q657, Q658, Q659, Q660, Q661, Q662, Q663, Q664, Q665, Q666, Q667, Q668, Q669, Q670, Q671, Q672, Q673, Q674, Q675, Q676, Q677, Q678, Q679, Q680, Q681, Q682, Q683, Q684, Q685, Q686, Q687, Q688, Q689, Q690, Q691, Q692, Q693, Q694, Q695, Q696, Q697, Q698, Q699, Q700, Q701, Q702, Q703, Q704, Q705, Q706, Q707, Q708, Q709, Q710, Q711, Q712, Q713, Q714, Q715, Q716, Q717, Q718, Q719, Q720, Q721, Q722, Q723, Q724, Q725, Q726, Q727, Q728, Q729, Q730, Q731, Q732, Q733, Q734, Q735, Q736, Q737, Q738, Q739, Q740, Q741, Q742, Q743, Q744, Q745, Q746, Q747, Q748, Q749, Q750, Q751, Q752, Q753, Q754, Q755, Q756, Q757, Q758, Q759, Q760, Q761, Q762, Q763, Q764, Q765, Q766, Q767, Q768, Q769, Q770, Q771, Q772, Q773, Q774, Q775, Q776, Q777, Q778, Q779, Q780, Q781, Q782, Q783, Q784, Q785, Q786, Q787, Q788, Q789, Q790, Q791, Q792, Q793, Q794, Q795, Q796, Q797, Q798, Q799, Q800, Q801, Q802, Q803, Q804, Q805, Q806, Q807, Q808, Q809, Q810, Q811, Q812, Q813, Q814, Q815, Q816, Q817, Q818, Q819, Q820, Q821, Q822, Q823, Q824, Q825, Q826, Q827, Q828, Q829, Q830, Q831, Q832, Q833, Q834, Q835, Q836, Q837, Q838, Q839, Q840, Q841, Q842, Q843, Q844, Q845, Q846, Q847, Q848, Q849, Q850, Q851, Q852, Q853, Q854, Q855, Q856, Q857, Q858, Q859, Q860, Q861, Q862, Q863, Q864, Q865, Q866, Q867, Q868, Q869, Q870, Q871, Q872, Q873, Q874, Q875, Q876, Q877, Q878, Q879, Q880, Q881, Q882, Q883, Q884, Q885, Q886, Q887, Q888, Q889, Q890, Q891, Q892, Q893, Q894, Q895, Q896, Q897, Q898, Q899, Q900, Q901, Q902, Q903, Q904, Q905, Q906, Q907, Q908, Q909, Q910, Q911, Q912, Q913, Q914, Q915, Q916, Q917, Q918, Q919, Q920, Q921, Q922, Q923, Q924, Q925, Q926, Q927, Q928, Q929, Q930, Q931, Q932, Q933, Q934, Q935, Q936, Q937, Q938, Q939, Q940, Q941, Q942, Q943, Q944, Q945, Q946, Q947, Q948, Q949, Q950, Q951, Q952, Q953, Q954, Q955, Q956, Q957, Q958, Q959, Q960, Q961, Q962, Q963, Q964, Q965, Q966, Q967, Q968, Q969, Q970, Q971, Q972, Q973, Q974, Q975, Q976, Q977, Q978, Q979, Q980, Q981, Q982, Q983, Q984, Q985, Q986, Q987, Q988, Q989, Q990, Q991, Q992, Q993, Q994, Q995, Q996, Q997, Q998, Q999, Q1000, Q1001, Q1002, Q1003, Q1004, Q1005, Q1006, Q1007, Q1008, Q1009, Q1010, Q1011, Q1012, Q1013, Q1014, Q1015, Q1016, Q1017, Q1018, Q1019, Q1020, Q1021, Q1022, Q1023, Q1024, Q1025, Q1026, Q1027, Q1028, Q1029, Q1030, Q1031, Q1032, Q1033, Q1034, Q1035, Q1036, Q1037, Q1038, Q1039, Q1040, Q1041, Q1042, Q1043, Q1044, Q1045, Q1046, Q1047, Q1048, Q1049, Q1050, Q1051, Q1052, Q1053, Q1054, Q1055, Q1056, Q1057, Q1058, Q1059, Q1060, Q1061, Q1062, Q1063, Q1064, Q1065, Q1066, Q1067, Q1068, Q1069, Q1070, Q1071, Q1072, Q1073, Q1074, Q1075, Q1076, Q1077, Q1078, Q1079, Q1080, Q1081, Q1082, Q1083, Q1084, Q1085, Q1086, Q1087, Q1088, Q1089, Q1090, Q1091, Q1092, Q1093, Q1094, Q1095, Q1096, Q1097, Q1098, Q1099, Q1100, Q1101, Q1102, Q1103, Q1104, Q1105, Q1106, Q1107, Q1108, Q1109, Q1110, Q1111, Q1112, Q1113, Q1114, Q1115, Q1116, Q1117, Q1118, Q1119, Q1120, Q1121, Q1122, Q1123, Q1124, Q1125, Q1126, Q1127, Q1128, Q1129, Q1130, Q1131, Q1132, Q1133, Q1134, Q1135, Q1136, Q1137, Q1138, Q1139, Q1140, Q1141, Q1142, Q1143, Q1144, Q1145, Q1146, Q1147, Q1148, Q1149, Q1150, Q1151, Q1152, Q1153, Q1154, Q1155, Q1156, Q1157, Q1158, Q1159, Q1160, Q1161, Q1162, Q1163, Q1164, Q1165, Q1166, Q1167, Q1168, Q1169, Q1170, Q1171, Q1172, Q1173, Q1174, Q1175, Q1176, Q1177, Q1178, Q1179, Q1180, Q1181, Q1182, Q1183, Q1184, Q1185, Q1186, Q1187, Q1188, Q1189, Q1190, Q1191, Q1192, Q1193, Q1194, Q1195, Q1196, Q1197, Q1198, Q1199, Q1200, Q1201, Q1202, Q1203, Q1204, Q1205, Q1206, Q1207, Q1208, Q1209, Q1210, Q1211, Q1212, Q1213, Q1214, Q1215, Q1216, Q1217, Q1218, Q1219, Q1220, Q1221, Q1222, Q1223, Q1224, Q1225, Q1226, Q1227, Q1228, Q1229, Q1230, Q1231, Q1232, Q1233, Q1234, Q1235, Q1236, Q1237, Q1238, Q1239, Q1240, Q1241, Q1242, Q1243, Q1244, Q1245, Q1246, Q1247, Q1248, Q1249, Q1250, Q1251, Q1252, Q1253, Q1254, Q1255, Q1256, Q1257, Q1258, Q1259, Q1260, Q1261, Q1262, Q1263, Q1264, Q1265, Q1266, Q1267, Q1268, Q1269, Q1270, Q1271, Q1272, Q1273, Q1274, Q1275, Q1276, Q1277, Q1278, Q1279, Q1280, Q1281, Q1282, Q1283, Q1284, Q1285, Q1286, Q1287, Q1288, Q1289, Q1290, Q1291, Q1292, Q1293, Q1294, Q1295, Q1296, Q1297, Q1298, Q1299, Q1300, Q1301, Q1302, Q1303, Q1304, Q1305, Q1306, Q1307, Q1308, Q1309, Q1310, Q1311, Q1312, Q1313, Q1314, Q1315, Q1316, Q1317, Q1318, Q1319, Q1320, Q1321, Q1322, Q1323, Q1324, Q1325, Q1326, Q1327, Q1328, Q1329, Q1330, Q1331, Q1332, Q1333, Q1334, Q1335, Q1336, Q1337, Q1338, Q1339, Q1340, Q1341, Q1342, Q1343, Q1344, Q1345, Q1346, Q1347, Q1348, Q1349, Q1350, Q1351, Q1352, Q1353, Q1354, Q1355, Q1356, Q1357, Q1358, Q1359, Q1360, Q1361, Q1362, Q1363, Q1364, Q1365, Q1366, Q1367, Q1368, Q1369, Q1370, Q1371, Q1372, Q1373, Q1374, Q1375, Q1376, Q1377, Q1378, Q1379, Q1380, Q1381, Q1382, Q1383, Q1384, Q1385, Q1386, Q1387, Q1388, Q1389, Q1390, Q1391, Q1392, Q1393, Q1394, Q1395, Q1396, Q1397, Q1398, Q1399, Q1400, Q1401]), "depth" : 3 * mm});
        }
        {
            var Q0;
            Q0=qCreatedBy(makeId("Front.planeOp"),FACE);
            var sketch = newSketch(context, id + "F2", { "sketchPlane" : qUnion([Q0])});
            skCircle(sketch, "E1402", {"center": v(0, 8.75) * mm, "radius": 3.5 * mm});
            skCircle(sketch, "E1403", {"center": v(-8.75, 0) * mm, "radius": 3.5 * mm});
            skCircle(sketch, "E1404", {"center": v(0, -8.75) * mm, "radius": 3.5 * mm});
            skCircle(sketch, "E1405", {"center": v(8.75, 0) * mm, "radius": 3.5 * mm});
            skSolve(sketch);
        }
        {
            var Q0;
            Q0=makeQuery(id+"F2.imprint","IMPRINT",FACE,{"disambiguationData":[TD([[makeQuery(id+"F2.imprint","IMPRINT",EDGE,{"derivedFrom":sQuery(id+"F2.wireOp",EDGE,"E1405")}),1.0]])]});
            var Q1;
            Q1=makeQuery(id+"F2.imprint","IMPRINT",FACE,{"disambiguationData":[TD([[makeQuery(id+"F2.imprint","IMPRINT",EDGE,{"derivedFrom":sQuery(id+"F2.wireOp",EDGE,"E1402")}),1.0]])]});
            var Q2;
            Q2=makeQuery(id+"F2.imprint","IMPRINT",FACE,{"disambiguationData":[TD([[makeQuery(id+"F2.imprint","IMPRINT",EDGE,{"derivedFrom":sQuery(id+"F2.wireOp",EDGE,"E1403")}),1.0]])]});
            var Q3;
            Q3=makeQuery(id+"F2.imprint","IMPRINT",FACE,{"disambiguationData":[TD([[makeQuery(id+"F2.imprint","IMPRINT",EDGE,{"derivedFrom":sQuery(id+"F2.wireOp",EDGE,"E1404")}),1.0]])]});
            extrude(context, id + "F3", {"entities" : qUnion([Q0, Q1, Q2, Q3]), "endBound" : BoundingType.SYMMETRIC, "depth" : 25 * mm});
        }
        {
            var Q0;
            Q0=makeQuery(id+"F3.opExtrude","SWEPT_BODY",BODY,{"disambiguationData":[OSD([sQuery(id+"F2.wireOp",EDGE,"E1405")])]});
            var Q1;
            Q1=makeQuery(id+"F3.opExtrude","SWEPT_BODY",BODY,{"disambiguationData":[OSD([sQuery(id+"F2.wireOp",EDGE,"E1402")])]});
            var Q2;
            Q2=makeQuery(id+"F3.opExtrude","SWEPT_BODY",BODY,{"disambiguationData":[OSD([sQuery(id+"F2.wireOp",EDGE,"E1403")])]});
            var Q3;
            Q3=makeQuery(id+"F3.opExtrude","SWEPT_BODY",BODY,{"disambiguationData":[OSD([sQuery(id+"F2.wireOp",EDGE,"E1404")])]});
            var Q4;
            Q4=makeQuery(id+"F1.opExtrude","SWEPT_BODY",BODY,{"disambiguationData":[OSD([sQuery(id+"F0.wireOp",EDGE,"E0"),sQuery(id+"F0.wireOp",EDGE,"E1"),sQuery(id+"F0.wireOp",EDGE,"E2"),sQuery(id+"F0.wireOp",EDGE,"E3"),sQuery(id+"F0.wireOp",EDGE,"E4"),sQuery(id+"F0.wireOp",EDGE,"E5"),sQuery(id+"F0.wireOp",EDGE,"E6"),sQuery(id+"F0.wireOp",EDGE,"E7"),sQuery(id+"F0.wireOp",EDGE,"E8"),sQuery(id+"F0.wireOp",EDGE,"E9"),sQuery(id+"F0.wireOp",EDGE,"E10"),sQuery(id+"F0.wireOp",EDGE,"E11"),sQuery(id+"F0.wireOp",EDGE,"E12"),sQuery(id+"F0.wireOp",EDGE,"E13"),sQuery(id+"F0.wireOp",EDGE,"E14"),sQuery(id+"F0.wireOp",EDGE,"E15"),sQuery(id+"F0.wireOp",EDGE,"E16"),sQuery(id+"F0.wireOp",EDGE,"E17"),sQuery(id+"F0.wireOp",EDGE,"E18"),sQuery(id+"F0.wireOp",EDGE,"E19"),sQuery(id+"F0.wireOp",EDGE,"E20"),sQuery(id+"F0.wireOp",EDGE,"E21"),sQuery(id+"F0.wireOp",EDGE,"E22"),sQuery(id+"F0.wireOp",EDGE,"E23"),sQuery(id+"F0.wireOp",EDGE,"E24"),sQuery(id+"F0.wireOp",EDGE,"E25"),sQuery(id+"F0.wireOp",EDGE,"E26"),sQuery(id+"F0.wireOp",EDGE,"E27"),sQuery(id+"F0.wireOp",EDGE,"E28"),sQuery(id+"F0.wireOp",EDGE,"E29"),sQuery(id+"F0.wireOp",EDGE,"E30"),sQuery(id+"F0.wireOp",EDGE,"E31"),sQuery(id+"F0.wireOp",EDGE,"E32"),sQuery(id+"F0.wireOp",EDGE,"E33"),sQuery(id+"F0.wireOp",EDGE,"E34"),sQuery(id+"F0.wireOp",EDGE,"E35"),sQuery(id+"F0.wireOp",EDGE,"E36"),sQuery(id+"F0.wireOp",EDGE,"E37"),sQuery(id+"F0.wireOp",EDGE,"E38"),sQuery(id+"F0.wireOp",EDGE,"E39"),sQuery(id+"F0.wireOp",EDGE,"E40"),sQuery(id+"F0.wireOp",EDGE,"E41"),sQuery(id+"F0.wireOp",EDGE,"E42"),sQuery(id+"F0.wireOp",EDGE,"E43"),sQuery(id+"F0.wireOp",EDGE,"E44"),sQuery(id+"F0.wireOp",EDGE,"E45"),sQuery(id+"F0.wireOp",EDGE,"E46"),sQuery(id+"F0.wireOp",EDGE,"E47"),sQuery(id+"F0.wireOp",EDGE,"E48"),sQuery(id+"F0.wireOp",EDGE,"E49"),sQuery(id+"F0.wireOp",EDGE,"E50"),sQuery(id+"F0.wireOp",EDGE,"E51"),sQuery(id+"F0.wireOp",EDGE,"E52"),sQuery(id+"F0.wireOp",EDGE,"E53"),sQuery(id+"F0.wireOp",EDGE,"E54"),sQuery(id+"F0.wireOp",EDGE,"E55"),sQuery(id+"F0.wireOp",EDGE,"E56"),sQuery(id+"F0.wireOp",EDGE,"E57"),sQuery(id+"F0.wireOp",EDGE,"E58"),sQuery(id+"F0.wireOp",EDGE,"E59"),sQuery(id+"F0.wireOp",EDGE,"E60"),sQuery(id+"F0.wireOp",EDGE,"E61"),sQuery(id+"F0.wireOp",EDGE,"E62"),sQuery(id+"F0.wireOp",EDGE,"E63"),sQuery(id+"F0.wireOp",EDGE,"E64"),sQuery(id+"F0.wireOp",EDGE,"E65"),sQuery(id+"F0.wireOp",EDGE,"E66"),sQuery(id+"F0.wireOp",EDGE,"E67"),sQuery(id+"F0.wireOp",EDGE,"E68"),sQuery(id+"F0.wireOp",EDGE,"E69"),sQuery(id+"F0.wireOp",EDGE,"E70"),sQuery(id+"F0.wireOp",EDGE,"E71"),sQuery(id+"F0.wireOp",EDGE,"E72"),sQuery(id+"F0.wireOp",EDGE,"E73"),sQuery(id+"F0.wireOp",EDGE,"E74"),sQuery(id+"F0.wireOp",EDGE,"E75"),sQuery(id+"F0.wireOp",EDGE,"E76"),sQuery(id+"F0.wireOp",EDGE,"E77"),sQuery(id+"F0.wireOp",EDGE,"E78"),sQuery(id+"F0.wireOp",EDGE,"E79"),sQuery(id+"F0.wireOp",EDGE,"E80"),sQuery(id+"F0.wireOp",EDGE,"E81"),sQuery(id+"F0.wireOp",EDGE,"E82"),sQuery(id+"F0.wireOp",EDGE,"E83"),sQuery(id+"F0.wireOp",EDGE,"E84"),sQuery(id+"F0.wireOp",EDGE,"E85"),sQuery(id+"F0.wireOp",EDGE,"E86"),sQuery(id+"F0.wireOp",EDGE,"E87"),sQuery(id+"F0.wireOp",EDGE,"E88"),sQuery(id+"F0.wireOp",EDGE,"E89"),sQuery(id+"F0.wireOp",EDGE,"E90"),sQuery(id+"F0.wireOp",EDGE,"E91"),sQuery(id+"F0.wireOp",EDGE,"E92"),sQuery(id+"F0.wireOp",EDGE,"E93"),sQuery(id+"F0.wireOp",EDGE,"E94"),sQuery(id+"F0.wireOp",EDGE,"E95"),sQuery(id+"F0.wireOp",EDGE,"E96"),sQuery(id+"F0.wireOp",EDGE,"E97"),sQuery(id+"F0.wireOp",EDGE,"E98"),sQuery(id+"F0.wireOp",EDGE,"E99"),sQuery(id+"F0.wireOp",EDGE,"E100"),sQuery(id+"F0.wireOp",EDGE,"E101"),sQuery(id+"F0.wireOp",EDGE,"E102"),sQuery(id+"F0.wireOp",EDGE,"E103"),sQuery(id+"F0.wireOp",EDGE,"E104"),sQuery(id+"F0.wireOp",EDGE,"E105"),sQuery(id+"F0.wireOp",EDGE,"E106"),sQuery(id+"F0.wireOp",EDGE,"E107"),sQuery(id+"F0.wireOp",EDGE,"E108"),sQuery(id+"F0.wireOp",EDGE,"E109"),sQuery(id+"F0.wireOp",EDGE,"E110"),sQuery(id+"F0.wireOp",EDGE,"E111"),sQuery(id+"F0.wireOp",EDGE,"E112"),sQuery(id+"F0.wireOp",EDGE,"E113"),sQuery(id+"F0.wireOp",EDGE,"E114"),sQuery(id+"F0.wireOp",EDGE,"E115"),sQuery(id+"F0.wireOp",EDGE,"E116"),sQuery(id+"F0.wireOp",EDGE,"E117"),sQuery(id+"F0.wireOp",EDGE,"E118"),sQuery(id+"F0.wireOp",EDGE,"E119"),sQuery(id+"F0.wireOp",EDGE,"E120"),sQuery(id+"F0.wireOp",EDGE,"E121"),sQuery(id+"F0.wireOp",EDGE,"E122"),sQuery(id+"F0.wireOp",EDGE,"E123"),sQuery(id+"F0.wireOp",EDGE,"E124"),sQuery(id+"F0.wireOp",EDGE,"E125"),sQuery(id+"F0.wireOp",EDGE,"E126"),sQuery(id+"F0.wireOp",EDGE,"E127"),sQuery(id+"F0.wireOp",EDGE,"E128"),sQuery(id+"F0.wireOp",EDGE,"E129"),sQuery(id+"F0.wireOp",EDGE,"E130"),sQuery(id+"F0.wireOp",EDGE,"E131"),sQuery(id+"F0.wireOp",EDGE,"E132"),sQuery(id+"F0.wireOp",EDGE,"E133"),sQuery(id+"F0.wireOp",EDGE,"E134"),sQuery(id+"F0.wireOp",EDGE,"E135"),sQuery(id+"F0.wireOp",EDGE,"E136"),sQuery(id+"F0.wireOp",EDGE,"E137"),sQuery(id+"F0.wireOp",EDGE,"E138"),sQuery(id+"F0.wireOp",EDGE,"E139"),sQuery(id+"F0.wireOp",EDGE,"E140"),sQuery(id+"F0.wireOp",EDGE,"E141"),sQuery(id+"F0.wireOp",EDGE,"E142"),sQuery(id+"F0.wireOp",EDGE,"E143"),sQuery(id+"F0.wireOp",EDGE,"E144"),sQuery(id+"F0.wireOp",EDGE,"E145"),sQuery(id+"F0.wireOp",EDGE,"E146"),sQuery(id+"F0.wireOp",EDGE,"E147"),sQuery(id+"F0.wireOp",EDGE,"E148"),sQuery(id+"F0.wireOp",EDGE,"E149"),sQuery(id+"F0.wireOp",EDGE,"E150"),sQuery(id+"F0.wireOp",EDGE,"E151"),sQuery(id+"F0.wireOp",EDGE,"E152"),sQuery(id+"F0.wireOp",EDGE,"E153"),sQuery(id+"F0.wireOp",EDGE,"E154"),sQuery(id+"F0.wireOp",EDGE,"E155"),sQuery(id+"F0.wireOp",EDGE,"E156"),sQuery(id+"F0.wireOp",EDGE,"E157"),sQuery(id+"F0.wireOp",EDGE,"E158"),sQuery(id+"F0.wireOp",EDGE,"E159"),sQuery(id+"F0.wireOp",EDGE,"E160"),sQuery(id+"F0.wireOp",EDGE,"E161"),sQuery(id+"F0.wireOp",EDGE,"E162"),sQuery(id+"F0.wireOp",EDGE,"E163"),sQuery(id+"F0.wireOp",EDGE,"E164"),sQuery(id+"F0.wireOp",EDGE,"E165"),sQuery(id+"F0.wireOp",EDGE,"E166"),sQuery(id+"F0.wireOp",EDGE,"E167"),sQuery(id+"F0.wireOp",EDGE,"E168"),sQuery(id+"F0.wireOp",EDGE,"E169"),sQuery(id+"F0.wireOp",EDGE,"E170"),sQuery(id+"F0.wireOp",EDGE,"E171"),sQuery(id+"F0.wireOp",EDGE,"E172"),sQuery(id+"F0.wireOp",EDGE,"E173"),sQuery(id+"F0.wireOp",EDGE,"E174"),sQuery(id+"F0.wireOp",EDGE,"E175"),sQuery(id+"F0.wireOp",EDGE,"E176"),sQuery(id+"F0.wireOp",EDGE,"E177"),sQuery(id+"F0.wireOp",EDGE,"E178"),sQuery(id+"F0.wireOp",EDGE,"E179"),sQuery(id+"F0.wireOp",EDGE,"E180"),sQuery(id+"F0.wireOp",EDGE,"E181"),sQuery(id+"F0.wireOp",EDGE,"E182"),sQuery(id+"F0.wireOp",EDGE,"E183"),sQuery(id+"F0.wireOp",EDGE,"E184"),sQuery(id+"F0.wireOp",EDGE,"E185"),sQuery(id+"F0.wireOp",EDGE,"E186"),sQuery(id+"F0.wireOp",EDGE,"E187"),sQuery(id+"F0.wireOp",EDGE,"E188"),sQuery(id+"F0.wireOp",EDGE,"E189"),sQuery(id+"F0.wireOp",EDGE,"E190"),sQuery(id+"F0.wireOp",EDGE,"E191"),sQuery(id+"F0.wireOp",EDGE,"E192"),sQuery(id+"F0.wireOp",EDGE,"E193"),sQuery(id+"F0.wireOp",EDGE,"E194"),sQuery(id+"F0.wireOp",EDGE,"E195"),sQuery(id+"F0.wireOp",EDGE,"E196"),sQuery(id+"F0.wireOp",EDGE,"E197"),sQuery(id+"F0.wireOp",EDGE,"E198"),sQuery(id+"F0.wireOp",EDGE,"E199"),sQuery(id+"F0.wireOp",EDGE,"E200"),sQuery(id+"F0.wireOp",EDGE,"E201"),sQuery(id+"F0.wireOp",EDGE,"E202"),sQuery(id+"F0.wireOp",EDGE,"E203"),sQuery(id+"F0.wireOp",EDGE,"E204"),sQuery(id+"F0.wireOp",EDGE,"E205"),sQuery(id+"F0.wireOp",EDGE,"E206"),sQuery(id+"F0.wireOp",EDGE,"E207"),sQuery(id+"F0.wireOp",EDGE,"E208"),sQuery(id+"F0.wireOp",EDGE,"E209"),sQuery(id+"F0.wireOp",EDGE,"E210"),sQuery(id+"F0.wireOp",EDGE,"E211"),sQuery(id+"F0.wireOp",EDGE,"E212"),sQuery(id+"F0.wireOp",EDGE,"E213"),sQuery(id+"F0.wireOp",EDGE,"E214"),sQuery(id+"F0.wireOp",EDGE,"E215"),sQuery(id+"F0.wireOp",EDGE,"E216"),sQuery(id+"F0.wireOp",EDGE,"E217"),sQuery(id+"F0.wireOp",EDGE,"E218"),sQuery(id+"F0.wireOp",EDGE,"E219"),sQuery(id+"F0.wireOp",EDGE,"E220"),sQuery(id+"F0.wireOp",EDGE,"E221"),sQuery(id+"F0.wireOp",EDGE,"E222"),sQuery(id+"F0.wireOp",EDGE,"E223"),sQuery(id+"F0.wireOp",EDGE,"E224"),sQuery(id+"F0.wireOp",EDGE,"E225"),sQuery(id+"F0.wireOp",EDGE,"E226"),sQuery(id+"F0.wireOp",EDGE,"E227"),sQuery(id+"F0.wireOp",EDGE,"E228"),sQuery(id+"F0.wireOp",EDGE,"E229"),sQuery(id+"F0.wireOp",EDGE,"E230"),sQuery(id+"F0.wireOp",EDGE,"E231"),sQuery(id+"F0.wireOp",EDGE,"E232"),sQuery(id+"F0.wireOp",EDGE,"E233"),sQuery(id+"F0.wireOp",EDGE,"E234"),sQuery(id+"F0.wireOp",EDGE,"E235"),sQuery(id+"F0.wireOp",EDGE,"E236"),sQuery(id+"F0.wireOp",EDGE,"E237"),sQuery(id+"F0.wireOp",EDGE,"E238"),sQuery(id+"F0.wireOp",EDGE,"E239"),sQuery(id+"F0.wireOp",EDGE,"E240"),sQuery(id+"F0.wireOp",EDGE,"E241"),sQuery(id+"F0.wireOp",EDGE,"E242"),sQuery(id+"F0.wireOp",EDGE,"E243"),sQuery(id+"F0.wireOp",EDGE,"E244"),sQuery(id+"F0.wireOp",EDGE,"E245"),sQuery(id+"F0.wireOp",EDGE,"E246"),sQuery(id+"F0.wireOp",EDGE,"E247"),sQuery(id+"F0.wireOp",EDGE,"E248"),sQuery(id+"F0.wireOp",EDGE,"E249"),sQuery(id+"F0.wireOp",EDGE,"E250"),sQuery(id+"F0.wireOp",EDGE,"E251"),sQuery(id+"F0.wireOp",EDGE,"E252"),sQuery(id+"F0.wireOp",EDGE,"E253"),sQuery(id+"F0.wireOp",EDGE,"E254"),sQuery(id+"F0.wireOp",EDGE,"E255"),sQuery(id+"F0.wireOp",EDGE,"E256"),sQuery(id+"F0.wireOp",EDGE,"E257"),sQuery(id+"F0.wireOp",EDGE,"E258"),sQuery(id+"F0.wireOp",EDGE,"E259"),sQuery(id+"F0.wireOp",EDGE,"E260"),sQuery(id+"F0.wireOp",EDGE,"E261"),sQuery(id+"F0.wireOp",EDGE,"E262"),sQuery(id+"F0.wireOp",EDGE,"E263"),sQuery(id+"F0.wireOp",EDGE,"E264"),sQuery(id+"F0.wireOp",EDGE,"E265"),sQuery(id+"F0.wireOp",EDGE,"E266"),sQuery(id+"F0.wireOp",EDGE,"E267"),sQuery(id+"F0.wireOp",EDGE,"E268"),sQuery(id+"F0.wireOp",EDGE,"E269"),sQuery(id+"F0.wireOp",EDGE,"E270"),sQuery(id+"F0.wireOp",EDGE,"E271"),sQuery(id+"F0.wireOp",EDGE,"E272"),sQuery(id+"F0.wireOp",EDGE,"E273"),sQuery(id+"F0.wireOp",EDGE,"E274"),sQuery(id+"F0.wireOp",EDGE,"E275"),sQuery(id+"F0.wireOp",EDGE,"E276"),sQuery(id+"F0.wireOp",EDGE,"E277"),sQuery(id+"F0.wireOp",EDGE,"E278"),sQuery(id+"F0.wireOp",EDGE,"E279"),sQuery(id+"F0.wireOp",EDGE,"E280"),sQuery(id+"F0.wireOp",EDGE,"E281"),sQuery(id+"F0.wireOp",EDGE,"E282"),sQuery(id+"F0.wireOp",EDGE,"E283"),sQuery(id+"F0.wireOp",EDGE,"E284"),sQuery(id+"F0.wireOp",EDGE,"E285"),sQuery(id+"F0.wireOp",EDGE,"E286"),sQuery(id+"F0.wireOp",EDGE,"E287"),sQuery(id+"F0.wireOp",EDGE,"E288"),sQuery(id+"F0.wireOp",EDGE,"E289"),sQuery(id+"F0.wireOp",EDGE,"E290"),sQuery(id+"F0.wireOp",EDGE,"E291"),sQuery(id+"F0.wireOp",EDGE,"E292"),sQuery(id+"F0.wireOp",EDGE,"E293"),sQuery(id+"F0.wireOp",EDGE,"E294"),sQuery(id+"F0.wireOp",EDGE,"E295"),sQuery(id+"F0.wireOp",EDGE,"E296"),sQuery(id+"F0.wireOp",EDGE,"E297"),sQuery(id+"F0.wireOp",EDGE,"E298"),sQuery(id+"F0.wireOp",EDGE,"E299"),sQuery(id+"F0.wireOp",EDGE,"E300"),sQuery(id+"F0.wireOp",EDGE,"E301"),sQuery(id+"F0.wireOp",EDGE,"E302"),sQuery(id+"F0.wireOp",EDGE,"E303"),sQuery(id+"F0.wireOp",EDGE,"E304"),sQuery(id+"F0.wireOp",EDGE,"E305"),sQuery(id+"F0.wireOp",EDGE,"E306"),sQuery(id+"F0.wireOp",EDGE,"E307"),sQuery(id+"F0.wireOp",EDGE,"E308"),sQuery(id+"F0.wireOp",EDGE,"E309"),sQuery(id+"F0.wireOp",EDGE,"E310"),sQuery(id+"F0.wireOp",EDGE,"E311"),sQuery(id+"F0.wireOp",EDGE,"E312"),sQuery(id+"F0.wireOp",EDGE,"E313"),sQuery(id+"F0.wireOp",EDGE,"E314"),sQuery(id+"F0.wireOp",EDGE,"E315"),sQuery(id+"F0.wireOp",EDGE,"E316"),sQuery(id+"F0.wireOp",EDGE,"E317"),sQuery(id+"F0.wireOp",EDGE,"E318"),sQuery(id+"F0.wireOp",EDGE,"E319"),sQuery(id+"F0.wireOp",EDGE,"E320"),sQuery(id+"F0.wireOp",EDGE,"E321"),sQuery(id+"F0.wireOp",EDGE,"E322"),sQuery(id+"F0.wireOp",EDGE,"E323"),sQuery(id+"F0.wireOp",EDGE,"E324"),sQuery(id+"F0.wireOp",EDGE,"E325"),sQuery(id+"F0.wireOp",EDGE,"E326"),sQuery(id+"F0.wireOp",EDGE,"E327"),sQuery(id+"F0.wireOp",EDGE,"E328"),sQuery(id+"F0.wireOp",EDGE,"E329"),sQuery(id+"F0.wireOp",EDGE,"E330"),sQuery(id+"F0.wireOp",EDGE,"E331"),sQuery(id+"F0.wireOp",EDGE,"E332"),sQuery(id+"F0.wireOp",EDGE,"E333"),sQuery(id+"F0.wireOp",EDGE,"E334"),sQuery(id+"F0.wireOp",EDGE,"E335"),sQuery(id+"F0.wireOp",EDGE,"E336"),sQuery(id+"F0.wireOp",EDGE,"E337"),sQuery(id+"F0.wireOp",EDGE,"E338"),sQuery(id+"F0.wireOp",EDGE,"E339"),sQuery(id+"F0.wireOp",EDGE,"E340"),sQuery(id+"F0.wireOp",EDGE,"E341"),sQuery(id+"F0.wireOp",EDGE,"E342"),sQuery(id+"F0.wireOp",EDGE,"E343"),sQuery(id+"F0.wireOp",EDGE,"E344"),sQuery(id+"F0.wireOp",EDGE,"E345"),sQuery(id+"F0.wireOp",EDGE,"E346"),sQuery(id+"F0.wireOp",EDGE,"E347"),sQuery(id+"F0.wireOp",EDGE,"E348"),sQuery(id+"F0.wireOp",EDGE,"E349"),sQuery(id+"F0.wireOp",EDGE,"E350"),sQuery(id+"F0.wireOp",EDGE,"E351"),sQuery(id+"F0.wireOp",EDGE,"E352"),sQuery(id+"F0.wireOp",EDGE,"E353"),sQuery(id+"F0.wireOp",EDGE,"E354"),sQuery(id+"F0.wireOp",EDGE,"E355"),sQuery(id+"F0.wireOp",EDGE,"E356"),sQuery(id+"F0.wireOp",EDGE,"E357"),sQuery(id+"F0.wireOp",EDGE,"E358"),sQuery(id+"F0.wireOp",EDGE,"E359"),sQuery(id+"F0.wireOp",EDGE,"E360"),sQuery(id+"F0.wireOp",EDGE,"E361"),sQuery(id+"F0.wireOp",EDGE,"E362"),sQuery(id+"F0.wireOp",EDGE,"E363"),sQuery(id+"F0.wireOp",EDGE,"E364"),sQuery(id+"F0.wireOp",EDGE,"E365"),sQuery(id+"F0.wireOp",EDGE,"E366"),sQuery(id+"F0.wireOp",EDGE,"E367"),sQuery(id+"F0.wireOp",EDGE,"E368"),sQuery(id+"F0.wireOp",EDGE,"E369"),sQuery(id+"F0.wireOp",EDGE,"E370"),sQuery(id+"F0.wireOp",EDGE,"E371"),sQuery(id+"F0.wireOp",EDGE,"E372"),sQuery(id+"F0.wireOp",EDGE,"E373"),sQuery(id+"F0.wireOp",EDGE,"E374"),sQuery(id+"F0.wireOp",EDGE,"E375"),sQuery(id+"F0.wireOp",EDGE,"E376"),sQuery(id+"F0.wireOp",EDGE,"E377"),sQuery(id+"F0.wireOp",EDGE,"E378"),sQuery(id+"F0.wireOp",EDGE,"E379"),sQuery(id+"F0.wireOp",EDGE,"E380"),sQuery(id+"F0.wireOp",EDGE,"E381"),sQuery(id+"F0.wireOp",EDGE,"E382"),sQuery(id+"F0.wireOp",EDGE,"E383"),sQuery(id+"F0.wireOp",EDGE,"E384"),sQuery(id+"F0.wireOp",EDGE,"E385"),sQuery(id+"F0.wireOp",EDGE,"E386"),sQuery(id+"F0.wireOp",EDGE,"E387"),sQuery(id+"F0.wireOp",EDGE,"E388"),sQuery(id+"F0.wireOp",EDGE,"E389"),sQuery(id+"F0.wireOp",EDGE,"E390"),sQuery(id+"F0.wireOp",EDGE,"E391"),sQuery(id+"F0.wireOp",EDGE,"E392"),sQuery(id+"F0.wireOp",EDGE,"E393"),sQuery(id+"F0.wireOp",EDGE,"E394"),sQuery(id+"F0.wireOp",EDGE,"E395"),sQuery(id+"F0.wireOp",EDGE,"E396"),sQuery(id+"F0.wireOp",EDGE,"E397"),sQuery(id+"F0.wireOp",EDGE,"E398"),sQuery(id+"F0.wireOp",EDGE,"E399"),sQuery(id+"F0.wireOp",EDGE,"E400"),sQuery(id+"F0.wireOp",EDGE,"E401"),sQuery(id+"F0.wireOp",EDGE,"E402"),sQuery(id+"F0.wireOp",EDGE,"E403"),sQuery(id+"F0.wireOp",EDGE,"E404"),sQuery(id+"F0.wireOp",EDGE,"E405"),sQuery(id+"F0.wireOp",EDGE,"E406"),sQuery(id+"F0.wireOp",EDGE,"E407"),sQuery(id+"F0.wireOp",EDGE,"E408"),sQuery(id+"F0.wireOp",EDGE,"E409"),sQuery(id+"F0.wireOp",EDGE,"E410"),sQuery(id+"F0.wireOp",EDGE,"E411"),sQuery(id+"F0.wireOp",EDGE,"E412"),sQuery(id+"F0.wireOp",EDGE,"E413"),sQuery(id+"F0.wireOp",EDGE,"E414"),sQuery(id+"F0.wireOp",EDGE,"E415"),sQuery(id+"F0.wireOp",EDGE,"E416"),sQuery(id+"F0.wireOp",EDGE,"E417"),sQuery(id+"F0.wireOp",EDGE,"E418"),sQuery(id+"F0.wireOp",EDGE,"E419"),sQuery(id+"F0.wireOp",EDGE,"E420"),sQuery(id+"F0.wireOp",EDGE,"E421"),sQuery(id+"F0.wireOp",EDGE,"E422"),sQuery(id+"F0.wireOp",EDGE,"E423"),sQuery(id+"F0.wireOp",EDGE,"E424"),sQuery(id+"F0.wireOp",EDGE,"E425"),sQuery(id+"F0.wireOp",EDGE,"E426"),sQuery(id+"F0.wireOp",EDGE,"E427"),sQuery(id+"F0.wireOp",EDGE,"E428"),sQuery(id+"F0.wireOp",EDGE,"E429"),sQuery(id+"F0.wireOp",EDGE,"E430"),sQuery(id+"F0.wireOp",EDGE,"E431"),sQuery(id+"F0.wireOp",EDGE,"E432"),sQuery(id+"F0.wireOp",EDGE,"E433"),sQuery(id+"F0.wireOp",EDGE,"E434"),sQuery(id+"F0.wireOp",EDGE,"E435"),sQuery(id+"F0.wireOp",EDGE,"E436"),sQuery(id+"F0.wireOp",EDGE,"E437"),sQuery(id+"F0.wireOp",EDGE,"E438"),sQuery(id+"F0.wireOp",EDGE,"E439"),sQuery(id+"F0.wireOp",EDGE,"E440"),sQuery(id+"F0.wireOp",EDGE,"E441"),sQuery(id+"F0.wireOp",EDGE,"E442"),sQuery(id+"F0.wireOp",EDGE,"E443"),sQuery(id+"F0.wireOp",EDGE,"E444"),sQuery(id+"F0.wireOp",EDGE,"E445"),sQuery(id+"F0.wireOp",EDGE,"E446"),sQuery(id+"F0.wireOp",EDGE,"E447"),sQuery(id+"F0.wireOp",EDGE,"E448"),sQuery(id+"F0.wireOp",EDGE,"E449"),sQuery(id+"F0.wireOp",EDGE,"E450"),sQuery(id+"F0.wireOp",EDGE,"E451"),sQuery(id+"F0.wireOp",EDGE,"E452"),sQuery(id+"F0.wireOp",EDGE,"E453"),sQuery(id+"F0.wireOp",EDGE,"E454"),sQuery(id+"F0.wireOp",EDGE,"E455"),sQuery(id+"F0.wireOp",EDGE,"E456"),sQuery(id+"F0.wireOp",EDGE,"E457"),sQuery(id+"F0.wireOp",EDGE,"E458"),sQuery(id+"F0.wireOp",EDGE,"E459"),sQuery(id+"F0.wireOp",EDGE,"E460"),sQuery(id+"F0.wireOp",EDGE,"E461"),sQuery(id+"F0.wireOp",EDGE,"E462"),sQuery(id+"F0.wireOp",EDGE,"E463"),sQuery(id+"F0.wireOp",EDGE,"E464"),sQuery(id+"F0.wireOp",EDGE,"E465"),sQuery(id+"F0.wireOp",EDGE,"E466"),sQuery(id+"F0.wireOp",EDGE,"E467"),sQuery(id+"F0.wireOp",EDGE,"E468"),sQuery(id+"F0.wireOp",EDGE,"E469"),sQuery(id+"F0.wireOp",EDGE,"E470"),sQuery(id+"F0.wireOp",EDGE,"E471"),sQuery(id+"F0.wireOp",EDGE,"E472"),sQuery(id+"F0.wireOp",EDGE,"E473"),sQuery(id+"F0.wireOp",EDGE,"E474"),sQuery(id+"F0.wireOp",EDGE,"E475"),sQuery(id+"F0.wireOp",EDGE,"E476"),sQuery(id+"F0.wireOp",EDGE,"E477"),sQuery(id+"F0.wireOp",EDGE,"E478"),sQuery(id+"F0.wireOp",EDGE,"E479"),sQuery(id+"F0.wireOp",EDGE,"E480"),sQuery(id+"F0.wireOp",EDGE,"E481"),sQuery(id+"F0.wireOp",EDGE,"E482"),sQuery(id+"F0.wireOp",EDGE,"E483"),sQuery(id+"F0.wireOp",EDGE,"E484"),sQuery(id+"F0.wireOp",EDGE,"E485"),sQuery(id+"F0.wireOp",EDGE,"E486"),sQuery(id+"F0.wireOp",EDGE,"E487"),sQuery(id+"F0.wireOp",EDGE,"E488"),sQuery(id+"F0.wireOp",EDGE,"E489"),sQuery(id+"F0.wireOp",EDGE,"E490"),sQuery(id+"F0.wireOp",EDGE,"E491"),sQuery(id+"F0.wireOp",EDGE,"E492"),sQuery(id+"F0.wireOp",EDGE,"E493"),sQuery(id+"F0.wireOp",EDGE,"E494"),sQuery(id+"F0.wireOp",EDGE,"E495"),sQuery(id+"F0.wireOp",EDGE,"E496"),sQuery(id+"F0.wireOp",EDGE,"E497"),sQuery(id+"F0.wireOp",EDGE,"E498"),sQuery(id+"F0.wireOp",EDGE,"E499"),sQuery(id+"F0.wireOp",EDGE,"E500"),sQuery(id+"F0.wireOp",EDGE,"E501"),sQuery(id+"F0.wireOp",EDGE,"E502"),sQuery(id+"F0.wireOp",EDGE,"E503"),sQuery(id+"F0.wireOp",EDGE,"E504"),sQuery(id+"F0.wireOp",EDGE,"E505"),sQuery(id+"F0.wireOp",EDGE,"E506"),sQuery(id+"F0.wireOp",EDGE,"E507"),sQuery(id+"F0.wireOp",EDGE,"E508"),sQuery(id+"F0.wireOp",EDGE,"E509"),sQuery(id+"F0.wireOp",EDGE,"E510"),sQuery(id+"F0.wireOp",EDGE,"E511"),sQuery(id+"F0.wireOp",EDGE,"E512"),sQuery(id+"F0.wireOp",EDGE,"E513"),sQuery(id+"F0.wireOp",EDGE,"E514"),sQuery(id+"F0.wireOp",EDGE,"E515"),sQuery(id+"F0.wireOp",EDGE,"E516"),sQuery(id+"F0.wireOp",EDGE,"E517"),sQuery(id+"F0.wireOp",EDGE,"E518"),sQuery(id+"F0.wireOp",EDGE,"E519"),sQuery(id+"F0.wireOp",EDGE,"E520"),sQuery(id+"F0.wireOp",EDGE,"E521"),sQuery(id+"F0.wireOp",EDGE,"E522"),sQuery(id+"F0.wireOp",EDGE,"E523"),sQuery(id+"F0.wireOp",EDGE,"E524"),sQuery(id+"F0.wireOp",EDGE,"E525"),sQuery(id+"F0.wireOp",EDGE,"E526"),sQuery(id+"F0.wireOp",EDGE,"E527"),sQuery(id+"F0.wireOp",EDGE,"E528"),sQuery(id+"F0.wireOp",EDGE,"E529"),sQuery(id+"F0.wireOp",EDGE,"E530"),sQuery(id+"F0.wireOp",EDGE,"E531"),sQuery(id+"F0.wireOp",EDGE,"E532"),sQuery(id+"F0.wireOp",EDGE,"E533"),sQuery(id+"F0.wireOp",EDGE,"E534"),sQuery(id+"F0.wireOp",EDGE,"E535"),sQuery(id+"F0.wireOp",EDGE,"E536"),sQuery(id+"F0.wireOp",EDGE,"E537"),sQuery(id+"F0.wireOp",EDGE,"E538"),sQuery(id+"F0.wireOp",EDGE,"E539"),sQuery(id+"F0.wireOp",EDGE,"E540"),sQuery(id+"F0.wireOp",EDGE,"E541"),sQuery(id+"F0.wireOp",EDGE,"E542"),sQuery(id+"F0.wireOp",EDGE,"E543"),sQuery(id+"F0.wireOp",EDGE,"E544"),sQuery(id+"F0.wireOp",EDGE,"E545"),sQuery(id+"F0.wireOp",EDGE,"E546"),sQuery(id+"F0.wireOp",EDGE,"E547"),sQuery(id+"F0.wireOp",EDGE,"E548"),sQuery(id+"F0.wireOp",EDGE,"E549"),sQuery(id+"F0.wireOp",EDGE,"E550"),sQuery(id+"F0.wireOp",EDGE,"E551"),sQuery(id+"F0.wireOp",EDGE,"E552"),sQuery(id+"F0.wireOp",EDGE,"E553"),sQuery(id+"F0.wireOp",EDGE,"E554"),sQuery(id+"F0.wireOp",EDGE,"E555"),sQuery(id+"F0.wireOp",EDGE,"E556"),sQuery(id+"F0.wireOp",EDGE,"E557"),sQuery(id+"F0.wireOp",EDGE,"E558"),sQuery(id+"F0.wireOp",EDGE,"E559"),sQuery(id+"F0.wireOp",EDGE,"E560"),sQuery(id+"F0.wireOp",EDGE,"E561"),sQuery(id+"F0.wireOp",EDGE,"E562"),sQuery(id+"F0.wireOp",EDGE,"E563"),sQuery(id+"F0.wireOp",EDGE,"E564"),sQuery(id+"F0.wireOp",EDGE,"E565"),sQuery(id+"F0.wireOp",EDGE,"E566"),sQuery(id+"F0.wireOp",EDGE,"E567"),sQuery(id+"F0.wireOp",EDGE,"E568"),sQuery(id+"F0.wireOp",EDGE,"E569"),sQuery(id+"F0.wireOp",EDGE,"E570"),sQuery(id+"F0.wireOp",EDGE,"E571"),sQuery(id+"F0.wireOp",EDGE,"E572"),sQuery(id+"F0.wireOp",EDGE,"E573"),sQuery(id+"F0.wireOp",EDGE,"E574"),sQuery(id+"F0.wireOp",EDGE,"E575"),sQuery(id+"F0.wireOp",EDGE,"E576"),sQuery(id+"F0.wireOp",EDGE,"E577"),sQuery(id+"F0.wireOp",EDGE,"E578"),sQuery(id+"F0.wireOp",EDGE,"E579"),sQuery(id+"F0.wireOp",EDGE,"E580"),sQuery(id+"F0.wireOp",EDGE,"E581"),sQuery(id+"F0.wireOp",EDGE,"E582"),sQuery(id+"F0.wireOp",EDGE,"E583"),sQuery(id+"F0.wireOp",EDGE,"E584"),sQuery(id+"F0.wireOp",EDGE,"E585"),sQuery(id+"F0.wireOp",EDGE,"E586"),sQuery(id+"F0.wireOp",EDGE,"E587"),sQuery(id+"F0.wireOp",EDGE,"E588"),sQuery(id+"F0.wireOp",EDGE,"E589"),sQuery(id+"F0.wireOp",EDGE,"E590"),sQuery(id+"F0.wireOp",EDGE,"E591"),sQuery(id+"F0.wireOp",EDGE,"E592"),sQuery(id+"F0.wireOp",EDGE,"E593"),sQuery(id+"F0.wireOp",EDGE,"E594"),sQuery(id+"F0.wireOp",EDGE,"E595"),sQuery(id+"F0.wireOp",EDGE,"E596"),sQuery(id+"F0.wireOp",EDGE,"E597"),sQuery(id+"F0.wireOp",EDGE,"E598"),sQuery(id+"F0.wireOp",EDGE,"E599"),sQuery(id+"F0.wireOp",EDGE,"E600"),sQuery(id+"F0.wireOp",EDGE,"E601"),sQuery(id+"F0.wireOp",EDGE,"E602"),sQuery(id+"F0.wireOp",EDGE,"E603"),sQuery(id+"F0.wireOp",EDGE,"E604"),sQuery(id+"F0.wireOp",EDGE,"E605"),sQuery(id+"F0.wireOp",EDGE,"E606"),sQuery(id+"F0.wireOp",EDGE,"E607"),sQuery(id+"F0.wireOp",EDGE,"E608"),sQuery(id+"F0.wireOp",EDGE,"E609"),sQuery(id+"F0.wireOp",EDGE,"E610"),sQuery(id+"F0.wireOp",EDGE,"E611"),sQuery(id+"F0.wireOp",EDGE,"E612"),sQuery(id+"F0.wireOp",EDGE,"E613"),sQuery(id+"F0.wireOp",EDGE,"E614"),sQuery(id+"F0.wireOp",EDGE,"E615"),sQuery(id+"F0.wireOp",EDGE,"E616"),sQuery(id+"F0.wireOp",EDGE,"E617"),sQuery(id+"F0.wireOp",EDGE,"E618"),sQuery(id+"F0.wireOp",EDGE,"E619"),sQuery(id+"F0.wireOp",EDGE,"E620"),sQuery(id+"F0.wireOp",EDGE,"E621"),sQuery(id+"F0.wireOp",EDGE,"E622"),sQuery(id+"F0.wireOp",EDGE,"E623"),sQuery(id+"F0.wireOp",EDGE,"E624"),sQuery(id+"F0.wireOp",EDGE,"E625"),sQuery(id+"F0.wireOp",EDGE,"E626"),sQuery(id+"F0.wireOp",EDGE,"E627"),sQuery(id+"F0.wireOp",EDGE,"E628"),sQuery(id+"F0.wireOp",EDGE,"E629"),sQuery(id+"F0.wireOp",EDGE,"E630"),sQuery(id+"F0.wireOp",EDGE,"E631"),sQuery(id+"F0.wireOp",EDGE,"E632"),sQuery(id+"F0.wireOp",EDGE,"E633"),sQuery(id+"F0.wireOp",EDGE,"E634"),sQuery(id+"F0.wireOp",EDGE,"E635"),sQuery(id+"F0.wireOp",EDGE,"E636"),sQuery(id+"F0.wireOp",EDGE,"E637"),sQuery(id+"F0.wireOp",EDGE,"E638"),sQuery(id+"F0.wireOp",EDGE,"E639"),sQuery(id+"F0.wireOp",EDGE,"E640"),sQuery(id+"F0.wireOp",EDGE,"E641"),sQuery(id+"F0.wireOp",EDGE,"E642"),sQuery(id+"F0.wireOp",EDGE,"E643"),sQuery(id+"F0.wireOp",EDGE,"E644"),sQuery(id+"F0.wireOp",EDGE,"E645"),sQuery(id+"F0.wireOp",EDGE,"E646"),sQuery(id+"F0.wireOp",EDGE,"E647"),sQuery(id+"F0.wireOp",EDGE,"E648"),sQuery(id+"F0.wireOp",EDGE,"E649"),sQuery(id+"F0.wireOp",EDGE,"E650"),sQuery(id+"F0.wireOp",EDGE,"E651"),sQuery(id+"F0.wireOp",EDGE,"E652"),sQuery(id+"F0.wireOp",EDGE,"E653"),sQuery(id+"F0.wireOp",EDGE,"E654"),sQuery(id+"F0.wireOp",EDGE,"E655"),sQuery(id+"F0.wireOp",EDGE,"E656"),sQuery(id+"F0.wireOp",EDGE,"E657"),sQuery(id+"F0.wireOp",EDGE,"E658"),sQuery(id+"F0.wireOp",EDGE,"E659"),sQuery(id+"F0.wireOp",EDGE,"E660"),sQuery(id+"F0.wireOp",EDGE,"E661"),sQuery(id+"F0.wireOp",EDGE,"E662"),sQuery(id+"F0.wireOp",EDGE,"E663"),sQuery(id+"F0.wireOp",EDGE,"E664"),sQuery(id+"F0.wireOp",EDGE,"E665"),sQuery(id+"F0.wireOp",EDGE,"E666"),sQuery(id+"F0.wireOp",EDGE,"E667"),sQuery(id+"F0.wireOp",EDGE,"E668"),sQuery(id+"F0.wireOp",EDGE,"E669"),sQuery(id+"F0.wireOp",EDGE,"E670"),sQuery(id+"F0.wireOp",EDGE,"E671"),sQuery(id+"F0.wireOp",EDGE,"E672"),sQuery(id+"F0.wireOp",EDGE,"E673"),sQuery(id+"F0.wireOp",EDGE,"E674"),sQuery(id+"F0.wireOp",EDGE,"E675"),sQuery(id+"F0.wireOp",EDGE,"E676"),sQuery(id+"F0.wireOp",EDGE,"E677"),sQuery(id+"F0.wireOp",EDGE,"E678"),sQuery(id+"F0.wireOp",EDGE,"E679"),sQuery(id+"F0.wireOp",EDGE,"E680"),sQuery(id+"F0.wireOp",EDGE,"E681"),sQuery(id+"F0.wireOp",EDGE,"E682"),sQuery(id+"F0.wireOp",EDGE,"E683"),sQuery(id+"F0.wireOp",EDGE,"E684"),sQuery(id+"F0.wireOp",EDGE,"E685"),sQuery(id+"F0.wireOp",EDGE,"E686"),sQuery(id+"F0.wireOp",EDGE,"E687"),sQuery(id+"F0.wireOp",EDGE,"E688"),sQuery(id+"F0.wireOp",EDGE,"E689"),sQuery(id+"F0.wireOp",EDGE,"E690"),sQuery(id+"F0.wireOp",EDGE,"E691"),sQuery(id+"F0.wireOp",EDGE,"E692"),sQuery(id+"F0.wireOp",EDGE,"E693"),sQuery(id+"F0.wireOp",EDGE,"E694"),sQuery(id+"F0.wireOp",EDGE,"E695"),sQuery(id+"F0.wireOp",EDGE,"E696"),sQuery(id+"F0.wireOp",EDGE,"E697"),sQuery(id+"F0.wireOp",EDGE,"E698"),sQuery(id+"F0.wireOp",EDGE,"E699"),sQuery(id+"F0.wireOp",EDGE,"E700"),sQuery(id+"F0.wireOp",EDGE,"E701"),sQuery(id+"F0.wireOp",EDGE,"E702"),sQuery(id+"F0.wireOp",EDGE,"E703"),sQuery(id+"F0.wireOp",EDGE,"E704"),sQuery(id+"F0.wireOp",EDGE,"E705"),sQuery(id+"F0.wireOp",EDGE,"E706"),sQuery(id+"F0.wireOp",EDGE,"E707"),sQuery(id+"F0.wireOp",EDGE,"E708"),sQuery(id+"F0.wireOp",EDGE,"E709"),sQuery(id+"F0.wireOp",EDGE,"E710"),sQuery(id+"F0.wireOp",EDGE,"E711"),sQuery(id+"F0.wireOp",EDGE,"E712"),sQuery(id+"F0.wireOp",EDGE,"E713"),sQuery(id+"F0.wireOp",EDGE,"E714"),sQuery(id+"F0.wireOp",EDGE,"E715"),sQuery(id+"F0.wireOp",EDGE,"E716"),sQuery(id+"F0.wireOp",EDGE,"E717"),sQuery(id+"F0.wireOp",EDGE,"E718"),sQuery(id+"F0.wireOp",EDGE,"E719"),sQuery(id+"F0.wireOp",EDGE,"E720"),sQuery(id+"F0.wireOp",EDGE,"E721"),sQuery(id+"F0.wireOp",EDGE,"E722"),sQuery(id+"F0.wireOp",EDGE,"E723"),sQuery(id+"F0.wireOp",EDGE,"E724"),sQuery(id+"F0.wireOp",EDGE,"E725"),sQuery(id+"F0.wireOp",EDGE,"E726"),sQuery(id+"F0.wireOp",EDGE,"E727"),sQuery(id+"F0.wireOp",EDGE,"E728"),sQuery(id+"F0.wireOp",EDGE,"E729"),sQuery(id+"F0.wireOp",EDGE,"E730"),sQuery(id+"F0.wireOp",EDGE,"E731"),sQuery(id+"F0.wireOp",EDGE,"E732"),sQuery(id+"F0.wireOp",EDGE,"E733"),sQuery(id+"F0.wireOp",EDGE,"E734"),sQuery(id+"F0.wireOp",EDGE,"E735"),sQuery(id+"F0.wireOp",EDGE,"E736"),sQuery(id+"F0.wireOp",EDGE,"E737"),sQuery(id+"F0.wireOp",EDGE,"E738"),sQuery(id+"F0.wireOp",EDGE,"E739"),sQuery(id+"F0.wireOp",EDGE,"E740"),sQuery(id+"F0.wireOp",EDGE,"E741"),sQuery(id+"F0.wireOp",EDGE,"E742"),sQuery(id+"F0.wireOp",EDGE,"E743"),sQuery(id+"F0.wireOp",EDGE,"E744"),sQuery(id+"F0.wireOp",EDGE,"E745"),sQuery(id+"F0.wireOp",EDGE,"E746"),sQuery(id+"F0.wireOp",EDGE,"E747"),sQuery(id+"F0.wireOp",EDGE,"E748"),sQuery(id+"F0.wireOp",EDGE,"E749"),sQuery(id+"F0.wireOp",EDGE,"E750"),sQuery(id+"F0.wireOp",EDGE,"E751"),sQuery(id+"F0.wireOp",EDGE,"E752"),sQuery(id+"F0.wireOp",EDGE,"E753"),sQuery(id+"F0.wireOp",EDGE,"E754"),sQuery(id+"F0.wireOp",EDGE,"E755"),sQuery(id+"F0.wireOp",EDGE,"E756"),sQuery(id+"F0.wireOp",EDGE,"E757"),sQuery(id+"F0.wireOp",EDGE,"E758"),sQuery(id+"F0.wireOp",EDGE,"E759"),sQuery(id+"F0.wireOp",EDGE,"E760"),sQuery(id+"F0.wireOp",EDGE,"E761"),sQuery(id+"F0.wireOp",EDGE,"E762"),sQuery(id+"F0.wireOp",EDGE,"E763"),sQuery(id+"F0.wireOp",EDGE,"E764"),sQuery(id+"F0.wireOp",EDGE,"E765"),sQuery(id+"F0.wireOp",EDGE,"E766"),sQuery(id+"F0.wireOp",EDGE,"E767"),sQuery(id+"F0.wireOp",EDGE,"E768"),sQuery(id+"F0.wireOp",EDGE,"E769"),sQuery(id+"F0.wireOp",EDGE,"E770"),sQuery(id+"F0.wireOp",EDGE,"E771"),sQuery(id+"F0.wireOp",EDGE,"E772"),sQuery(id+"F0.wireOp",EDGE,"E773"),sQuery(id+"F0.wireOp",EDGE,"E774"),sQuery(id+"F0.wireOp",EDGE,"E775"),sQuery(id+"F0.wireOp",EDGE,"E776"),sQuery(id+"F0.wireOp",EDGE,"E777"),sQuery(id+"F0.wireOp",EDGE,"E778"),sQuery(id+"F0.wireOp",EDGE,"E779"),sQuery(id+"F0.wireOp",EDGE,"E780"),sQuery(id+"F0.wireOp",EDGE,"E781"),sQuery(id+"F0.wireOp",EDGE,"E782"),sQuery(id+"F0.wireOp",EDGE,"E783"),sQuery(id+"F0.wireOp",EDGE,"E784"),sQuery(id+"F0.wireOp",EDGE,"E785"),sQuery(id+"F0.wireOp",EDGE,"E786"),sQuery(id+"F0.wireOp",EDGE,"E787"),sQuery(id+"F0.wireOp",EDGE,"E788"),sQuery(id+"F0.wireOp",EDGE,"E789"),sQuery(id+"F0.wireOp",EDGE,"E790"),sQuery(id+"F0.wireOp",EDGE,"E791"),sQuery(id+"F0.wireOp",EDGE,"E792"),sQuery(id+"F0.wireOp",EDGE,"E793"),sQuery(id+"F0.wireOp",EDGE,"E794"),sQuery(id+"F0.wireOp",EDGE,"E795"),sQuery(id+"F0.wireOp",EDGE,"E796"),sQuery(id+"F0.wireOp",EDGE,"E797"),sQuery(id+"F0.wireOp",EDGE,"E798"),sQuery(id+"F0.wireOp",EDGE,"E799"),sQuery(id+"F0.wireOp",EDGE,"E800"),sQuery(id+"F0.wireOp",EDGE,"E801"),sQuery(id+"F0.wireOp",EDGE,"E802"),sQuery(id+"F0.wireOp",EDGE,"E803"),sQuery(id+"F0.wireOp",EDGE,"E804"),sQuery(id+"F0.wireOp",EDGE,"E805"),sQuery(id+"F0.wireOp",EDGE,"E806"),sQuery(id+"F0.wireOp",EDGE,"E807"),sQuery(id+"F0.wireOp",EDGE,"E808"),sQuery(id+"F0.wireOp",EDGE,"E809"),sQuery(id+"F0.wireOp",EDGE,"E810"),sQuery(id+"F0.wireOp",EDGE,"E811"),sQuery(id+"F0.wireOp",EDGE,"E812"),sQuery(id+"F0.wireOp",EDGE,"E813"),sQuery(id+"F0.wireOp",EDGE,"E814"),sQuery(id+"F0.wireOp",EDGE,"E815"),sQuery(id+"F0.wireOp",EDGE,"E816"),sQuery(id+"F0.wireOp",EDGE,"E817"),sQuery(id+"F0.wireOp",EDGE,"E818"),sQuery(id+"F0.wireOp",EDGE,"E819"),sQuery(id+"F0.wireOp",EDGE,"E820"),sQuery(id+"F0.wireOp",EDGE,"E821"),sQuery(id+"F0.wireOp",EDGE,"E822"),sQuery(id+"F0.wireOp",EDGE,"E823"),sQuery(id+"F0.wireOp",EDGE,"E824"),sQuery(id+"F0.wireOp",EDGE,"E825"),sQuery(id+"F0.wireOp",EDGE,"E826"),sQuery(id+"F0.wireOp",EDGE,"E827"),sQuery(id+"F0.wireOp",EDGE,"E828"),sQuery(id+"F0.wireOp",EDGE,"E829"),sQuery(id+"F0.wireOp",EDGE,"E830"),sQuery(id+"F0.wireOp",EDGE,"E831"),sQuery(id+"F0.wireOp",EDGE,"E832"),sQuery(id+"F0.wireOp",EDGE,"E833"),sQuery(id+"F0.wireOp",EDGE,"E834"),sQuery(id+"F0.wireOp",EDGE,"E835"),sQuery(id+"F0.wireOp",EDGE,"E836"),sQuery(id+"F0.wireOp",EDGE,"E837"),sQuery(id+"F0.wireOp",EDGE,"E838"),sQuery(id+"F0.wireOp",EDGE,"E839"),sQuery(id+"F0.wireOp",EDGE,"E840"),sQuery(id+"F0.wireOp",EDGE,"E841"),sQuery(id+"F0.wireOp",EDGE,"E842"),sQuery(id+"F0.wireOp",EDGE,"E843"),sQuery(id+"F0.wireOp",EDGE,"E844"),sQuery(id+"F0.wireOp",EDGE,"E845"),sQuery(id+"F0.wireOp",EDGE,"E846"),sQuery(id+"F0.wireOp",EDGE,"E847"),sQuery(id+"F0.wireOp",EDGE,"E848"),sQuery(id+"F0.wireOp",EDGE,"E849"),sQuery(id+"F0.wireOp",EDGE,"E850"),sQuery(id+"F0.wireOp",EDGE,"E851"),sQuery(id+"F0.wireOp",EDGE,"E852"),sQuery(id+"F0.wireOp",EDGE,"E853"),sQuery(id+"F0.wireOp",EDGE,"E854"),sQuery(id+"F0.wireOp",EDGE,"E855"),sQuery(id+"F0.wireOp",EDGE,"E856"),sQuery(id+"F0.wireOp",EDGE,"E857"),sQuery(id+"F0.wireOp",EDGE,"E858"),sQuery(id+"F0.wireOp",EDGE,"E859"),sQuery(id+"F0.wireOp",EDGE,"E860"),sQuery(id+"F0.wireOp",EDGE,"E861"),sQuery(id+"F0.wireOp",EDGE,"E862"),sQuery(id+"F0.wireOp",EDGE,"E863"),sQuery(id+"F0.wireOp",EDGE,"E864"),sQuery(id+"F0.wireOp",EDGE,"E865"),sQuery(id+"F0.wireOp",EDGE,"E866"),sQuery(id+"F0.wireOp",EDGE,"E867"),sQuery(id+"F0.wireOp",EDGE,"E868"),sQuery(id+"F0.wireOp",EDGE,"E869"),sQuery(id+"F0.wireOp",EDGE,"E870"),sQuery(id+"F0.wireOp",EDGE,"E871"),sQuery(id+"F0.wireOp",EDGE,"E872"),sQuery(id+"F0.wireOp",EDGE,"E873"),sQuery(id+"F0.wireOp",EDGE,"E874"),sQuery(id+"F0.wireOp",EDGE,"E875"),sQuery(id+"F0.wireOp",EDGE,"E876"),sQuery(id+"F0.wireOp",EDGE,"E877"),sQuery(id+"F0.wireOp",EDGE,"E878"),sQuery(id+"F0.wireOp",EDGE,"E879"),sQuery(id+"F0.wireOp",EDGE,"E880"),sQuery(id+"F0.wireOp",EDGE,"E881"),sQuery(id+"F0.wireOp",EDGE,"E882"),sQuery(id+"F0.wireOp",EDGE,"E883"),sQuery(id+"F0.wireOp",EDGE,"E884"),sQuery(id+"F0.wireOp",EDGE,"E885"),sQuery(id+"F0.wireOp",EDGE,"E886"),sQuery(id+"F0.wireOp",EDGE,"E887"),sQuery(id+"F0.wireOp",EDGE,"E888"),sQuery(id+"F0.wireOp",EDGE,"E889"),sQuery(id+"F0.wireOp",EDGE,"E890"),sQuery(id+"F0.wireOp",EDGE,"E891"),sQuery(id+"F0.wireOp",EDGE,"E892"),sQuery(id+"F0.wireOp",EDGE,"E893"),sQuery(id+"F0.wireOp",EDGE,"E894"),sQuery(id+"F0.wireOp",EDGE,"E895"),sQuery(id+"F0.wireOp",EDGE,"E896"),sQuery(id+"F0.wireOp",EDGE,"E897"),sQuery(id+"F0.wireOp",EDGE,"E898"),sQuery(id+"F0.wireOp",EDGE,"E899"),sQuery(id+"F0.wireOp",EDGE,"E900"),sQuery(id+"F0.wireOp",EDGE,"E901"),sQuery(id+"F0.wireOp",EDGE,"E902"),sQuery(id+"F0.wireOp",EDGE,"E903"),sQuery(id+"F0.wireOp",EDGE,"E904"),sQuery(id+"F0.wireOp",EDGE,"E905"),sQuery(id+"F0.wireOp",EDGE,"E906"),sQuery(id+"F0.wireOp",EDGE,"E907"),sQuery(id+"F0.wireOp",EDGE,"E908"),sQuery(id+"F0.wireOp",EDGE,"E909"),sQuery(id+"F0.wireOp",EDGE,"E910"),sQuery(id+"F0.wireOp",EDGE,"E911"),sQuery(id+"F0.wireOp",EDGE,"E912"),sQuery(id+"F0.wireOp",EDGE,"E913"),sQuery(id+"F0.wireOp",EDGE,"E914"),sQuery(id+"F0.wireOp",EDGE,"E915"),sQuery(id+"F0.wireOp",EDGE,"E916"),sQuery(id+"F0.wireOp",EDGE,"E917"),sQuery(id+"F0.wireOp",EDGE,"E918"),sQuery(id+"F0.wireOp",EDGE,"E919"),sQuery(id+"F0.wireOp",EDGE,"E920"),sQuery(id+"F0.wireOp",EDGE,"E921"),sQuery(id+"F0.wireOp",EDGE,"E922"),sQuery(id+"F0.wireOp",EDGE,"E923"),sQuery(id+"F0.wireOp",EDGE,"E924"),sQuery(id+"F0.wireOp",EDGE,"E925"),sQuery(id+"F0.wireOp",EDGE,"E926"),sQuery(id+"F0.wireOp",EDGE,"E927"),sQuery(id+"F0.wireOp",EDGE,"E928"),sQuery(id+"F0.wireOp",EDGE,"E929"),sQuery(id+"F0.wireOp",EDGE,"E930"),sQuery(id+"F0.wireOp",EDGE,"E931"),sQuery(id+"F0.wireOp",EDGE,"E932"),sQuery(id+"F0.wireOp",EDGE,"E933"),sQuery(id+"F0.wireOp",EDGE,"E934"),sQuery(id+"F0.wireOp",EDGE,"E935"),sQuery(id+"F0.wireOp",EDGE,"E936"),sQuery(id+"F0.wireOp",EDGE,"E937"),sQuery(id+"F0.wireOp",EDGE,"E938"),sQuery(id+"F0.wireOp",EDGE,"E939"),sQuery(id+"F0.wireOp",EDGE,"E940"),sQuery(id+"F0.wireOp",EDGE,"E941"),sQuery(id+"F0.wireOp",EDGE,"E942"),sQuery(id+"F0.wireOp",EDGE,"E943"),sQuery(id+"F0.wireOp",EDGE,"E944"),sQuery(id+"F0.wireOp",EDGE,"E945"),sQuery(id+"F0.wireOp",EDGE,"E946"),sQuery(id+"F0.wireOp",EDGE,"E947"),sQuery(id+"F0.wireOp",EDGE,"E948"),sQuery(id+"F0.wireOp",EDGE,"E949"),sQuery(id+"F0.wireOp",EDGE,"E950"),sQuery(id+"F0.wireOp",EDGE,"E951"),sQuery(id+"F0.wireOp",EDGE,"E952"),sQuery(id+"F0.wireOp",EDGE,"E953"),sQuery(id+"F0.wireOp",EDGE,"E954"),sQuery(id+"F0.wireOp",EDGE,"E955"),sQuery(id+"F0.wireOp",EDGE,"E956"),sQuery(id+"F0.wireOp",EDGE,"E957"),sQuery(id+"F0.wireOp",EDGE,"E958"),sQuery(id+"F0.wireOp",EDGE,"E959"),sQuery(id+"F0.wireOp",EDGE,"E960"),sQuery(id+"F0.wireOp",EDGE,"E961"),sQuery(id+"F0.wireOp",EDGE,"E962"),sQuery(id+"F0.wireOp",EDGE,"E963"),sQuery(id+"F0.wireOp",EDGE,"E964"),sQuery(id+"F0.wireOp",EDGE,"E965"),sQuery(id+"F0.wireOp",EDGE,"E966"),sQuery(id+"F0.wireOp",EDGE,"E967"),sQuery(id+"F0.wireOp",EDGE,"E968"),sQuery(id+"F0.wireOp",EDGE,"E969"),sQuery(id+"F0.wireOp",EDGE,"E970"),sQuery(id+"F0.wireOp",EDGE,"E971"),sQuery(id+"F0.wireOp",EDGE,"E972"),sQuery(id+"F0.wireOp",EDGE,"E973"),sQuery(id+"F0.wireOp",EDGE,"E974"),sQuery(id+"F0.wireOp",EDGE,"E975"),sQuery(id+"F0.wireOp",EDGE,"E976"),sQuery(id+"F0.wireOp",EDGE,"E977"),sQuery(id+"F0.wireOp",EDGE,"E978"),sQuery(id+"F0.wireOp",EDGE,"E979"),sQuery(id+"F0.wireOp",EDGE,"E980"),sQuery(id+"F0.wireOp",EDGE,"E981"),sQuery(id+"F0.wireOp",EDGE,"E982"),sQuery(id+"F0.wireOp",EDGE,"E983"),sQuery(id+"F0.wireOp",EDGE,"E984"),sQuery(id+"F0.wireOp",EDGE,"E985"),sQuery(id+"F0.wireOp",EDGE,"E986"),sQuery(id+"F0.wireOp",EDGE,"E987"),sQuery(id+"F0.wireOp",EDGE,"E988"),sQuery(id+"F0.wireOp",EDGE,"E989"),sQuery(id+"F0.wireOp",EDGE,"E990"),sQuery(id+"F0.wireOp",EDGE,"E991"),sQuery(id+"F0.wireOp",EDGE,"E992"),sQuery(id+"F0.wireOp",EDGE,"E993"),sQuery(id+"F0.wireOp",EDGE,"E994"),sQuery(id+"F0.wireOp",EDGE,"E995"),sQuery(id+"F0.wireOp",EDGE,"E996"),sQuery(id+"F0.wireOp",EDGE,"E997"),sQuery(id+"F0.wireOp",EDGE,"E998"),sQuery(id+"F0.wireOp",EDGE,"E999"),sQuery(id+"F0.wireOp",EDGE,"E1000"),sQuery(id+"F0.wireOp",EDGE,"E1001"),sQuery(id+"F0.wireOp",EDGE,"E1002"),sQuery(id+"F0.wireOp",EDGE,"E1003"),sQuery(id+"F0.wireOp",EDGE,"E1004"),sQuery(id+"F0.wireOp",EDGE,"E1005"),sQuery(id+"F0.wireOp",EDGE,"E1006"),sQuery(id+"F0.wireOp",EDGE,"E1007"),sQuery(id+"F0.wireOp",EDGE,"E1008"),sQuery(id+"F0.wireOp",EDGE,"E1009"),sQuery(id+"F0.wireOp",EDGE,"E1010"),sQuery(id+"F0.wireOp",EDGE,"E1011"),sQuery(id+"F0.wireOp",EDGE,"E1012"),sQuery(id+"F0.wireOp",EDGE,"E1013"),sQuery(id+"F0.wireOp",EDGE,"E1014"),sQuery(id+"F0.wireOp",EDGE,"E1015"),sQuery(id+"F0.wireOp",EDGE,"E1016"),sQuery(id+"F0.wireOp",EDGE,"E1017"),sQuery(id+"F0.wireOp",EDGE,"E1018"),sQuery(id+"F0.wireOp",EDGE,"E1019"),sQuery(id+"F0.wireOp",EDGE,"E1020"),sQuery(id+"F0.wireOp",EDGE,"E1021"),sQuery(id+"F0.wireOp",EDGE,"E1022"),sQuery(id+"F0.wireOp",EDGE,"E1023"),sQuery(id+"F0.wireOp",EDGE,"E1024"),sQuery(id+"F0.wireOp",EDGE,"E1025"),sQuery(id+"F0.wireOp",EDGE,"E1026"),sQuery(id+"F0.wireOp",EDGE,"E1027"),sQuery(id+"F0.wireOp",EDGE,"E1028"),sQuery(id+"F0.wireOp",EDGE,"E1029"),sQuery(id+"F0.wireOp",EDGE,"E1030"),sQuery(id+"F0.wireOp",EDGE,"E1031"),sQuery(id+"F0.wireOp",EDGE,"E1032"),sQuery(id+"F0.wireOp",EDGE,"E1033"),sQuery(id+"F0.wireOp",EDGE,"E1034"),sQuery(id+"F0.wireOp",EDGE,"E1035"),sQuery(id+"F0.wireOp",EDGE,"E1036"),sQuery(id+"F0.wireOp",EDGE,"E1037"),sQuery(id+"F0.wireOp",EDGE,"E1038"),sQuery(id+"F0.wireOp",EDGE,"E1039"),sQuery(id+"F0.wireOp",EDGE,"E1040"),sQuery(id+"F0.wireOp",EDGE,"E1041"),sQuery(id+"F0.wireOp",EDGE,"E1042"),sQuery(id+"F0.wireOp",EDGE,"E1043"),sQuery(id+"F0.wireOp",EDGE,"E1044"),sQuery(id+"F0.wireOp",EDGE,"E1045"),sQuery(id+"F0.wireOp",EDGE,"E1046"),sQuery(id+"F0.wireOp",EDGE,"E1047"),sQuery(id+"F0.wireOp",EDGE,"E1048"),sQuery(id+"F0.wireOp",EDGE,"E1049"),sQuery(id+"F0.wireOp",EDGE,"E1050"),sQuery(id+"F0.wireOp",EDGE,"E1051"),sQuery(id+"F0.wireOp",EDGE,"E1052"),sQuery(id+"F0.wireOp",EDGE,"E1053"),sQuery(id+"F0.wireOp",EDGE,"E1054"),sQuery(id+"F0.wireOp",EDGE,"E1055"),sQuery(id+"F0.wireOp",EDGE,"E1056"),sQuery(id+"F0.wireOp",EDGE,"E1057"),sQuery(id+"F0.wireOp",EDGE,"E1058"),sQuery(id+"F0.wireOp",EDGE,"E1059"),sQuery(id+"F0.wireOp",EDGE,"E1060"),sQuery(id+"F0.wireOp",EDGE,"E1061"),sQuery(id+"F0.wireOp",EDGE,"E1062"),sQuery(id+"F0.wireOp",EDGE,"E1063"),sQuery(id+"F0.wireOp",EDGE,"E1064"),sQuery(id+"F0.wireOp",EDGE,"E1065"),sQuery(id+"F0.wireOp",EDGE,"E1066"),sQuery(id+"F0.wireOp",EDGE,"E1067"),sQuery(id+"F0.wireOp",EDGE,"E1068"),sQuery(id+"F0.wireOp",EDGE,"E1069"),sQuery(id+"F0.wireOp",EDGE,"E1070"),sQuery(id+"F0.wireOp",EDGE,"E1071"),sQuery(id+"F0.wireOp",EDGE,"E1072"),sQuery(id+"F0.wireOp",EDGE,"E1073"),sQuery(id+"F0.wireOp",EDGE,"E1074"),sQuery(id+"F0.wireOp",EDGE,"E1075"),sQuery(id+"F0.wireOp",EDGE,"E1076"),sQuery(id+"F0.wireOp",EDGE,"E1077"),sQuery(id+"F0.wireOp",EDGE,"E1078"),sQuery(id+"F0.wireOp",EDGE,"E1079"),sQuery(id+"F0.wireOp",EDGE,"E1080"),sQuery(id+"F0.wireOp",EDGE,"E1081"),sQuery(id+"F0.wireOp",EDGE,"E1082"),sQuery(id+"F0.wireOp",EDGE,"E1083"),sQuery(id+"F0.wireOp",EDGE,"E1084"),sQuery(id+"F0.wireOp",EDGE,"E1085"),sQuery(id+"F0.wireOp",EDGE,"E1086"),sQuery(id+"F0.wireOp",EDGE,"E1087"),sQuery(id+"F0.wireOp",EDGE,"E1088"),sQuery(id+"F0.wireOp",EDGE,"E1089"),sQuery(id+"F0.wireOp",EDGE,"E1090"),sQuery(id+"F0.wireOp",EDGE,"E1091"),sQuery(id+"F0.wireOp",EDGE,"E1092"),sQuery(id+"F0.wireOp",EDGE,"E1093"),sQuery(id+"F0.wireOp",EDGE,"E1094"),sQuery(id+"F0.wireOp",EDGE,"E1095"),sQuery(id+"F0.wireOp",EDGE,"E1096"),sQuery(id+"F0.wireOp",EDGE,"E1097"),sQuery(id+"F0.wireOp",EDGE,"E1098"),sQuery(id+"F0.wireOp",EDGE,"E1099"),sQuery(id+"F0.wireOp",EDGE,"E1100"),sQuery(id+"F0.wireOp",EDGE,"E1101"),sQuery(id+"F0.wireOp",EDGE,"E1102"),sQuery(id+"F0.wireOp",EDGE,"E1103"),sQuery(id+"F0.wireOp",EDGE,"E1104"),sQuery(id+"F0.wireOp",EDGE,"E1105"),sQuery(id+"F0.wireOp",EDGE,"E1106"),sQuery(id+"F0.wireOp",EDGE,"E1107"),sQuery(id+"F0.wireOp",EDGE,"E1108"),sQuery(id+"F0.wireOp",EDGE,"E1109"),sQuery(id+"F0.wireOp",EDGE,"E1110"),sQuery(id+"F0.wireOp",EDGE,"E1111"),sQuery(id+"F0.wireOp",EDGE,"E1112"),sQuery(id+"F0.wireOp",EDGE,"E1113"),sQuery(id+"F0.wireOp",EDGE,"E1114"),sQuery(id+"F0.wireOp",EDGE,"E1115"),sQuery(id+"F0.wireOp",EDGE,"E1116"),sQuery(id+"F0.wireOp",EDGE,"E1117"),sQuery(id+"F0.wireOp",EDGE,"E1118"),sQuery(id+"F0.wireOp",EDGE,"E1119"),sQuery(id+"F0.wireOp",EDGE,"E1120"),sQuery(id+"F0.wireOp",EDGE,"E1121"),sQuery(id+"F0.wireOp",EDGE,"E1122"),sQuery(id+"F0.wireOp",EDGE,"E1123"),sQuery(id+"F0.wireOp",EDGE,"E1124"),sQuery(id+"F0.wireOp",EDGE,"E1125"),sQuery(id+"F0.wireOp",EDGE,"E1126"),sQuery(id+"F0.wireOp",EDGE,"E1127"),sQuery(id+"F0.wireOp",EDGE,"E1128"),sQuery(id+"F0.wireOp",EDGE,"E1129"),sQuery(id+"F0.wireOp",EDGE,"E1130"),sQuery(id+"F0.wireOp",EDGE,"E1131"),sQuery(id+"F0.wireOp",EDGE,"E1132"),sQuery(id+"F0.wireOp",EDGE,"E1133"),sQuery(id+"F0.wireOp",EDGE,"E1134"),sQuery(id+"F0.wireOp",EDGE,"E1135"),sQuery(id+"F0.wireOp",EDGE,"E1136"),sQuery(id+"F0.wireOp",EDGE,"E1137"),sQuery(id+"F0.wireOp",EDGE,"E1138"),sQuery(id+"F0.wireOp",EDGE,"E1139"),sQuery(id+"F0.wireOp",EDGE,"E1140"),sQuery(id+"F0.wireOp",EDGE,"E1141"),sQuery(id+"F0.wireOp",EDGE,"E1142"),sQuery(id+"F0.wireOp",EDGE,"E1143"),sQuery(id+"F0.wireOp",EDGE,"E1144"),sQuery(id+"F0.wireOp",EDGE,"E1145"),sQuery(id+"F0.wireOp",EDGE,"E1146"),sQuery(id+"F0.wireOp",EDGE,"E1147"),sQuery(id+"F0.wireOp",EDGE,"E1148"),sQuery(id+"F0.wireOp",EDGE,"E1149"),sQuery(id+"F0.wireOp",EDGE,"E1150"),sQuery(id+"F0.wireOp",EDGE,"E1151"),sQuery(id+"F0.wireOp",EDGE,"E1152"),sQuery(id+"F0.wireOp",EDGE,"E1153"),sQuery(id+"F0.wireOp",EDGE,"E1154"),sQuery(id+"F0.wireOp",EDGE,"E1155"),sQuery(id+"F0.wireOp",EDGE,"E1156"),sQuery(id+"F0.wireOp",EDGE,"E1157"),sQuery(id+"F0.wireOp",EDGE,"E1158"),sQuery(id+"F0.wireOp",EDGE,"E1159"),sQuery(id+"F0.wireOp",EDGE,"E1160"),sQuery(id+"F0.wireOp",EDGE,"E1161"),sQuery(id+"F0.wireOp",EDGE,"E1162"),sQuery(id+"F0.wireOp",EDGE,"E1163"),sQuery(id+"F0.wireOp",EDGE,"E1164"),sQuery(id+"F0.wireOp",EDGE,"E1165"),sQuery(id+"F0.wireOp",EDGE,"E1166"),sQuery(id+"F0.wireOp",EDGE,"E1167"),sQuery(id+"F0.wireOp",EDGE,"E1168"),sQuery(id+"F0.wireOp",EDGE,"E1169"),sQuery(id+"F0.wireOp",EDGE,"E1170"),sQuery(id+"F0.wireOp",EDGE,"E1171"),sQuery(id+"F0.wireOp",EDGE,"E1172"),sQuery(id+"F0.wireOp",EDGE,"E1173"),sQuery(id+"F0.wireOp",EDGE,"E1174"),sQuery(id+"F0.wireOp",EDGE,"E1175"),sQuery(id+"F0.wireOp",EDGE,"E1176"),sQuery(id+"F0.wireOp",EDGE,"E1177"),sQuery(id+"F0.wireOp",EDGE,"E1178"),sQuery(id+"F0.wireOp",EDGE,"E1179"),sQuery(id+"F0.wireOp",EDGE,"E1180"),sQuery(id+"F0.wireOp",EDGE,"E1181"),sQuery(id+"F0.wireOp",EDGE,"E1182"),sQuery(id+"F0.wireOp",EDGE,"E1183"),sQuery(id+"F0.wireOp",EDGE,"E1184"),sQuery(id+"F0.wireOp",EDGE,"E1185"),sQuery(id+"F0.wireOp",EDGE,"E1186"),sQuery(id+"F0.wireOp",EDGE,"E1187"),sQuery(id+"F0.wireOp",EDGE,"E1188"),sQuery(id+"F0.wireOp",EDGE,"E1189"),sQuery(id+"F0.wireOp",EDGE,"E1190"),sQuery(id+"F0.wireOp",EDGE,"E1191"),sQuery(id+"F0.wireOp",EDGE,"E1192"),sQuery(id+"F0.wireOp",EDGE,"E1193"),sQuery(id+"F0.wireOp",EDGE,"E1194"),sQuery(id+"F0.wireOp",EDGE,"E1195"),sQuery(id+"F0.wireOp",EDGE,"E1196"),sQuery(id+"F0.wireOp",EDGE,"E1197"),sQuery(id+"F0.wireOp",EDGE,"E1198"),sQuery(id+"F0.wireOp",EDGE,"E1199"),sQuery(id+"F0.wireOp",EDGE,"E1200"),sQuery(id+"F0.wireOp",EDGE,"E1201"),sQuery(id+"F0.wireOp",EDGE,"E1202"),sQuery(id+"F0.wireOp",EDGE,"E1203"),sQuery(id+"F0.wireOp",EDGE,"E1204"),sQuery(id+"F0.wireOp",EDGE,"E1205"),sQuery(id+"F0.wireOp",EDGE,"E1206"),sQuery(id+"F0.wireOp",EDGE,"E1207"),sQuery(id+"F0.wireOp",EDGE,"E1208"),sQuery(id+"F0.wireOp",EDGE,"E1209"),sQuery(id+"F0.wireOp",EDGE,"E1210"),sQuery(id+"F0.wireOp",EDGE,"E1211"),sQuery(id+"F0.wireOp",EDGE,"E1212"),sQuery(id+"F0.wireOp",EDGE,"E1213"),sQuery(id+"F0.wireOp",EDGE,"E1214"),sQuery(id+"F0.wireOp",EDGE,"E1215"),sQuery(id+"F0.wireOp",EDGE,"E1216"),sQuery(id+"F0.wireOp",EDGE,"E1217"),sQuery(id+"F0.wireOp",EDGE,"E1218"),sQuery(id+"F0.wireOp",EDGE,"E1219"),sQuery(id+"F0.wireOp",EDGE,"E1220"),sQuery(id+"F0.wireOp",EDGE,"E1221"),sQuery(id+"F0.wireOp",EDGE,"E1222"),sQuery(id+"F0.wireOp",EDGE,"E1223"),sQuery(id+"F0.wireOp",EDGE,"E1224"),sQuery(id+"F0.wireOp",EDGE,"E1225"),sQuery(id+"F0.wireOp",EDGE,"E1226"),sQuery(id+"F0.wireOp",EDGE,"E1227"),sQuery(id+"F0.wireOp",EDGE,"E1228"),sQuery(id+"F0.wireOp",EDGE,"E1229"),sQuery(id+"F0.wireOp",EDGE,"E1230"),sQuery(id+"F0.wireOp",EDGE,"E1231"),sQuery(id+"F0.wireOp",EDGE,"E1232"),sQuery(id+"F0.wireOp",EDGE,"E1233"),sQuery(id+"F0.wireOp",EDGE,"E1234"),sQuery(id+"F0.wireOp",EDGE,"E1235"),sQuery(id+"F0.wireOp",EDGE,"E1236"),sQuery(id+"F0.wireOp",EDGE,"E1237"),sQuery(id+"F0.wireOp",EDGE,"E1238"),sQuery(id+"F0.wireOp",EDGE,"E1239"),sQuery(id+"F0.wireOp",EDGE,"E1240"),sQuery(id+"F0.wireOp",EDGE,"E1241"),sQuery(id+"F0.wireOp",EDGE,"E1242"),sQuery(id+"F0.wireOp",EDGE,"E1243"),sQuery(id+"F0.wireOp",EDGE,"E1244"),sQuery(id+"F0.wireOp",EDGE,"E1245"),sQuery(id+"F0.wireOp",EDGE,"E1246"),sQuery(id+"F0.wireOp",EDGE,"E1247"),sQuery(id+"F0.wireOp",EDGE,"E1248"),sQuery(id+"F0.wireOp",EDGE,"E1249"),sQuery(id+"F0.wireOp",EDGE,"E1250"),sQuery(id+"F0.wireOp",EDGE,"E1251"),sQuery(id+"F0.wireOp",EDGE,"E1252"),sQuery(id+"F0.wireOp",EDGE,"E1253"),sQuery(id+"F0.wireOp",EDGE,"E1254"),sQuery(id+"F0.wireOp",EDGE,"E1255"),sQuery(id+"F0.wireOp",EDGE,"E1256"),sQuery(id+"F0.wireOp",EDGE,"E1257"),sQuery(id+"F0.wireOp",EDGE,"E1258"),sQuery(id+"F0.wireOp",EDGE,"E1259"),sQuery(id+"F0.wireOp",EDGE,"E1260"),sQuery(id+"F0.wireOp",EDGE,"E1261"),sQuery(id+"F0.wireOp",EDGE,"E1262"),sQuery(id+"F0.wireOp",EDGE,"E1263"),sQuery(id+"F0.wireOp",EDGE,"E1264"),sQuery(id+"F0.wireOp",EDGE,"E1265"),sQuery(id+"F0.wireOp",EDGE,"E1266"),sQuery(id+"F0.wireOp",EDGE,"E1267"),sQuery(id+"F0.wireOp",EDGE,"E1268"),sQuery(id+"F0.wireOp",EDGE,"E1269"),sQuery(id+"F0.wireOp",EDGE,"E1270"),sQuery(id+"F0.wireOp",EDGE,"E1271"),sQuery(id+"F0.wireOp",EDGE,"E1272"),sQuery(id+"F0.wireOp",EDGE,"E1273"),sQuery(id+"F0.wireOp",EDGE,"E1274"),sQuery(id+"F0.wireOp",EDGE,"E1275"),sQuery(id+"F0.wireOp",EDGE,"E1276"),sQuery(id+"F0.wireOp",EDGE,"E1277"),sQuery(id+"F0.wireOp",EDGE,"E1278"),sQuery(id+"F0.wireOp",EDGE,"E1279"),sQuery(id+"F0.wireOp",EDGE,"E1280"),sQuery(id+"F0.wireOp",EDGE,"E1281"),sQuery(id+"F0.wireOp",EDGE,"E1282"),sQuery(id+"F0.wireOp",EDGE,"E1283"),sQuery(id+"F0.wireOp",EDGE,"E1284"),sQuery(id+"F0.wireOp",EDGE,"E1285"),sQuery(id+"F0.wireOp",EDGE,"E1286"),sQuery(id+"F0.wireOp",EDGE,"E1287"),sQuery(id+"F0.wireOp",EDGE,"E1288"),sQuery(id+"F0.wireOp",EDGE,"E1289"),sQuery(id+"F0.wireOp",EDGE,"E1290"),sQuery(id+"F0.wireOp",EDGE,"E1291"),sQuery(id+"F0.wireOp",EDGE,"E1292"),sQuery(id+"F0.wireOp",EDGE,"E1293"),sQuery(id+"F0.wireOp",EDGE,"E1294"),sQuery(id+"F0.wireOp",EDGE,"E1295"),sQuery(id+"F0.wireOp",EDGE,"E1296"),sQuery(id+"F0.wireOp",EDGE,"E1297"),sQuery(id+"F0.wireOp",EDGE,"E1298"),sQuery(id+"F0.wireOp",EDGE,"E1299"),sQuery(id+"F0.wireOp",EDGE,"E1300"),sQuery(id+"F0.wireOp",EDGE,"E1301"),sQuery(id+"F0.wireOp",EDGE,"E1302"),sQuery(id+"F0.wireOp",EDGE,"E1303"),sQuery(id+"F0.wireOp",EDGE,"E1304"),sQuery(id+"F0.wireOp",EDGE,"E1305"),sQuery(id+"F0.wireOp",EDGE,"E1306"),sQuery(id+"F0.wireOp",EDGE,"E1307"),sQuery(id+"F0.wireOp",EDGE,"E1308"),sQuery(id+"F0.wireOp",EDGE,"E1309"),sQuery(id+"F0.wireOp",EDGE,"E1310"),sQuery(id+"F0.wireOp",EDGE,"E1311"),sQuery(id+"F0.wireOp",EDGE,"E1312"),sQuery(id+"F0.wireOp",EDGE,"E1313"),sQuery(id+"F0.wireOp",EDGE,"E1314"),sQuery(id+"F0.wireOp",EDGE,"E1315"),sQuery(id+"F0.wireOp",EDGE,"E1316"),sQuery(id+"F0.wireOp",EDGE,"E1317"),sQuery(id+"F0.wireOp",EDGE,"E1318"),sQuery(id+"F0.wireOp",EDGE,"E1319"),sQuery(id+"F0.wireOp",EDGE,"E1320"),sQuery(id+"F0.wireOp",EDGE,"E1321"),sQuery(id+"F0.wireOp",EDGE,"E1322"),sQuery(id+"F0.wireOp",EDGE,"E1323"),sQuery(id+"F0.wireOp",EDGE,"E1324"),sQuery(id+"F0.wireOp",EDGE,"E1325"),sQuery(id+"F0.wireOp",EDGE,"E1326"),sQuery(id+"F0.wireOp",EDGE,"E1327"),sQuery(id+"F0.wireOp",EDGE,"E1328"),sQuery(id+"F0.wireOp",EDGE,"E1329"),sQuery(id+"F0.wireOp",EDGE,"E1330"),sQuery(id+"F0.wireOp",EDGE,"E1331"),sQuery(id+"F0.wireOp",EDGE,"E1332"),sQuery(id+"F0.wireOp",EDGE,"E1333"),sQuery(id+"F0.wireOp",EDGE,"E1334"),sQuery(id+"F0.wireOp",EDGE,"E1335"),sQuery(id+"F0.wireOp",EDGE,"E1336"),sQuery(id+"F0.wireOp",EDGE,"E1337"),sQuery(id+"F0.wireOp",EDGE,"E1338"),sQuery(id+"F0.wireOp",EDGE,"E1339"),sQuery(id+"F0.wireOp",EDGE,"E1340"),sQuery(id+"F0.wireOp",EDGE,"E1341"),sQuery(id+"F0.wireOp",EDGE,"E1342"),sQuery(id+"F0.wireOp",EDGE,"E1343"),sQuery(id+"F0.wireOp",EDGE,"E1344"),sQuery(id+"F0.wireOp",EDGE,"E1345"),sQuery(id+"F0.wireOp",EDGE,"E1346"),sQuery(id+"F0.wireOp",EDGE,"E1347"),sQuery(id+"F0.wireOp",EDGE,"E1348"),sQuery(id+"F0.wireOp",EDGE,"E1349"),sQuery(id+"F0.wireOp",EDGE,"E1350"),sQuery(id+"F0.wireOp",EDGE,"E1351"),sQuery(id+"F0.wireOp",EDGE,"E1352"),sQuery(id+"F0.wireOp",EDGE,"E1353"),sQuery(id+"F0.wireOp",EDGE,"E1354"),sQuery(id+"F0.wireOp",EDGE,"E1355"),sQuery(id+"F0.wireOp",EDGE,"E1356"),sQuery(id+"F0.wireOp",EDGE,"E1357"),sQuery(id+"F0.wireOp",EDGE,"E1358"),sQuery(id+"F0.wireOp",EDGE,"E1359"),sQuery(id+"F0.wireOp",EDGE,"E1360"),sQuery(id+"F0.wireOp",EDGE,"E1361"),sQuery(id+"F0.wireOp",EDGE,"E1362"),sQuery(id+"F0.wireOp",EDGE,"E1363"),sQuery(id+"F0.wireOp",EDGE,"E1364"),sQuery(id+"F0.wireOp",EDGE,"E1365"),sQuery(id+"F0.wireOp",EDGE,"E1366"),sQuery(id+"F0.wireOp",EDGE,"E1367"),sQuery(id+"F0.wireOp",EDGE,"E1368"),sQuery(id+"F0.wireOp",EDGE,"E1369"),sQuery(id+"F0.wireOp",EDGE,"E1370"),sQuery(id+"F0.wireOp",EDGE,"E1371"),sQuery(id+"F0.wireOp",EDGE,"E1372"),sQuery(id+"F0.wireOp",EDGE,"E1373"),sQuery(id+"F0.wireOp",EDGE,"E1374"),sQuery(id+"F0.wireOp",EDGE,"E1375"),sQuery(id+"F0.wireOp",EDGE,"E1376"),sQuery(id+"F0.wireOp",EDGE,"E1377"),sQuery(id+"F0.wireOp",EDGE,"E1378"),sQuery(id+"F0.wireOp",EDGE,"E1379"),sQuery(id+"F0.wireOp",EDGE,"E1380"),sQuery(id+"F0.wireOp",EDGE,"E1381"),sQuery(id+"F0.wireOp",EDGE,"E1382"),sQuery(id+"F0.wireOp",EDGE,"E1383"),sQuery(id+"F0.wireOp",EDGE,"E1384"),sQuery(id+"F0.wireOp",EDGE,"E1385"),sQuery(id+"F0.wireOp",EDGE,"E1386"),sQuery(id+"F0.wireOp",EDGE,"E1387"),sQuery(id+"F0.wireOp",EDGE,"E1388"),sQuery(id+"F0.wireOp",EDGE,"E1389"),sQuery(id+"F0.wireOp",EDGE,"E1390"),sQuery(id+"F0.wireOp",EDGE,"E1391"),sQuery(id+"F0.wireOp",EDGE,"E1392"),sQuery(id+"F0.wireOp",EDGE,"E1393"),sQuery(id+"F0.wireOp",EDGE,"E1394"),sQuery(id+"F0.wireOp",EDGE,"E1395"),sQuery(id+"F0.wireOp",EDGE,"E1396"),sQuery(id+"F0.wireOp",EDGE,"E1397"),sQuery(id+"F0.wireOp",EDGE,"E1398"),sQuery(id+"F0.wireOp",EDGE,"E1399"),sQuery(id+"F0.wireOp",EDGE,"E1400"),sQuery(id+"F0.wireOp",EDGE,"E1401")])]});
            booleanBodies(context, id + "F4", {"operationType" : BooleanOperationType.SUBTRACTION, "tools" : qUnion([Q0, Q1, Q2, Q3]), "targets" : qUnion([Q4])});
        }
    });
